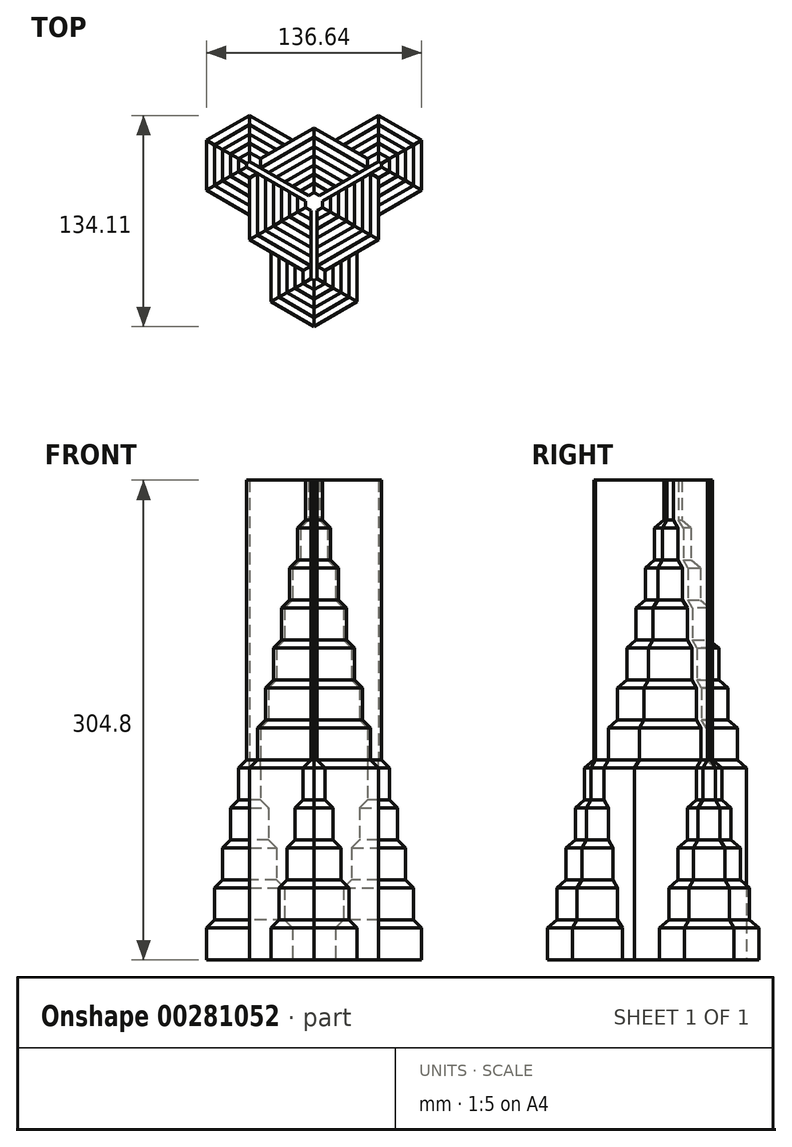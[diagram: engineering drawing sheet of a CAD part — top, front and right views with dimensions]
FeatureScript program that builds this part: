
annotation { "Feature Type Name" : "Feature", "Feature Type Description" : "" }
export const myFeature = defineFeature(function(context is Context, id is Id, definition is map)
    precondition{}
    {
        {
            var Q0;
            Q0=qCreatedBy(makeId("Top.planeOp"),FACE);
            var sketch = newSketch(context, id + "F0", { "sketchPlane" : qUnion([Q0])});
            skCircle(sketch, "E0.cCircle", {"center": v(0, 0) * mm, "radius": 41 * mm, "construction": true});
            skLineSegment(sketch, "E0.0", {"start": v(41, 23.67) * mm, "end": v(41, -23.67) * mm});
            skLineSegment(sketch, "E0.1", {"start": v(41, -23.67) * mm, "end": v(0, -47.33) * mm});
            skLineSegment(sketch, "E0.2", {"start": v(0, -47.33) * mm, "end": v(-41, -23.67) * mm});
            skLineSegment(sketch, "E0.3", {"start": v(-41, -23.67) * mm, "end": v(-41, 23.67) * mm});
            skLineSegment(sketch, "E0.4", {"start": v(-41, 23.67) * mm, "end": v(0, 47.33) * mm});
            skLineSegment(sketch, "E0.5", {"start": v(0, 47.33) * mm, "end": v(41, 23.67) * mm});
            skPoint(sketch, "E0.0.midPoint", {"position": v(41, 0) * mm});
            skCircle(sketch, "E1.cCircle", {"center": v(-41, 23.67) * mm, "radius": 27.33 * mm, "construction": true});
            skLineSegment(sketch, "E1.0", {"start": v(-13.66, 7.89) * mm, "end": v(-41, -7.89) * mm});
            skLineSegment(sketch, "E1.1", {"start": v(-41, -7.89) * mm, "end": v(-68.32, 7.89) * mm});
            skLineSegment(sketch, "E1.2", {"start": v(-68.32, 7.89) * mm, "end": v(-68.32, 39.44) * mm});
            skLineSegment(sketch, "E1.3", {"start": v(-68.32, 39.44) * mm, "end": v(-41, 55.22) * mm});
            skLineSegment(sketch, "E1.4", {"start": v(-41, 55.22) * mm, "end": v(-13.66, 39.44) * mm});
            skLineSegment(sketch, "E1.5", {"start": v(-13.66, 39.44) * mm, "end": v(-13.66, 7.89) * mm});
            skPoint(sketch, "E1.0.midPoint", {"position": v(-27.33, 0) * mm});
            skCircle(sketch, "E2.cCircle", {"center": v(41, 23.67) * mm, "radius": 27.33 * mm, "construction": true});
            skLineSegment(sketch, "E2.0", {"start": v(41, -7.89) * mm, "end": v(13.66, 7.89) * mm});
            skLineSegment(sketch, "E2.1", {"start": v(13.66, 7.89) * mm, "end": v(13.66, 39.44) * mm});
            skLineSegment(sketch, "E2.2", {"start": v(13.66, 39.44) * mm, "end": v(41, 55.22) * mm});
            skLineSegment(sketch, "E2.3", {"start": v(41, 55.22) * mm, "end": v(68.32, 39.44) * mm});
            skLineSegment(sketch, "E2.4", {"start": v(68.32, 39.44) * mm, "end": v(68.32, 7.89) * mm});
            skLineSegment(sketch, "E2.5", {"start": v(68.32, 7.89) * mm, "end": v(41, -7.89) * mm});
            skPoint(sketch, "E2.0.midPoint", {"position": v(27.33, 0) * mm});
            skCircle(sketch, "E3.cCircle", {"center": v(0, -47.33) * mm, "radius": 27.33 * mm, "construction": true});
            skLineSegment(sketch, "E3.0", {"start": v(0, -15.78) * mm, "end": v(27.33, -31.55) * mm});
            skLineSegment(sketch, "E3.1", {"start": v(27.33, -31.55) * mm, "end": v(27.33, -63.1) * mm});
            skLineSegment(sketch, "E3.2", {"start": v(27.33, -63.1) * mm, "end": v(0, -78.89) * mm});
            skLineSegment(sketch, "E3.3", {"start": v(0, -78.89) * mm, "end": v(-27.33, -63.1) * mm});
            skLineSegment(sketch, "E3.4", {"start": v(-27.33, -63.1) * mm, "end": v(-27.33, -31.55) * mm});
            skLineSegment(sketch, "E3.5", {"start": v(-27.33, -31.55) * mm, "end": v(0, -15.78) * mm});
            skPoint(sketch, "E3.0.midPoint", {"position": v(13.66, -23.67) * mm});
            skSolve(sketch);
        }
        {
            var Q0;
            Q0 = qSketchRegion(id + "F0", true);
            extrude(context, id + "F1", {"entities" : qUnion([Q0]), "depth" : 25.4 * mm});
        }
        {
            var Q0;
            Q0=makeQuery(id+"F1.opExtrude","CAP_EDGE",EDGE,{"disambiguationData":[OSD([sQuery(id+"F0.wireOp",EDGE,"E1.1")])],"isStart":false});
            var Q1;
            Q1=makeQuery(id+"F1.opExtrude","CAP_EDGE",EDGE,{"disambiguationData":[OSD([sQuery(id+"F0.wireOp",EDGE,"E3.4")])],"isStart":false});
            var Q2;
            Q2=makeQuery(id+"F1.opExtrude","CAP_EDGE",EDGE,{"disambiguationData":[OSD([sQuery(id+"F0.wireOp",EDGE,"E3.3")])],"isStart":false});
            var Q3;
            Q3=makeQuery(id+"F1.opExtrude","CAP_EDGE",EDGE,{"disambiguationData":[OSD([sQuery(id+"F0.wireOp",EDGE,"E3.2")])],"isStart":false});
            var Q4;
            Q4=makeQuery(id+"F1.opExtrude","CAP_EDGE",EDGE,{"disambiguationData":[OSD([sQuery(id+"F0.wireOp",EDGE,"E3.1")])],"isStart":false});
            var Q5;
            Q5=makeQuery(id+"F1.opExtrude","CAP_EDGE",EDGE,{"disambiguationData":[OSD([sQuery(id+"F0.wireOp",EDGE,"E2.5")])],"isStart":false});
            var Q6;
            Q6=makeQuery(id+"F1.opExtrude","CAP_EDGE",EDGE,{"disambiguationData":[OSD([sQuery(id+"F0.wireOp",EDGE,"E2.4")])],"isStart":false});
            var Q7;
            Q7=makeQuery(id+"F1.opExtrude","CAP_EDGE",EDGE,{"disambiguationData":[OSD([sQuery(id+"F0.wireOp",EDGE,"E2.3")])],"isStart":false});
            var Q8;
            Q8=makeQuery(id+"F1.opExtrude","CAP_EDGE",EDGE,{"disambiguationData":[OSD([sQuery(id+"F0.wireOp",EDGE,"E2.2")])],"isStart":false});
            var Q9;
            Q9=makeQuery(id+"F1.opExtrude","CAP_EDGE",EDGE,{"disambiguationData":[OSD([sQuery(id+"F0.wireOp",EDGE,"E1.4")])],"isStart":false});
            var Q10;
            Q10=makeQuery(id+"F1.opExtrude","CAP_EDGE",EDGE,{"disambiguationData":[OSD([sQuery(id+"F0.wireOp",EDGE,"E1.3")])],"isStart":false});
            var Q11;
            Q11=makeQuery(id+"F1.opExtrude","CAP_EDGE",EDGE,{"disambiguationData":[OSD([sQuery(id+"F0.wireOp",EDGE,"E1.2")])],"isStart":false});
            chamfer(context, id + "F2", {"entities" : qUnion([Q0, Q1, Q2, Q3, Q4, Q5, Q6, Q7, Q8, Q9, Q10, Q11]), "width" : 5.08 * mm, "tangentPropagation" : true});
        }
        {
            var Q0;
            Q0=makeQuery(id+"F1.opExtrude","CAP_FACE",FACE,{"disambiguationData":[OSD([sQuery(id+"F0.wireOp",EDGE,"E0.0"),sQuery(id+"F0.wireOp",EDGE,"E0.1"),sQuery(id+"F0.wireOp",EDGE,"E0.2"),sQuery(id+"F0.wireOp",EDGE,"E0.3"),sQuery(id+"F0.wireOp",EDGE,"E0.4"),sQuery(id+"F0.wireOp",EDGE,"E0.5"),sQuery(id+"F0.wireOp",EDGE,"E1.1"),sQuery(id+"F0.wireOp",EDGE,"E1.2"),sQuery(id+"F0.wireOp",EDGE,"E1.3"),sQuery(id+"F0.wireOp",EDGE,"E1.4"),sQuery(id+"F0.wireOp",EDGE,"E2.2"),sQuery(id+"F0.wireOp",EDGE,"E2.3"),sQuery(id+"F0.wireOp",EDGE,"E2.4"),sQuery(id+"F0.wireOp",EDGE,"E2.5"),sQuery(id+"F0.wireOp",EDGE,"E3.1"),sQuery(id+"F0.wireOp",EDGE,"E3.2"),sQuery(id+"F0.wireOp",EDGE,"E3.3"),sQuery(id+"F0.wireOp",EDGE,"E3.4")])],"isStart":false});
            extrude(context, id + "F3", {"entities" : qUnion([Q0]), "operationType" : NewBodyOperationType.ADD, "depth" : 25.4 * mm});
        }
        {
            var Q0;
            {var subQ0=sQuery(id+"F0.wireOp",EDGE,"E3.4");var subQ1=sQuery(id+"F0.wireOp",EDGE,"E3.3");var subQ2=sQuery(id+"F0.wireOp",EDGE,"E3.2");var subQ3=sQuery(id+"F0.wireOp",EDGE,"E3.1");var subQ4=sQuery(id+"F0.wireOp",EDGE,"E2.5");var subQ5=sQuery(id+"F0.wireOp",EDGE,"E2.4");var subQ6=sQuery(id+"F0.wireOp",EDGE,"E2.3");var subQ7=sQuery(id+"F0.wireOp",EDGE,"E2.2");var subQ8=sQuery(id+"F0.wireOp",EDGE,"E1.4");var subQ9=sQuery(id+"F0.wireOp",EDGE,"E1.3");var subQ10=sQuery(id+"F0.wireOp",EDGE,"E1.2");var subQ11=sQuery(id+"F0.wireOp",EDGE,"E1.1");var subQ12=sQuery(id+"F0.wireOp",EDGE,"E0.5");var subQ13=sQuery(id+"F0.wireOp",EDGE,"E0.4");var subQ14=sQuery(id+"F0.wireOp",EDGE,"E0.3");var subQ15=sQuery(id+"F0.wireOp",EDGE,"E0.2");var subQ16=sQuery(id+"F0.wireOp",EDGE,"E0.1");var subQ17=sQuery(id+"F0.wireOp",EDGE,"E0.0");Q0=makeQuery(id+"F3.opExtrude","CAP_EDGE",EDGE,{"disambiguationData":[OSD([subQ17,subQ16,subQ15,subQ14,subQ13,subQ12,subQ11,subQ10,subQ9,subQ8,subQ7,subQ6,subQ5,subQ4,subQ3,subQ2,subQ1,subQ0]),TDD([makeQuery(id+"F2.opChamfer","BLEND_EDGE",EDGE,{"blendedFrom":[makeQuery(id+"F1.opExtrude","CAP_EDGE",EDGE,{"disambiguationData":[OSD([subQ3])],"isStart":false}),makeQuery(id+"F1.opExtrude","CAP_FACE",FACE,{"disambiguationData":[OSD([subQ17,subQ16,subQ15,subQ14,subQ13,subQ12,subQ11,subQ10,subQ9,subQ8,subQ7,subQ6,subQ5,subQ4,subQ3,subQ2,subQ1,subQ0])],"isStart":false})],"blendedInto":[makeQuery(id+"F1.opExtrude","CAP_FACE",FACE,{"disambiguationData":[OSD([subQ17,subQ16,subQ15,subQ14,subQ13,subQ12,subQ11,subQ10,subQ9,subQ8,subQ7,subQ6,subQ5,subQ4,subQ3,subQ2,subQ1,subQ0])],"isStart":false})]})])],"isStart":false});}
            var Q1;
            {var subQ0=sQuery(id+"F0.wireOp",EDGE,"E3.4");var subQ1=sQuery(id+"F0.wireOp",EDGE,"E3.3");var subQ2=sQuery(id+"F0.wireOp",EDGE,"E3.2");var subQ3=sQuery(id+"F0.wireOp",EDGE,"E3.1");var subQ4=sQuery(id+"F0.wireOp",EDGE,"E2.5");var subQ5=sQuery(id+"F0.wireOp",EDGE,"E2.4");var subQ6=sQuery(id+"F0.wireOp",EDGE,"E2.3");var subQ7=sQuery(id+"F0.wireOp",EDGE,"E2.2");var subQ8=sQuery(id+"F0.wireOp",EDGE,"E1.4");var subQ9=sQuery(id+"F0.wireOp",EDGE,"E1.3");var subQ10=sQuery(id+"F0.wireOp",EDGE,"E1.2");var subQ11=sQuery(id+"F0.wireOp",EDGE,"E1.1");var subQ12=sQuery(id+"F0.wireOp",EDGE,"E0.5");var subQ13=sQuery(id+"F0.wireOp",EDGE,"E0.4");var subQ14=sQuery(id+"F0.wireOp",EDGE,"E0.3");var subQ15=sQuery(id+"F0.wireOp",EDGE,"E0.2");var subQ16=sQuery(id+"F0.wireOp",EDGE,"E0.1");var subQ17=sQuery(id+"F0.wireOp",EDGE,"E0.0");Q1=makeQuery(id+"F3.opExtrude","CAP_EDGE",EDGE,{"disambiguationData":[OSD([subQ17,subQ16,subQ15,subQ14,subQ13,subQ12,subQ11,subQ10,subQ9,subQ8,subQ7,subQ6,subQ5,subQ4,subQ3,subQ2,subQ1,subQ0]),TDD([makeQuery(id+"F2.opChamfer","BLEND_EDGE",EDGE,{"blendedFrom":[makeQuery(id+"F1.opExtrude","CAP_EDGE",EDGE,{"disambiguationData":[OSD([subQ2])],"isStart":false}),makeQuery(id+"F1.opExtrude","CAP_FACE",FACE,{"disambiguationData":[OSD([subQ17,subQ16,subQ15,subQ14,subQ13,subQ12,subQ11,subQ10,subQ9,subQ8,subQ7,subQ6,subQ5,subQ4,subQ3,subQ2,subQ1,subQ0])],"isStart":false})],"blendedInto":[makeQuery(id+"F1.opExtrude","CAP_FACE",FACE,{"disambiguationData":[OSD([subQ17,subQ16,subQ15,subQ14,subQ13,subQ12,subQ11,subQ10,subQ9,subQ8,subQ7,subQ6,subQ5,subQ4,subQ3,subQ2,subQ1,subQ0])],"isStart":false})]})])],"isStart":false});}
            var Q2;
            {var subQ0=sQuery(id+"F0.wireOp",EDGE,"E3.4");var subQ1=sQuery(id+"F0.wireOp",EDGE,"E3.3");var subQ2=sQuery(id+"F0.wireOp",EDGE,"E3.2");var subQ3=sQuery(id+"F0.wireOp",EDGE,"E3.1");var subQ4=sQuery(id+"F0.wireOp",EDGE,"E2.5");var subQ5=sQuery(id+"F0.wireOp",EDGE,"E2.4");var subQ6=sQuery(id+"F0.wireOp",EDGE,"E2.3");var subQ7=sQuery(id+"F0.wireOp",EDGE,"E2.2");var subQ8=sQuery(id+"F0.wireOp",EDGE,"E1.4");var subQ9=sQuery(id+"F0.wireOp",EDGE,"E1.3");var subQ10=sQuery(id+"F0.wireOp",EDGE,"E1.2");var subQ11=sQuery(id+"F0.wireOp",EDGE,"E1.1");var subQ12=sQuery(id+"F0.wireOp",EDGE,"E0.5");var subQ13=sQuery(id+"F0.wireOp",EDGE,"E0.4");var subQ14=sQuery(id+"F0.wireOp",EDGE,"E0.3");var subQ15=sQuery(id+"F0.wireOp",EDGE,"E0.2");var subQ16=sQuery(id+"F0.wireOp",EDGE,"E0.1");var subQ17=sQuery(id+"F0.wireOp",EDGE,"E0.0");Q2=makeQuery(id+"F3.opExtrude","CAP_EDGE",EDGE,{"disambiguationData":[OSD([subQ17,subQ16,subQ15,subQ14,subQ13,subQ12,subQ11,subQ10,subQ9,subQ8,subQ7,subQ6,subQ5,subQ4,subQ3,subQ2,subQ1,subQ0]),TDD([makeQuery(id+"F2.opChamfer","BLEND_EDGE",EDGE,{"blendedFrom":[makeQuery(id+"F1.opExtrude","CAP_EDGE",EDGE,{"disambiguationData":[OSD([subQ1])],"isStart":false}),makeQuery(id+"F1.opExtrude","CAP_FACE",FACE,{"disambiguationData":[OSD([subQ17,subQ16,subQ15,subQ14,subQ13,subQ12,subQ11,subQ10,subQ9,subQ8,subQ7,subQ6,subQ5,subQ4,subQ3,subQ2,subQ1,subQ0])],"isStart":false})],"blendedInto":[makeQuery(id+"F1.opExtrude","CAP_FACE",FACE,{"disambiguationData":[OSD([subQ17,subQ16,subQ15,subQ14,subQ13,subQ12,subQ11,subQ10,subQ9,subQ8,subQ7,subQ6,subQ5,subQ4,subQ3,subQ2,subQ1,subQ0])],"isStart":false})]})])],"isStart":false});}
            var Q3;
            {var subQ0=sQuery(id+"F0.wireOp",EDGE,"E3.4");var subQ1=sQuery(id+"F0.wireOp",EDGE,"E3.3");var subQ2=sQuery(id+"F0.wireOp",EDGE,"E3.2");var subQ3=sQuery(id+"F0.wireOp",EDGE,"E3.1");var subQ4=sQuery(id+"F0.wireOp",EDGE,"E2.5");var subQ5=sQuery(id+"F0.wireOp",EDGE,"E2.4");var subQ6=sQuery(id+"F0.wireOp",EDGE,"E2.3");var subQ7=sQuery(id+"F0.wireOp",EDGE,"E2.2");var subQ8=sQuery(id+"F0.wireOp",EDGE,"E1.4");var subQ9=sQuery(id+"F0.wireOp",EDGE,"E1.3");var subQ10=sQuery(id+"F0.wireOp",EDGE,"E1.2");var subQ11=sQuery(id+"F0.wireOp",EDGE,"E1.1");var subQ12=sQuery(id+"F0.wireOp",EDGE,"E0.5");var subQ13=sQuery(id+"F0.wireOp",EDGE,"E0.4");var subQ14=sQuery(id+"F0.wireOp",EDGE,"E0.3");var subQ15=sQuery(id+"F0.wireOp",EDGE,"E0.2");var subQ16=sQuery(id+"F0.wireOp",EDGE,"E0.1");var subQ17=sQuery(id+"F0.wireOp",EDGE,"E0.0");Q3=makeQuery(id+"F3.opExtrude","CAP_EDGE",EDGE,{"disambiguationData":[OSD([subQ17,subQ16,subQ15,subQ14,subQ13,subQ12,subQ11,subQ10,subQ9,subQ8,subQ7,subQ6,subQ5,subQ4,subQ3,subQ2,subQ1,subQ0]),TDD([makeQuery(id+"F2.opChamfer","BLEND_EDGE",EDGE,{"blendedFrom":[makeQuery(id+"F1.opExtrude","CAP_EDGE",EDGE,{"disambiguationData":[OSD([subQ0])],"isStart":false}),makeQuery(id+"F1.opExtrude","CAP_FACE",FACE,{"disambiguationData":[OSD([subQ17,subQ16,subQ15,subQ14,subQ13,subQ12,subQ11,subQ10,subQ9,subQ8,subQ7,subQ6,subQ5,subQ4,subQ3,subQ2,subQ1,subQ0])],"isStart":false})],"blendedInto":[makeQuery(id+"F1.opExtrude","CAP_FACE",FACE,{"disambiguationData":[OSD([subQ17,subQ16,subQ15,subQ14,subQ13,subQ12,subQ11,subQ10,subQ9,subQ8,subQ7,subQ6,subQ5,subQ4,subQ3,subQ2,subQ1,subQ0])],"isStart":false})]})])],"isStart":false});}
            var Q4;
            {var subQ0=sQuery(id+"F0.wireOp",EDGE,"E3.4");var subQ1=sQuery(id+"F0.wireOp",EDGE,"E3.3");var subQ2=sQuery(id+"F0.wireOp",EDGE,"E3.2");var subQ3=sQuery(id+"F0.wireOp",EDGE,"E3.1");var subQ4=sQuery(id+"F0.wireOp",EDGE,"E2.5");var subQ5=sQuery(id+"F0.wireOp",EDGE,"E2.4");var subQ6=sQuery(id+"F0.wireOp",EDGE,"E2.3");var subQ7=sQuery(id+"F0.wireOp",EDGE,"E2.2");var subQ8=sQuery(id+"F0.wireOp",EDGE,"E1.4");var subQ9=sQuery(id+"F0.wireOp",EDGE,"E1.3");var subQ10=sQuery(id+"F0.wireOp",EDGE,"E1.2");var subQ11=sQuery(id+"F0.wireOp",EDGE,"E1.1");var subQ12=sQuery(id+"F0.wireOp",EDGE,"E0.5");var subQ13=sQuery(id+"F0.wireOp",EDGE,"E0.4");var subQ14=sQuery(id+"F0.wireOp",EDGE,"E0.3");var subQ15=sQuery(id+"F0.wireOp",EDGE,"E0.2");var subQ16=sQuery(id+"F0.wireOp",EDGE,"E0.1");var subQ17=sQuery(id+"F0.wireOp",EDGE,"E0.0");Q4=makeQuery(id+"F3.opExtrude","CAP_EDGE",EDGE,{"disambiguationData":[OSD([subQ17,subQ16,subQ15,subQ14,subQ13,subQ12,subQ11,subQ10,subQ9,subQ8,subQ7,subQ6,subQ5,subQ4,subQ3,subQ2,subQ1,subQ0]),TDD([makeQuery(id+"F2.opChamfer","BLEND_EDGE",EDGE,{"blendedFrom":[makeQuery(id+"F1.opExtrude","CAP_EDGE",EDGE,{"disambiguationData":[OSD([subQ11])],"isStart":false}),makeQuery(id+"F1.opExtrude","CAP_FACE",FACE,{"disambiguationData":[OSD([subQ17,subQ16,subQ15,subQ14,subQ13,subQ12,subQ11,subQ10,subQ9,subQ8,subQ7,subQ6,subQ5,subQ4,subQ3,subQ2,subQ1,subQ0])],"isStart":false})],"blendedInto":[makeQuery(id+"F1.opExtrude","CAP_FACE",FACE,{"disambiguationData":[OSD([subQ17,subQ16,subQ15,subQ14,subQ13,subQ12,subQ11,subQ10,subQ9,subQ8,subQ7,subQ6,subQ5,subQ4,subQ3,subQ2,subQ1,subQ0])],"isStart":false})]})])],"isStart":false});}
            var Q5;
            {var subQ0=sQuery(id+"F0.wireOp",EDGE,"E3.4");var subQ1=sQuery(id+"F0.wireOp",EDGE,"E3.3");var subQ2=sQuery(id+"F0.wireOp",EDGE,"E3.2");var subQ3=sQuery(id+"F0.wireOp",EDGE,"E3.1");var subQ4=sQuery(id+"F0.wireOp",EDGE,"E2.5");var subQ5=sQuery(id+"F0.wireOp",EDGE,"E2.4");var subQ6=sQuery(id+"F0.wireOp",EDGE,"E2.3");var subQ7=sQuery(id+"F0.wireOp",EDGE,"E2.2");var subQ8=sQuery(id+"F0.wireOp",EDGE,"E1.4");var subQ9=sQuery(id+"F0.wireOp",EDGE,"E1.3");var subQ10=sQuery(id+"F0.wireOp",EDGE,"E1.2");var subQ11=sQuery(id+"F0.wireOp",EDGE,"E1.1");var subQ12=sQuery(id+"F0.wireOp",EDGE,"E0.5");var subQ13=sQuery(id+"F0.wireOp",EDGE,"E0.4");var subQ14=sQuery(id+"F0.wireOp",EDGE,"E0.3");var subQ15=sQuery(id+"F0.wireOp",EDGE,"E0.2");var subQ16=sQuery(id+"F0.wireOp",EDGE,"E0.1");var subQ17=sQuery(id+"F0.wireOp",EDGE,"E0.0");Q5=makeQuery(id+"F3.opExtrude","CAP_EDGE",EDGE,{"disambiguationData":[OSD([subQ17,subQ16,subQ15,subQ14,subQ13,subQ12,subQ11,subQ10,subQ9,subQ8,subQ7,subQ6,subQ5,subQ4,subQ3,subQ2,subQ1,subQ0]),TDD([makeQuery(id+"F2.opChamfer","BLEND_EDGE",EDGE,{"blendedFrom":[makeQuery(id+"F1.opExtrude","CAP_EDGE",EDGE,{"disambiguationData":[OSD([subQ10])],"isStart":false}),makeQuery(id+"F1.opExtrude","CAP_FACE",FACE,{"disambiguationData":[OSD([subQ17,subQ16,subQ15,subQ14,subQ13,subQ12,subQ11,subQ10,subQ9,subQ8,subQ7,subQ6,subQ5,subQ4,subQ3,subQ2,subQ1,subQ0])],"isStart":false})],"blendedInto":[makeQuery(id+"F1.opExtrude","CAP_FACE",FACE,{"disambiguationData":[OSD([subQ17,subQ16,subQ15,subQ14,subQ13,subQ12,subQ11,subQ10,subQ9,subQ8,subQ7,subQ6,subQ5,subQ4,subQ3,subQ2,subQ1,subQ0])],"isStart":false})]})])],"isStart":false});}
            var Q6;
            {var subQ0=sQuery(id+"F0.wireOp",EDGE,"E3.4");var subQ1=sQuery(id+"F0.wireOp",EDGE,"E3.3");var subQ2=sQuery(id+"F0.wireOp",EDGE,"E3.2");var subQ3=sQuery(id+"F0.wireOp",EDGE,"E3.1");var subQ4=sQuery(id+"F0.wireOp",EDGE,"E2.5");var subQ5=sQuery(id+"F0.wireOp",EDGE,"E2.4");var subQ6=sQuery(id+"F0.wireOp",EDGE,"E2.3");var subQ7=sQuery(id+"F0.wireOp",EDGE,"E2.2");var subQ8=sQuery(id+"F0.wireOp",EDGE,"E1.4");var subQ9=sQuery(id+"F0.wireOp",EDGE,"E1.3");var subQ10=sQuery(id+"F0.wireOp",EDGE,"E1.2");var subQ11=sQuery(id+"F0.wireOp",EDGE,"E1.1");var subQ12=sQuery(id+"F0.wireOp",EDGE,"E0.5");var subQ13=sQuery(id+"F0.wireOp",EDGE,"E0.4");var subQ14=sQuery(id+"F0.wireOp",EDGE,"E0.3");var subQ15=sQuery(id+"F0.wireOp",EDGE,"E0.2");var subQ16=sQuery(id+"F0.wireOp",EDGE,"E0.1");var subQ17=sQuery(id+"F0.wireOp",EDGE,"E0.0");Q6=makeQuery(id+"F3.opExtrude","CAP_EDGE",EDGE,{"disambiguationData":[OSD([subQ17,subQ16,subQ15,subQ14,subQ13,subQ12,subQ11,subQ10,subQ9,subQ8,subQ7,subQ6,subQ5,subQ4,subQ3,subQ2,subQ1,subQ0]),TDD([makeQuery(id+"F2.opChamfer","BLEND_EDGE",EDGE,{"blendedFrom":[makeQuery(id+"F1.opExtrude","CAP_EDGE",EDGE,{"disambiguationData":[OSD([subQ9])],"isStart":false}),makeQuery(id+"F1.opExtrude","CAP_FACE",FACE,{"disambiguationData":[OSD([subQ17,subQ16,subQ15,subQ14,subQ13,subQ12,subQ11,subQ10,subQ9,subQ8,subQ7,subQ6,subQ5,subQ4,subQ3,subQ2,subQ1,subQ0])],"isStart":false})],"blendedInto":[makeQuery(id+"F1.opExtrude","CAP_FACE",FACE,{"disambiguationData":[OSD([subQ17,subQ16,subQ15,subQ14,subQ13,subQ12,subQ11,subQ10,subQ9,subQ8,subQ7,subQ6,subQ5,subQ4,subQ3,subQ2,subQ1,subQ0])],"isStart":false})]})])],"isStart":false});}
            var Q7;
            {var subQ0=sQuery(id+"F0.wireOp",EDGE,"E3.4");var subQ1=sQuery(id+"F0.wireOp",EDGE,"E3.3");var subQ2=sQuery(id+"F0.wireOp",EDGE,"E3.2");var subQ3=sQuery(id+"F0.wireOp",EDGE,"E3.1");var subQ4=sQuery(id+"F0.wireOp",EDGE,"E2.5");var subQ5=sQuery(id+"F0.wireOp",EDGE,"E2.4");var subQ6=sQuery(id+"F0.wireOp",EDGE,"E2.3");var subQ7=sQuery(id+"F0.wireOp",EDGE,"E2.2");var subQ8=sQuery(id+"F0.wireOp",EDGE,"E1.4");var subQ9=sQuery(id+"F0.wireOp",EDGE,"E1.3");var subQ10=sQuery(id+"F0.wireOp",EDGE,"E1.2");var subQ11=sQuery(id+"F0.wireOp",EDGE,"E1.1");var subQ12=sQuery(id+"F0.wireOp",EDGE,"E0.5");var subQ13=sQuery(id+"F0.wireOp",EDGE,"E0.4");var subQ14=sQuery(id+"F0.wireOp",EDGE,"E0.3");var subQ15=sQuery(id+"F0.wireOp",EDGE,"E0.2");var subQ16=sQuery(id+"F0.wireOp",EDGE,"E0.1");var subQ17=sQuery(id+"F0.wireOp",EDGE,"E0.0");Q7=makeQuery(id+"F3.opExtrude","CAP_EDGE",EDGE,{"disambiguationData":[OSD([subQ17,subQ16,subQ15,subQ14,subQ13,subQ12,subQ11,subQ10,subQ9,subQ8,subQ7,subQ6,subQ5,subQ4,subQ3,subQ2,subQ1,subQ0]),TDD([makeQuery(id+"F2.opChamfer","BLEND_EDGE",EDGE,{"blendedFrom":[makeQuery(id+"F1.opExtrude","CAP_EDGE",EDGE,{"disambiguationData":[OSD([subQ8])],"isStart":false}),makeQuery(id+"F1.opExtrude","CAP_FACE",FACE,{"disambiguationData":[OSD([subQ17,subQ16,subQ15,subQ14,subQ13,subQ12,subQ11,subQ10,subQ9,subQ8,subQ7,subQ6,subQ5,subQ4,subQ3,subQ2,subQ1,subQ0])],"isStart":false})],"blendedInto":[makeQuery(id+"F1.opExtrude","CAP_FACE",FACE,{"disambiguationData":[OSD([subQ17,subQ16,subQ15,subQ14,subQ13,subQ12,subQ11,subQ10,subQ9,subQ8,subQ7,subQ6,subQ5,subQ4,subQ3,subQ2,subQ1,subQ0])],"isStart":false})]})])],"isStart":false});}
            var Q8;
            {var subQ0=sQuery(id+"F0.wireOp",EDGE,"E3.4");var subQ1=sQuery(id+"F0.wireOp",EDGE,"E3.3");var subQ2=sQuery(id+"F0.wireOp",EDGE,"E3.2");var subQ3=sQuery(id+"F0.wireOp",EDGE,"E3.1");var subQ4=sQuery(id+"F0.wireOp",EDGE,"E2.5");var subQ5=sQuery(id+"F0.wireOp",EDGE,"E2.4");var subQ6=sQuery(id+"F0.wireOp",EDGE,"E2.3");var subQ7=sQuery(id+"F0.wireOp",EDGE,"E2.2");var subQ8=sQuery(id+"F0.wireOp",EDGE,"E1.4");var subQ9=sQuery(id+"F0.wireOp",EDGE,"E1.3");var subQ10=sQuery(id+"F0.wireOp",EDGE,"E1.2");var subQ11=sQuery(id+"F0.wireOp",EDGE,"E1.1");var subQ12=sQuery(id+"F0.wireOp",EDGE,"E0.5");var subQ13=sQuery(id+"F0.wireOp",EDGE,"E0.4");var subQ14=sQuery(id+"F0.wireOp",EDGE,"E0.3");var subQ15=sQuery(id+"F0.wireOp",EDGE,"E0.2");var subQ16=sQuery(id+"F0.wireOp",EDGE,"E0.1");var subQ17=sQuery(id+"F0.wireOp",EDGE,"E0.0");Q8=makeQuery(id+"F3.opExtrude","CAP_EDGE",EDGE,{"disambiguationData":[OSD([subQ17,subQ16,subQ15,subQ14,subQ13,subQ12,subQ11,subQ10,subQ9,subQ8,subQ7,subQ6,subQ5,subQ4,subQ3,subQ2,subQ1,subQ0]),TDD([makeQuery(id+"F2.opChamfer","BLEND_EDGE",EDGE,{"blendedFrom":[makeQuery(id+"F1.opExtrude","CAP_EDGE",EDGE,{"disambiguationData":[OSD([subQ7])],"isStart":false}),makeQuery(id+"F1.opExtrude","CAP_FACE",FACE,{"disambiguationData":[OSD([subQ17,subQ16,subQ15,subQ14,subQ13,subQ12,subQ11,subQ10,subQ9,subQ8,subQ7,subQ6,subQ5,subQ4,subQ3,subQ2,subQ1,subQ0])],"isStart":false})],"blendedInto":[makeQuery(id+"F1.opExtrude","CAP_FACE",FACE,{"disambiguationData":[OSD([subQ17,subQ16,subQ15,subQ14,subQ13,subQ12,subQ11,subQ10,subQ9,subQ8,subQ7,subQ6,subQ5,subQ4,subQ3,subQ2,subQ1,subQ0])],"isStart":false})]})])],"isStart":false});}
            var Q9;
            {var subQ0=sQuery(id+"F0.wireOp",EDGE,"E3.4");var subQ1=sQuery(id+"F0.wireOp",EDGE,"E3.3");var subQ2=sQuery(id+"F0.wireOp",EDGE,"E3.2");var subQ3=sQuery(id+"F0.wireOp",EDGE,"E3.1");var subQ4=sQuery(id+"F0.wireOp",EDGE,"E2.5");var subQ5=sQuery(id+"F0.wireOp",EDGE,"E2.4");var subQ6=sQuery(id+"F0.wireOp",EDGE,"E2.3");var subQ7=sQuery(id+"F0.wireOp",EDGE,"E2.2");var subQ8=sQuery(id+"F0.wireOp",EDGE,"E1.4");var subQ9=sQuery(id+"F0.wireOp",EDGE,"E1.3");var subQ10=sQuery(id+"F0.wireOp",EDGE,"E1.2");var subQ11=sQuery(id+"F0.wireOp",EDGE,"E1.1");var subQ12=sQuery(id+"F0.wireOp",EDGE,"E0.5");var subQ13=sQuery(id+"F0.wireOp",EDGE,"E0.4");var subQ14=sQuery(id+"F0.wireOp",EDGE,"E0.3");var subQ15=sQuery(id+"F0.wireOp",EDGE,"E0.2");var subQ16=sQuery(id+"F0.wireOp",EDGE,"E0.1");var subQ17=sQuery(id+"F0.wireOp",EDGE,"E0.0");Q9=makeQuery(id+"F3.opExtrude","CAP_EDGE",EDGE,{"disambiguationData":[OSD([subQ17,subQ16,subQ15,subQ14,subQ13,subQ12,subQ11,subQ10,subQ9,subQ8,subQ7,subQ6,subQ5,subQ4,subQ3,subQ2,subQ1,subQ0]),TDD([makeQuery(id+"F2.opChamfer","BLEND_EDGE",EDGE,{"blendedFrom":[makeQuery(id+"F1.opExtrude","CAP_EDGE",EDGE,{"disambiguationData":[OSD([subQ6])],"isStart":false}),makeQuery(id+"F1.opExtrude","CAP_FACE",FACE,{"disambiguationData":[OSD([subQ17,subQ16,subQ15,subQ14,subQ13,subQ12,subQ11,subQ10,subQ9,subQ8,subQ7,subQ6,subQ5,subQ4,subQ3,subQ2,subQ1,subQ0])],"isStart":false})],"blendedInto":[makeQuery(id+"F1.opExtrude","CAP_FACE",FACE,{"disambiguationData":[OSD([subQ17,subQ16,subQ15,subQ14,subQ13,subQ12,subQ11,subQ10,subQ9,subQ8,subQ7,subQ6,subQ5,subQ4,subQ3,subQ2,subQ1,subQ0])],"isStart":false})]})])],"isStart":false});}
            var Q10;
            {var subQ0=sQuery(id+"F0.wireOp",EDGE,"E3.4");var subQ1=sQuery(id+"F0.wireOp",EDGE,"E3.3");var subQ2=sQuery(id+"F0.wireOp",EDGE,"E3.2");var subQ3=sQuery(id+"F0.wireOp",EDGE,"E3.1");var subQ4=sQuery(id+"F0.wireOp",EDGE,"E2.5");var subQ5=sQuery(id+"F0.wireOp",EDGE,"E2.4");var subQ6=sQuery(id+"F0.wireOp",EDGE,"E2.3");var subQ7=sQuery(id+"F0.wireOp",EDGE,"E2.2");var subQ8=sQuery(id+"F0.wireOp",EDGE,"E1.4");var subQ9=sQuery(id+"F0.wireOp",EDGE,"E1.3");var subQ10=sQuery(id+"F0.wireOp",EDGE,"E1.2");var subQ11=sQuery(id+"F0.wireOp",EDGE,"E1.1");var subQ12=sQuery(id+"F0.wireOp",EDGE,"E0.5");var subQ13=sQuery(id+"F0.wireOp",EDGE,"E0.4");var subQ14=sQuery(id+"F0.wireOp",EDGE,"E0.3");var subQ15=sQuery(id+"F0.wireOp",EDGE,"E0.2");var subQ16=sQuery(id+"F0.wireOp",EDGE,"E0.1");var subQ17=sQuery(id+"F0.wireOp",EDGE,"E0.0");Q10=makeQuery(id+"F3.opExtrude","CAP_EDGE",EDGE,{"disambiguationData":[OSD([subQ17,subQ16,subQ15,subQ14,subQ13,subQ12,subQ11,subQ10,subQ9,subQ8,subQ7,subQ6,subQ5,subQ4,subQ3,subQ2,subQ1,subQ0]),TDD([makeQuery(id+"F2.opChamfer","BLEND_EDGE",EDGE,{"blendedFrom":[makeQuery(id+"F1.opExtrude","CAP_EDGE",EDGE,{"disambiguationData":[OSD([subQ5])],"isStart":false}),makeQuery(id+"F1.opExtrude","CAP_FACE",FACE,{"disambiguationData":[OSD([subQ17,subQ16,subQ15,subQ14,subQ13,subQ12,subQ11,subQ10,subQ9,subQ8,subQ7,subQ6,subQ5,subQ4,subQ3,subQ2,subQ1,subQ0])],"isStart":false})],"blendedInto":[makeQuery(id+"F1.opExtrude","CAP_FACE",FACE,{"disambiguationData":[OSD([subQ17,subQ16,subQ15,subQ14,subQ13,subQ12,subQ11,subQ10,subQ9,subQ8,subQ7,subQ6,subQ5,subQ4,subQ3,subQ2,subQ1,subQ0])],"isStart":false})]})])],"isStart":false});}
            var Q11;
            {var subQ0=sQuery(id+"F0.wireOp",EDGE,"E3.4");var subQ1=sQuery(id+"F0.wireOp",EDGE,"E3.3");var subQ2=sQuery(id+"F0.wireOp",EDGE,"E3.2");var subQ3=sQuery(id+"F0.wireOp",EDGE,"E3.1");var subQ4=sQuery(id+"F0.wireOp",EDGE,"E2.5");var subQ5=sQuery(id+"F0.wireOp",EDGE,"E2.4");var subQ6=sQuery(id+"F0.wireOp",EDGE,"E2.3");var subQ7=sQuery(id+"F0.wireOp",EDGE,"E2.2");var subQ8=sQuery(id+"F0.wireOp",EDGE,"E1.4");var subQ9=sQuery(id+"F0.wireOp",EDGE,"E1.3");var subQ10=sQuery(id+"F0.wireOp",EDGE,"E1.2");var subQ11=sQuery(id+"F0.wireOp",EDGE,"E1.1");var subQ12=sQuery(id+"F0.wireOp",EDGE,"E0.5");var subQ13=sQuery(id+"F0.wireOp",EDGE,"E0.4");var subQ14=sQuery(id+"F0.wireOp",EDGE,"E0.3");var subQ15=sQuery(id+"F0.wireOp",EDGE,"E0.2");var subQ16=sQuery(id+"F0.wireOp",EDGE,"E0.1");var subQ17=sQuery(id+"F0.wireOp",EDGE,"E0.0");Q11=makeQuery(id+"F3.opExtrude","CAP_EDGE",EDGE,{"disambiguationData":[OSD([subQ17,subQ16,subQ15,subQ14,subQ13,subQ12,subQ11,subQ10,subQ9,subQ8,subQ7,subQ6,subQ5,subQ4,subQ3,subQ2,subQ1,subQ0]),TDD([makeQuery(id+"F2.opChamfer","BLEND_EDGE",EDGE,{"blendedFrom":[makeQuery(id+"F1.opExtrude","CAP_EDGE",EDGE,{"disambiguationData":[OSD([subQ4])],"isStart":false}),makeQuery(id+"F1.opExtrude","CAP_FACE",FACE,{"disambiguationData":[OSD([subQ17,subQ16,subQ15,subQ14,subQ13,subQ12,subQ11,subQ10,subQ9,subQ8,subQ7,subQ6,subQ5,subQ4,subQ3,subQ2,subQ1,subQ0])],"isStart":false})],"blendedInto":[makeQuery(id+"F1.opExtrude","CAP_FACE",FACE,{"disambiguationData":[OSD([subQ17,subQ16,subQ15,subQ14,subQ13,subQ12,subQ11,subQ10,subQ9,subQ8,subQ7,subQ6,subQ5,subQ4,subQ3,subQ2,subQ1,subQ0])],"isStart":false})]})])],"isStart":false});}
            chamfer(context, id + "F4", {"entities" : qUnion([Q0, Q1, Q2, Q3, Q4, Q5, Q6, Q7, Q8, Q9, Q10, Q11]), "width" : 5.08 * mm, "tangentPropagation" : true});
        }
        {
            var Q0;
            Q0=makeQuery(id+"F3.opExtrude","CAP_FACE",FACE,{"disambiguationData":[OSD([sQuery(id+"F0.wireOp",EDGE,"E0.0"),sQuery(id+"F0.wireOp",EDGE,"E0.1"),sQuery(id+"F0.wireOp",EDGE,"E0.2"),sQuery(id+"F0.wireOp",EDGE,"E0.3"),sQuery(id+"F0.wireOp",EDGE,"E0.4"),sQuery(id+"F0.wireOp",EDGE,"E0.5"),sQuery(id+"F0.wireOp",EDGE,"E1.1"),sQuery(id+"F0.wireOp",EDGE,"E1.2"),sQuery(id+"F0.wireOp",EDGE,"E1.3"),sQuery(id+"F0.wireOp",EDGE,"E1.4"),sQuery(id+"F0.wireOp",EDGE,"E2.2"),sQuery(id+"F0.wireOp",EDGE,"E2.3"),sQuery(id+"F0.wireOp",EDGE,"E2.4"),sQuery(id+"F0.wireOp",EDGE,"E2.5"),sQuery(id+"F0.wireOp",EDGE,"E3.1"),sQuery(id+"F0.wireOp",EDGE,"E3.2"),sQuery(id+"F0.wireOp",EDGE,"E3.3"),sQuery(id+"F0.wireOp",EDGE,"E3.4")])],"isStart":false});
            extrude(context, id + "F5", {"entities" : qUnion([Q0]), "operationType" : NewBodyOperationType.ADD, "depth" : 25.4 * mm});
        }
        {
            var Q0;
            {var subQ0=sQuery(id+"F0.wireOp",EDGE,"E3.4");var subQ1=sQuery(id+"F0.wireOp",EDGE,"E3.3");var subQ2=sQuery(id+"F0.wireOp",EDGE,"E3.2");var subQ3=sQuery(id+"F0.wireOp",EDGE,"E3.1");var subQ4=sQuery(id+"F0.wireOp",EDGE,"E2.5");var subQ5=sQuery(id+"F0.wireOp",EDGE,"E2.4");var subQ6=sQuery(id+"F0.wireOp",EDGE,"E2.3");var subQ7=sQuery(id+"F0.wireOp",EDGE,"E2.2");var subQ8=sQuery(id+"F0.wireOp",EDGE,"E1.4");var subQ9=sQuery(id+"F0.wireOp",EDGE,"E1.3");var subQ10=sQuery(id+"F0.wireOp",EDGE,"E1.2");var subQ11=sQuery(id+"F0.wireOp",EDGE,"E1.1");var subQ12=sQuery(id+"F0.wireOp",EDGE,"E0.5");var subQ13=sQuery(id+"F0.wireOp",EDGE,"E0.4");var subQ14=sQuery(id+"F0.wireOp",EDGE,"E0.3");var subQ15=sQuery(id+"F0.wireOp",EDGE,"E0.2");var subQ16=sQuery(id+"F0.wireOp",EDGE,"E0.1");var subQ17=sQuery(id+"F0.wireOp",EDGE,"E0.0");Q0=makeQuery(id+"F5.opExtrude","CAP_EDGE",EDGE,{"disambiguationData":[OSD([subQ17,subQ16,subQ15,subQ14,subQ13,subQ12,subQ11,subQ10,subQ9,subQ8,subQ7,subQ6,subQ5,subQ4,subQ3,subQ2,subQ1,subQ0]),TDD([makeQuery(id+"F4.opChamfer","BLEND_EDGE",EDGE,{"blendedFrom":[makeQuery(id+"F3.opExtrude","CAP_EDGE",EDGE,{"disambiguationData":[OSD([subQ17,subQ16,subQ15,subQ14,subQ13,subQ12,subQ11,subQ10,subQ9,subQ8,subQ7,subQ6,subQ5,subQ4,subQ3,subQ2,subQ1,subQ0]),TDD([makeQuery(id+"F2.opChamfer","BLEND_EDGE",EDGE,{"blendedFrom":[makeQuery(id+"F1.opExtrude","CAP_EDGE",EDGE,{"disambiguationData":[OSD([subQ8])],"isStart":false}),makeQuery(id+"F1.opExtrude","CAP_FACE",FACE,{"disambiguationData":[OSD([subQ17,subQ16,subQ15,subQ14,subQ13,subQ12,subQ11,subQ10,subQ9,subQ8,subQ7,subQ6,subQ5,subQ4,subQ3,subQ2,subQ1,subQ0])],"isStart":false})],"blendedInto":[makeQuery(id+"F1.opExtrude","CAP_FACE",FACE,{"disambiguationData":[OSD([subQ17,subQ16,subQ15,subQ14,subQ13,subQ12,subQ11,subQ10,subQ9,subQ8,subQ7,subQ6,subQ5,subQ4,subQ3,subQ2,subQ1,subQ0])],"isStart":false})]})])],"isStart":false}),makeQuery(id+"F3.opExtrude","CAP_FACE",FACE,{"disambiguationData":[OSD([subQ17,subQ16,subQ15,subQ14,subQ13,subQ12,subQ11,subQ10,subQ9,subQ8,subQ7,subQ6,subQ5,subQ4,subQ3,subQ2,subQ1,subQ0])],"isStart":false})],"blendedInto":[makeQuery(id+"F3.opExtrude","CAP_FACE",FACE,{"disambiguationData":[OSD([subQ17,subQ16,subQ15,subQ14,subQ13,subQ12,subQ11,subQ10,subQ9,subQ8,subQ7,subQ6,subQ5,subQ4,subQ3,subQ2,subQ1,subQ0])],"isStart":false})]})])],"isStart":false});}
            var Q1;
            {var subQ0=sQuery(id+"F0.wireOp",EDGE,"E3.4");var subQ1=sQuery(id+"F0.wireOp",EDGE,"E3.3");var subQ2=sQuery(id+"F0.wireOp",EDGE,"E3.2");var subQ3=sQuery(id+"F0.wireOp",EDGE,"E3.1");var subQ4=sQuery(id+"F0.wireOp",EDGE,"E2.5");var subQ5=sQuery(id+"F0.wireOp",EDGE,"E2.4");var subQ6=sQuery(id+"F0.wireOp",EDGE,"E2.3");var subQ7=sQuery(id+"F0.wireOp",EDGE,"E2.2");var subQ8=sQuery(id+"F0.wireOp",EDGE,"E1.4");var subQ9=sQuery(id+"F0.wireOp",EDGE,"E1.3");var subQ10=sQuery(id+"F0.wireOp",EDGE,"E1.2");var subQ11=sQuery(id+"F0.wireOp",EDGE,"E1.1");var subQ12=sQuery(id+"F0.wireOp",EDGE,"E0.5");var subQ13=sQuery(id+"F0.wireOp",EDGE,"E0.4");var subQ14=sQuery(id+"F0.wireOp",EDGE,"E0.3");var subQ15=sQuery(id+"F0.wireOp",EDGE,"E0.2");var subQ16=sQuery(id+"F0.wireOp",EDGE,"E0.1");var subQ17=sQuery(id+"F0.wireOp",EDGE,"E0.0");Q1=makeQuery(id+"F5.opExtrude","CAP_EDGE",EDGE,{"disambiguationData":[OSD([subQ17,subQ16,subQ15,subQ14,subQ13,subQ12,subQ11,subQ10,subQ9,subQ8,subQ7,subQ6,subQ5,subQ4,subQ3,subQ2,subQ1,subQ0]),TDD([makeQuery(id+"F4.opChamfer","BLEND_EDGE",EDGE,{"blendedFrom":[makeQuery(id+"F3.opExtrude","CAP_EDGE",EDGE,{"disambiguationData":[OSD([subQ17,subQ16,subQ15,subQ14,subQ13,subQ12,subQ11,subQ10,subQ9,subQ8,subQ7,subQ6,subQ5,subQ4,subQ3,subQ2,subQ1,subQ0]),TDD([makeQuery(id+"F2.opChamfer","BLEND_EDGE",EDGE,{"blendedFrom":[makeQuery(id+"F1.opExtrude","CAP_EDGE",EDGE,{"disambiguationData":[OSD([subQ9])],"isStart":false}),makeQuery(id+"F1.opExtrude","CAP_FACE",FACE,{"disambiguationData":[OSD([subQ17,subQ16,subQ15,subQ14,subQ13,subQ12,subQ11,subQ10,subQ9,subQ8,subQ7,subQ6,subQ5,subQ4,subQ3,subQ2,subQ1,subQ0])],"isStart":false})],"blendedInto":[makeQuery(id+"F1.opExtrude","CAP_FACE",FACE,{"disambiguationData":[OSD([subQ17,subQ16,subQ15,subQ14,subQ13,subQ12,subQ11,subQ10,subQ9,subQ8,subQ7,subQ6,subQ5,subQ4,subQ3,subQ2,subQ1,subQ0])],"isStart":false})]})])],"isStart":false}),makeQuery(id+"F3.opExtrude","CAP_FACE",FACE,{"disambiguationData":[OSD([subQ17,subQ16,subQ15,subQ14,subQ13,subQ12,subQ11,subQ10,subQ9,subQ8,subQ7,subQ6,subQ5,subQ4,subQ3,subQ2,subQ1,subQ0])],"isStart":false})],"blendedInto":[makeQuery(id+"F3.opExtrude","CAP_FACE",FACE,{"disambiguationData":[OSD([subQ17,subQ16,subQ15,subQ14,subQ13,subQ12,subQ11,subQ10,subQ9,subQ8,subQ7,subQ6,subQ5,subQ4,subQ3,subQ2,subQ1,subQ0])],"isStart":false})]})])],"isStart":false});}
            var Q2;
            {var subQ0=sQuery(id+"F0.wireOp",EDGE,"E3.4");var subQ1=sQuery(id+"F0.wireOp",EDGE,"E3.3");var subQ2=sQuery(id+"F0.wireOp",EDGE,"E3.2");var subQ3=sQuery(id+"F0.wireOp",EDGE,"E3.1");var subQ4=sQuery(id+"F0.wireOp",EDGE,"E2.5");var subQ5=sQuery(id+"F0.wireOp",EDGE,"E2.4");var subQ6=sQuery(id+"F0.wireOp",EDGE,"E2.3");var subQ7=sQuery(id+"F0.wireOp",EDGE,"E2.2");var subQ8=sQuery(id+"F0.wireOp",EDGE,"E1.4");var subQ9=sQuery(id+"F0.wireOp",EDGE,"E1.3");var subQ10=sQuery(id+"F0.wireOp",EDGE,"E1.2");var subQ11=sQuery(id+"F0.wireOp",EDGE,"E1.1");var subQ12=sQuery(id+"F0.wireOp",EDGE,"E0.5");var subQ13=sQuery(id+"F0.wireOp",EDGE,"E0.4");var subQ14=sQuery(id+"F0.wireOp",EDGE,"E0.3");var subQ15=sQuery(id+"F0.wireOp",EDGE,"E0.2");var subQ16=sQuery(id+"F0.wireOp",EDGE,"E0.1");var subQ17=sQuery(id+"F0.wireOp",EDGE,"E0.0");Q2=makeQuery(id+"F5.opExtrude","CAP_EDGE",EDGE,{"disambiguationData":[OSD([subQ17,subQ16,subQ15,subQ14,subQ13,subQ12,subQ11,subQ10,subQ9,subQ8,subQ7,subQ6,subQ5,subQ4,subQ3,subQ2,subQ1,subQ0]),TDD([makeQuery(id+"F4.opChamfer","BLEND_EDGE",EDGE,{"blendedFrom":[makeQuery(id+"F3.opExtrude","CAP_EDGE",EDGE,{"disambiguationData":[OSD([subQ17,subQ16,subQ15,subQ14,subQ13,subQ12,subQ11,subQ10,subQ9,subQ8,subQ7,subQ6,subQ5,subQ4,subQ3,subQ2,subQ1,subQ0]),TDD([makeQuery(id+"F2.opChamfer","BLEND_EDGE",EDGE,{"blendedFrom":[makeQuery(id+"F1.opExtrude","CAP_EDGE",EDGE,{"disambiguationData":[OSD([subQ10])],"isStart":false}),makeQuery(id+"F1.opExtrude","CAP_FACE",FACE,{"disambiguationData":[OSD([subQ17,subQ16,subQ15,subQ14,subQ13,subQ12,subQ11,subQ10,subQ9,subQ8,subQ7,subQ6,subQ5,subQ4,subQ3,subQ2,subQ1,subQ0])],"isStart":false})],"blendedInto":[makeQuery(id+"F1.opExtrude","CAP_FACE",FACE,{"disambiguationData":[OSD([subQ17,subQ16,subQ15,subQ14,subQ13,subQ12,subQ11,subQ10,subQ9,subQ8,subQ7,subQ6,subQ5,subQ4,subQ3,subQ2,subQ1,subQ0])],"isStart":false})]})])],"isStart":false}),makeQuery(id+"F3.opExtrude","CAP_FACE",FACE,{"disambiguationData":[OSD([subQ17,subQ16,subQ15,subQ14,subQ13,subQ12,subQ11,subQ10,subQ9,subQ8,subQ7,subQ6,subQ5,subQ4,subQ3,subQ2,subQ1,subQ0])],"isStart":false})],"blendedInto":[makeQuery(id+"F3.opExtrude","CAP_FACE",FACE,{"disambiguationData":[OSD([subQ17,subQ16,subQ15,subQ14,subQ13,subQ12,subQ11,subQ10,subQ9,subQ8,subQ7,subQ6,subQ5,subQ4,subQ3,subQ2,subQ1,subQ0])],"isStart":false})]})])],"isStart":false});}
            var Q3;
            {var subQ0=sQuery(id+"F0.wireOp",EDGE,"E3.4");var subQ1=sQuery(id+"F0.wireOp",EDGE,"E3.3");var subQ2=sQuery(id+"F0.wireOp",EDGE,"E3.2");var subQ3=sQuery(id+"F0.wireOp",EDGE,"E3.1");var subQ4=sQuery(id+"F0.wireOp",EDGE,"E2.5");var subQ5=sQuery(id+"F0.wireOp",EDGE,"E2.4");var subQ6=sQuery(id+"F0.wireOp",EDGE,"E2.3");var subQ7=sQuery(id+"F0.wireOp",EDGE,"E2.2");var subQ8=sQuery(id+"F0.wireOp",EDGE,"E1.4");var subQ9=sQuery(id+"F0.wireOp",EDGE,"E1.3");var subQ10=sQuery(id+"F0.wireOp",EDGE,"E1.2");var subQ11=sQuery(id+"F0.wireOp",EDGE,"E1.1");var subQ12=sQuery(id+"F0.wireOp",EDGE,"E0.5");var subQ13=sQuery(id+"F0.wireOp",EDGE,"E0.4");var subQ14=sQuery(id+"F0.wireOp",EDGE,"E0.3");var subQ15=sQuery(id+"F0.wireOp",EDGE,"E0.2");var subQ16=sQuery(id+"F0.wireOp",EDGE,"E0.1");var subQ17=sQuery(id+"F0.wireOp",EDGE,"E0.0");Q3=makeQuery(id+"F5.opExtrude","CAP_EDGE",EDGE,{"disambiguationData":[OSD([subQ17,subQ16,subQ15,subQ14,subQ13,subQ12,subQ11,subQ10,subQ9,subQ8,subQ7,subQ6,subQ5,subQ4,subQ3,subQ2,subQ1,subQ0]),TDD([makeQuery(id+"F4.opChamfer","BLEND_EDGE",EDGE,{"blendedFrom":[makeQuery(id+"F3.opExtrude","CAP_EDGE",EDGE,{"disambiguationData":[OSD([subQ17,subQ16,subQ15,subQ14,subQ13,subQ12,subQ11,subQ10,subQ9,subQ8,subQ7,subQ6,subQ5,subQ4,subQ3,subQ2,subQ1,subQ0]),TDD([makeQuery(id+"F2.opChamfer","BLEND_EDGE",EDGE,{"blendedFrom":[makeQuery(id+"F1.opExtrude","CAP_EDGE",EDGE,{"disambiguationData":[OSD([subQ11])],"isStart":false}),makeQuery(id+"F1.opExtrude","CAP_FACE",FACE,{"disambiguationData":[OSD([subQ17,subQ16,subQ15,subQ14,subQ13,subQ12,subQ11,subQ10,subQ9,subQ8,subQ7,subQ6,subQ5,subQ4,subQ3,subQ2,subQ1,subQ0])],"isStart":false})],"blendedInto":[makeQuery(id+"F1.opExtrude","CAP_FACE",FACE,{"disambiguationData":[OSD([subQ17,subQ16,subQ15,subQ14,subQ13,subQ12,subQ11,subQ10,subQ9,subQ8,subQ7,subQ6,subQ5,subQ4,subQ3,subQ2,subQ1,subQ0])],"isStart":false})]})])],"isStart":false}),makeQuery(id+"F3.opExtrude","CAP_FACE",FACE,{"disambiguationData":[OSD([subQ17,subQ16,subQ15,subQ14,subQ13,subQ12,subQ11,subQ10,subQ9,subQ8,subQ7,subQ6,subQ5,subQ4,subQ3,subQ2,subQ1,subQ0])],"isStart":false})],"blendedInto":[makeQuery(id+"F3.opExtrude","CAP_FACE",FACE,{"disambiguationData":[OSD([subQ17,subQ16,subQ15,subQ14,subQ13,subQ12,subQ11,subQ10,subQ9,subQ8,subQ7,subQ6,subQ5,subQ4,subQ3,subQ2,subQ1,subQ0])],"isStart":false})]})])],"isStart":false});}
            var Q4;
            {var subQ0=sQuery(id+"F0.wireOp",EDGE,"E3.4");var subQ1=sQuery(id+"F0.wireOp",EDGE,"E3.3");var subQ2=sQuery(id+"F0.wireOp",EDGE,"E3.2");var subQ3=sQuery(id+"F0.wireOp",EDGE,"E3.1");var subQ4=sQuery(id+"F0.wireOp",EDGE,"E2.5");var subQ5=sQuery(id+"F0.wireOp",EDGE,"E2.4");var subQ6=sQuery(id+"F0.wireOp",EDGE,"E2.3");var subQ7=sQuery(id+"F0.wireOp",EDGE,"E2.2");var subQ8=sQuery(id+"F0.wireOp",EDGE,"E1.4");var subQ9=sQuery(id+"F0.wireOp",EDGE,"E1.3");var subQ10=sQuery(id+"F0.wireOp",EDGE,"E1.2");var subQ11=sQuery(id+"F0.wireOp",EDGE,"E1.1");var subQ12=sQuery(id+"F0.wireOp",EDGE,"E0.5");var subQ13=sQuery(id+"F0.wireOp",EDGE,"E0.4");var subQ14=sQuery(id+"F0.wireOp",EDGE,"E0.3");var subQ15=sQuery(id+"F0.wireOp",EDGE,"E0.2");var subQ16=sQuery(id+"F0.wireOp",EDGE,"E0.1");var subQ17=sQuery(id+"F0.wireOp",EDGE,"E0.0");Q4=makeQuery(id+"F5.opExtrude","CAP_EDGE",EDGE,{"disambiguationData":[OSD([subQ17,subQ16,subQ15,subQ14,subQ13,subQ12,subQ11,subQ10,subQ9,subQ8,subQ7,subQ6,subQ5,subQ4,subQ3,subQ2,subQ1,subQ0]),TDD([makeQuery(id+"F4.opChamfer","BLEND_EDGE",EDGE,{"blendedFrom":[makeQuery(id+"F3.opExtrude","CAP_EDGE",EDGE,{"disambiguationData":[OSD([subQ17,subQ16,subQ15,subQ14,subQ13,subQ12,subQ11,subQ10,subQ9,subQ8,subQ7,subQ6,subQ5,subQ4,subQ3,subQ2,subQ1,subQ0]),TDD([makeQuery(id+"F2.opChamfer","BLEND_EDGE",EDGE,{"blendedFrom":[makeQuery(id+"F1.opExtrude","CAP_EDGE",EDGE,{"disambiguationData":[OSD([subQ0])],"isStart":false}),makeQuery(id+"F1.opExtrude","CAP_FACE",FACE,{"disambiguationData":[OSD([subQ17,subQ16,subQ15,subQ14,subQ13,subQ12,subQ11,subQ10,subQ9,subQ8,subQ7,subQ6,subQ5,subQ4,subQ3,subQ2,subQ1,subQ0])],"isStart":false})],"blendedInto":[makeQuery(id+"F1.opExtrude","CAP_FACE",FACE,{"disambiguationData":[OSD([subQ17,subQ16,subQ15,subQ14,subQ13,subQ12,subQ11,subQ10,subQ9,subQ8,subQ7,subQ6,subQ5,subQ4,subQ3,subQ2,subQ1,subQ0])],"isStart":false})]})])],"isStart":false}),makeQuery(id+"F3.opExtrude","CAP_FACE",FACE,{"disambiguationData":[OSD([subQ17,subQ16,subQ15,subQ14,subQ13,subQ12,subQ11,subQ10,subQ9,subQ8,subQ7,subQ6,subQ5,subQ4,subQ3,subQ2,subQ1,subQ0])],"isStart":false})],"blendedInto":[makeQuery(id+"F3.opExtrude","CAP_FACE",FACE,{"disambiguationData":[OSD([subQ17,subQ16,subQ15,subQ14,subQ13,subQ12,subQ11,subQ10,subQ9,subQ8,subQ7,subQ6,subQ5,subQ4,subQ3,subQ2,subQ1,subQ0])],"isStart":false})]})])],"isStart":false});}
            var Q5;
            {var subQ0=sQuery(id+"F0.wireOp",EDGE,"E3.4");var subQ1=sQuery(id+"F0.wireOp",EDGE,"E3.3");var subQ2=sQuery(id+"F0.wireOp",EDGE,"E3.2");var subQ3=sQuery(id+"F0.wireOp",EDGE,"E3.1");var subQ4=sQuery(id+"F0.wireOp",EDGE,"E2.5");var subQ5=sQuery(id+"F0.wireOp",EDGE,"E2.4");var subQ6=sQuery(id+"F0.wireOp",EDGE,"E2.3");var subQ7=sQuery(id+"F0.wireOp",EDGE,"E2.2");var subQ8=sQuery(id+"F0.wireOp",EDGE,"E1.4");var subQ9=sQuery(id+"F0.wireOp",EDGE,"E1.3");var subQ10=sQuery(id+"F0.wireOp",EDGE,"E1.2");var subQ11=sQuery(id+"F0.wireOp",EDGE,"E1.1");var subQ12=sQuery(id+"F0.wireOp",EDGE,"E0.5");var subQ13=sQuery(id+"F0.wireOp",EDGE,"E0.4");var subQ14=sQuery(id+"F0.wireOp",EDGE,"E0.3");var subQ15=sQuery(id+"F0.wireOp",EDGE,"E0.2");var subQ16=sQuery(id+"F0.wireOp",EDGE,"E0.1");var subQ17=sQuery(id+"F0.wireOp",EDGE,"E0.0");Q5=makeQuery(id+"F5.opExtrude","CAP_EDGE",EDGE,{"disambiguationData":[OSD([subQ17,subQ16,subQ15,subQ14,subQ13,subQ12,subQ11,subQ10,subQ9,subQ8,subQ7,subQ6,subQ5,subQ4,subQ3,subQ2,subQ1,subQ0]),TDD([makeQuery(id+"F4.opChamfer","BLEND_EDGE",EDGE,{"blendedFrom":[makeQuery(id+"F3.opExtrude","CAP_EDGE",EDGE,{"disambiguationData":[OSD([subQ17,subQ16,subQ15,subQ14,subQ13,subQ12,subQ11,subQ10,subQ9,subQ8,subQ7,subQ6,subQ5,subQ4,subQ3,subQ2,subQ1,subQ0]),TDD([makeQuery(id+"F2.opChamfer","BLEND_EDGE",EDGE,{"blendedFrom":[makeQuery(id+"F1.opExtrude","CAP_EDGE",EDGE,{"disambiguationData":[OSD([subQ1])],"isStart":false}),makeQuery(id+"F1.opExtrude","CAP_FACE",FACE,{"disambiguationData":[OSD([subQ17,subQ16,subQ15,subQ14,subQ13,subQ12,subQ11,subQ10,subQ9,subQ8,subQ7,subQ6,subQ5,subQ4,subQ3,subQ2,subQ1,subQ0])],"isStart":false})],"blendedInto":[makeQuery(id+"F1.opExtrude","CAP_FACE",FACE,{"disambiguationData":[OSD([subQ17,subQ16,subQ15,subQ14,subQ13,subQ12,subQ11,subQ10,subQ9,subQ8,subQ7,subQ6,subQ5,subQ4,subQ3,subQ2,subQ1,subQ0])],"isStart":false})]})])],"isStart":false}),makeQuery(id+"F3.opExtrude","CAP_FACE",FACE,{"disambiguationData":[OSD([subQ17,subQ16,subQ15,subQ14,subQ13,subQ12,subQ11,subQ10,subQ9,subQ8,subQ7,subQ6,subQ5,subQ4,subQ3,subQ2,subQ1,subQ0])],"isStart":false})],"blendedInto":[makeQuery(id+"F3.opExtrude","CAP_FACE",FACE,{"disambiguationData":[OSD([subQ17,subQ16,subQ15,subQ14,subQ13,subQ12,subQ11,subQ10,subQ9,subQ8,subQ7,subQ6,subQ5,subQ4,subQ3,subQ2,subQ1,subQ0])],"isStart":false})]})])],"isStart":false});}
            var Q6;
            {var subQ0=sQuery(id+"F0.wireOp",EDGE,"E3.4");var subQ1=sQuery(id+"F0.wireOp",EDGE,"E3.3");var subQ2=sQuery(id+"F0.wireOp",EDGE,"E3.2");var subQ3=sQuery(id+"F0.wireOp",EDGE,"E3.1");var subQ4=sQuery(id+"F0.wireOp",EDGE,"E2.5");var subQ5=sQuery(id+"F0.wireOp",EDGE,"E2.4");var subQ6=sQuery(id+"F0.wireOp",EDGE,"E2.3");var subQ7=sQuery(id+"F0.wireOp",EDGE,"E2.2");var subQ8=sQuery(id+"F0.wireOp",EDGE,"E1.4");var subQ9=sQuery(id+"F0.wireOp",EDGE,"E1.3");var subQ10=sQuery(id+"F0.wireOp",EDGE,"E1.2");var subQ11=sQuery(id+"F0.wireOp",EDGE,"E1.1");var subQ12=sQuery(id+"F0.wireOp",EDGE,"E0.5");var subQ13=sQuery(id+"F0.wireOp",EDGE,"E0.4");var subQ14=sQuery(id+"F0.wireOp",EDGE,"E0.3");var subQ15=sQuery(id+"F0.wireOp",EDGE,"E0.2");var subQ16=sQuery(id+"F0.wireOp",EDGE,"E0.1");var subQ17=sQuery(id+"F0.wireOp",EDGE,"E0.0");Q6=makeQuery(id+"F5.opExtrude","CAP_EDGE",EDGE,{"disambiguationData":[OSD([subQ17,subQ16,subQ15,subQ14,subQ13,subQ12,subQ11,subQ10,subQ9,subQ8,subQ7,subQ6,subQ5,subQ4,subQ3,subQ2,subQ1,subQ0]),TDD([makeQuery(id+"F4.opChamfer","BLEND_EDGE",EDGE,{"blendedFrom":[makeQuery(id+"F3.opExtrude","CAP_EDGE",EDGE,{"disambiguationData":[OSD([subQ17,subQ16,subQ15,subQ14,subQ13,subQ12,subQ11,subQ10,subQ9,subQ8,subQ7,subQ6,subQ5,subQ4,subQ3,subQ2,subQ1,subQ0]),TDD([makeQuery(id+"F2.opChamfer","BLEND_EDGE",EDGE,{"blendedFrom":[makeQuery(id+"F1.opExtrude","CAP_EDGE",EDGE,{"disambiguationData":[OSD([subQ2])],"isStart":false}),makeQuery(id+"F1.opExtrude","CAP_FACE",FACE,{"disambiguationData":[OSD([subQ17,subQ16,subQ15,subQ14,subQ13,subQ12,subQ11,subQ10,subQ9,subQ8,subQ7,subQ6,subQ5,subQ4,subQ3,subQ2,subQ1,subQ0])],"isStart":false})],"blendedInto":[makeQuery(id+"F1.opExtrude","CAP_FACE",FACE,{"disambiguationData":[OSD([subQ17,subQ16,subQ15,subQ14,subQ13,subQ12,subQ11,subQ10,subQ9,subQ8,subQ7,subQ6,subQ5,subQ4,subQ3,subQ2,subQ1,subQ0])],"isStart":false})]})])],"isStart":false}),makeQuery(id+"F3.opExtrude","CAP_FACE",FACE,{"disambiguationData":[OSD([subQ17,subQ16,subQ15,subQ14,subQ13,subQ12,subQ11,subQ10,subQ9,subQ8,subQ7,subQ6,subQ5,subQ4,subQ3,subQ2,subQ1,subQ0])],"isStart":false})],"blendedInto":[makeQuery(id+"F3.opExtrude","CAP_FACE",FACE,{"disambiguationData":[OSD([subQ17,subQ16,subQ15,subQ14,subQ13,subQ12,subQ11,subQ10,subQ9,subQ8,subQ7,subQ6,subQ5,subQ4,subQ3,subQ2,subQ1,subQ0])],"isStart":false})]})])],"isStart":false});}
            var Q7;
            {var subQ0=sQuery(id+"F0.wireOp",EDGE,"E3.4");var subQ1=sQuery(id+"F0.wireOp",EDGE,"E3.3");var subQ2=sQuery(id+"F0.wireOp",EDGE,"E3.2");var subQ3=sQuery(id+"F0.wireOp",EDGE,"E3.1");var subQ4=sQuery(id+"F0.wireOp",EDGE,"E2.5");var subQ5=sQuery(id+"F0.wireOp",EDGE,"E2.4");var subQ6=sQuery(id+"F0.wireOp",EDGE,"E2.3");var subQ7=sQuery(id+"F0.wireOp",EDGE,"E2.2");var subQ8=sQuery(id+"F0.wireOp",EDGE,"E1.4");var subQ9=sQuery(id+"F0.wireOp",EDGE,"E1.3");var subQ10=sQuery(id+"F0.wireOp",EDGE,"E1.2");var subQ11=sQuery(id+"F0.wireOp",EDGE,"E1.1");var subQ12=sQuery(id+"F0.wireOp",EDGE,"E0.5");var subQ13=sQuery(id+"F0.wireOp",EDGE,"E0.4");var subQ14=sQuery(id+"F0.wireOp",EDGE,"E0.3");var subQ15=sQuery(id+"F0.wireOp",EDGE,"E0.2");var subQ16=sQuery(id+"F0.wireOp",EDGE,"E0.1");var subQ17=sQuery(id+"F0.wireOp",EDGE,"E0.0");Q7=makeQuery(id+"F5.opExtrude","CAP_EDGE",EDGE,{"disambiguationData":[OSD([subQ17,subQ16,subQ15,subQ14,subQ13,subQ12,subQ11,subQ10,subQ9,subQ8,subQ7,subQ6,subQ5,subQ4,subQ3,subQ2,subQ1,subQ0]),TDD([makeQuery(id+"F4.opChamfer","BLEND_EDGE",EDGE,{"blendedFrom":[makeQuery(id+"F3.opExtrude","CAP_EDGE",EDGE,{"disambiguationData":[OSD([subQ17,subQ16,subQ15,subQ14,subQ13,subQ12,subQ11,subQ10,subQ9,subQ8,subQ7,subQ6,subQ5,subQ4,subQ3,subQ2,subQ1,subQ0]),TDD([makeQuery(id+"F2.opChamfer","BLEND_EDGE",EDGE,{"blendedFrom":[makeQuery(id+"F1.opExtrude","CAP_EDGE",EDGE,{"disambiguationData":[OSD([subQ3])],"isStart":false}),makeQuery(id+"F1.opExtrude","CAP_FACE",FACE,{"disambiguationData":[OSD([subQ17,subQ16,subQ15,subQ14,subQ13,subQ12,subQ11,subQ10,subQ9,subQ8,subQ7,subQ6,subQ5,subQ4,subQ3,subQ2,subQ1,subQ0])],"isStart":false})],"blendedInto":[makeQuery(id+"F1.opExtrude","CAP_FACE",FACE,{"disambiguationData":[OSD([subQ17,subQ16,subQ15,subQ14,subQ13,subQ12,subQ11,subQ10,subQ9,subQ8,subQ7,subQ6,subQ5,subQ4,subQ3,subQ2,subQ1,subQ0])],"isStart":false})]})])],"isStart":false}),makeQuery(id+"F3.opExtrude","CAP_FACE",FACE,{"disambiguationData":[OSD([subQ17,subQ16,subQ15,subQ14,subQ13,subQ12,subQ11,subQ10,subQ9,subQ8,subQ7,subQ6,subQ5,subQ4,subQ3,subQ2,subQ1,subQ0])],"isStart":false})],"blendedInto":[makeQuery(id+"F3.opExtrude","CAP_FACE",FACE,{"disambiguationData":[OSD([subQ17,subQ16,subQ15,subQ14,subQ13,subQ12,subQ11,subQ10,subQ9,subQ8,subQ7,subQ6,subQ5,subQ4,subQ3,subQ2,subQ1,subQ0])],"isStart":false})]})])],"isStart":false});}
            var Q8;
            {var subQ0=sQuery(id+"F0.wireOp",EDGE,"E3.4");var subQ1=sQuery(id+"F0.wireOp",EDGE,"E3.3");var subQ2=sQuery(id+"F0.wireOp",EDGE,"E3.2");var subQ3=sQuery(id+"F0.wireOp",EDGE,"E3.1");var subQ4=sQuery(id+"F0.wireOp",EDGE,"E2.5");var subQ5=sQuery(id+"F0.wireOp",EDGE,"E2.4");var subQ6=sQuery(id+"F0.wireOp",EDGE,"E2.3");var subQ7=sQuery(id+"F0.wireOp",EDGE,"E2.2");var subQ8=sQuery(id+"F0.wireOp",EDGE,"E1.4");var subQ9=sQuery(id+"F0.wireOp",EDGE,"E1.3");var subQ10=sQuery(id+"F0.wireOp",EDGE,"E1.2");var subQ11=sQuery(id+"F0.wireOp",EDGE,"E1.1");var subQ12=sQuery(id+"F0.wireOp",EDGE,"E0.5");var subQ13=sQuery(id+"F0.wireOp",EDGE,"E0.4");var subQ14=sQuery(id+"F0.wireOp",EDGE,"E0.3");var subQ15=sQuery(id+"F0.wireOp",EDGE,"E0.2");var subQ16=sQuery(id+"F0.wireOp",EDGE,"E0.1");var subQ17=sQuery(id+"F0.wireOp",EDGE,"E0.0");Q8=makeQuery(id+"F5.opExtrude","CAP_EDGE",EDGE,{"disambiguationData":[OSD([subQ17,subQ16,subQ15,subQ14,subQ13,subQ12,subQ11,subQ10,subQ9,subQ8,subQ7,subQ6,subQ5,subQ4,subQ3,subQ2,subQ1,subQ0]),TDD([makeQuery(id+"F4.opChamfer","BLEND_EDGE",EDGE,{"blendedFrom":[makeQuery(id+"F3.opExtrude","CAP_EDGE",EDGE,{"disambiguationData":[OSD([subQ17,subQ16,subQ15,subQ14,subQ13,subQ12,subQ11,subQ10,subQ9,subQ8,subQ7,subQ6,subQ5,subQ4,subQ3,subQ2,subQ1,subQ0]),TDD([makeQuery(id+"F2.opChamfer","BLEND_EDGE",EDGE,{"blendedFrom":[makeQuery(id+"F1.opExtrude","CAP_EDGE",EDGE,{"disambiguationData":[OSD([subQ4])],"isStart":false}),makeQuery(id+"F1.opExtrude","CAP_FACE",FACE,{"disambiguationData":[OSD([subQ17,subQ16,subQ15,subQ14,subQ13,subQ12,subQ11,subQ10,subQ9,subQ8,subQ7,subQ6,subQ5,subQ4,subQ3,subQ2,subQ1,subQ0])],"isStart":false})],"blendedInto":[makeQuery(id+"F1.opExtrude","CAP_FACE",FACE,{"disambiguationData":[OSD([subQ17,subQ16,subQ15,subQ14,subQ13,subQ12,subQ11,subQ10,subQ9,subQ8,subQ7,subQ6,subQ5,subQ4,subQ3,subQ2,subQ1,subQ0])],"isStart":false})]})])],"isStart":false}),makeQuery(id+"F3.opExtrude","CAP_FACE",FACE,{"disambiguationData":[OSD([subQ17,subQ16,subQ15,subQ14,subQ13,subQ12,subQ11,subQ10,subQ9,subQ8,subQ7,subQ6,subQ5,subQ4,subQ3,subQ2,subQ1,subQ0])],"isStart":false})],"blendedInto":[makeQuery(id+"F3.opExtrude","CAP_FACE",FACE,{"disambiguationData":[OSD([subQ17,subQ16,subQ15,subQ14,subQ13,subQ12,subQ11,subQ10,subQ9,subQ8,subQ7,subQ6,subQ5,subQ4,subQ3,subQ2,subQ1,subQ0])],"isStart":false})]})])],"isStart":false});}
            var Q9;
            {var subQ0=sQuery(id+"F0.wireOp",EDGE,"E3.4");var subQ1=sQuery(id+"F0.wireOp",EDGE,"E3.3");var subQ2=sQuery(id+"F0.wireOp",EDGE,"E3.2");var subQ3=sQuery(id+"F0.wireOp",EDGE,"E3.1");var subQ4=sQuery(id+"F0.wireOp",EDGE,"E2.5");var subQ5=sQuery(id+"F0.wireOp",EDGE,"E2.4");var subQ6=sQuery(id+"F0.wireOp",EDGE,"E2.3");var subQ7=sQuery(id+"F0.wireOp",EDGE,"E2.2");var subQ8=sQuery(id+"F0.wireOp",EDGE,"E1.4");var subQ9=sQuery(id+"F0.wireOp",EDGE,"E1.3");var subQ10=sQuery(id+"F0.wireOp",EDGE,"E1.2");var subQ11=sQuery(id+"F0.wireOp",EDGE,"E1.1");var subQ12=sQuery(id+"F0.wireOp",EDGE,"E0.5");var subQ13=sQuery(id+"F0.wireOp",EDGE,"E0.4");var subQ14=sQuery(id+"F0.wireOp",EDGE,"E0.3");var subQ15=sQuery(id+"F0.wireOp",EDGE,"E0.2");var subQ16=sQuery(id+"F0.wireOp",EDGE,"E0.1");var subQ17=sQuery(id+"F0.wireOp",EDGE,"E0.0");Q9=makeQuery(id+"F5.opExtrude","CAP_EDGE",EDGE,{"disambiguationData":[OSD([subQ17,subQ16,subQ15,subQ14,subQ13,subQ12,subQ11,subQ10,subQ9,subQ8,subQ7,subQ6,subQ5,subQ4,subQ3,subQ2,subQ1,subQ0]),TDD([makeQuery(id+"F4.opChamfer","BLEND_EDGE",EDGE,{"blendedFrom":[makeQuery(id+"F3.opExtrude","CAP_EDGE",EDGE,{"disambiguationData":[OSD([subQ17,subQ16,subQ15,subQ14,subQ13,subQ12,subQ11,subQ10,subQ9,subQ8,subQ7,subQ6,subQ5,subQ4,subQ3,subQ2,subQ1,subQ0]),TDD([makeQuery(id+"F2.opChamfer","BLEND_EDGE",EDGE,{"blendedFrom":[makeQuery(id+"F1.opExtrude","CAP_EDGE",EDGE,{"disambiguationData":[OSD([subQ5])],"isStart":false}),makeQuery(id+"F1.opExtrude","CAP_FACE",FACE,{"disambiguationData":[OSD([subQ17,subQ16,subQ15,subQ14,subQ13,subQ12,subQ11,subQ10,subQ9,subQ8,subQ7,subQ6,subQ5,subQ4,subQ3,subQ2,subQ1,subQ0])],"isStart":false})],"blendedInto":[makeQuery(id+"F1.opExtrude","CAP_FACE",FACE,{"disambiguationData":[OSD([subQ17,subQ16,subQ15,subQ14,subQ13,subQ12,subQ11,subQ10,subQ9,subQ8,subQ7,subQ6,subQ5,subQ4,subQ3,subQ2,subQ1,subQ0])],"isStart":false})]})])],"isStart":false}),makeQuery(id+"F3.opExtrude","CAP_FACE",FACE,{"disambiguationData":[OSD([subQ17,subQ16,subQ15,subQ14,subQ13,subQ12,subQ11,subQ10,subQ9,subQ8,subQ7,subQ6,subQ5,subQ4,subQ3,subQ2,subQ1,subQ0])],"isStart":false})],"blendedInto":[makeQuery(id+"F3.opExtrude","CAP_FACE",FACE,{"disambiguationData":[OSD([subQ17,subQ16,subQ15,subQ14,subQ13,subQ12,subQ11,subQ10,subQ9,subQ8,subQ7,subQ6,subQ5,subQ4,subQ3,subQ2,subQ1,subQ0])],"isStart":false})]})])],"isStart":false});}
            var Q10;
            {var subQ0=sQuery(id+"F0.wireOp",EDGE,"E3.4");var subQ1=sQuery(id+"F0.wireOp",EDGE,"E3.3");var subQ2=sQuery(id+"F0.wireOp",EDGE,"E3.2");var subQ3=sQuery(id+"F0.wireOp",EDGE,"E3.1");var subQ4=sQuery(id+"F0.wireOp",EDGE,"E2.5");var subQ5=sQuery(id+"F0.wireOp",EDGE,"E2.4");var subQ6=sQuery(id+"F0.wireOp",EDGE,"E2.3");var subQ7=sQuery(id+"F0.wireOp",EDGE,"E2.2");var subQ8=sQuery(id+"F0.wireOp",EDGE,"E1.4");var subQ9=sQuery(id+"F0.wireOp",EDGE,"E1.3");var subQ10=sQuery(id+"F0.wireOp",EDGE,"E1.2");var subQ11=sQuery(id+"F0.wireOp",EDGE,"E1.1");var subQ12=sQuery(id+"F0.wireOp",EDGE,"E0.5");var subQ13=sQuery(id+"F0.wireOp",EDGE,"E0.4");var subQ14=sQuery(id+"F0.wireOp",EDGE,"E0.3");var subQ15=sQuery(id+"F0.wireOp",EDGE,"E0.2");var subQ16=sQuery(id+"F0.wireOp",EDGE,"E0.1");var subQ17=sQuery(id+"F0.wireOp",EDGE,"E0.0");Q10=makeQuery(id+"F5.opExtrude","CAP_EDGE",EDGE,{"disambiguationData":[OSD([subQ17,subQ16,subQ15,subQ14,subQ13,subQ12,subQ11,subQ10,subQ9,subQ8,subQ7,subQ6,subQ5,subQ4,subQ3,subQ2,subQ1,subQ0]),TDD([makeQuery(id+"F4.opChamfer","BLEND_EDGE",EDGE,{"blendedFrom":[makeQuery(id+"F3.opExtrude","CAP_EDGE",EDGE,{"disambiguationData":[OSD([subQ17,subQ16,subQ15,subQ14,subQ13,subQ12,subQ11,subQ10,subQ9,subQ8,subQ7,subQ6,subQ5,subQ4,subQ3,subQ2,subQ1,subQ0]),TDD([makeQuery(id+"F2.opChamfer","BLEND_EDGE",EDGE,{"blendedFrom":[makeQuery(id+"F1.opExtrude","CAP_EDGE",EDGE,{"disambiguationData":[OSD([subQ6])],"isStart":false}),makeQuery(id+"F1.opExtrude","CAP_FACE",FACE,{"disambiguationData":[OSD([subQ17,subQ16,subQ15,subQ14,subQ13,subQ12,subQ11,subQ10,subQ9,subQ8,subQ7,subQ6,subQ5,subQ4,subQ3,subQ2,subQ1,subQ0])],"isStart":false})],"blendedInto":[makeQuery(id+"F1.opExtrude","CAP_FACE",FACE,{"disambiguationData":[OSD([subQ17,subQ16,subQ15,subQ14,subQ13,subQ12,subQ11,subQ10,subQ9,subQ8,subQ7,subQ6,subQ5,subQ4,subQ3,subQ2,subQ1,subQ0])],"isStart":false})]})])],"isStart":false}),makeQuery(id+"F3.opExtrude","CAP_FACE",FACE,{"disambiguationData":[OSD([subQ17,subQ16,subQ15,subQ14,subQ13,subQ12,subQ11,subQ10,subQ9,subQ8,subQ7,subQ6,subQ5,subQ4,subQ3,subQ2,subQ1,subQ0])],"isStart":false})],"blendedInto":[makeQuery(id+"F3.opExtrude","CAP_FACE",FACE,{"disambiguationData":[OSD([subQ17,subQ16,subQ15,subQ14,subQ13,subQ12,subQ11,subQ10,subQ9,subQ8,subQ7,subQ6,subQ5,subQ4,subQ3,subQ2,subQ1,subQ0])],"isStart":false})]})])],"isStart":false});}
            var Q11;
            {var subQ0=sQuery(id+"F0.wireOp",EDGE,"E3.4");var subQ1=sQuery(id+"F0.wireOp",EDGE,"E3.3");var subQ2=sQuery(id+"F0.wireOp",EDGE,"E3.2");var subQ3=sQuery(id+"F0.wireOp",EDGE,"E3.1");var subQ4=sQuery(id+"F0.wireOp",EDGE,"E2.5");var subQ5=sQuery(id+"F0.wireOp",EDGE,"E2.4");var subQ6=sQuery(id+"F0.wireOp",EDGE,"E2.3");var subQ7=sQuery(id+"F0.wireOp",EDGE,"E2.2");var subQ8=sQuery(id+"F0.wireOp",EDGE,"E1.4");var subQ9=sQuery(id+"F0.wireOp",EDGE,"E1.3");var subQ10=sQuery(id+"F0.wireOp",EDGE,"E1.2");var subQ11=sQuery(id+"F0.wireOp",EDGE,"E1.1");var subQ12=sQuery(id+"F0.wireOp",EDGE,"E0.5");var subQ13=sQuery(id+"F0.wireOp",EDGE,"E0.4");var subQ14=sQuery(id+"F0.wireOp",EDGE,"E0.3");var subQ15=sQuery(id+"F0.wireOp",EDGE,"E0.2");var subQ16=sQuery(id+"F0.wireOp",EDGE,"E0.1");var subQ17=sQuery(id+"F0.wireOp",EDGE,"E0.0");Q11=makeQuery(id+"F5.opExtrude","CAP_EDGE",EDGE,{"disambiguationData":[OSD([subQ17,subQ16,subQ15,subQ14,subQ13,subQ12,subQ11,subQ10,subQ9,subQ8,subQ7,subQ6,subQ5,subQ4,subQ3,subQ2,subQ1,subQ0]),TDD([makeQuery(id+"F4.opChamfer","BLEND_EDGE",EDGE,{"blendedFrom":[makeQuery(id+"F3.opExtrude","CAP_EDGE",EDGE,{"disambiguationData":[OSD([subQ17,subQ16,subQ15,subQ14,subQ13,subQ12,subQ11,subQ10,subQ9,subQ8,subQ7,subQ6,subQ5,subQ4,subQ3,subQ2,subQ1,subQ0]),TDD([makeQuery(id+"F2.opChamfer","BLEND_EDGE",EDGE,{"blendedFrom":[makeQuery(id+"F1.opExtrude","CAP_EDGE",EDGE,{"disambiguationData":[OSD([subQ7])],"isStart":false}),makeQuery(id+"F1.opExtrude","CAP_FACE",FACE,{"disambiguationData":[OSD([subQ17,subQ16,subQ15,subQ14,subQ13,subQ12,subQ11,subQ10,subQ9,subQ8,subQ7,subQ6,subQ5,subQ4,subQ3,subQ2,subQ1,subQ0])],"isStart":false})],"blendedInto":[makeQuery(id+"F1.opExtrude","CAP_FACE",FACE,{"disambiguationData":[OSD([subQ17,subQ16,subQ15,subQ14,subQ13,subQ12,subQ11,subQ10,subQ9,subQ8,subQ7,subQ6,subQ5,subQ4,subQ3,subQ2,subQ1,subQ0])],"isStart":false})]})])],"isStart":false}),makeQuery(id+"F3.opExtrude","CAP_FACE",FACE,{"disambiguationData":[OSD([subQ17,subQ16,subQ15,subQ14,subQ13,subQ12,subQ11,subQ10,subQ9,subQ8,subQ7,subQ6,subQ5,subQ4,subQ3,subQ2,subQ1,subQ0])],"isStart":false})],"blendedInto":[makeQuery(id+"F3.opExtrude","CAP_FACE",FACE,{"disambiguationData":[OSD([subQ17,subQ16,subQ15,subQ14,subQ13,subQ12,subQ11,subQ10,subQ9,subQ8,subQ7,subQ6,subQ5,subQ4,subQ3,subQ2,subQ1,subQ0])],"isStart":false})]})])],"isStart":false});}
            chamfer(context, id + "F6", {"entities" : qUnion([Q0, Q1, Q2, Q3, Q4, Q5, Q6, Q7, Q8, Q9, Q10, Q11]), "width" : 5.08 * mm, "tangentPropagation" : true});
        }
        {
            var Q0;
            Q0=makeQuery(id+"F5.opExtrude","CAP_FACE",FACE,{"disambiguationData":[OSD([sQuery(id+"F0.wireOp",EDGE,"E0.0"),sQuery(id+"F0.wireOp",EDGE,"E0.1"),sQuery(id+"F0.wireOp",EDGE,"E0.2"),sQuery(id+"F0.wireOp",EDGE,"E0.3"),sQuery(id+"F0.wireOp",EDGE,"E0.4"),sQuery(id+"F0.wireOp",EDGE,"E0.5"),sQuery(id+"F0.wireOp",EDGE,"E1.1"),sQuery(id+"F0.wireOp",EDGE,"E1.2"),sQuery(id+"F0.wireOp",EDGE,"E1.3"),sQuery(id+"F0.wireOp",EDGE,"E1.4"),sQuery(id+"F0.wireOp",EDGE,"E2.2"),sQuery(id+"F0.wireOp",EDGE,"E2.3"),sQuery(id+"F0.wireOp",EDGE,"E2.4"),sQuery(id+"F0.wireOp",EDGE,"E2.5"),sQuery(id+"F0.wireOp",EDGE,"E3.1"),sQuery(id+"F0.wireOp",EDGE,"E3.2"),sQuery(id+"F0.wireOp",EDGE,"E3.3"),sQuery(id+"F0.wireOp",EDGE,"E3.4")])],"isStart":false});
            extrude(context, id + "F7", {"entities" : qUnion([Q0]), "operationType" : NewBodyOperationType.ADD, "depth" : 25.4 * mm});
        }
        {
            var Q0;
            {var subQ0=sQuery(id+"F0.wireOp",EDGE,"E3.4");var subQ1=sQuery(id+"F0.wireOp",EDGE,"E3.3");var subQ2=sQuery(id+"F0.wireOp",EDGE,"E3.2");var subQ3=sQuery(id+"F0.wireOp",EDGE,"E3.1");var subQ4=sQuery(id+"F0.wireOp",EDGE,"E2.5");var subQ5=sQuery(id+"F0.wireOp",EDGE,"E2.4");var subQ6=sQuery(id+"F0.wireOp",EDGE,"E2.3");var subQ7=sQuery(id+"F0.wireOp",EDGE,"E2.2");var subQ8=sQuery(id+"F0.wireOp",EDGE,"E1.4");var subQ9=sQuery(id+"F0.wireOp",EDGE,"E1.3");var subQ10=sQuery(id+"F0.wireOp",EDGE,"E1.2");var subQ11=sQuery(id+"F0.wireOp",EDGE,"E1.1");var subQ12=sQuery(id+"F0.wireOp",EDGE,"E0.5");var subQ13=sQuery(id+"F0.wireOp",EDGE,"E0.4");var subQ14=sQuery(id+"F0.wireOp",EDGE,"E0.3");var subQ15=sQuery(id+"F0.wireOp",EDGE,"E0.2");var subQ16=sQuery(id+"F0.wireOp",EDGE,"E0.1");var subQ17=sQuery(id+"F0.wireOp",EDGE,"E0.0");Q0=makeQuery(id+"F7.opExtrude","CAP_EDGE",EDGE,{"disambiguationData":[OSD([subQ17,subQ16,subQ15,subQ14,subQ13,subQ12,subQ11,subQ10,subQ9,subQ8,subQ7,subQ6,subQ5,subQ4,subQ3,subQ2,subQ1,subQ0]),TDD([makeQuery(id+"F6.opChamfer","BLEND_EDGE",EDGE,{"blendedFrom":[makeQuery(id+"F5.opExtrude","CAP_EDGE",EDGE,{"disambiguationData":[OSD([subQ17,subQ16,subQ15,subQ14,subQ13,subQ12,subQ11,subQ10,subQ9,subQ8,subQ7,subQ6,subQ5,subQ4,subQ3,subQ2,subQ1,subQ0]),TDD([makeQuery(id+"F4.opChamfer","BLEND_EDGE",EDGE,{"blendedFrom":[makeQuery(id+"F3.opExtrude","CAP_EDGE",EDGE,{"disambiguationData":[OSD([subQ17,subQ16,subQ15,subQ14,subQ13,subQ12,subQ11,subQ10,subQ9,subQ8,subQ7,subQ6,subQ5,subQ4,subQ3,subQ2,subQ1,subQ0]),TDD([makeQuery(id+"F2.opChamfer","BLEND_EDGE",EDGE,{"blendedFrom":[makeQuery(id+"F1.opExtrude","CAP_EDGE",EDGE,{"disambiguationData":[OSD([subQ8])],"isStart":false}),makeQuery(id+"F1.opExtrude","CAP_FACE",FACE,{"disambiguationData":[OSD([subQ17,subQ16,subQ15,subQ14,subQ13,subQ12,subQ11,subQ10,subQ9,subQ8,subQ7,subQ6,subQ5,subQ4,subQ3,subQ2,subQ1,subQ0])],"isStart":false})],"blendedInto":[makeQuery(id+"F1.opExtrude","CAP_FACE",FACE,{"disambiguationData":[OSD([subQ17,subQ16,subQ15,subQ14,subQ13,subQ12,subQ11,subQ10,subQ9,subQ8,subQ7,subQ6,subQ5,subQ4,subQ3,subQ2,subQ1,subQ0])],"isStart":false})]})])],"isStart":false}),makeQuery(id+"F3.opExtrude","CAP_FACE",FACE,{"disambiguationData":[OSD([subQ17,subQ16,subQ15,subQ14,subQ13,subQ12,subQ11,subQ10,subQ9,subQ8,subQ7,subQ6,subQ5,subQ4,subQ3,subQ2,subQ1,subQ0])],"isStart":false})],"blendedInto":[makeQuery(id+"F3.opExtrude","CAP_FACE",FACE,{"disambiguationData":[OSD([subQ17,subQ16,subQ15,subQ14,subQ13,subQ12,subQ11,subQ10,subQ9,subQ8,subQ7,subQ6,subQ5,subQ4,subQ3,subQ2,subQ1,subQ0])],"isStart":false})]})])],"isStart":false}),makeQuery(id+"F5.opExtrude","CAP_FACE",FACE,{"disambiguationData":[OSD([subQ17,subQ16,subQ15,subQ14,subQ13,subQ12,subQ11,subQ10,subQ9,subQ8,subQ7,subQ6,subQ5,subQ4,subQ3,subQ2,subQ1,subQ0])],"isStart":false})],"blendedInto":[makeQuery(id+"F5.opExtrude","CAP_FACE",FACE,{"disambiguationData":[OSD([subQ17,subQ16,subQ15,subQ14,subQ13,subQ12,subQ11,subQ10,subQ9,subQ8,subQ7,subQ6,subQ5,subQ4,subQ3,subQ2,subQ1,subQ0])],"isStart":false})]})])],"isStart":false});}
            var Q1;
            {var subQ0=sQuery(id+"F0.wireOp",EDGE,"E3.4");var subQ1=sQuery(id+"F0.wireOp",EDGE,"E3.3");var subQ2=sQuery(id+"F0.wireOp",EDGE,"E3.2");var subQ3=sQuery(id+"F0.wireOp",EDGE,"E3.1");var subQ4=sQuery(id+"F0.wireOp",EDGE,"E2.5");var subQ5=sQuery(id+"F0.wireOp",EDGE,"E2.4");var subQ6=sQuery(id+"F0.wireOp",EDGE,"E2.3");var subQ7=sQuery(id+"F0.wireOp",EDGE,"E2.2");var subQ8=sQuery(id+"F0.wireOp",EDGE,"E1.4");var subQ9=sQuery(id+"F0.wireOp",EDGE,"E1.3");var subQ10=sQuery(id+"F0.wireOp",EDGE,"E1.2");var subQ11=sQuery(id+"F0.wireOp",EDGE,"E1.1");var subQ12=sQuery(id+"F0.wireOp",EDGE,"E0.5");var subQ13=sQuery(id+"F0.wireOp",EDGE,"E0.4");var subQ14=sQuery(id+"F0.wireOp",EDGE,"E0.3");var subQ15=sQuery(id+"F0.wireOp",EDGE,"E0.2");var subQ16=sQuery(id+"F0.wireOp",EDGE,"E0.1");var subQ17=sQuery(id+"F0.wireOp",EDGE,"E0.0");Q1=makeQuery(id+"F7.opExtrude","CAP_EDGE",EDGE,{"disambiguationData":[OSD([subQ17,subQ16,subQ15,subQ14,subQ13,subQ12,subQ11,subQ10,subQ9,subQ8,subQ7,subQ6,subQ5,subQ4,subQ3,subQ2,subQ1,subQ0]),TDD([makeQuery(id+"F6.opChamfer","BLEND_EDGE",EDGE,{"blendedFrom":[makeQuery(id+"F5.opExtrude","CAP_EDGE",EDGE,{"disambiguationData":[OSD([subQ17,subQ16,subQ15,subQ14,subQ13,subQ12,subQ11,subQ10,subQ9,subQ8,subQ7,subQ6,subQ5,subQ4,subQ3,subQ2,subQ1,subQ0]),TDD([makeQuery(id+"F4.opChamfer","BLEND_EDGE",EDGE,{"blendedFrom":[makeQuery(id+"F3.opExtrude","CAP_EDGE",EDGE,{"disambiguationData":[OSD([subQ17,subQ16,subQ15,subQ14,subQ13,subQ12,subQ11,subQ10,subQ9,subQ8,subQ7,subQ6,subQ5,subQ4,subQ3,subQ2,subQ1,subQ0]),TDD([makeQuery(id+"F2.opChamfer","BLEND_EDGE",EDGE,{"blendedFrom":[makeQuery(id+"F1.opExtrude","CAP_EDGE",EDGE,{"disambiguationData":[OSD([subQ9])],"isStart":false}),makeQuery(id+"F1.opExtrude","CAP_FACE",FACE,{"disambiguationData":[OSD([subQ17,subQ16,subQ15,subQ14,subQ13,subQ12,subQ11,subQ10,subQ9,subQ8,subQ7,subQ6,subQ5,subQ4,subQ3,subQ2,subQ1,subQ0])],"isStart":false})],"blendedInto":[makeQuery(id+"F1.opExtrude","CAP_FACE",FACE,{"disambiguationData":[OSD([subQ17,subQ16,subQ15,subQ14,subQ13,subQ12,subQ11,subQ10,subQ9,subQ8,subQ7,subQ6,subQ5,subQ4,subQ3,subQ2,subQ1,subQ0])],"isStart":false})]})])],"isStart":false}),makeQuery(id+"F3.opExtrude","CAP_FACE",FACE,{"disambiguationData":[OSD([subQ17,subQ16,subQ15,subQ14,subQ13,subQ12,subQ11,subQ10,subQ9,subQ8,subQ7,subQ6,subQ5,subQ4,subQ3,subQ2,subQ1,subQ0])],"isStart":false})],"blendedInto":[makeQuery(id+"F3.opExtrude","CAP_FACE",FACE,{"disambiguationData":[OSD([subQ17,subQ16,subQ15,subQ14,subQ13,subQ12,subQ11,subQ10,subQ9,subQ8,subQ7,subQ6,subQ5,subQ4,subQ3,subQ2,subQ1,subQ0])],"isStart":false})]})])],"isStart":false}),makeQuery(id+"F5.opExtrude","CAP_FACE",FACE,{"disambiguationData":[OSD([subQ17,subQ16,subQ15,subQ14,subQ13,subQ12,subQ11,subQ10,subQ9,subQ8,subQ7,subQ6,subQ5,subQ4,subQ3,subQ2,subQ1,subQ0])],"isStart":false})],"blendedInto":[makeQuery(id+"F5.opExtrude","CAP_FACE",FACE,{"disambiguationData":[OSD([subQ17,subQ16,subQ15,subQ14,subQ13,subQ12,subQ11,subQ10,subQ9,subQ8,subQ7,subQ6,subQ5,subQ4,subQ3,subQ2,subQ1,subQ0])],"isStart":false})]})])],"isStart":false});}
            var Q2;
            {var subQ0=sQuery(id+"F0.wireOp",EDGE,"E3.4");var subQ1=sQuery(id+"F0.wireOp",EDGE,"E3.3");var subQ2=sQuery(id+"F0.wireOp",EDGE,"E3.2");var subQ3=sQuery(id+"F0.wireOp",EDGE,"E3.1");var subQ4=sQuery(id+"F0.wireOp",EDGE,"E2.5");var subQ5=sQuery(id+"F0.wireOp",EDGE,"E2.4");var subQ6=sQuery(id+"F0.wireOp",EDGE,"E2.3");var subQ7=sQuery(id+"F0.wireOp",EDGE,"E2.2");var subQ8=sQuery(id+"F0.wireOp",EDGE,"E1.4");var subQ9=sQuery(id+"F0.wireOp",EDGE,"E1.3");var subQ10=sQuery(id+"F0.wireOp",EDGE,"E1.2");var subQ11=sQuery(id+"F0.wireOp",EDGE,"E1.1");var subQ12=sQuery(id+"F0.wireOp",EDGE,"E0.5");var subQ13=sQuery(id+"F0.wireOp",EDGE,"E0.4");var subQ14=sQuery(id+"F0.wireOp",EDGE,"E0.3");var subQ15=sQuery(id+"F0.wireOp",EDGE,"E0.2");var subQ16=sQuery(id+"F0.wireOp",EDGE,"E0.1");var subQ17=sQuery(id+"F0.wireOp",EDGE,"E0.0");Q2=makeQuery(id+"F7.opExtrude","CAP_EDGE",EDGE,{"disambiguationData":[OSD([subQ17,subQ16,subQ15,subQ14,subQ13,subQ12,subQ11,subQ10,subQ9,subQ8,subQ7,subQ6,subQ5,subQ4,subQ3,subQ2,subQ1,subQ0]),TDD([makeQuery(id+"F6.opChamfer","BLEND_EDGE",EDGE,{"blendedFrom":[makeQuery(id+"F5.opExtrude","CAP_EDGE",EDGE,{"disambiguationData":[OSD([subQ17,subQ16,subQ15,subQ14,subQ13,subQ12,subQ11,subQ10,subQ9,subQ8,subQ7,subQ6,subQ5,subQ4,subQ3,subQ2,subQ1,subQ0]),TDD([makeQuery(id+"F4.opChamfer","BLEND_EDGE",EDGE,{"blendedFrom":[makeQuery(id+"F3.opExtrude","CAP_EDGE",EDGE,{"disambiguationData":[OSD([subQ17,subQ16,subQ15,subQ14,subQ13,subQ12,subQ11,subQ10,subQ9,subQ8,subQ7,subQ6,subQ5,subQ4,subQ3,subQ2,subQ1,subQ0]),TDD([makeQuery(id+"F2.opChamfer","BLEND_EDGE",EDGE,{"blendedFrom":[makeQuery(id+"F1.opExtrude","CAP_EDGE",EDGE,{"disambiguationData":[OSD([subQ10])],"isStart":false}),makeQuery(id+"F1.opExtrude","CAP_FACE",FACE,{"disambiguationData":[OSD([subQ17,subQ16,subQ15,subQ14,subQ13,subQ12,subQ11,subQ10,subQ9,subQ8,subQ7,subQ6,subQ5,subQ4,subQ3,subQ2,subQ1,subQ0])],"isStart":false})],"blendedInto":[makeQuery(id+"F1.opExtrude","CAP_FACE",FACE,{"disambiguationData":[OSD([subQ17,subQ16,subQ15,subQ14,subQ13,subQ12,subQ11,subQ10,subQ9,subQ8,subQ7,subQ6,subQ5,subQ4,subQ3,subQ2,subQ1,subQ0])],"isStart":false})]})])],"isStart":false}),makeQuery(id+"F3.opExtrude","CAP_FACE",FACE,{"disambiguationData":[OSD([subQ17,subQ16,subQ15,subQ14,subQ13,subQ12,subQ11,subQ10,subQ9,subQ8,subQ7,subQ6,subQ5,subQ4,subQ3,subQ2,subQ1,subQ0])],"isStart":false})],"blendedInto":[makeQuery(id+"F3.opExtrude","CAP_FACE",FACE,{"disambiguationData":[OSD([subQ17,subQ16,subQ15,subQ14,subQ13,subQ12,subQ11,subQ10,subQ9,subQ8,subQ7,subQ6,subQ5,subQ4,subQ3,subQ2,subQ1,subQ0])],"isStart":false})]})])],"isStart":false}),makeQuery(id+"F5.opExtrude","CAP_FACE",FACE,{"disambiguationData":[OSD([subQ17,subQ16,subQ15,subQ14,subQ13,subQ12,subQ11,subQ10,subQ9,subQ8,subQ7,subQ6,subQ5,subQ4,subQ3,subQ2,subQ1,subQ0])],"isStart":false})],"blendedInto":[makeQuery(id+"F5.opExtrude","CAP_FACE",FACE,{"disambiguationData":[OSD([subQ17,subQ16,subQ15,subQ14,subQ13,subQ12,subQ11,subQ10,subQ9,subQ8,subQ7,subQ6,subQ5,subQ4,subQ3,subQ2,subQ1,subQ0])],"isStart":false})]})])],"isStart":false});}
            var Q3;
            {var subQ0=sQuery(id+"F0.wireOp",EDGE,"E3.4");var subQ1=sQuery(id+"F0.wireOp",EDGE,"E3.3");var subQ2=sQuery(id+"F0.wireOp",EDGE,"E3.2");var subQ3=sQuery(id+"F0.wireOp",EDGE,"E3.1");var subQ4=sQuery(id+"F0.wireOp",EDGE,"E2.5");var subQ5=sQuery(id+"F0.wireOp",EDGE,"E2.4");var subQ6=sQuery(id+"F0.wireOp",EDGE,"E2.3");var subQ7=sQuery(id+"F0.wireOp",EDGE,"E2.2");var subQ8=sQuery(id+"F0.wireOp",EDGE,"E1.4");var subQ9=sQuery(id+"F0.wireOp",EDGE,"E1.3");var subQ10=sQuery(id+"F0.wireOp",EDGE,"E1.2");var subQ11=sQuery(id+"F0.wireOp",EDGE,"E1.1");var subQ12=sQuery(id+"F0.wireOp",EDGE,"E0.5");var subQ13=sQuery(id+"F0.wireOp",EDGE,"E0.4");var subQ14=sQuery(id+"F0.wireOp",EDGE,"E0.3");var subQ15=sQuery(id+"F0.wireOp",EDGE,"E0.2");var subQ16=sQuery(id+"F0.wireOp",EDGE,"E0.1");var subQ17=sQuery(id+"F0.wireOp",EDGE,"E0.0");Q3=makeQuery(id+"F7.opExtrude","CAP_EDGE",EDGE,{"disambiguationData":[OSD([subQ17,subQ16,subQ15,subQ14,subQ13,subQ12,subQ11,subQ10,subQ9,subQ8,subQ7,subQ6,subQ5,subQ4,subQ3,subQ2,subQ1,subQ0]),TDD([makeQuery(id+"F6.opChamfer","BLEND_EDGE",EDGE,{"blendedFrom":[makeQuery(id+"F5.opExtrude","CAP_EDGE",EDGE,{"disambiguationData":[OSD([subQ17,subQ16,subQ15,subQ14,subQ13,subQ12,subQ11,subQ10,subQ9,subQ8,subQ7,subQ6,subQ5,subQ4,subQ3,subQ2,subQ1,subQ0]),TDD([makeQuery(id+"F4.opChamfer","BLEND_EDGE",EDGE,{"blendedFrom":[makeQuery(id+"F3.opExtrude","CAP_EDGE",EDGE,{"disambiguationData":[OSD([subQ17,subQ16,subQ15,subQ14,subQ13,subQ12,subQ11,subQ10,subQ9,subQ8,subQ7,subQ6,subQ5,subQ4,subQ3,subQ2,subQ1,subQ0]),TDD([makeQuery(id+"F2.opChamfer","BLEND_EDGE",EDGE,{"blendedFrom":[makeQuery(id+"F1.opExtrude","CAP_EDGE",EDGE,{"disambiguationData":[OSD([subQ11])],"isStart":false}),makeQuery(id+"F1.opExtrude","CAP_FACE",FACE,{"disambiguationData":[OSD([subQ17,subQ16,subQ15,subQ14,subQ13,subQ12,subQ11,subQ10,subQ9,subQ8,subQ7,subQ6,subQ5,subQ4,subQ3,subQ2,subQ1,subQ0])],"isStart":false})],"blendedInto":[makeQuery(id+"F1.opExtrude","CAP_FACE",FACE,{"disambiguationData":[OSD([subQ17,subQ16,subQ15,subQ14,subQ13,subQ12,subQ11,subQ10,subQ9,subQ8,subQ7,subQ6,subQ5,subQ4,subQ3,subQ2,subQ1,subQ0])],"isStart":false})]})])],"isStart":false}),makeQuery(id+"F3.opExtrude","CAP_FACE",FACE,{"disambiguationData":[OSD([subQ17,subQ16,subQ15,subQ14,subQ13,subQ12,subQ11,subQ10,subQ9,subQ8,subQ7,subQ6,subQ5,subQ4,subQ3,subQ2,subQ1,subQ0])],"isStart":false})],"blendedInto":[makeQuery(id+"F3.opExtrude","CAP_FACE",FACE,{"disambiguationData":[OSD([subQ17,subQ16,subQ15,subQ14,subQ13,subQ12,subQ11,subQ10,subQ9,subQ8,subQ7,subQ6,subQ5,subQ4,subQ3,subQ2,subQ1,subQ0])],"isStart":false})]})])],"isStart":false}),makeQuery(id+"F5.opExtrude","CAP_FACE",FACE,{"disambiguationData":[OSD([subQ17,subQ16,subQ15,subQ14,subQ13,subQ12,subQ11,subQ10,subQ9,subQ8,subQ7,subQ6,subQ5,subQ4,subQ3,subQ2,subQ1,subQ0])],"isStart":false})],"blendedInto":[makeQuery(id+"F5.opExtrude","CAP_FACE",FACE,{"disambiguationData":[OSD([subQ17,subQ16,subQ15,subQ14,subQ13,subQ12,subQ11,subQ10,subQ9,subQ8,subQ7,subQ6,subQ5,subQ4,subQ3,subQ2,subQ1,subQ0])],"isStart":false})]})])],"isStart":false});}
            var Q4;
            {var subQ0=sQuery(id+"F0.wireOp",EDGE,"E3.4");var subQ1=sQuery(id+"F0.wireOp",EDGE,"E3.3");var subQ2=sQuery(id+"F0.wireOp",EDGE,"E3.2");var subQ3=sQuery(id+"F0.wireOp",EDGE,"E3.1");var subQ4=sQuery(id+"F0.wireOp",EDGE,"E2.5");var subQ5=sQuery(id+"F0.wireOp",EDGE,"E2.4");var subQ6=sQuery(id+"F0.wireOp",EDGE,"E2.3");var subQ7=sQuery(id+"F0.wireOp",EDGE,"E2.2");var subQ8=sQuery(id+"F0.wireOp",EDGE,"E1.4");var subQ9=sQuery(id+"F0.wireOp",EDGE,"E1.3");var subQ10=sQuery(id+"F0.wireOp",EDGE,"E1.2");var subQ11=sQuery(id+"F0.wireOp",EDGE,"E1.1");var subQ12=sQuery(id+"F0.wireOp",EDGE,"E0.5");var subQ13=sQuery(id+"F0.wireOp",EDGE,"E0.4");var subQ14=sQuery(id+"F0.wireOp",EDGE,"E0.3");var subQ15=sQuery(id+"F0.wireOp",EDGE,"E0.2");var subQ16=sQuery(id+"F0.wireOp",EDGE,"E0.1");var subQ17=sQuery(id+"F0.wireOp",EDGE,"E0.0");Q4=makeQuery(id+"F7.opExtrude","CAP_EDGE",EDGE,{"disambiguationData":[OSD([subQ17,subQ16,subQ15,subQ14,subQ13,subQ12,subQ11,subQ10,subQ9,subQ8,subQ7,subQ6,subQ5,subQ4,subQ3,subQ2,subQ1,subQ0]),TDD([makeQuery(id+"F6.opChamfer","BLEND_EDGE",EDGE,{"blendedFrom":[makeQuery(id+"F5.opExtrude","CAP_EDGE",EDGE,{"disambiguationData":[OSD([subQ17,subQ16,subQ15,subQ14,subQ13,subQ12,subQ11,subQ10,subQ9,subQ8,subQ7,subQ6,subQ5,subQ4,subQ3,subQ2,subQ1,subQ0]),TDD([makeQuery(id+"F4.opChamfer","BLEND_EDGE",EDGE,{"blendedFrom":[makeQuery(id+"F3.opExtrude","CAP_EDGE",EDGE,{"disambiguationData":[OSD([subQ17,subQ16,subQ15,subQ14,subQ13,subQ12,subQ11,subQ10,subQ9,subQ8,subQ7,subQ6,subQ5,subQ4,subQ3,subQ2,subQ1,subQ0]),TDD([makeQuery(id+"F2.opChamfer","BLEND_EDGE",EDGE,{"blendedFrom":[makeQuery(id+"F1.opExtrude","CAP_EDGE",EDGE,{"disambiguationData":[OSD([subQ0])],"isStart":false}),makeQuery(id+"F1.opExtrude","CAP_FACE",FACE,{"disambiguationData":[OSD([subQ17,subQ16,subQ15,subQ14,subQ13,subQ12,subQ11,subQ10,subQ9,subQ8,subQ7,subQ6,subQ5,subQ4,subQ3,subQ2,subQ1,subQ0])],"isStart":false})],"blendedInto":[makeQuery(id+"F1.opExtrude","CAP_FACE",FACE,{"disambiguationData":[OSD([subQ17,subQ16,subQ15,subQ14,subQ13,subQ12,subQ11,subQ10,subQ9,subQ8,subQ7,subQ6,subQ5,subQ4,subQ3,subQ2,subQ1,subQ0])],"isStart":false})]})])],"isStart":false}),makeQuery(id+"F3.opExtrude","CAP_FACE",FACE,{"disambiguationData":[OSD([subQ17,subQ16,subQ15,subQ14,subQ13,subQ12,subQ11,subQ10,subQ9,subQ8,subQ7,subQ6,subQ5,subQ4,subQ3,subQ2,subQ1,subQ0])],"isStart":false})],"blendedInto":[makeQuery(id+"F3.opExtrude","CAP_FACE",FACE,{"disambiguationData":[OSD([subQ17,subQ16,subQ15,subQ14,subQ13,subQ12,subQ11,subQ10,subQ9,subQ8,subQ7,subQ6,subQ5,subQ4,subQ3,subQ2,subQ1,subQ0])],"isStart":false})]})])],"isStart":false}),makeQuery(id+"F5.opExtrude","CAP_FACE",FACE,{"disambiguationData":[OSD([subQ17,subQ16,subQ15,subQ14,subQ13,subQ12,subQ11,subQ10,subQ9,subQ8,subQ7,subQ6,subQ5,subQ4,subQ3,subQ2,subQ1,subQ0])],"isStart":false})],"blendedInto":[makeQuery(id+"F5.opExtrude","CAP_FACE",FACE,{"disambiguationData":[OSD([subQ17,subQ16,subQ15,subQ14,subQ13,subQ12,subQ11,subQ10,subQ9,subQ8,subQ7,subQ6,subQ5,subQ4,subQ3,subQ2,subQ1,subQ0])],"isStart":false})]})])],"isStart":false});}
            var Q5;
            {var subQ0=sQuery(id+"F0.wireOp",EDGE,"E3.4");var subQ1=sQuery(id+"F0.wireOp",EDGE,"E3.3");var subQ2=sQuery(id+"F0.wireOp",EDGE,"E3.2");var subQ3=sQuery(id+"F0.wireOp",EDGE,"E3.1");var subQ4=sQuery(id+"F0.wireOp",EDGE,"E2.5");var subQ5=sQuery(id+"F0.wireOp",EDGE,"E2.4");var subQ6=sQuery(id+"F0.wireOp",EDGE,"E2.3");var subQ7=sQuery(id+"F0.wireOp",EDGE,"E2.2");var subQ8=sQuery(id+"F0.wireOp",EDGE,"E1.4");var subQ9=sQuery(id+"F0.wireOp",EDGE,"E1.3");var subQ10=sQuery(id+"F0.wireOp",EDGE,"E1.2");var subQ11=sQuery(id+"F0.wireOp",EDGE,"E1.1");var subQ12=sQuery(id+"F0.wireOp",EDGE,"E0.5");var subQ13=sQuery(id+"F0.wireOp",EDGE,"E0.4");var subQ14=sQuery(id+"F0.wireOp",EDGE,"E0.3");var subQ15=sQuery(id+"F0.wireOp",EDGE,"E0.2");var subQ16=sQuery(id+"F0.wireOp",EDGE,"E0.1");var subQ17=sQuery(id+"F0.wireOp",EDGE,"E0.0");Q5=makeQuery(id+"F7.opExtrude","CAP_EDGE",EDGE,{"disambiguationData":[OSD([subQ17,subQ16,subQ15,subQ14,subQ13,subQ12,subQ11,subQ10,subQ9,subQ8,subQ7,subQ6,subQ5,subQ4,subQ3,subQ2,subQ1,subQ0]),TDD([makeQuery(id+"F6.opChamfer","BLEND_EDGE",EDGE,{"blendedFrom":[makeQuery(id+"F5.opExtrude","CAP_EDGE",EDGE,{"disambiguationData":[OSD([subQ17,subQ16,subQ15,subQ14,subQ13,subQ12,subQ11,subQ10,subQ9,subQ8,subQ7,subQ6,subQ5,subQ4,subQ3,subQ2,subQ1,subQ0]),TDD([makeQuery(id+"F4.opChamfer","BLEND_EDGE",EDGE,{"blendedFrom":[makeQuery(id+"F3.opExtrude","CAP_EDGE",EDGE,{"disambiguationData":[OSD([subQ17,subQ16,subQ15,subQ14,subQ13,subQ12,subQ11,subQ10,subQ9,subQ8,subQ7,subQ6,subQ5,subQ4,subQ3,subQ2,subQ1,subQ0]),TDD([makeQuery(id+"F2.opChamfer","BLEND_EDGE",EDGE,{"blendedFrom":[makeQuery(id+"F1.opExtrude","CAP_EDGE",EDGE,{"disambiguationData":[OSD([subQ1])],"isStart":false}),makeQuery(id+"F1.opExtrude","CAP_FACE",FACE,{"disambiguationData":[OSD([subQ17,subQ16,subQ15,subQ14,subQ13,subQ12,subQ11,subQ10,subQ9,subQ8,subQ7,subQ6,subQ5,subQ4,subQ3,subQ2,subQ1,subQ0])],"isStart":false})],"blendedInto":[makeQuery(id+"F1.opExtrude","CAP_FACE",FACE,{"disambiguationData":[OSD([subQ17,subQ16,subQ15,subQ14,subQ13,subQ12,subQ11,subQ10,subQ9,subQ8,subQ7,subQ6,subQ5,subQ4,subQ3,subQ2,subQ1,subQ0])],"isStart":false})]})])],"isStart":false}),makeQuery(id+"F3.opExtrude","CAP_FACE",FACE,{"disambiguationData":[OSD([subQ17,subQ16,subQ15,subQ14,subQ13,subQ12,subQ11,subQ10,subQ9,subQ8,subQ7,subQ6,subQ5,subQ4,subQ3,subQ2,subQ1,subQ0])],"isStart":false})],"blendedInto":[makeQuery(id+"F3.opExtrude","CAP_FACE",FACE,{"disambiguationData":[OSD([subQ17,subQ16,subQ15,subQ14,subQ13,subQ12,subQ11,subQ10,subQ9,subQ8,subQ7,subQ6,subQ5,subQ4,subQ3,subQ2,subQ1,subQ0])],"isStart":false})]})])],"isStart":false}),makeQuery(id+"F5.opExtrude","CAP_FACE",FACE,{"disambiguationData":[OSD([subQ17,subQ16,subQ15,subQ14,subQ13,subQ12,subQ11,subQ10,subQ9,subQ8,subQ7,subQ6,subQ5,subQ4,subQ3,subQ2,subQ1,subQ0])],"isStart":false})],"blendedInto":[makeQuery(id+"F5.opExtrude","CAP_FACE",FACE,{"disambiguationData":[OSD([subQ17,subQ16,subQ15,subQ14,subQ13,subQ12,subQ11,subQ10,subQ9,subQ8,subQ7,subQ6,subQ5,subQ4,subQ3,subQ2,subQ1,subQ0])],"isStart":false})]})])],"isStart":false});}
            var Q6;
            {var subQ0=sQuery(id+"F0.wireOp",EDGE,"E3.4");var subQ1=sQuery(id+"F0.wireOp",EDGE,"E3.3");var subQ2=sQuery(id+"F0.wireOp",EDGE,"E3.2");var subQ3=sQuery(id+"F0.wireOp",EDGE,"E3.1");var subQ4=sQuery(id+"F0.wireOp",EDGE,"E2.5");var subQ5=sQuery(id+"F0.wireOp",EDGE,"E2.4");var subQ6=sQuery(id+"F0.wireOp",EDGE,"E2.3");var subQ7=sQuery(id+"F0.wireOp",EDGE,"E2.2");var subQ8=sQuery(id+"F0.wireOp",EDGE,"E1.4");var subQ9=sQuery(id+"F0.wireOp",EDGE,"E1.3");var subQ10=sQuery(id+"F0.wireOp",EDGE,"E1.2");var subQ11=sQuery(id+"F0.wireOp",EDGE,"E1.1");var subQ12=sQuery(id+"F0.wireOp",EDGE,"E0.5");var subQ13=sQuery(id+"F0.wireOp",EDGE,"E0.4");var subQ14=sQuery(id+"F0.wireOp",EDGE,"E0.3");var subQ15=sQuery(id+"F0.wireOp",EDGE,"E0.2");var subQ16=sQuery(id+"F0.wireOp",EDGE,"E0.1");var subQ17=sQuery(id+"F0.wireOp",EDGE,"E0.0");Q6=makeQuery(id+"F7.opExtrude","CAP_EDGE",EDGE,{"disambiguationData":[OSD([subQ17,subQ16,subQ15,subQ14,subQ13,subQ12,subQ11,subQ10,subQ9,subQ8,subQ7,subQ6,subQ5,subQ4,subQ3,subQ2,subQ1,subQ0]),TDD([makeQuery(id+"F6.opChamfer","BLEND_EDGE",EDGE,{"blendedFrom":[makeQuery(id+"F5.opExtrude","CAP_EDGE",EDGE,{"disambiguationData":[OSD([subQ17,subQ16,subQ15,subQ14,subQ13,subQ12,subQ11,subQ10,subQ9,subQ8,subQ7,subQ6,subQ5,subQ4,subQ3,subQ2,subQ1,subQ0]),TDD([makeQuery(id+"F4.opChamfer","BLEND_EDGE",EDGE,{"blendedFrom":[makeQuery(id+"F3.opExtrude","CAP_EDGE",EDGE,{"disambiguationData":[OSD([subQ17,subQ16,subQ15,subQ14,subQ13,subQ12,subQ11,subQ10,subQ9,subQ8,subQ7,subQ6,subQ5,subQ4,subQ3,subQ2,subQ1,subQ0]),TDD([makeQuery(id+"F2.opChamfer","BLEND_EDGE",EDGE,{"blendedFrom":[makeQuery(id+"F1.opExtrude","CAP_EDGE",EDGE,{"disambiguationData":[OSD([subQ2])],"isStart":false}),makeQuery(id+"F1.opExtrude","CAP_FACE",FACE,{"disambiguationData":[OSD([subQ17,subQ16,subQ15,subQ14,subQ13,subQ12,subQ11,subQ10,subQ9,subQ8,subQ7,subQ6,subQ5,subQ4,subQ3,subQ2,subQ1,subQ0])],"isStart":false})],"blendedInto":[makeQuery(id+"F1.opExtrude","CAP_FACE",FACE,{"disambiguationData":[OSD([subQ17,subQ16,subQ15,subQ14,subQ13,subQ12,subQ11,subQ10,subQ9,subQ8,subQ7,subQ6,subQ5,subQ4,subQ3,subQ2,subQ1,subQ0])],"isStart":false})]})])],"isStart":false}),makeQuery(id+"F3.opExtrude","CAP_FACE",FACE,{"disambiguationData":[OSD([subQ17,subQ16,subQ15,subQ14,subQ13,subQ12,subQ11,subQ10,subQ9,subQ8,subQ7,subQ6,subQ5,subQ4,subQ3,subQ2,subQ1,subQ0])],"isStart":false})],"blendedInto":[makeQuery(id+"F3.opExtrude","CAP_FACE",FACE,{"disambiguationData":[OSD([subQ17,subQ16,subQ15,subQ14,subQ13,subQ12,subQ11,subQ10,subQ9,subQ8,subQ7,subQ6,subQ5,subQ4,subQ3,subQ2,subQ1,subQ0])],"isStart":false})]})])],"isStart":false}),makeQuery(id+"F5.opExtrude","CAP_FACE",FACE,{"disambiguationData":[OSD([subQ17,subQ16,subQ15,subQ14,subQ13,subQ12,subQ11,subQ10,subQ9,subQ8,subQ7,subQ6,subQ5,subQ4,subQ3,subQ2,subQ1,subQ0])],"isStart":false})],"blendedInto":[makeQuery(id+"F5.opExtrude","CAP_FACE",FACE,{"disambiguationData":[OSD([subQ17,subQ16,subQ15,subQ14,subQ13,subQ12,subQ11,subQ10,subQ9,subQ8,subQ7,subQ6,subQ5,subQ4,subQ3,subQ2,subQ1,subQ0])],"isStart":false})]})])],"isStart":false});}
            var Q7;
            {var subQ0=sQuery(id+"F0.wireOp",EDGE,"E3.4");var subQ1=sQuery(id+"F0.wireOp",EDGE,"E3.3");var subQ2=sQuery(id+"F0.wireOp",EDGE,"E3.2");var subQ3=sQuery(id+"F0.wireOp",EDGE,"E3.1");var subQ4=sQuery(id+"F0.wireOp",EDGE,"E2.5");var subQ5=sQuery(id+"F0.wireOp",EDGE,"E2.4");var subQ6=sQuery(id+"F0.wireOp",EDGE,"E2.3");var subQ7=sQuery(id+"F0.wireOp",EDGE,"E2.2");var subQ8=sQuery(id+"F0.wireOp",EDGE,"E1.4");var subQ9=sQuery(id+"F0.wireOp",EDGE,"E1.3");var subQ10=sQuery(id+"F0.wireOp",EDGE,"E1.2");var subQ11=sQuery(id+"F0.wireOp",EDGE,"E1.1");var subQ12=sQuery(id+"F0.wireOp",EDGE,"E0.5");var subQ13=sQuery(id+"F0.wireOp",EDGE,"E0.4");var subQ14=sQuery(id+"F0.wireOp",EDGE,"E0.3");var subQ15=sQuery(id+"F0.wireOp",EDGE,"E0.2");var subQ16=sQuery(id+"F0.wireOp",EDGE,"E0.1");var subQ17=sQuery(id+"F0.wireOp",EDGE,"E0.0");Q7=makeQuery(id+"F7.opExtrude","CAP_EDGE",EDGE,{"disambiguationData":[OSD([subQ17,subQ16,subQ15,subQ14,subQ13,subQ12,subQ11,subQ10,subQ9,subQ8,subQ7,subQ6,subQ5,subQ4,subQ3,subQ2,subQ1,subQ0]),TDD([makeQuery(id+"F6.opChamfer","BLEND_EDGE",EDGE,{"blendedFrom":[makeQuery(id+"F5.opExtrude","CAP_EDGE",EDGE,{"disambiguationData":[OSD([subQ17,subQ16,subQ15,subQ14,subQ13,subQ12,subQ11,subQ10,subQ9,subQ8,subQ7,subQ6,subQ5,subQ4,subQ3,subQ2,subQ1,subQ0]),TDD([makeQuery(id+"F4.opChamfer","BLEND_EDGE",EDGE,{"blendedFrom":[makeQuery(id+"F3.opExtrude","CAP_EDGE",EDGE,{"disambiguationData":[OSD([subQ17,subQ16,subQ15,subQ14,subQ13,subQ12,subQ11,subQ10,subQ9,subQ8,subQ7,subQ6,subQ5,subQ4,subQ3,subQ2,subQ1,subQ0]),TDD([makeQuery(id+"F2.opChamfer","BLEND_EDGE",EDGE,{"blendedFrom":[makeQuery(id+"F1.opExtrude","CAP_EDGE",EDGE,{"disambiguationData":[OSD([subQ3])],"isStart":false}),makeQuery(id+"F1.opExtrude","CAP_FACE",FACE,{"disambiguationData":[OSD([subQ17,subQ16,subQ15,subQ14,subQ13,subQ12,subQ11,subQ10,subQ9,subQ8,subQ7,subQ6,subQ5,subQ4,subQ3,subQ2,subQ1,subQ0])],"isStart":false})],"blendedInto":[makeQuery(id+"F1.opExtrude","CAP_FACE",FACE,{"disambiguationData":[OSD([subQ17,subQ16,subQ15,subQ14,subQ13,subQ12,subQ11,subQ10,subQ9,subQ8,subQ7,subQ6,subQ5,subQ4,subQ3,subQ2,subQ1,subQ0])],"isStart":false})]})])],"isStart":false}),makeQuery(id+"F3.opExtrude","CAP_FACE",FACE,{"disambiguationData":[OSD([subQ17,subQ16,subQ15,subQ14,subQ13,subQ12,subQ11,subQ10,subQ9,subQ8,subQ7,subQ6,subQ5,subQ4,subQ3,subQ2,subQ1,subQ0])],"isStart":false})],"blendedInto":[makeQuery(id+"F3.opExtrude","CAP_FACE",FACE,{"disambiguationData":[OSD([subQ17,subQ16,subQ15,subQ14,subQ13,subQ12,subQ11,subQ10,subQ9,subQ8,subQ7,subQ6,subQ5,subQ4,subQ3,subQ2,subQ1,subQ0])],"isStart":false})]})])],"isStart":false}),makeQuery(id+"F5.opExtrude","CAP_FACE",FACE,{"disambiguationData":[OSD([subQ17,subQ16,subQ15,subQ14,subQ13,subQ12,subQ11,subQ10,subQ9,subQ8,subQ7,subQ6,subQ5,subQ4,subQ3,subQ2,subQ1,subQ0])],"isStart":false})],"blendedInto":[makeQuery(id+"F5.opExtrude","CAP_FACE",FACE,{"disambiguationData":[OSD([subQ17,subQ16,subQ15,subQ14,subQ13,subQ12,subQ11,subQ10,subQ9,subQ8,subQ7,subQ6,subQ5,subQ4,subQ3,subQ2,subQ1,subQ0])],"isStart":false})]})])],"isStart":false});}
            var Q8;
            {var subQ0=sQuery(id+"F0.wireOp",EDGE,"E3.4");var subQ1=sQuery(id+"F0.wireOp",EDGE,"E3.3");var subQ2=sQuery(id+"F0.wireOp",EDGE,"E3.2");var subQ3=sQuery(id+"F0.wireOp",EDGE,"E3.1");var subQ4=sQuery(id+"F0.wireOp",EDGE,"E2.5");var subQ5=sQuery(id+"F0.wireOp",EDGE,"E2.4");var subQ6=sQuery(id+"F0.wireOp",EDGE,"E2.3");var subQ7=sQuery(id+"F0.wireOp",EDGE,"E2.2");var subQ8=sQuery(id+"F0.wireOp",EDGE,"E1.4");var subQ9=sQuery(id+"F0.wireOp",EDGE,"E1.3");var subQ10=sQuery(id+"F0.wireOp",EDGE,"E1.2");var subQ11=sQuery(id+"F0.wireOp",EDGE,"E1.1");var subQ12=sQuery(id+"F0.wireOp",EDGE,"E0.5");var subQ13=sQuery(id+"F0.wireOp",EDGE,"E0.4");var subQ14=sQuery(id+"F0.wireOp",EDGE,"E0.3");var subQ15=sQuery(id+"F0.wireOp",EDGE,"E0.2");var subQ16=sQuery(id+"F0.wireOp",EDGE,"E0.1");var subQ17=sQuery(id+"F0.wireOp",EDGE,"E0.0");Q8=makeQuery(id+"F7.opExtrude","CAP_EDGE",EDGE,{"disambiguationData":[OSD([subQ17,subQ16,subQ15,subQ14,subQ13,subQ12,subQ11,subQ10,subQ9,subQ8,subQ7,subQ6,subQ5,subQ4,subQ3,subQ2,subQ1,subQ0]),TDD([makeQuery(id+"F6.opChamfer","BLEND_EDGE",EDGE,{"blendedFrom":[makeQuery(id+"F5.opExtrude","CAP_EDGE",EDGE,{"disambiguationData":[OSD([subQ17,subQ16,subQ15,subQ14,subQ13,subQ12,subQ11,subQ10,subQ9,subQ8,subQ7,subQ6,subQ5,subQ4,subQ3,subQ2,subQ1,subQ0]),TDD([makeQuery(id+"F4.opChamfer","BLEND_EDGE",EDGE,{"blendedFrom":[makeQuery(id+"F3.opExtrude","CAP_EDGE",EDGE,{"disambiguationData":[OSD([subQ17,subQ16,subQ15,subQ14,subQ13,subQ12,subQ11,subQ10,subQ9,subQ8,subQ7,subQ6,subQ5,subQ4,subQ3,subQ2,subQ1,subQ0]),TDD([makeQuery(id+"F2.opChamfer","BLEND_EDGE",EDGE,{"blendedFrom":[makeQuery(id+"F1.opExtrude","CAP_EDGE",EDGE,{"disambiguationData":[OSD([subQ4])],"isStart":false}),makeQuery(id+"F1.opExtrude","CAP_FACE",FACE,{"disambiguationData":[OSD([subQ17,subQ16,subQ15,subQ14,subQ13,subQ12,subQ11,subQ10,subQ9,subQ8,subQ7,subQ6,subQ5,subQ4,subQ3,subQ2,subQ1,subQ0])],"isStart":false})],"blendedInto":[makeQuery(id+"F1.opExtrude","CAP_FACE",FACE,{"disambiguationData":[OSD([subQ17,subQ16,subQ15,subQ14,subQ13,subQ12,subQ11,subQ10,subQ9,subQ8,subQ7,subQ6,subQ5,subQ4,subQ3,subQ2,subQ1,subQ0])],"isStart":false})]})])],"isStart":false}),makeQuery(id+"F3.opExtrude","CAP_FACE",FACE,{"disambiguationData":[OSD([subQ17,subQ16,subQ15,subQ14,subQ13,subQ12,subQ11,subQ10,subQ9,subQ8,subQ7,subQ6,subQ5,subQ4,subQ3,subQ2,subQ1,subQ0])],"isStart":false})],"blendedInto":[makeQuery(id+"F3.opExtrude","CAP_FACE",FACE,{"disambiguationData":[OSD([subQ17,subQ16,subQ15,subQ14,subQ13,subQ12,subQ11,subQ10,subQ9,subQ8,subQ7,subQ6,subQ5,subQ4,subQ3,subQ2,subQ1,subQ0])],"isStart":false})]})])],"isStart":false}),makeQuery(id+"F5.opExtrude","CAP_FACE",FACE,{"disambiguationData":[OSD([subQ17,subQ16,subQ15,subQ14,subQ13,subQ12,subQ11,subQ10,subQ9,subQ8,subQ7,subQ6,subQ5,subQ4,subQ3,subQ2,subQ1,subQ0])],"isStart":false})],"blendedInto":[makeQuery(id+"F5.opExtrude","CAP_FACE",FACE,{"disambiguationData":[OSD([subQ17,subQ16,subQ15,subQ14,subQ13,subQ12,subQ11,subQ10,subQ9,subQ8,subQ7,subQ6,subQ5,subQ4,subQ3,subQ2,subQ1,subQ0])],"isStart":false})]})])],"isStart":false});}
            var Q9;
            {var subQ0=sQuery(id+"F0.wireOp",EDGE,"E3.4");var subQ1=sQuery(id+"F0.wireOp",EDGE,"E3.3");var subQ2=sQuery(id+"F0.wireOp",EDGE,"E3.2");var subQ3=sQuery(id+"F0.wireOp",EDGE,"E3.1");var subQ4=sQuery(id+"F0.wireOp",EDGE,"E2.5");var subQ5=sQuery(id+"F0.wireOp",EDGE,"E2.4");var subQ6=sQuery(id+"F0.wireOp",EDGE,"E2.3");var subQ7=sQuery(id+"F0.wireOp",EDGE,"E2.2");var subQ8=sQuery(id+"F0.wireOp",EDGE,"E1.4");var subQ9=sQuery(id+"F0.wireOp",EDGE,"E1.3");var subQ10=sQuery(id+"F0.wireOp",EDGE,"E1.2");var subQ11=sQuery(id+"F0.wireOp",EDGE,"E1.1");var subQ12=sQuery(id+"F0.wireOp",EDGE,"E0.5");var subQ13=sQuery(id+"F0.wireOp",EDGE,"E0.4");var subQ14=sQuery(id+"F0.wireOp",EDGE,"E0.3");var subQ15=sQuery(id+"F0.wireOp",EDGE,"E0.2");var subQ16=sQuery(id+"F0.wireOp",EDGE,"E0.1");var subQ17=sQuery(id+"F0.wireOp",EDGE,"E0.0");Q9=makeQuery(id+"F7.opExtrude","CAP_EDGE",EDGE,{"disambiguationData":[OSD([subQ17,subQ16,subQ15,subQ14,subQ13,subQ12,subQ11,subQ10,subQ9,subQ8,subQ7,subQ6,subQ5,subQ4,subQ3,subQ2,subQ1,subQ0]),TDD([makeQuery(id+"F6.opChamfer","BLEND_EDGE",EDGE,{"blendedFrom":[makeQuery(id+"F5.opExtrude","CAP_EDGE",EDGE,{"disambiguationData":[OSD([subQ17,subQ16,subQ15,subQ14,subQ13,subQ12,subQ11,subQ10,subQ9,subQ8,subQ7,subQ6,subQ5,subQ4,subQ3,subQ2,subQ1,subQ0]),TDD([makeQuery(id+"F4.opChamfer","BLEND_EDGE",EDGE,{"blendedFrom":[makeQuery(id+"F3.opExtrude","CAP_EDGE",EDGE,{"disambiguationData":[OSD([subQ17,subQ16,subQ15,subQ14,subQ13,subQ12,subQ11,subQ10,subQ9,subQ8,subQ7,subQ6,subQ5,subQ4,subQ3,subQ2,subQ1,subQ0]),TDD([makeQuery(id+"F2.opChamfer","BLEND_EDGE",EDGE,{"blendedFrom":[makeQuery(id+"F1.opExtrude","CAP_EDGE",EDGE,{"disambiguationData":[OSD([subQ7])],"isStart":false}),makeQuery(id+"F1.opExtrude","CAP_FACE",FACE,{"disambiguationData":[OSD([subQ17,subQ16,subQ15,subQ14,subQ13,subQ12,subQ11,subQ10,subQ9,subQ8,subQ7,subQ6,subQ5,subQ4,subQ3,subQ2,subQ1,subQ0])],"isStart":false})],"blendedInto":[makeQuery(id+"F1.opExtrude","CAP_FACE",FACE,{"disambiguationData":[OSD([subQ17,subQ16,subQ15,subQ14,subQ13,subQ12,subQ11,subQ10,subQ9,subQ8,subQ7,subQ6,subQ5,subQ4,subQ3,subQ2,subQ1,subQ0])],"isStart":false})]})])],"isStart":false}),makeQuery(id+"F3.opExtrude","CAP_FACE",FACE,{"disambiguationData":[OSD([subQ17,subQ16,subQ15,subQ14,subQ13,subQ12,subQ11,subQ10,subQ9,subQ8,subQ7,subQ6,subQ5,subQ4,subQ3,subQ2,subQ1,subQ0])],"isStart":false})],"blendedInto":[makeQuery(id+"F3.opExtrude","CAP_FACE",FACE,{"disambiguationData":[OSD([subQ17,subQ16,subQ15,subQ14,subQ13,subQ12,subQ11,subQ10,subQ9,subQ8,subQ7,subQ6,subQ5,subQ4,subQ3,subQ2,subQ1,subQ0])],"isStart":false})]})])],"isStart":false}),makeQuery(id+"F5.opExtrude","CAP_FACE",FACE,{"disambiguationData":[OSD([subQ17,subQ16,subQ15,subQ14,subQ13,subQ12,subQ11,subQ10,subQ9,subQ8,subQ7,subQ6,subQ5,subQ4,subQ3,subQ2,subQ1,subQ0])],"isStart":false})],"blendedInto":[makeQuery(id+"F5.opExtrude","CAP_FACE",FACE,{"disambiguationData":[OSD([subQ17,subQ16,subQ15,subQ14,subQ13,subQ12,subQ11,subQ10,subQ9,subQ8,subQ7,subQ6,subQ5,subQ4,subQ3,subQ2,subQ1,subQ0])],"isStart":false})]})])],"isStart":false});}
            var Q10;
            {var subQ0=sQuery(id+"F0.wireOp",EDGE,"E3.4");var subQ1=sQuery(id+"F0.wireOp",EDGE,"E3.3");var subQ2=sQuery(id+"F0.wireOp",EDGE,"E3.2");var subQ3=sQuery(id+"F0.wireOp",EDGE,"E3.1");var subQ4=sQuery(id+"F0.wireOp",EDGE,"E2.5");var subQ5=sQuery(id+"F0.wireOp",EDGE,"E2.4");var subQ6=sQuery(id+"F0.wireOp",EDGE,"E2.3");var subQ7=sQuery(id+"F0.wireOp",EDGE,"E2.2");var subQ8=sQuery(id+"F0.wireOp",EDGE,"E1.4");var subQ9=sQuery(id+"F0.wireOp",EDGE,"E1.3");var subQ10=sQuery(id+"F0.wireOp",EDGE,"E1.2");var subQ11=sQuery(id+"F0.wireOp",EDGE,"E1.1");var subQ12=sQuery(id+"F0.wireOp",EDGE,"E0.5");var subQ13=sQuery(id+"F0.wireOp",EDGE,"E0.4");var subQ14=sQuery(id+"F0.wireOp",EDGE,"E0.3");var subQ15=sQuery(id+"F0.wireOp",EDGE,"E0.2");var subQ16=sQuery(id+"F0.wireOp",EDGE,"E0.1");var subQ17=sQuery(id+"F0.wireOp",EDGE,"E0.0");Q10=makeQuery(id+"F7.opExtrude","CAP_EDGE",EDGE,{"disambiguationData":[OSD([subQ17,subQ16,subQ15,subQ14,subQ13,subQ12,subQ11,subQ10,subQ9,subQ8,subQ7,subQ6,subQ5,subQ4,subQ3,subQ2,subQ1,subQ0]),TDD([makeQuery(id+"F6.opChamfer","BLEND_EDGE",EDGE,{"blendedFrom":[makeQuery(id+"F5.opExtrude","CAP_EDGE",EDGE,{"disambiguationData":[OSD([subQ17,subQ16,subQ15,subQ14,subQ13,subQ12,subQ11,subQ10,subQ9,subQ8,subQ7,subQ6,subQ5,subQ4,subQ3,subQ2,subQ1,subQ0]),TDD([makeQuery(id+"F4.opChamfer","BLEND_EDGE",EDGE,{"blendedFrom":[makeQuery(id+"F3.opExtrude","CAP_EDGE",EDGE,{"disambiguationData":[OSD([subQ17,subQ16,subQ15,subQ14,subQ13,subQ12,subQ11,subQ10,subQ9,subQ8,subQ7,subQ6,subQ5,subQ4,subQ3,subQ2,subQ1,subQ0]),TDD([makeQuery(id+"F2.opChamfer","BLEND_EDGE",EDGE,{"blendedFrom":[makeQuery(id+"F1.opExtrude","CAP_EDGE",EDGE,{"disambiguationData":[OSD([subQ6])],"isStart":false}),makeQuery(id+"F1.opExtrude","CAP_FACE",FACE,{"disambiguationData":[OSD([subQ17,subQ16,subQ15,subQ14,subQ13,subQ12,subQ11,subQ10,subQ9,subQ8,subQ7,subQ6,subQ5,subQ4,subQ3,subQ2,subQ1,subQ0])],"isStart":false})],"blendedInto":[makeQuery(id+"F1.opExtrude","CAP_FACE",FACE,{"disambiguationData":[OSD([subQ17,subQ16,subQ15,subQ14,subQ13,subQ12,subQ11,subQ10,subQ9,subQ8,subQ7,subQ6,subQ5,subQ4,subQ3,subQ2,subQ1,subQ0])],"isStart":false})]})])],"isStart":false}),makeQuery(id+"F3.opExtrude","CAP_FACE",FACE,{"disambiguationData":[OSD([subQ17,subQ16,subQ15,subQ14,subQ13,subQ12,subQ11,subQ10,subQ9,subQ8,subQ7,subQ6,subQ5,subQ4,subQ3,subQ2,subQ1,subQ0])],"isStart":false})],"blendedInto":[makeQuery(id+"F3.opExtrude","CAP_FACE",FACE,{"disambiguationData":[OSD([subQ17,subQ16,subQ15,subQ14,subQ13,subQ12,subQ11,subQ10,subQ9,subQ8,subQ7,subQ6,subQ5,subQ4,subQ3,subQ2,subQ1,subQ0])],"isStart":false})]})])],"isStart":false}),makeQuery(id+"F5.opExtrude","CAP_FACE",FACE,{"disambiguationData":[OSD([subQ17,subQ16,subQ15,subQ14,subQ13,subQ12,subQ11,subQ10,subQ9,subQ8,subQ7,subQ6,subQ5,subQ4,subQ3,subQ2,subQ1,subQ0])],"isStart":false})],"blendedInto":[makeQuery(id+"F5.opExtrude","CAP_FACE",FACE,{"disambiguationData":[OSD([subQ17,subQ16,subQ15,subQ14,subQ13,subQ12,subQ11,subQ10,subQ9,subQ8,subQ7,subQ6,subQ5,subQ4,subQ3,subQ2,subQ1,subQ0])],"isStart":false})]})])],"isStart":false});}
            var Q11;
            {var subQ0=sQuery(id+"F0.wireOp",EDGE,"E3.4");var subQ1=sQuery(id+"F0.wireOp",EDGE,"E3.3");var subQ2=sQuery(id+"F0.wireOp",EDGE,"E3.2");var subQ3=sQuery(id+"F0.wireOp",EDGE,"E3.1");var subQ4=sQuery(id+"F0.wireOp",EDGE,"E2.5");var subQ5=sQuery(id+"F0.wireOp",EDGE,"E2.4");var subQ6=sQuery(id+"F0.wireOp",EDGE,"E2.3");var subQ7=sQuery(id+"F0.wireOp",EDGE,"E2.2");var subQ8=sQuery(id+"F0.wireOp",EDGE,"E1.4");var subQ9=sQuery(id+"F0.wireOp",EDGE,"E1.3");var subQ10=sQuery(id+"F0.wireOp",EDGE,"E1.2");var subQ11=sQuery(id+"F0.wireOp",EDGE,"E1.1");var subQ12=sQuery(id+"F0.wireOp",EDGE,"E0.5");var subQ13=sQuery(id+"F0.wireOp",EDGE,"E0.4");var subQ14=sQuery(id+"F0.wireOp",EDGE,"E0.3");var subQ15=sQuery(id+"F0.wireOp",EDGE,"E0.2");var subQ16=sQuery(id+"F0.wireOp",EDGE,"E0.1");var subQ17=sQuery(id+"F0.wireOp",EDGE,"E0.0");Q11=makeQuery(id+"F7.opExtrude","CAP_EDGE",EDGE,{"disambiguationData":[OSD([subQ17,subQ16,subQ15,subQ14,subQ13,subQ12,subQ11,subQ10,subQ9,subQ8,subQ7,subQ6,subQ5,subQ4,subQ3,subQ2,subQ1,subQ0]),TDD([makeQuery(id+"F6.opChamfer","BLEND_EDGE",EDGE,{"blendedFrom":[makeQuery(id+"F5.opExtrude","CAP_EDGE",EDGE,{"disambiguationData":[OSD([subQ17,subQ16,subQ15,subQ14,subQ13,subQ12,subQ11,subQ10,subQ9,subQ8,subQ7,subQ6,subQ5,subQ4,subQ3,subQ2,subQ1,subQ0]),TDD([makeQuery(id+"F4.opChamfer","BLEND_EDGE",EDGE,{"blendedFrom":[makeQuery(id+"F3.opExtrude","CAP_EDGE",EDGE,{"disambiguationData":[OSD([subQ17,subQ16,subQ15,subQ14,subQ13,subQ12,subQ11,subQ10,subQ9,subQ8,subQ7,subQ6,subQ5,subQ4,subQ3,subQ2,subQ1,subQ0]),TDD([makeQuery(id+"F2.opChamfer","BLEND_EDGE",EDGE,{"blendedFrom":[makeQuery(id+"F1.opExtrude","CAP_EDGE",EDGE,{"disambiguationData":[OSD([subQ5])],"isStart":false}),makeQuery(id+"F1.opExtrude","CAP_FACE",FACE,{"disambiguationData":[OSD([subQ17,subQ16,subQ15,subQ14,subQ13,subQ12,subQ11,subQ10,subQ9,subQ8,subQ7,subQ6,subQ5,subQ4,subQ3,subQ2,subQ1,subQ0])],"isStart":false})],"blendedInto":[makeQuery(id+"F1.opExtrude","CAP_FACE",FACE,{"disambiguationData":[OSD([subQ17,subQ16,subQ15,subQ14,subQ13,subQ12,subQ11,subQ10,subQ9,subQ8,subQ7,subQ6,subQ5,subQ4,subQ3,subQ2,subQ1,subQ0])],"isStart":false})]})])],"isStart":false}),makeQuery(id+"F3.opExtrude","CAP_FACE",FACE,{"disambiguationData":[OSD([subQ17,subQ16,subQ15,subQ14,subQ13,subQ12,subQ11,subQ10,subQ9,subQ8,subQ7,subQ6,subQ5,subQ4,subQ3,subQ2,subQ1,subQ0])],"isStart":false})],"blendedInto":[makeQuery(id+"F3.opExtrude","CAP_FACE",FACE,{"disambiguationData":[OSD([subQ17,subQ16,subQ15,subQ14,subQ13,subQ12,subQ11,subQ10,subQ9,subQ8,subQ7,subQ6,subQ5,subQ4,subQ3,subQ2,subQ1,subQ0])],"isStart":false})]})])],"isStart":false}),makeQuery(id+"F5.opExtrude","CAP_FACE",FACE,{"disambiguationData":[OSD([subQ17,subQ16,subQ15,subQ14,subQ13,subQ12,subQ11,subQ10,subQ9,subQ8,subQ7,subQ6,subQ5,subQ4,subQ3,subQ2,subQ1,subQ0])],"isStart":false})],"blendedInto":[makeQuery(id+"F5.opExtrude","CAP_FACE",FACE,{"disambiguationData":[OSD([subQ17,subQ16,subQ15,subQ14,subQ13,subQ12,subQ11,subQ10,subQ9,subQ8,subQ7,subQ6,subQ5,subQ4,subQ3,subQ2,subQ1,subQ0])],"isStart":false})]})])],"isStart":false});}
            chamfer(context, id + "F8", {"entities" : qUnion([Q0, Q1, Q2, Q3, Q4, Q5, Q6, Q7, Q8, Q9, Q10, Q11]), "width" : 5.08 * mm, "tangentPropagation" : true});
        }
        {
            var Q0;
            Q0=makeQuery(id+"F7.opExtrude","CAP_FACE",FACE,{"disambiguationData":[OSD([sQuery(id+"F0.wireOp",EDGE,"E0.0"),sQuery(id+"F0.wireOp",EDGE,"E0.1"),sQuery(id+"F0.wireOp",EDGE,"E0.2"),sQuery(id+"F0.wireOp",EDGE,"E0.3"),sQuery(id+"F0.wireOp",EDGE,"E0.4"),sQuery(id+"F0.wireOp",EDGE,"E0.5"),sQuery(id+"F0.wireOp",EDGE,"E1.1"),sQuery(id+"F0.wireOp",EDGE,"E1.2"),sQuery(id+"F0.wireOp",EDGE,"E1.3"),sQuery(id+"F0.wireOp",EDGE,"E1.4"),sQuery(id+"F0.wireOp",EDGE,"E2.2"),sQuery(id+"F0.wireOp",EDGE,"E2.3"),sQuery(id+"F0.wireOp",EDGE,"E2.4"),sQuery(id+"F0.wireOp",EDGE,"E2.5"),sQuery(id+"F0.wireOp",EDGE,"E3.1"),sQuery(id+"F0.wireOp",EDGE,"E3.2"),sQuery(id+"F0.wireOp",EDGE,"E3.3"),sQuery(id+"F0.wireOp",EDGE,"E3.4")])],"isStart":false});
            extrude(context, id + "F9", {"entities" : qUnion([Q0]), "operationType" : NewBodyOperationType.ADD, "depth" : 25.4 * mm});
        }
        {
            var Q0;
            {var subQ0=sQuery(id+"F0.wireOp",EDGE,"E3.4");var subQ1=sQuery(id+"F0.wireOp",EDGE,"E3.3");var subQ2=sQuery(id+"F0.wireOp",EDGE,"E3.2");var subQ3=sQuery(id+"F0.wireOp",EDGE,"E3.1");var subQ4=sQuery(id+"F0.wireOp",EDGE,"E2.5");var subQ5=sQuery(id+"F0.wireOp",EDGE,"E2.4");var subQ6=sQuery(id+"F0.wireOp",EDGE,"E2.3");var subQ7=sQuery(id+"F0.wireOp",EDGE,"E2.2");var subQ8=sQuery(id+"F0.wireOp",EDGE,"E1.4");var subQ9=sQuery(id+"F0.wireOp",EDGE,"E1.3");var subQ10=sQuery(id+"F0.wireOp",EDGE,"E1.2");var subQ11=sQuery(id+"F0.wireOp",EDGE,"E1.1");var subQ12=sQuery(id+"F0.wireOp",EDGE,"E0.5");var subQ13=sQuery(id+"F0.wireOp",EDGE,"E0.4");var subQ14=sQuery(id+"F0.wireOp",EDGE,"E0.3");var subQ15=sQuery(id+"F0.wireOp",EDGE,"E0.2");var subQ16=sQuery(id+"F0.wireOp",EDGE,"E0.1");var subQ17=sQuery(id+"F0.wireOp",EDGE,"E0.0");Q0=makeQuery(id+"F9.opExtrude","CAP_EDGE",EDGE,{"disambiguationData":[OSD([subQ17,subQ16,subQ15,subQ14,subQ13,subQ12,subQ11,subQ10,subQ9,subQ8,subQ7,subQ6,subQ5,subQ4,subQ3,subQ2,subQ1,subQ0]),TDD([makeQuery(id+"F8.opChamfer","BLEND_EDGE",EDGE,{"blendedFrom":[makeQuery(id+"F7.opExtrude","CAP_EDGE",EDGE,{"disambiguationData":[OSD([subQ17,subQ16,subQ15,subQ14,subQ13,subQ12,subQ11,subQ10,subQ9,subQ8,subQ7,subQ6,subQ5,subQ4,subQ3,subQ2,subQ1,subQ0]),TDD([makeQuery(id+"F6.opChamfer","BLEND_EDGE",EDGE,{"blendedFrom":[makeQuery(id+"F5.opExtrude","CAP_EDGE",EDGE,{"disambiguationData":[OSD([subQ17,subQ16,subQ15,subQ14,subQ13,subQ12,subQ11,subQ10,subQ9,subQ8,subQ7,subQ6,subQ5,subQ4,subQ3,subQ2,subQ1,subQ0]),TDD([makeQuery(id+"F4.opChamfer","BLEND_EDGE",EDGE,{"blendedFrom":[makeQuery(id+"F3.opExtrude","CAP_EDGE",EDGE,{"disambiguationData":[OSD([subQ17,subQ16,subQ15,subQ14,subQ13,subQ12,subQ11,subQ10,subQ9,subQ8,subQ7,subQ6,subQ5,subQ4,subQ3,subQ2,subQ1,subQ0]),TDD([makeQuery(id+"F2.opChamfer","BLEND_EDGE",EDGE,{"blendedFrom":[makeQuery(id+"F1.opExtrude","CAP_EDGE",EDGE,{"disambiguationData":[OSD([subQ8])],"isStart":false}),makeQuery(id+"F1.opExtrude","CAP_FACE",FACE,{"disambiguationData":[OSD([subQ17,subQ16,subQ15,subQ14,subQ13,subQ12,subQ11,subQ10,subQ9,subQ8,subQ7,subQ6,subQ5,subQ4,subQ3,subQ2,subQ1,subQ0])],"isStart":false})],"blendedInto":[makeQuery(id+"F1.opExtrude","CAP_FACE",FACE,{"disambiguationData":[OSD([subQ17,subQ16,subQ15,subQ14,subQ13,subQ12,subQ11,subQ10,subQ9,subQ8,subQ7,subQ6,subQ5,subQ4,subQ3,subQ2,subQ1,subQ0])],"isStart":false})]})])],"isStart":false}),makeQuery(id+"F3.opExtrude","CAP_FACE",FACE,{"disambiguationData":[OSD([subQ17,subQ16,subQ15,subQ14,subQ13,subQ12,subQ11,subQ10,subQ9,subQ8,subQ7,subQ6,subQ5,subQ4,subQ3,subQ2,subQ1,subQ0])],"isStart":false})],"blendedInto":[makeQuery(id+"F3.opExtrude","CAP_FACE",FACE,{"disambiguationData":[OSD([subQ17,subQ16,subQ15,subQ14,subQ13,subQ12,subQ11,subQ10,subQ9,subQ8,subQ7,subQ6,subQ5,subQ4,subQ3,subQ2,subQ1,subQ0])],"isStart":false})]})])],"isStart":false}),makeQuery(id+"F5.opExtrude","CAP_FACE",FACE,{"disambiguationData":[OSD([subQ17,subQ16,subQ15,subQ14,subQ13,subQ12,subQ11,subQ10,subQ9,subQ8,subQ7,subQ6,subQ5,subQ4,subQ3,subQ2,subQ1,subQ0])],"isStart":false})],"blendedInto":[makeQuery(id+"F5.opExtrude","CAP_FACE",FACE,{"disambiguationData":[OSD([subQ17,subQ16,subQ15,subQ14,subQ13,subQ12,subQ11,subQ10,subQ9,subQ8,subQ7,subQ6,subQ5,subQ4,subQ3,subQ2,subQ1,subQ0])],"isStart":false})]})])],"isStart":false}),makeQuery(id+"F7.opExtrude","CAP_FACE",FACE,{"disambiguationData":[OSD([subQ17,subQ16,subQ15,subQ14,subQ13,subQ12,subQ11,subQ10,subQ9,subQ8,subQ7,subQ6,subQ5,subQ4,subQ3,subQ2,subQ1,subQ0])],"isStart":false})],"blendedInto":[makeQuery(id+"F7.opExtrude","CAP_FACE",FACE,{"disambiguationData":[OSD([subQ17,subQ16,subQ15,subQ14,subQ13,subQ12,subQ11,subQ10,subQ9,subQ8,subQ7,subQ6,subQ5,subQ4,subQ3,subQ2,subQ1,subQ0])],"isStart":false})]})])],"isStart":false});}
            var Q1;
            {var subQ0=sQuery(id+"F0.wireOp",EDGE,"E3.4");var subQ1=sQuery(id+"F0.wireOp",EDGE,"E3.3");var subQ2=sQuery(id+"F0.wireOp",EDGE,"E3.2");var subQ3=sQuery(id+"F0.wireOp",EDGE,"E3.1");var subQ4=sQuery(id+"F0.wireOp",EDGE,"E2.5");var subQ5=sQuery(id+"F0.wireOp",EDGE,"E2.4");var subQ6=sQuery(id+"F0.wireOp",EDGE,"E2.3");var subQ7=sQuery(id+"F0.wireOp",EDGE,"E2.2");var subQ8=sQuery(id+"F0.wireOp",EDGE,"E1.4");var subQ9=sQuery(id+"F0.wireOp",EDGE,"E1.3");var subQ10=sQuery(id+"F0.wireOp",EDGE,"E1.2");var subQ11=sQuery(id+"F0.wireOp",EDGE,"E1.1");var subQ12=sQuery(id+"F0.wireOp",EDGE,"E0.5");var subQ13=sQuery(id+"F0.wireOp",EDGE,"E0.4");var subQ14=sQuery(id+"F0.wireOp",EDGE,"E0.3");var subQ15=sQuery(id+"F0.wireOp",EDGE,"E0.2");var subQ16=sQuery(id+"F0.wireOp",EDGE,"E0.1");var subQ17=sQuery(id+"F0.wireOp",EDGE,"E0.0");Q1=makeQuery(id+"F9.opExtrude","CAP_EDGE",EDGE,{"disambiguationData":[OSD([subQ17,subQ16,subQ15,subQ14,subQ13,subQ12,subQ11,subQ10,subQ9,subQ8,subQ7,subQ6,subQ5,subQ4,subQ3,subQ2,subQ1,subQ0]),TDD([makeQuery(id+"F8.opChamfer","BLEND_EDGE",EDGE,{"blendedFrom":[makeQuery(id+"F7.opExtrude","CAP_EDGE",EDGE,{"disambiguationData":[OSD([subQ17,subQ16,subQ15,subQ14,subQ13,subQ12,subQ11,subQ10,subQ9,subQ8,subQ7,subQ6,subQ5,subQ4,subQ3,subQ2,subQ1,subQ0]),TDD([makeQuery(id+"F6.opChamfer","BLEND_EDGE",EDGE,{"blendedFrom":[makeQuery(id+"F5.opExtrude","CAP_EDGE",EDGE,{"disambiguationData":[OSD([subQ17,subQ16,subQ15,subQ14,subQ13,subQ12,subQ11,subQ10,subQ9,subQ8,subQ7,subQ6,subQ5,subQ4,subQ3,subQ2,subQ1,subQ0]),TDD([makeQuery(id+"F4.opChamfer","BLEND_EDGE",EDGE,{"blendedFrom":[makeQuery(id+"F3.opExtrude","CAP_EDGE",EDGE,{"disambiguationData":[OSD([subQ17,subQ16,subQ15,subQ14,subQ13,subQ12,subQ11,subQ10,subQ9,subQ8,subQ7,subQ6,subQ5,subQ4,subQ3,subQ2,subQ1,subQ0]),TDD([makeQuery(id+"F2.opChamfer","BLEND_EDGE",EDGE,{"blendedFrom":[makeQuery(id+"F1.opExtrude","CAP_EDGE",EDGE,{"disambiguationData":[OSD([subQ9])],"isStart":false}),makeQuery(id+"F1.opExtrude","CAP_FACE",FACE,{"disambiguationData":[OSD([subQ17,subQ16,subQ15,subQ14,subQ13,subQ12,subQ11,subQ10,subQ9,subQ8,subQ7,subQ6,subQ5,subQ4,subQ3,subQ2,subQ1,subQ0])],"isStart":false})],"blendedInto":[makeQuery(id+"F1.opExtrude","CAP_FACE",FACE,{"disambiguationData":[OSD([subQ17,subQ16,subQ15,subQ14,subQ13,subQ12,subQ11,subQ10,subQ9,subQ8,subQ7,subQ6,subQ5,subQ4,subQ3,subQ2,subQ1,subQ0])],"isStart":false})]})])],"isStart":false}),makeQuery(id+"F3.opExtrude","CAP_FACE",FACE,{"disambiguationData":[OSD([subQ17,subQ16,subQ15,subQ14,subQ13,subQ12,subQ11,subQ10,subQ9,subQ8,subQ7,subQ6,subQ5,subQ4,subQ3,subQ2,subQ1,subQ0])],"isStart":false})],"blendedInto":[makeQuery(id+"F3.opExtrude","CAP_FACE",FACE,{"disambiguationData":[OSD([subQ17,subQ16,subQ15,subQ14,subQ13,subQ12,subQ11,subQ10,subQ9,subQ8,subQ7,subQ6,subQ5,subQ4,subQ3,subQ2,subQ1,subQ0])],"isStart":false})]})])],"isStart":false}),makeQuery(id+"F5.opExtrude","CAP_FACE",FACE,{"disambiguationData":[OSD([subQ17,subQ16,subQ15,subQ14,subQ13,subQ12,subQ11,subQ10,subQ9,subQ8,subQ7,subQ6,subQ5,subQ4,subQ3,subQ2,subQ1,subQ0])],"isStart":false})],"blendedInto":[makeQuery(id+"F5.opExtrude","CAP_FACE",FACE,{"disambiguationData":[OSD([subQ17,subQ16,subQ15,subQ14,subQ13,subQ12,subQ11,subQ10,subQ9,subQ8,subQ7,subQ6,subQ5,subQ4,subQ3,subQ2,subQ1,subQ0])],"isStart":false})]})])],"isStart":false}),makeQuery(id+"F7.opExtrude","CAP_FACE",FACE,{"disambiguationData":[OSD([subQ17,subQ16,subQ15,subQ14,subQ13,subQ12,subQ11,subQ10,subQ9,subQ8,subQ7,subQ6,subQ5,subQ4,subQ3,subQ2,subQ1,subQ0])],"isStart":false})],"blendedInto":[makeQuery(id+"F7.opExtrude","CAP_FACE",FACE,{"disambiguationData":[OSD([subQ17,subQ16,subQ15,subQ14,subQ13,subQ12,subQ11,subQ10,subQ9,subQ8,subQ7,subQ6,subQ5,subQ4,subQ3,subQ2,subQ1,subQ0])],"isStart":false})]})])],"isStart":false});}
            var Q2;
            {var subQ0=sQuery(id+"F0.wireOp",EDGE,"E3.4");var subQ1=sQuery(id+"F0.wireOp",EDGE,"E3.3");var subQ2=sQuery(id+"F0.wireOp",EDGE,"E3.2");var subQ3=sQuery(id+"F0.wireOp",EDGE,"E3.1");var subQ4=sQuery(id+"F0.wireOp",EDGE,"E2.5");var subQ5=sQuery(id+"F0.wireOp",EDGE,"E2.4");var subQ6=sQuery(id+"F0.wireOp",EDGE,"E2.3");var subQ7=sQuery(id+"F0.wireOp",EDGE,"E2.2");var subQ8=sQuery(id+"F0.wireOp",EDGE,"E1.4");var subQ9=sQuery(id+"F0.wireOp",EDGE,"E1.3");var subQ10=sQuery(id+"F0.wireOp",EDGE,"E1.2");var subQ11=sQuery(id+"F0.wireOp",EDGE,"E1.1");var subQ12=sQuery(id+"F0.wireOp",EDGE,"E0.5");var subQ13=sQuery(id+"F0.wireOp",EDGE,"E0.4");var subQ14=sQuery(id+"F0.wireOp",EDGE,"E0.3");var subQ15=sQuery(id+"F0.wireOp",EDGE,"E0.2");var subQ16=sQuery(id+"F0.wireOp",EDGE,"E0.1");var subQ17=sQuery(id+"F0.wireOp",EDGE,"E0.0");Q2=makeQuery(id+"F9.opExtrude","CAP_EDGE",EDGE,{"disambiguationData":[OSD([subQ17,subQ16,subQ15,subQ14,subQ13,subQ12,subQ11,subQ10,subQ9,subQ8,subQ7,subQ6,subQ5,subQ4,subQ3,subQ2,subQ1,subQ0]),TDD([makeQuery(id+"F8.opChamfer","BLEND_EDGE",EDGE,{"blendedFrom":[makeQuery(id+"F7.opExtrude","CAP_EDGE",EDGE,{"disambiguationData":[OSD([subQ17,subQ16,subQ15,subQ14,subQ13,subQ12,subQ11,subQ10,subQ9,subQ8,subQ7,subQ6,subQ5,subQ4,subQ3,subQ2,subQ1,subQ0]),TDD([makeQuery(id+"F6.opChamfer","BLEND_EDGE",EDGE,{"blendedFrom":[makeQuery(id+"F5.opExtrude","CAP_EDGE",EDGE,{"disambiguationData":[OSD([subQ17,subQ16,subQ15,subQ14,subQ13,subQ12,subQ11,subQ10,subQ9,subQ8,subQ7,subQ6,subQ5,subQ4,subQ3,subQ2,subQ1,subQ0]),TDD([makeQuery(id+"F4.opChamfer","BLEND_EDGE",EDGE,{"blendedFrom":[makeQuery(id+"F3.opExtrude","CAP_EDGE",EDGE,{"disambiguationData":[OSD([subQ17,subQ16,subQ15,subQ14,subQ13,subQ12,subQ11,subQ10,subQ9,subQ8,subQ7,subQ6,subQ5,subQ4,subQ3,subQ2,subQ1,subQ0]),TDD([makeQuery(id+"F2.opChamfer","BLEND_EDGE",EDGE,{"blendedFrom":[makeQuery(id+"F1.opExtrude","CAP_EDGE",EDGE,{"disambiguationData":[OSD([subQ10])],"isStart":false}),makeQuery(id+"F1.opExtrude","CAP_FACE",FACE,{"disambiguationData":[OSD([subQ17,subQ16,subQ15,subQ14,subQ13,subQ12,subQ11,subQ10,subQ9,subQ8,subQ7,subQ6,subQ5,subQ4,subQ3,subQ2,subQ1,subQ0])],"isStart":false})],"blendedInto":[makeQuery(id+"F1.opExtrude","CAP_FACE",FACE,{"disambiguationData":[OSD([subQ17,subQ16,subQ15,subQ14,subQ13,subQ12,subQ11,subQ10,subQ9,subQ8,subQ7,subQ6,subQ5,subQ4,subQ3,subQ2,subQ1,subQ0])],"isStart":false})]})])],"isStart":false}),makeQuery(id+"F3.opExtrude","CAP_FACE",FACE,{"disambiguationData":[OSD([subQ17,subQ16,subQ15,subQ14,subQ13,subQ12,subQ11,subQ10,subQ9,subQ8,subQ7,subQ6,subQ5,subQ4,subQ3,subQ2,subQ1,subQ0])],"isStart":false})],"blendedInto":[makeQuery(id+"F3.opExtrude","CAP_FACE",FACE,{"disambiguationData":[OSD([subQ17,subQ16,subQ15,subQ14,subQ13,subQ12,subQ11,subQ10,subQ9,subQ8,subQ7,subQ6,subQ5,subQ4,subQ3,subQ2,subQ1,subQ0])],"isStart":false})]})])],"isStart":false}),makeQuery(id+"F5.opExtrude","CAP_FACE",FACE,{"disambiguationData":[OSD([subQ17,subQ16,subQ15,subQ14,subQ13,subQ12,subQ11,subQ10,subQ9,subQ8,subQ7,subQ6,subQ5,subQ4,subQ3,subQ2,subQ1,subQ0])],"isStart":false})],"blendedInto":[makeQuery(id+"F5.opExtrude","CAP_FACE",FACE,{"disambiguationData":[OSD([subQ17,subQ16,subQ15,subQ14,subQ13,subQ12,subQ11,subQ10,subQ9,subQ8,subQ7,subQ6,subQ5,subQ4,subQ3,subQ2,subQ1,subQ0])],"isStart":false})]})])],"isStart":false}),makeQuery(id+"F7.opExtrude","CAP_FACE",FACE,{"disambiguationData":[OSD([subQ17,subQ16,subQ15,subQ14,subQ13,subQ12,subQ11,subQ10,subQ9,subQ8,subQ7,subQ6,subQ5,subQ4,subQ3,subQ2,subQ1,subQ0])],"isStart":false})],"blendedInto":[makeQuery(id+"F7.opExtrude","CAP_FACE",FACE,{"disambiguationData":[OSD([subQ17,subQ16,subQ15,subQ14,subQ13,subQ12,subQ11,subQ10,subQ9,subQ8,subQ7,subQ6,subQ5,subQ4,subQ3,subQ2,subQ1,subQ0])],"isStart":false})]})])],"isStart":false});}
            var Q3;
            {var subQ0=sQuery(id+"F0.wireOp",EDGE,"E3.4");var subQ1=sQuery(id+"F0.wireOp",EDGE,"E3.3");var subQ2=sQuery(id+"F0.wireOp",EDGE,"E3.2");var subQ3=sQuery(id+"F0.wireOp",EDGE,"E3.1");var subQ4=sQuery(id+"F0.wireOp",EDGE,"E2.5");var subQ5=sQuery(id+"F0.wireOp",EDGE,"E2.4");var subQ6=sQuery(id+"F0.wireOp",EDGE,"E2.3");var subQ7=sQuery(id+"F0.wireOp",EDGE,"E2.2");var subQ8=sQuery(id+"F0.wireOp",EDGE,"E1.4");var subQ9=sQuery(id+"F0.wireOp",EDGE,"E1.3");var subQ10=sQuery(id+"F0.wireOp",EDGE,"E1.2");var subQ11=sQuery(id+"F0.wireOp",EDGE,"E1.1");var subQ12=sQuery(id+"F0.wireOp",EDGE,"E0.5");var subQ13=sQuery(id+"F0.wireOp",EDGE,"E0.4");var subQ14=sQuery(id+"F0.wireOp",EDGE,"E0.3");var subQ15=sQuery(id+"F0.wireOp",EDGE,"E0.2");var subQ16=sQuery(id+"F0.wireOp",EDGE,"E0.1");var subQ17=sQuery(id+"F0.wireOp",EDGE,"E0.0");Q3=makeQuery(id+"F9.opExtrude","CAP_EDGE",EDGE,{"disambiguationData":[OSD([subQ17,subQ16,subQ15,subQ14,subQ13,subQ12,subQ11,subQ10,subQ9,subQ8,subQ7,subQ6,subQ5,subQ4,subQ3,subQ2,subQ1,subQ0]),TDD([makeQuery(id+"F8.opChamfer","BLEND_EDGE",EDGE,{"blendedFrom":[makeQuery(id+"F7.opExtrude","CAP_EDGE",EDGE,{"disambiguationData":[OSD([subQ17,subQ16,subQ15,subQ14,subQ13,subQ12,subQ11,subQ10,subQ9,subQ8,subQ7,subQ6,subQ5,subQ4,subQ3,subQ2,subQ1,subQ0]),TDD([makeQuery(id+"F6.opChamfer","BLEND_EDGE",EDGE,{"blendedFrom":[makeQuery(id+"F5.opExtrude","CAP_EDGE",EDGE,{"disambiguationData":[OSD([subQ17,subQ16,subQ15,subQ14,subQ13,subQ12,subQ11,subQ10,subQ9,subQ8,subQ7,subQ6,subQ5,subQ4,subQ3,subQ2,subQ1,subQ0]),TDD([makeQuery(id+"F4.opChamfer","BLEND_EDGE",EDGE,{"blendedFrom":[makeQuery(id+"F3.opExtrude","CAP_EDGE",EDGE,{"disambiguationData":[OSD([subQ17,subQ16,subQ15,subQ14,subQ13,subQ12,subQ11,subQ10,subQ9,subQ8,subQ7,subQ6,subQ5,subQ4,subQ3,subQ2,subQ1,subQ0]),TDD([makeQuery(id+"F2.opChamfer","BLEND_EDGE",EDGE,{"blendedFrom":[makeQuery(id+"F1.opExtrude","CAP_EDGE",EDGE,{"disambiguationData":[OSD([subQ11])],"isStart":false}),makeQuery(id+"F1.opExtrude","CAP_FACE",FACE,{"disambiguationData":[OSD([subQ17,subQ16,subQ15,subQ14,subQ13,subQ12,subQ11,subQ10,subQ9,subQ8,subQ7,subQ6,subQ5,subQ4,subQ3,subQ2,subQ1,subQ0])],"isStart":false})],"blendedInto":[makeQuery(id+"F1.opExtrude","CAP_FACE",FACE,{"disambiguationData":[OSD([subQ17,subQ16,subQ15,subQ14,subQ13,subQ12,subQ11,subQ10,subQ9,subQ8,subQ7,subQ6,subQ5,subQ4,subQ3,subQ2,subQ1,subQ0])],"isStart":false})]})])],"isStart":false}),makeQuery(id+"F3.opExtrude","CAP_FACE",FACE,{"disambiguationData":[OSD([subQ17,subQ16,subQ15,subQ14,subQ13,subQ12,subQ11,subQ10,subQ9,subQ8,subQ7,subQ6,subQ5,subQ4,subQ3,subQ2,subQ1,subQ0])],"isStart":false})],"blendedInto":[makeQuery(id+"F3.opExtrude","CAP_FACE",FACE,{"disambiguationData":[OSD([subQ17,subQ16,subQ15,subQ14,subQ13,subQ12,subQ11,subQ10,subQ9,subQ8,subQ7,subQ6,subQ5,subQ4,subQ3,subQ2,subQ1,subQ0])],"isStart":false})]})])],"isStart":false}),makeQuery(id+"F5.opExtrude","CAP_FACE",FACE,{"disambiguationData":[OSD([subQ17,subQ16,subQ15,subQ14,subQ13,subQ12,subQ11,subQ10,subQ9,subQ8,subQ7,subQ6,subQ5,subQ4,subQ3,subQ2,subQ1,subQ0])],"isStart":false})],"blendedInto":[makeQuery(id+"F5.opExtrude","CAP_FACE",FACE,{"disambiguationData":[OSD([subQ17,subQ16,subQ15,subQ14,subQ13,subQ12,subQ11,subQ10,subQ9,subQ8,subQ7,subQ6,subQ5,subQ4,subQ3,subQ2,subQ1,subQ0])],"isStart":false})]})])],"isStart":false}),makeQuery(id+"F7.opExtrude","CAP_FACE",FACE,{"disambiguationData":[OSD([subQ17,subQ16,subQ15,subQ14,subQ13,subQ12,subQ11,subQ10,subQ9,subQ8,subQ7,subQ6,subQ5,subQ4,subQ3,subQ2,subQ1,subQ0])],"isStart":false})],"blendedInto":[makeQuery(id+"F7.opExtrude","CAP_FACE",FACE,{"disambiguationData":[OSD([subQ17,subQ16,subQ15,subQ14,subQ13,subQ12,subQ11,subQ10,subQ9,subQ8,subQ7,subQ6,subQ5,subQ4,subQ3,subQ2,subQ1,subQ0])],"isStart":false})]})])],"isStart":false});}
            var Q4;
            {var subQ0=sQuery(id+"F0.wireOp",EDGE,"E3.4");var subQ1=sQuery(id+"F0.wireOp",EDGE,"E3.3");var subQ2=sQuery(id+"F0.wireOp",EDGE,"E3.2");var subQ3=sQuery(id+"F0.wireOp",EDGE,"E3.1");var subQ4=sQuery(id+"F0.wireOp",EDGE,"E2.5");var subQ5=sQuery(id+"F0.wireOp",EDGE,"E2.4");var subQ6=sQuery(id+"F0.wireOp",EDGE,"E2.3");var subQ7=sQuery(id+"F0.wireOp",EDGE,"E2.2");var subQ8=sQuery(id+"F0.wireOp",EDGE,"E1.4");var subQ9=sQuery(id+"F0.wireOp",EDGE,"E1.3");var subQ10=sQuery(id+"F0.wireOp",EDGE,"E1.2");var subQ11=sQuery(id+"F0.wireOp",EDGE,"E1.1");var subQ12=sQuery(id+"F0.wireOp",EDGE,"E0.5");var subQ13=sQuery(id+"F0.wireOp",EDGE,"E0.4");var subQ14=sQuery(id+"F0.wireOp",EDGE,"E0.3");var subQ15=sQuery(id+"F0.wireOp",EDGE,"E0.2");var subQ16=sQuery(id+"F0.wireOp",EDGE,"E0.1");var subQ17=sQuery(id+"F0.wireOp",EDGE,"E0.0");Q4=makeQuery(id+"F9.opExtrude","CAP_EDGE",EDGE,{"disambiguationData":[OSD([subQ17,subQ16,subQ15,subQ14,subQ13,subQ12,subQ11,subQ10,subQ9,subQ8,subQ7,subQ6,subQ5,subQ4,subQ3,subQ2,subQ1,subQ0]),TDD([makeQuery(id+"F8.opChamfer","BLEND_EDGE",EDGE,{"blendedFrom":[makeQuery(id+"F7.opExtrude","CAP_EDGE",EDGE,{"disambiguationData":[OSD([subQ17,subQ16,subQ15,subQ14,subQ13,subQ12,subQ11,subQ10,subQ9,subQ8,subQ7,subQ6,subQ5,subQ4,subQ3,subQ2,subQ1,subQ0]),TDD([makeQuery(id+"F6.opChamfer","BLEND_EDGE",EDGE,{"blendedFrom":[makeQuery(id+"F5.opExtrude","CAP_EDGE",EDGE,{"disambiguationData":[OSD([subQ17,subQ16,subQ15,subQ14,subQ13,subQ12,subQ11,subQ10,subQ9,subQ8,subQ7,subQ6,subQ5,subQ4,subQ3,subQ2,subQ1,subQ0]),TDD([makeQuery(id+"F4.opChamfer","BLEND_EDGE",EDGE,{"blendedFrom":[makeQuery(id+"F3.opExtrude","CAP_EDGE",EDGE,{"disambiguationData":[OSD([subQ17,subQ16,subQ15,subQ14,subQ13,subQ12,subQ11,subQ10,subQ9,subQ8,subQ7,subQ6,subQ5,subQ4,subQ3,subQ2,subQ1,subQ0]),TDD([makeQuery(id+"F2.opChamfer","BLEND_EDGE",EDGE,{"blendedFrom":[makeQuery(id+"F1.opExtrude","CAP_EDGE",EDGE,{"disambiguationData":[OSD([subQ0])],"isStart":false}),makeQuery(id+"F1.opExtrude","CAP_FACE",FACE,{"disambiguationData":[OSD([subQ17,subQ16,subQ15,subQ14,subQ13,subQ12,subQ11,subQ10,subQ9,subQ8,subQ7,subQ6,subQ5,subQ4,subQ3,subQ2,subQ1,subQ0])],"isStart":false})],"blendedInto":[makeQuery(id+"F1.opExtrude","CAP_FACE",FACE,{"disambiguationData":[OSD([subQ17,subQ16,subQ15,subQ14,subQ13,subQ12,subQ11,subQ10,subQ9,subQ8,subQ7,subQ6,subQ5,subQ4,subQ3,subQ2,subQ1,subQ0])],"isStart":false})]})])],"isStart":false}),makeQuery(id+"F3.opExtrude","CAP_FACE",FACE,{"disambiguationData":[OSD([subQ17,subQ16,subQ15,subQ14,subQ13,subQ12,subQ11,subQ10,subQ9,subQ8,subQ7,subQ6,subQ5,subQ4,subQ3,subQ2,subQ1,subQ0])],"isStart":false})],"blendedInto":[makeQuery(id+"F3.opExtrude","CAP_FACE",FACE,{"disambiguationData":[OSD([subQ17,subQ16,subQ15,subQ14,subQ13,subQ12,subQ11,subQ10,subQ9,subQ8,subQ7,subQ6,subQ5,subQ4,subQ3,subQ2,subQ1,subQ0])],"isStart":false})]})])],"isStart":false}),makeQuery(id+"F5.opExtrude","CAP_FACE",FACE,{"disambiguationData":[OSD([subQ17,subQ16,subQ15,subQ14,subQ13,subQ12,subQ11,subQ10,subQ9,subQ8,subQ7,subQ6,subQ5,subQ4,subQ3,subQ2,subQ1,subQ0])],"isStart":false})],"blendedInto":[makeQuery(id+"F5.opExtrude","CAP_FACE",FACE,{"disambiguationData":[OSD([subQ17,subQ16,subQ15,subQ14,subQ13,subQ12,subQ11,subQ10,subQ9,subQ8,subQ7,subQ6,subQ5,subQ4,subQ3,subQ2,subQ1,subQ0])],"isStart":false})]})])],"isStart":false}),makeQuery(id+"F7.opExtrude","CAP_FACE",FACE,{"disambiguationData":[OSD([subQ17,subQ16,subQ15,subQ14,subQ13,subQ12,subQ11,subQ10,subQ9,subQ8,subQ7,subQ6,subQ5,subQ4,subQ3,subQ2,subQ1,subQ0])],"isStart":false})],"blendedInto":[makeQuery(id+"F7.opExtrude","CAP_FACE",FACE,{"disambiguationData":[OSD([subQ17,subQ16,subQ15,subQ14,subQ13,subQ12,subQ11,subQ10,subQ9,subQ8,subQ7,subQ6,subQ5,subQ4,subQ3,subQ2,subQ1,subQ0])],"isStart":false})]})])],"isStart":false});}
            var Q5;
            {var subQ0=sQuery(id+"F0.wireOp",EDGE,"E3.4");var subQ1=sQuery(id+"F0.wireOp",EDGE,"E3.3");var subQ2=sQuery(id+"F0.wireOp",EDGE,"E3.2");var subQ3=sQuery(id+"F0.wireOp",EDGE,"E3.1");var subQ4=sQuery(id+"F0.wireOp",EDGE,"E2.5");var subQ5=sQuery(id+"F0.wireOp",EDGE,"E2.4");var subQ6=sQuery(id+"F0.wireOp",EDGE,"E2.3");var subQ7=sQuery(id+"F0.wireOp",EDGE,"E2.2");var subQ8=sQuery(id+"F0.wireOp",EDGE,"E1.4");var subQ9=sQuery(id+"F0.wireOp",EDGE,"E1.3");var subQ10=sQuery(id+"F0.wireOp",EDGE,"E1.2");var subQ11=sQuery(id+"F0.wireOp",EDGE,"E1.1");var subQ12=sQuery(id+"F0.wireOp",EDGE,"E0.5");var subQ13=sQuery(id+"F0.wireOp",EDGE,"E0.4");var subQ14=sQuery(id+"F0.wireOp",EDGE,"E0.3");var subQ15=sQuery(id+"F0.wireOp",EDGE,"E0.2");var subQ16=sQuery(id+"F0.wireOp",EDGE,"E0.1");var subQ17=sQuery(id+"F0.wireOp",EDGE,"E0.0");Q5=makeQuery(id+"F9.opExtrude","CAP_EDGE",EDGE,{"disambiguationData":[OSD([subQ17,subQ16,subQ15,subQ14,subQ13,subQ12,subQ11,subQ10,subQ9,subQ8,subQ7,subQ6,subQ5,subQ4,subQ3,subQ2,subQ1,subQ0]),TDD([makeQuery(id+"F8.opChamfer","BLEND_EDGE",EDGE,{"blendedFrom":[makeQuery(id+"F7.opExtrude","CAP_EDGE",EDGE,{"disambiguationData":[OSD([subQ17,subQ16,subQ15,subQ14,subQ13,subQ12,subQ11,subQ10,subQ9,subQ8,subQ7,subQ6,subQ5,subQ4,subQ3,subQ2,subQ1,subQ0]),TDD([makeQuery(id+"F6.opChamfer","BLEND_EDGE",EDGE,{"blendedFrom":[makeQuery(id+"F5.opExtrude","CAP_EDGE",EDGE,{"disambiguationData":[OSD([subQ17,subQ16,subQ15,subQ14,subQ13,subQ12,subQ11,subQ10,subQ9,subQ8,subQ7,subQ6,subQ5,subQ4,subQ3,subQ2,subQ1,subQ0]),TDD([makeQuery(id+"F4.opChamfer","BLEND_EDGE",EDGE,{"blendedFrom":[makeQuery(id+"F3.opExtrude","CAP_EDGE",EDGE,{"disambiguationData":[OSD([subQ17,subQ16,subQ15,subQ14,subQ13,subQ12,subQ11,subQ10,subQ9,subQ8,subQ7,subQ6,subQ5,subQ4,subQ3,subQ2,subQ1,subQ0]),TDD([makeQuery(id+"F2.opChamfer","BLEND_EDGE",EDGE,{"blendedFrom":[makeQuery(id+"F1.opExtrude","CAP_EDGE",EDGE,{"disambiguationData":[OSD([subQ1])],"isStart":false}),makeQuery(id+"F1.opExtrude","CAP_FACE",FACE,{"disambiguationData":[OSD([subQ17,subQ16,subQ15,subQ14,subQ13,subQ12,subQ11,subQ10,subQ9,subQ8,subQ7,subQ6,subQ5,subQ4,subQ3,subQ2,subQ1,subQ0])],"isStart":false})],"blendedInto":[makeQuery(id+"F1.opExtrude","CAP_FACE",FACE,{"disambiguationData":[OSD([subQ17,subQ16,subQ15,subQ14,subQ13,subQ12,subQ11,subQ10,subQ9,subQ8,subQ7,subQ6,subQ5,subQ4,subQ3,subQ2,subQ1,subQ0])],"isStart":false})]})])],"isStart":false}),makeQuery(id+"F3.opExtrude","CAP_FACE",FACE,{"disambiguationData":[OSD([subQ17,subQ16,subQ15,subQ14,subQ13,subQ12,subQ11,subQ10,subQ9,subQ8,subQ7,subQ6,subQ5,subQ4,subQ3,subQ2,subQ1,subQ0])],"isStart":false})],"blendedInto":[makeQuery(id+"F3.opExtrude","CAP_FACE",FACE,{"disambiguationData":[OSD([subQ17,subQ16,subQ15,subQ14,subQ13,subQ12,subQ11,subQ10,subQ9,subQ8,subQ7,subQ6,subQ5,subQ4,subQ3,subQ2,subQ1,subQ0])],"isStart":false})]})])],"isStart":false}),makeQuery(id+"F5.opExtrude","CAP_FACE",FACE,{"disambiguationData":[OSD([subQ17,subQ16,subQ15,subQ14,subQ13,subQ12,subQ11,subQ10,subQ9,subQ8,subQ7,subQ6,subQ5,subQ4,subQ3,subQ2,subQ1,subQ0])],"isStart":false})],"blendedInto":[makeQuery(id+"F5.opExtrude","CAP_FACE",FACE,{"disambiguationData":[OSD([subQ17,subQ16,subQ15,subQ14,subQ13,subQ12,subQ11,subQ10,subQ9,subQ8,subQ7,subQ6,subQ5,subQ4,subQ3,subQ2,subQ1,subQ0])],"isStart":false})]})])],"isStart":false}),makeQuery(id+"F7.opExtrude","CAP_FACE",FACE,{"disambiguationData":[OSD([subQ17,subQ16,subQ15,subQ14,subQ13,subQ12,subQ11,subQ10,subQ9,subQ8,subQ7,subQ6,subQ5,subQ4,subQ3,subQ2,subQ1,subQ0])],"isStart":false})],"blendedInto":[makeQuery(id+"F7.opExtrude","CAP_FACE",FACE,{"disambiguationData":[OSD([subQ17,subQ16,subQ15,subQ14,subQ13,subQ12,subQ11,subQ10,subQ9,subQ8,subQ7,subQ6,subQ5,subQ4,subQ3,subQ2,subQ1,subQ0])],"isStart":false})]})])],"isStart":false});}
            var Q6;
            {var subQ0=sQuery(id+"F0.wireOp",EDGE,"E3.4");var subQ1=sQuery(id+"F0.wireOp",EDGE,"E3.3");var subQ2=sQuery(id+"F0.wireOp",EDGE,"E3.2");var subQ3=sQuery(id+"F0.wireOp",EDGE,"E3.1");var subQ4=sQuery(id+"F0.wireOp",EDGE,"E2.5");var subQ5=sQuery(id+"F0.wireOp",EDGE,"E2.4");var subQ6=sQuery(id+"F0.wireOp",EDGE,"E2.3");var subQ7=sQuery(id+"F0.wireOp",EDGE,"E2.2");var subQ8=sQuery(id+"F0.wireOp",EDGE,"E1.4");var subQ9=sQuery(id+"F0.wireOp",EDGE,"E1.3");var subQ10=sQuery(id+"F0.wireOp",EDGE,"E1.2");var subQ11=sQuery(id+"F0.wireOp",EDGE,"E1.1");var subQ12=sQuery(id+"F0.wireOp",EDGE,"E0.5");var subQ13=sQuery(id+"F0.wireOp",EDGE,"E0.4");var subQ14=sQuery(id+"F0.wireOp",EDGE,"E0.3");var subQ15=sQuery(id+"F0.wireOp",EDGE,"E0.2");var subQ16=sQuery(id+"F0.wireOp",EDGE,"E0.1");var subQ17=sQuery(id+"F0.wireOp",EDGE,"E0.0");Q6=makeQuery(id+"F9.opExtrude","CAP_EDGE",EDGE,{"disambiguationData":[OSD([subQ17,subQ16,subQ15,subQ14,subQ13,subQ12,subQ11,subQ10,subQ9,subQ8,subQ7,subQ6,subQ5,subQ4,subQ3,subQ2,subQ1,subQ0]),TDD([makeQuery(id+"F8.opChamfer","BLEND_EDGE",EDGE,{"blendedFrom":[makeQuery(id+"F7.opExtrude","CAP_EDGE",EDGE,{"disambiguationData":[OSD([subQ17,subQ16,subQ15,subQ14,subQ13,subQ12,subQ11,subQ10,subQ9,subQ8,subQ7,subQ6,subQ5,subQ4,subQ3,subQ2,subQ1,subQ0]),TDD([makeQuery(id+"F6.opChamfer","BLEND_EDGE",EDGE,{"blendedFrom":[makeQuery(id+"F5.opExtrude","CAP_EDGE",EDGE,{"disambiguationData":[OSD([subQ17,subQ16,subQ15,subQ14,subQ13,subQ12,subQ11,subQ10,subQ9,subQ8,subQ7,subQ6,subQ5,subQ4,subQ3,subQ2,subQ1,subQ0]),TDD([makeQuery(id+"F4.opChamfer","BLEND_EDGE",EDGE,{"blendedFrom":[makeQuery(id+"F3.opExtrude","CAP_EDGE",EDGE,{"disambiguationData":[OSD([subQ17,subQ16,subQ15,subQ14,subQ13,subQ12,subQ11,subQ10,subQ9,subQ8,subQ7,subQ6,subQ5,subQ4,subQ3,subQ2,subQ1,subQ0]),TDD([makeQuery(id+"F2.opChamfer","BLEND_EDGE",EDGE,{"blendedFrom":[makeQuery(id+"F1.opExtrude","CAP_EDGE",EDGE,{"disambiguationData":[OSD([subQ2])],"isStart":false}),makeQuery(id+"F1.opExtrude","CAP_FACE",FACE,{"disambiguationData":[OSD([subQ17,subQ16,subQ15,subQ14,subQ13,subQ12,subQ11,subQ10,subQ9,subQ8,subQ7,subQ6,subQ5,subQ4,subQ3,subQ2,subQ1,subQ0])],"isStart":false})],"blendedInto":[makeQuery(id+"F1.opExtrude","CAP_FACE",FACE,{"disambiguationData":[OSD([subQ17,subQ16,subQ15,subQ14,subQ13,subQ12,subQ11,subQ10,subQ9,subQ8,subQ7,subQ6,subQ5,subQ4,subQ3,subQ2,subQ1,subQ0])],"isStart":false})]})])],"isStart":false}),makeQuery(id+"F3.opExtrude","CAP_FACE",FACE,{"disambiguationData":[OSD([subQ17,subQ16,subQ15,subQ14,subQ13,subQ12,subQ11,subQ10,subQ9,subQ8,subQ7,subQ6,subQ5,subQ4,subQ3,subQ2,subQ1,subQ0])],"isStart":false})],"blendedInto":[makeQuery(id+"F3.opExtrude","CAP_FACE",FACE,{"disambiguationData":[OSD([subQ17,subQ16,subQ15,subQ14,subQ13,subQ12,subQ11,subQ10,subQ9,subQ8,subQ7,subQ6,subQ5,subQ4,subQ3,subQ2,subQ1,subQ0])],"isStart":false})]})])],"isStart":false}),makeQuery(id+"F5.opExtrude","CAP_FACE",FACE,{"disambiguationData":[OSD([subQ17,subQ16,subQ15,subQ14,subQ13,subQ12,subQ11,subQ10,subQ9,subQ8,subQ7,subQ6,subQ5,subQ4,subQ3,subQ2,subQ1,subQ0])],"isStart":false})],"blendedInto":[makeQuery(id+"F5.opExtrude","CAP_FACE",FACE,{"disambiguationData":[OSD([subQ17,subQ16,subQ15,subQ14,subQ13,subQ12,subQ11,subQ10,subQ9,subQ8,subQ7,subQ6,subQ5,subQ4,subQ3,subQ2,subQ1,subQ0])],"isStart":false})]})])],"isStart":false}),makeQuery(id+"F7.opExtrude","CAP_FACE",FACE,{"disambiguationData":[OSD([subQ17,subQ16,subQ15,subQ14,subQ13,subQ12,subQ11,subQ10,subQ9,subQ8,subQ7,subQ6,subQ5,subQ4,subQ3,subQ2,subQ1,subQ0])],"isStart":false})],"blendedInto":[makeQuery(id+"F7.opExtrude","CAP_FACE",FACE,{"disambiguationData":[OSD([subQ17,subQ16,subQ15,subQ14,subQ13,subQ12,subQ11,subQ10,subQ9,subQ8,subQ7,subQ6,subQ5,subQ4,subQ3,subQ2,subQ1,subQ0])],"isStart":false})]})])],"isStart":false});}
            var Q7;
            {var subQ0=sQuery(id+"F0.wireOp",EDGE,"E3.4");var subQ1=sQuery(id+"F0.wireOp",EDGE,"E3.3");var subQ2=sQuery(id+"F0.wireOp",EDGE,"E3.2");var subQ3=sQuery(id+"F0.wireOp",EDGE,"E3.1");var subQ4=sQuery(id+"F0.wireOp",EDGE,"E2.5");var subQ5=sQuery(id+"F0.wireOp",EDGE,"E2.4");var subQ6=sQuery(id+"F0.wireOp",EDGE,"E2.3");var subQ7=sQuery(id+"F0.wireOp",EDGE,"E2.2");var subQ8=sQuery(id+"F0.wireOp",EDGE,"E1.4");var subQ9=sQuery(id+"F0.wireOp",EDGE,"E1.3");var subQ10=sQuery(id+"F0.wireOp",EDGE,"E1.2");var subQ11=sQuery(id+"F0.wireOp",EDGE,"E1.1");var subQ12=sQuery(id+"F0.wireOp",EDGE,"E0.5");var subQ13=sQuery(id+"F0.wireOp",EDGE,"E0.4");var subQ14=sQuery(id+"F0.wireOp",EDGE,"E0.3");var subQ15=sQuery(id+"F0.wireOp",EDGE,"E0.2");var subQ16=sQuery(id+"F0.wireOp",EDGE,"E0.1");var subQ17=sQuery(id+"F0.wireOp",EDGE,"E0.0");Q7=makeQuery(id+"F9.opExtrude","CAP_EDGE",EDGE,{"disambiguationData":[OSD([subQ17,subQ16,subQ15,subQ14,subQ13,subQ12,subQ11,subQ10,subQ9,subQ8,subQ7,subQ6,subQ5,subQ4,subQ3,subQ2,subQ1,subQ0]),TDD([makeQuery(id+"F8.opChamfer","BLEND_EDGE",EDGE,{"blendedFrom":[makeQuery(id+"F7.opExtrude","CAP_EDGE",EDGE,{"disambiguationData":[OSD([subQ17,subQ16,subQ15,subQ14,subQ13,subQ12,subQ11,subQ10,subQ9,subQ8,subQ7,subQ6,subQ5,subQ4,subQ3,subQ2,subQ1,subQ0]),TDD([makeQuery(id+"F6.opChamfer","BLEND_EDGE",EDGE,{"blendedFrom":[makeQuery(id+"F5.opExtrude","CAP_EDGE",EDGE,{"disambiguationData":[OSD([subQ17,subQ16,subQ15,subQ14,subQ13,subQ12,subQ11,subQ10,subQ9,subQ8,subQ7,subQ6,subQ5,subQ4,subQ3,subQ2,subQ1,subQ0]),TDD([makeQuery(id+"F4.opChamfer","BLEND_EDGE",EDGE,{"blendedFrom":[makeQuery(id+"F3.opExtrude","CAP_EDGE",EDGE,{"disambiguationData":[OSD([subQ17,subQ16,subQ15,subQ14,subQ13,subQ12,subQ11,subQ10,subQ9,subQ8,subQ7,subQ6,subQ5,subQ4,subQ3,subQ2,subQ1,subQ0]),TDD([makeQuery(id+"F2.opChamfer","BLEND_EDGE",EDGE,{"blendedFrom":[makeQuery(id+"F1.opExtrude","CAP_EDGE",EDGE,{"disambiguationData":[OSD([subQ3])],"isStart":false}),makeQuery(id+"F1.opExtrude","CAP_FACE",FACE,{"disambiguationData":[OSD([subQ17,subQ16,subQ15,subQ14,subQ13,subQ12,subQ11,subQ10,subQ9,subQ8,subQ7,subQ6,subQ5,subQ4,subQ3,subQ2,subQ1,subQ0])],"isStart":false})],"blendedInto":[makeQuery(id+"F1.opExtrude","CAP_FACE",FACE,{"disambiguationData":[OSD([subQ17,subQ16,subQ15,subQ14,subQ13,subQ12,subQ11,subQ10,subQ9,subQ8,subQ7,subQ6,subQ5,subQ4,subQ3,subQ2,subQ1,subQ0])],"isStart":false})]})])],"isStart":false}),makeQuery(id+"F3.opExtrude","CAP_FACE",FACE,{"disambiguationData":[OSD([subQ17,subQ16,subQ15,subQ14,subQ13,subQ12,subQ11,subQ10,subQ9,subQ8,subQ7,subQ6,subQ5,subQ4,subQ3,subQ2,subQ1,subQ0])],"isStart":false})],"blendedInto":[makeQuery(id+"F3.opExtrude","CAP_FACE",FACE,{"disambiguationData":[OSD([subQ17,subQ16,subQ15,subQ14,subQ13,subQ12,subQ11,subQ10,subQ9,subQ8,subQ7,subQ6,subQ5,subQ4,subQ3,subQ2,subQ1,subQ0])],"isStart":false})]})])],"isStart":false}),makeQuery(id+"F5.opExtrude","CAP_FACE",FACE,{"disambiguationData":[OSD([subQ17,subQ16,subQ15,subQ14,subQ13,subQ12,subQ11,subQ10,subQ9,subQ8,subQ7,subQ6,subQ5,subQ4,subQ3,subQ2,subQ1,subQ0])],"isStart":false})],"blendedInto":[makeQuery(id+"F5.opExtrude","CAP_FACE",FACE,{"disambiguationData":[OSD([subQ17,subQ16,subQ15,subQ14,subQ13,subQ12,subQ11,subQ10,subQ9,subQ8,subQ7,subQ6,subQ5,subQ4,subQ3,subQ2,subQ1,subQ0])],"isStart":false})]})])],"isStart":false}),makeQuery(id+"F7.opExtrude","CAP_FACE",FACE,{"disambiguationData":[OSD([subQ17,subQ16,subQ15,subQ14,subQ13,subQ12,subQ11,subQ10,subQ9,subQ8,subQ7,subQ6,subQ5,subQ4,subQ3,subQ2,subQ1,subQ0])],"isStart":false})],"blendedInto":[makeQuery(id+"F7.opExtrude","CAP_FACE",FACE,{"disambiguationData":[OSD([subQ17,subQ16,subQ15,subQ14,subQ13,subQ12,subQ11,subQ10,subQ9,subQ8,subQ7,subQ6,subQ5,subQ4,subQ3,subQ2,subQ1,subQ0])],"isStart":false})]})])],"isStart":false});}
            var Q8;
            {var subQ0=sQuery(id+"F0.wireOp",EDGE,"E3.4");var subQ1=sQuery(id+"F0.wireOp",EDGE,"E3.3");var subQ2=sQuery(id+"F0.wireOp",EDGE,"E3.2");var subQ3=sQuery(id+"F0.wireOp",EDGE,"E3.1");var subQ4=sQuery(id+"F0.wireOp",EDGE,"E2.5");var subQ5=sQuery(id+"F0.wireOp",EDGE,"E2.4");var subQ6=sQuery(id+"F0.wireOp",EDGE,"E2.3");var subQ7=sQuery(id+"F0.wireOp",EDGE,"E2.2");var subQ8=sQuery(id+"F0.wireOp",EDGE,"E1.4");var subQ9=sQuery(id+"F0.wireOp",EDGE,"E1.3");var subQ10=sQuery(id+"F0.wireOp",EDGE,"E1.2");var subQ11=sQuery(id+"F0.wireOp",EDGE,"E1.1");var subQ12=sQuery(id+"F0.wireOp",EDGE,"E0.5");var subQ13=sQuery(id+"F0.wireOp",EDGE,"E0.4");var subQ14=sQuery(id+"F0.wireOp",EDGE,"E0.3");var subQ15=sQuery(id+"F0.wireOp",EDGE,"E0.2");var subQ16=sQuery(id+"F0.wireOp",EDGE,"E0.1");var subQ17=sQuery(id+"F0.wireOp",EDGE,"E0.0");Q8=makeQuery(id+"F9.opExtrude","CAP_EDGE",EDGE,{"disambiguationData":[OSD([subQ17,subQ16,subQ15,subQ14,subQ13,subQ12,subQ11,subQ10,subQ9,subQ8,subQ7,subQ6,subQ5,subQ4,subQ3,subQ2,subQ1,subQ0]),TDD([makeQuery(id+"F8.opChamfer","BLEND_EDGE",EDGE,{"blendedFrom":[makeQuery(id+"F7.opExtrude","CAP_EDGE",EDGE,{"disambiguationData":[OSD([subQ17,subQ16,subQ15,subQ14,subQ13,subQ12,subQ11,subQ10,subQ9,subQ8,subQ7,subQ6,subQ5,subQ4,subQ3,subQ2,subQ1,subQ0]),TDD([makeQuery(id+"F6.opChamfer","BLEND_EDGE",EDGE,{"blendedFrom":[makeQuery(id+"F5.opExtrude","CAP_EDGE",EDGE,{"disambiguationData":[OSD([subQ17,subQ16,subQ15,subQ14,subQ13,subQ12,subQ11,subQ10,subQ9,subQ8,subQ7,subQ6,subQ5,subQ4,subQ3,subQ2,subQ1,subQ0]),TDD([makeQuery(id+"F4.opChamfer","BLEND_EDGE",EDGE,{"blendedFrom":[makeQuery(id+"F3.opExtrude","CAP_EDGE",EDGE,{"disambiguationData":[OSD([subQ17,subQ16,subQ15,subQ14,subQ13,subQ12,subQ11,subQ10,subQ9,subQ8,subQ7,subQ6,subQ5,subQ4,subQ3,subQ2,subQ1,subQ0]),TDD([makeQuery(id+"F2.opChamfer","BLEND_EDGE",EDGE,{"blendedFrom":[makeQuery(id+"F1.opExtrude","CAP_EDGE",EDGE,{"disambiguationData":[OSD([subQ4])],"isStart":false}),makeQuery(id+"F1.opExtrude","CAP_FACE",FACE,{"disambiguationData":[OSD([subQ17,subQ16,subQ15,subQ14,subQ13,subQ12,subQ11,subQ10,subQ9,subQ8,subQ7,subQ6,subQ5,subQ4,subQ3,subQ2,subQ1,subQ0])],"isStart":false})],"blendedInto":[makeQuery(id+"F1.opExtrude","CAP_FACE",FACE,{"disambiguationData":[OSD([subQ17,subQ16,subQ15,subQ14,subQ13,subQ12,subQ11,subQ10,subQ9,subQ8,subQ7,subQ6,subQ5,subQ4,subQ3,subQ2,subQ1,subQ0])],"isStart":false})]})])],"isStart":false}),makeQuery(id+"F3.opExtrude","CAP_FACE",FACE,{"disambiguationData":[OSD([subQ17,subQ16,subQ15,subQ14,subQ13,subQ12,subQ11,subQ10,subQ9,subQ8,subQ7,subQ6,subQ5,subQ4,subQ3,subQ2,subQ1,subQ0])],"isStart":false})],"blendedInto":[makeQuery(id+"F3.opExtrude","CAP_FACE",FACE,{"disambiguationData":[OSD([subQ17,subQ16,subQ15,subQ14,subQ13,subQ12,subQ11,subQ10,subQ9,subQ8,subQ7,subQ6,subQ5,subQ4,subQ3,subQ2,subQ1,subQ0])],"isStart":false})]})])],"isStart":false}),makeQuery(id+"F5.opExtrude","CAP_FACE",FACE,{"disambiguationData":[OSD([subQ17,subQ16,subQ15,subQ14,subQ13,subQ12,subQ11,subQ10,subQ9,subQ8,subQ7,subQ6,subQ5,subQ4,subQ3,subQ2,subQ1,subQ0])],"isStart":false})],"blendedInto":[makeQuery(id+"F5.opExtrude","CAP_FACE",FACE,{"disambiguationData":[OSD([subQ17,subQ16,subQ15,subQ14,subQ13,subQ12,subQ11,subQ10,subQ9,subQ8,subQ7,subQ6,subQ5,subQ4,subQ3,subQ2,subQ1,subQ0])],"isStart":false})]})])],"isStart":false}),makeQuery(id+"F7.opExtrude","CAP_FACE",FACE,{"disambiguationData":[OSD([subQ17,subQ16,subQ15,subQ14,subQ13,subQ12,subQ11,subQ10,subQ9,subQ8,subQ7,subQ6,subQ5,subQ4,subQ3,subQ2,subQ1,subQ0])],"isStart":false})],"blendedInto":[makeQuery(id+"F7.opExtrude","CAP_FACE",FACE,{"disambiguationData":[OSD([subQ17,subQ16,subQ15,subQ14,subQ13,subQ12,subQ11,subQ10,subQ9,subQ8,subQ7,subQ6,subQ5,subQ4,subQ3,subQ2,subQ1,subQ0])],"isStart":false})]})])],"isStart":false});}
            var Q9;
            {var subQ0=sQuery(id+"F0.wireOp",EDGE,"E3.4");var subQ1=sQuery(id+"F0.wireOp",EDGE,"E3.3");var subQ2=sQuery(id+"F0.wireOp",EDGE,"E3.2");var subQ3=sQuery(id+"F0.wireOp",EDGE,"E3.1");var subQ4=sQuery(id+"F0.wireOp",EDGE,"E2.5");var subQ5=sQuery(id+"F0.wireOp",EDGE,"E2.4");var subQ6=sQuery(id+"F0.wireOp",EDGE,"E2.3");var subQ7=sQuery(id+"F0.wireOp",EDGE,"E2.2");var subQ8=sQuery(id+"F0.wireOp",EDGE,"E1.4");var subQ9=sQuery(id+"F0.wireOp",EDGE,"E1.3");var subQ10=sQuery(id+"F0.wireOp",EDGE,"E1.2");var subQ11=sQuery(id+"F0.wireOp",EDGE,"E1.1");var subQ12=sQuery(id+"F0.wireOp",EDGE,"E0.5");var subQ13=sQuery(id+"F0.wireOp",EDGE,"E0.4");var subQ14=sQuery(id+"F0.wireOp",EDGE,"E0.3");var subQ15=sQuery(id+"F0.wireOp",EDGE,"E0.2");var subQ16=sQuery(id+"F0.wireOp",EDGE,"E0.1");var subQ17=sQuery(id+"F0.wireOp",EDGE,"E0.0");Q9=makeQuery(id+"F9.opExtrude","CAP_EDGE",EDGE,{"disambiguationData":[OSD([subQ17,subQ16,subQ15,subQ14,subQ13,subQ12,subQ11,subQ10,subQ9,subQ8,subQ7,subQ6,subQ5,subQ4,subQ3,subQ2,subQ1,subQ0]),TDD([makeQuery(id+"F8.opChamfer","BLEND_EDGE",EDGE,{"blendedFrom":[makeQuery(id+"F7.opExtrude","CAP_EDGE",EDGE,{"disambiguationData":[OSD([subQ17,subQ16,subQ15,subQ14,subQ13,subQ12,subQ11,subQ10,subQ9,subQ8,subQ7,subQ6,subQ5,subQ4,subQ3,subQ2,subQ1,subQ0]),TDD([makeQuery(id+"F6.opChamfer","BLEND_EDGE",EDGE,{"blendedFrom":[makeQuery(id+"F5.opExtrude","CAP_EDGE",EDGE,{"disambiguationData":[OSD([subQ17,subQ16,subQ15,subQ14,subQ13,subQ12,subQ11,subQ10,subQ9,subQ8,subQ7,subQ6,subQ5,subQ4,subQ3,subQ2,subQ1,subQ0]),TDD([makeQuery(id+"F4.opChamfer","BLEND_EDGE",EDGE,{"blendedFrom":[makeQuery(id+"F3.opExtrude","CAP_EDGE",EDGE,{"disambiguationData":[OSD([subQ17,subQ16,subQ15,subQ14,subQ13,subQ12,subQ11,subQ10,subQ9,subQ8,subQ7,subQ6,subQ5,subQ4,subQ3,subQ2,subQ1,subQ0]),TDD([makeQuery(id+"F2.opChamfer","BLEND_EDGE",EDGE,{"blendedFrom":[makeQuery(id+"F1.opExtrude","CAP_EDGE",EDGE,{"disambiguationData":[OSD([subQ5])],"isStart":false}),makeQuery(id+"F1.opExtrude","CAP_FACE",FACE,{"disambiguationData":[OSD([subQ17,subQ16,subQ15,subQ14,subQ13,subQ12,subQ11,subQ10,subQ9,subQ8,subQ7,subQ6,subQ5,subQ4,subQ3,subQ2,subQ1,subQ0])],"isStart":false})],"blendedInto":[makeQuery(id+"F1.opExtrude","CAP_FACE",FACE,{"disambiguationData":[OSD([subQ17,subQ16,subQ15,subQ14,subQ13,subQ12,subQ11,subQ10,subQ9,subQ8,subQ7,subQ6,subQ5,subQ4,subQ3,subQ2,subQ1,subQ0])],"isStart":false})]})])],"isStart":false}),makeQuery(id+"F3.opExtrude","CAP_FACE",FACE,{"disambiguationData":[OSD([subQ17,subQ16,subQ15,subQ14,subQ13,subQ12,subQ11,subQ10,subQ9,subQ8,subQ7,subQ6,subQ5,subQ4,subQ3,subQ2,subQ1,subQ0])],"isStart":false})],"blendedInto":[makeQuery(id+"F3.opExtrude","CAP_FACE",FACE,{"disambiguationData":[OSD([subQ17,subQ16,subQ15,subQ14,subQ13,subQ12,subQ11,subQ10,subQ9,subQ8,subQ7,subQ6,subQ5,subQ4,subQ3,subQ2,subQ1,subQ0])],"isStart":false})]})])],"isStart":false}),makeQuery(id+"F5.opExtrude","CAP_FACE",FACE,{"disambiguationData":[OSD([subQ17,subQ16,subQ15,subQ14,subQ13,subQ12,subQ11,subQ10,subQ9,subQ8,subQ7,subQ6,subQ5,subQ4,subQ3,subQ2,subQ1,subQ0])],"isStart":false})],"blendedInto":[makeQuery(id+"F5.opExtrude","CAP_FACE",FACE,{"disambiguationData":[OSD([subQ17,subQ16,subQ15,subQ14,subQ13,subQ12,subQ11,subQ10,subQ9,subQ8,subQ7,subQ6,subQ5,subQ4,subQ3,subQ2,subQ1,subQ0])],"isStart":false})]})])],"isStart":false}),makeQuery(id+"F7.opExtrude","CAP_FACE",FACE,{"disambiguationData":[OSD([subQ17,subQ16,subQ15,subQ14,subQ13,subQ12,subQ11,subQ10,subQ9,subQ8,subQ7,subQ6,subQ5,subQ4,subQ3,subQ2,subQ1,subQ0])],"isStart":false})],"blendedInto":[makeQuery(id+"F7.opExtrude","CAP_FACE",FACE,{"disambiguationData":[OSD([subQ17,subQ16,subQ15,subQ14,subQ13,subQ12,subQ11,subQ10,subQ9,subQ8,subQ7,subQ6,subQ5,subQ4,subQ3,subQ2,subQ1,subQ0])],"isStart":false})]})])],"isStart":false});}
            var Q10;
            {var subQ0=sQuery(id+"F0.wireOp",EDGE,"E3.4");var subQ1=sQuery(id+"F0.wireOp",EDGE,"E3.3");var subQ2=sQuery(id+"F0.wireOp",EDGE,"E3.2");var subQ3=sQuery(id+"F0.wireOp",EDGE,"E3.1");var subQ4=sQuery(id+"F0.wireOp",EDGE,"E2.5");var subQ5=sQuery(id+"F0.wireOp",EDGE,"E2.4");var subQ6=sQuery(id+"F0.wireOp",EDGE,"E2.3");var subQ7=sQuery(id+"F0.wireOp",EDGE,"E2.2");var subQ8=sQuery(id+"F0.wireOp",EDGE,"E1.4");var subQ9=sQuery(id+"F0.wireOp",EDGE,"E1.3");var subQ10=sQuery(id+"F0.wireOp",EDGE,"E1.2");var subQ11=sQuery(id+"F0.wireOp",EDGE,"E1.1");var subQ12=sQuery(id+"F0.wireOp",EDGE,"E0.5");var subQ13=sQuery(id+"F0.wireOp",EDGE,"E0.4");var subQ14=sQuery(id+"F0.wireOp",EDGE,"E0.3");var subQ15=sQuery(id+"F0.wireOp",EDGE,"E0.2");var subQ16=sQuery(id+"F0.wireOp",EDGE,"E0.1");var subQ17=sQuery(id+"F0.wireOp",EDGE,"E0.0");Q10=makeQuery(id+"F9.opExtrude","CAP_EDGE",EDGE,{"disambiguationData":[OSD([subQ17,subQ16,subQ15,subQ14,subQ13,subQ12,subQ11,subQ10,subQ9,subQ8,subQ7,subQ6,subQ5,subQ4,subQ3,subQ2,subQ1,subQ0]),TDD([makeQuery(id+"F8.opChamfer","BLEND_EDGE",EDGE,{"blendedFrom":[makeQuery(id+"F7.opExtrude","CAP_EDGE",EDGE,{"disambiguationData":[OSD([subQ17,subQ16,subQ15,subQ14,subQ13,subQ12,subQ11,subQ10,subQ9,subQ8,subQ7,subQ6,subQ5,subQ4,subQ3,subQ2,subQ1,subQ0]),TDD([makeQuery(id+"F6.opChamfer","BLEND_EDGE",EDGE,{"blendedFrom":[makeQuery(id+"F5.opExtrude","CAP_EDGE",EDGE,{"disambiguationData":[OSD([subQ17,subQ16,subQ15,subQ14,subQ13,subQ12,subQ11,subQ10,subQ9,subQ8,subQ7,subQ6,subQ5,subQ4,subQ3,subQ2,subQ1,subQ0]),TDD([makeQuery(id+"F4.opChamfer","BLEND_EDGE",EDGE,{"blendedFrom":[makeQuery(id+"F3.opExtrude","CAP_EDGE",EDGE,{"disambiguationData":[OSD([subQ17,subQ16,subQ15,subQ14,subQ13,subQ12,subQ11,subQ10,subQ9,subQ8,subQ7,subQ6,subQ5,subQ4,subQ3,subQ2,subQ1,subQ0]),TDD([makeQuery(id+"F2.opChamfer","BLEND_EDGE",EDGE,{"blendedFrom":[makeQuery(id+"F1.opExtrude","CAP_EDGE",EDGE,{"disambiguationData":[OSD([subQ6])],"isStart":false}),makeQuery(id+"F1.opExtrude","CAP_FACE",FACE,{"disambiguationData":[OSD([subQ17,subQ16,subQ15,subQ14,subQ13,subQ12,subQ11,subQ10,subQ9,subQ8,subQ7,subQ6,subQ5,subQ4,subQ3,subQ2,subQ1,subQ0])],"isStart":false})],"blendedInto":[makeQuery(id+"F1.opExtrude","CAP_FACE",FACE,{"disambiguationData":[OSD([subQ17,subQ16,subQ15,subQ14,subQ13,subQ12,subQ11,subQ10,subQ9,subQ8,subQ7,subQ6,subQ5,subQ4,subQ3,subQ2,subQ1,subQ0])],"isStart":false})]})])],"isStart":false}),makeQuery(id+"F3.opExtrude","CAP_FACE",FACE,{"disambiguationData":[OSD([subQ17,subQ16,subQ15,subQ14,subQ13,subQ12,subQ11,subQ10,subQ9,subQ8,subQ7,subQ6,subQ5,subQ4,subQ3,subQ2,subQ1,subQ0])],"isStart":false})],"blendedInto":[makeQuery(id+"F3.opExtrude","CAP_FACE",FACE,{"disambiguationData":[OSD([subQ17,subQ16,subQ15,subQ14,subQ13,subQ12,subQ11,subQ10,subQ9,subQ8,subQ7,subQ6,subQ5,subQ4,subQ3,subQ2,subQ1,subQ0])],"isStart":false})]})])],"isStart":false}),makeQuery(id+"F5.opExtrude","CAP_FACE",FACE,{"disambiguationData":[OSD([subQ17,subQ16,subQ15,subQ14,subQ13,subQ12,subQ11,subQ10,subQ9,subQ8,subQ7,subQ6,subQ5,subQ4,subQ3,subQ2,subQ1,subQ0])],"isStart":false})],"blendedInto":[makeQuery(id+"F5.opExtrude","CAP_FACE",FACE,{"disambiguationData":[OSD([subQ17,subQ16,subQ15,subQ14,subQ13,subQ12,subQ11,subQ10,subQ9,subQ8,subQ7,subQ6,subQ5,subQ4,subQ3,subQ2,subQ1,subQ0])],"isStart":false})]})])],"isStart":false}),makeQuery(id+"F7.opExtrude","CAP_FACE",FACE,{"disambiguationData":[OSD([subQ17,subQ16,subQ15,subQ14,subQ13,subQ12,subQ11,subQ10,subQ9,subQ8,subQ7,subQ6,subQ5,subQ4,subQ3,subQ2,subQ1,subQ0])],"isStart":false})],"blendedInto":[makeQuery(id+"F7.opExtrude","CAP_FACE",FACE,{"disambiguationData":[OSD([subQ17,subQ16,subQ15,subQ14,subQ13,subQ12,subQ11,subQ10,subQ9,subQ8,subQ7,subQ6,subQ5,subQ4,subQ3,subQ2,subQ1,subQ0])],"isStart":false})]})])],"isStart":false});}
            var Q11;
            {var subQ0=sQuery(id+"F0.wireOp",EDGE,"E3.4");var subQ1=sQuery(id+"F0.wireOp",EDGE,"E3.3");var subQ2=sQuery(id+"F0.wireOp",EDGE,"E3.2");var subQ3=sQuery(id+"F0.wireOp",EDGE,"E3.1");var subQ4=sQuery(id+"F0.wireOp",EDGE,"E2.5");var subQ5=sQuery(id+"F0.wireOp",EDGE,"E2.4");var subQ6=sQuery(id+"F0.wireOp",EDGE,"E2.3");var subQ7=sQuery(id+"F0.wireOp",EDGE,"E2.2");var subQ8=sQuery(id+"F0.wireOp",EDGE,"E1.4");var subQ9=sQuery(id+"F0.wireOp",EDGE,"E1.3");var subQ10=sQuery(id+"F0.wireOp",EDGE,"E1.2");var subQ11=sQuery(id+"F0.wireOp",EDGE,"E1.1");var subQ12=sQuery(id+"F0.wireOp",EDGE,"E0.5");var subQ13=sQuery(id+"F0.wireOp",EDGE,"E0.4");var subQ14=sQuery(id+"F0.wireOp",EDGE,"E0.3");var subQ15=sQuery(id+"F0.wireOp",EDGE,"E0.2");var subQ16=sQuery(id+"F0.wireOp",EDGE,"E0.1");var subQ17=sQuery(id+"F0.wireOp",EDGE,"E0.0");Q11=makeQuery(id+"F9.opExtrude","CAP_EDGE",EDGE,{"disambiguationData":[OSD([subQ17,subQ16,subQ15,subQ14,subQ13,subQ12,subQ11,subQ10,subQ9,subQ8,subQ7,subQ6,subQ5,subQ4,subQ3,subQ2,subQ1,subQ0]),TDD([makeQuery(id+"F8.opChamfer","BLEND_EDGE",EDGE,{"blendedFrom":[makeQuery(id+"F7.opExtrude","CAP_EDGE",EDGE,{"disambiguationData":[OSD([subQ17,subQ16,subQ15,subQ14,subQ13,subQ12,subQ11,subQ10,subQ9,subQ8,subQ7,subQ6,subQ5,subQ4,subQ3,subQ2,subQ1,subQ0]),TDD([makeQuery(id+"F6.opChamfer","BLEND_EDGE",EDGE,{"blendedFrom":[makeQuery(id+"F5.opExtrude","CAP_EDGE",EDGE,{"disambiguationData":[OSD([subQ17,subQ16,subQ15,subQ14,subQ13,subQ12,subQ11,subQ10,subQ9,subQ8,subQ7,subQ6,subQ5,subQ4,subQ3,subQ2,subQ1,subQ0]),TDD([makeQuery(id+"F4.opChamfer","BLEND_EDGE",EDGE,{"blendedFrom":[makeQuery(id+"F3.opExtrude","CAP_EDGE",EDGE,{"disambiguationData":[OSD([subQ17,subQ16,subQ15,subQ14,subQ13,subQ12,subQ11,subQ10,subQ9,subQ8,subQ7,subQ6,subQ5,subQ4,subQ3,subQ2,subQ1,subQ0]),TDD([makeQuery(id+"F2.opChamfer","BLEND_EDGE",EDGE,{"blendedFrom":[makeQuery(id+"F1.opExtrude","CAP_EDGE",EDGE,{"disambiguationData":[OSD([subQ7])],"isStart":false}),makeQuery(id+"F1.opExtrude","CAP_FACE",FACE,{"disambiguationData":[OSD([subQ17,subQ16,subQ15,subQ14,subQ13,subQ12,subQ11,subQ10,subQ9,subQ8,subQ7,subQ6,subQ5,subQ4,subQ3,subQ2,subQ1,subQ0])],"isStart":false})],"blendedInto":[makeQuery(id+"F1.opExtrude","CAP_FACE",FACE,{"disambiguationData":[OSD([subQ17,subQ16,subQ15,subQ14,subQ13,subQ12,subQ11,subQ10,subQ9,subQ8,subQ7,subQ6,subQ5,subQ4,subQ3,subQ2,subQ1,subQ0])],"isStart":false})]})])],"isStart":false}),makeQuery(id+"F3.opExtrude","CAP_FACE",FACE,{"disambiguationData":[OSD([subQ17,subQ16,subQ15,subQ14,subQ13,subQ12,subQ11,subQ10,subQ9,subQ8,subQ7,subQ6,subQ5,subQ4,subQ3,subQ2,subQ1,subQ0])],"isStart":false})],"blendedInto":[makeQuery(id+"F3.opExtrude","CAP_FACE",FACE,{"disambiguationData":[OSD([subQ17,subQ16,subQ15,subQ14,subQ13,subQ12,subQ11,subQ10,subQ9,subQ8,subQ7,subQ6,subQ5,subQ4,subQ3,subQ2,subQ1,subQ0])],"isStart":false})]})])],"isStart":false}),makeQuery(id+"F5.opExtrude","CAP_FACE",FACE,{"disambiguationData":[OSD([subQ17,subQ16,subQ15,subQ14,subQ13,subQ12,subQ11,subQ10,subQ9,subQ8,subQ7,subQ6,subQ5,subQ4,subQ3,subQ2,subQ1,subQ0])],"isStart":false})],"blendedInto":[makeQuery(id+"F5.opExtrude","CAP_FACE",FACE,{"disambiguationData":[OSD([subQ17,subQ16,subQ15,subQ14,subQ13,subQ12,subQ11,subQ10,subQ9,subQ8,subQ7,subQ6,subQ5,subQ4,subQ3,subQ2,subQ1,subQ0])],"isStart":false})]})])],"isStart":false}),makeQuery(id+"F7.opExtrude","CAP_FACE",FACE,{"disambiguationData":[OSD([subQ17,subQ16,subQ15,subQ14,subQ13,subQ12,subQ11,subQ10,subQ9,subQ8,subQ7,subQ6,subQ5,subQ4,subQ3,subQ2,subQ1,subQ0])],"isStart":false})],"blendedInto":[makeQuery(id+"F7.opExtrude","CAP_FACE",FACE,{"disambiguationData":[OSD([subQ17,subQ16,subQ15,subQ14,subQ13,subQ12,subQ11,subQ10,subQ9,subQ8,subQ7,subQ6,subQ5,subQ4,subQ3,subQ2,subQ1,subQ0])],"isStart":false})]})])],"isStart":false});}
            chamfer(context, id + "F10", {"entities" : qUnion([Q0, Q1, Q2, Q3, Q4, Q5, Q6, Q7, Q8, Q9, Q10, Q11]), "width" : 5.08 * mm, "tangentPropagation" : true});
        }
        {
            var Q0;
            Q0=makeQuery(id+"F9.opExtrude","CAP_EDGE",EDGE,{"disambiguationData":[OSD([sQuery(id+"F0.wireOp",EDGE,"E0.0")])],"isStart":false});
            var Q1;
            Q1=makeQuery(id+"F9.opExtrude","CAP_EDGE",EDGE,{"disambiguationData":[OSD([sQuery(id+"F0.wireOp",EDGE,"E0.1")])],"isStart":false});
            var Q2;
            Q2=makeQuery(id+"F9.opExtrude","CAP_EDGE",EDGE,{"disambiguationData":[OSD([sQuery(id+"F0.wireOp",EDGE,"E0.2")])],"isStart":false});
            var Q3;
            Q3=makeQuery(id+"F9.opExtrude","CAP_EDGE",EDGE,{"disambiguationData":[OSD([sQuery(id+"F0.wireOp",EDGE,"E0.3")])],"isStart":false});
            var Q4;
            Q4=makeQuery(id+"F9.opExtrude","CAP_EDGE",EDGE,{"disambiguationData":[OSD([sQuery(id+"F0.wireOp",EDGE,"E0.4")])],"isStart":false});
            var Q5;
            Q5=makeQuery(id+"F9.opExtrude","CAP_EDGE",EDGE,{"disambiguationData":[OSD([sQuery(id+"F0.wireOp",EDGE,"E0.5")])],"isStart":false});
            chamfer(context, id + "F11", {"entities" : qUnion([Q0, Q1, Q2, Q3, Q4, Q5]), "width" : 5.08 * mm, "tangentPropagation" : true});
        }
        {
            var Q0;
            Q0=makeQuery(id+"F9.opExtrude","CAP_FACE",FACE,{"disambiguationData":[OSD([sQuery(id+"F0.wireOp",EDGE,"E0.0"),sQuery(id+"F0.wireOp",EDGE,"E0.1"),sQuery(id+"F0.wireOp",EDGE,"E0.2"),sQuery(id+"F0.wireOp",EDGE,"E0.3"),sQuery(id+"F0.wireOp",EDGE,"E0.4"),sQuery(id+"F0.wireOp",EDGE,"E0.5"),sQuery(id+"F0.wireOp",EDGE,"E1.1"),sQuery(id+"F0.wireOp",EDGE,"E1.2"),sQuery(id+"F0.wireOp",EDGE,"E1.3"),sQuery(id+"F0.wireOp",EDGE,"E1.4"),sQuery(id+"F0.wireOp",EDGE,"E2.2"),sQuery(id+"F0.wireOp",EDGE,"E2.3"),sQuery(id+"F0.wireOp",EDGE,"E2.4"),sQuery(id+"F0.wireOp",EDGE,"E2.5"),sQuery(id+"F0.wireOp",EDGE,"E3.1"),sQuery(id+"F0.wireOp",EDGE,"E3.2"),sQuery(id+"F0.wireOp",EDGE,"E3.3"),sQuery(id+"F0.wireOp",EDGE,"E3.4")])],"isStart":false});
            extrude(context, id + "F12", {"entities" : qUnion([Q0]), "operationType" : NewBodyOperationType.ADD, "depth" : 25.4 * mm});
        }
        {
            var Q0;
            {var subQ0=sQuery(id+"F0.wireOp",EDGE,"E3.4");var subQ1=sQuery(id+"F0.wireOp",EDGE,"E3.3");var subQ2=sQuery(id+"F0.wireOp",EDGE,"E3.2");var subQ3=sQuery(id+"F0.wireOp",EDGE,"E3.1");var subQ4=sQuery(id+"F0.wireOp",EDGE,"E2.5");var subQ5=sQuery(id+"F0.wireOp",EDGE,"E2.4");var subQ6=sQuery(id+"F0.wireOp",EDGE,"E2.3");var subQ7=sQuery(id+"F0.wireOp",EDGE,"E2.2");var subQ8=sQuery(id+"F0.wireOp",EDGE,"E1.4");var subQ9=sQuery(id+"F0.wireOp",EDGE,"E1.3");var subQ10=sQuery(id+"F0.wireOp",EDGE,"E1.2");var subQ11=sQuery(id+"F0.wireOp",EDGE,"E1.1");var subQ12=sQuery(id+"F0.wireOp",EDGE,"E0.5");var subQ13=sQuery(id+"F0.wireOp",EDGE,"E0.4");var subQ14=sQuery(id+"F0.wireOp",EDGE,"E0.3");var subQ15=sQuery(id+"F0.wireOp",EDGE,"E0.2");var subQ16=sQuery(id+"F0.wireOp",EDGE,"E0.1");var subQ17=sQuery(id+"F0.wireOp",EDGE,"E0.0");Q0=makeQuery(id+"F12.opExtrude","CAP_EDGE",EDGE,{"disambiguationData":[OSD([subQ17,subQ16,subQ15,subQ14,subQ13,subQ12,subQ11,subQ10,subQ9,subQ8,subQ7,subQ6,subQ5,subQ4,subQ3,subQ2,subQ1,subQ0]),TDD([makeQuery(id+"F11.opChamfer","BLEND_EDGE",EDGE,{"blendedFrom":[makeQuery(id+"F9.opExtrude","CAP_EDGE",EDGE,{"disambiguationData":[OSD([subQ16])],"isStart":false}),makeQuery(id+"F9.opExtrude","CAP_FACE",FACE,{"disambiguationData":[OSD([subQ17,subQ16,subQ15,subQ14,subQ13,subQ12,subQ11,subQ10,subQ9,subQ8,subQ7,subQ6,subQ5,subQ4,subQ3,subQ2,subQ1,subQ0])],"isStart":false})],"blendedInto":[makeQuery(id+"F9.opExtrude","CAP_FACE",FACE,{"disambiguationData":[OSD([subQ17,subQ16,subQ15,subQ14,subQ13,subQ12,subQ11,subQ10,subQ9,subQ8,subQ7,subQ6,subQ5,subQ4,subQ3,subQ2,subQ1,subQ0])],"isStart":false})]})])],"isStart":false});}
            var Q1;
            {var subQ0=sQuery(id+"F0.wireOp",EDGE,"E3.4");var subQ1=sQuery(id+"F0.wireOp",EDGE,"E3.3");var subQ2=sQuery(id+"F0.wireOp",EDGE,"E3.2");var subQ3=sQuery(id+"F0.wireOp",EDGE,"E3.1");var subQ4=sQuery(id+"F0.wireOp",EDGE,"E2.5");var subQ5=sQuery(id+"F0.wireOp",EDGE,"E2.4");var subQ6=sQuery(id+"F0.wireOp",EDGE,"E2.3");var subQ7=sQuery(id+"F0.wireOp",EDGE,"E2.2");var subQ8=sQuery(id+"F0.wireOp",EDGE,"E1.4");var subQ9=sQuery(id+"F0.wireOp",EDGE,"E1.3");var subQ10=sQuery(id+"F0.wireOp",EDGE,"E1.2");var subQ11=sQuery(id+"F0.wireOp",EDGE,"E1.1");var subQ12=sQuery(id+"F0.wireOp",EDGE,"E0.5");var subQ13=sQuery(id+"F0.wireOp",EDGE,"E0.4");var subQ14=sQuery(id+"F0.wireOp",EDGE,"E0.3");var subQ15=sQuery(id+"F0.wireOp",EDGE,"E0.2");var subQ16=sQuery(id+"F0.wireOp",EDGE,"E0.1");var subQ17=sQuery(id+"F0.wireOp",EDGE,"E0.0");Q1=makeQuery(id+"F12.opExtrude","CAP_EDGE",EDGE,{"disambiguationData":[OSD([subQ17,subQ16,subQ15,subQ14,subQ13,subQ12,subQ11,subQ10,subQ9,subQ8,subQ7,subQ6,subQ5,subQ4,subQ3,subQ2,subQ1,subQ0]),TDD([makeQuery(id+"F11.opChamfer","BLEND_EDGE",EDGE,{"blendedFrom":[makeQuery(id+"F9.opExtrude","CAP_EDGE",EDGE,{"disambiguationData":[OSD([subQ17])],"isStart":false}),makeQuery(id+"F9.opExtrude","CAP_FACE",FACE,{"disambiguationData":[OSD([subQ17,subQ16,subQ15,subQ14,subQ13,subQ12,subQ11,subQ10,subQ9,subQ8,subQ7,subQ6,subQ5,subQ4,subQ3,subQ2,subQ1,subQ0])],"isStart":false})],"blendedInto":[makeQuery(id+"F9.opExtrude","CAP_FACE",FACE,{"disambiguationData":[OSD([subQ17,subQ16,subQ15,subQ14,subQ13,subQ12,subQ11,subQ10,subQ9,subQ8,subQ7,subQ6,subQ5,subQ4,subQ3,subQ2,subQ1,subQ0])],"isStart":false})]})])],"isStart":false});}
            var Q2;
            {var subQ0=sQuery(id+"F0.wireOp",EDGE,"E3.4");var subQ1=sQuery(id+"F0.wireOp",EDGE,"E3.3");var subQ2=sQuery(id+"F0.wireOp",EDGE,"E3.2");var subQ3=sQuery(id+"F0.wireOp",EDGE,"E3.1");var subQ4=sQuery(id+"F0.wireOp",EDGE,"E2.5");var subQ5=sQuery(id+"F0.wireOp",EDGE,"E2.4");var subQ6=sQuery(id+"F0.wireOp",EDGE,"E2.3");var subQ7=sQuery(id+"F0.wireOp",EDGE,"E2.2");var subQ8=sQuery(id+"F0.wireOp",EDGE,"E1.4");var subQ9=sQuery(id+"F0.wireOp",EDGE,"E1.3");var subQ10=sQuery(id+"F0.wireOp",EDGE,"E1.2");var subQ11=sQuery(id+"F0.wireOp",EDGE,"E1.1");var subQ12=sQuery(id+"F0.wireOp",EDGE,"E0.5");var subQ13=sQuery(id+"F0.wireOp",EDGE,"E0.4");var subQ14=sQuery(id+"F0.wireOp",EDGE,"E0.3");var subQ15=sQuery(id+"F0.wireOp",EDGE,"E0.2");var subQ16=sQuery(id+"F0.wireOp",EDGE,"E0.1");var subQ17=sQuery(id+"F0.wireOp",EDGE,"E0.0");Q2=makeQuery(id+"F12.opExtrude","CAP_EDGE",EDGE,{"disambiguationData":[OSD([subQ17,subQ16,subQ15,subQ14,subQ13,subQ12,subQ11,subQ10,subQ9,subQ8,subQ7,subQ6,subQ5,subQ4,subQ3,subQ2,subQ1,subQ0]),TDD([makeQuery(id+"F11.opChamfer","BLEND_EDGE",EDGE,{"blendedFrom":[makeQuery(id+"F9.opExtrude","CAP_EDGE",EDGE,{"disambiguationData":[OSD([subQ12])],"isStart":false}),makeQuery(id+"F9.opExtrude","CAP_FACE",FACE,{"disambiguationData":[OSD([subQ17,subQ16,subQ15,subQ14,subQ13,subQ12,subQ11,subQ10,subQ9,subQ8,subQ7,subQ6,subQ5,subQ4,subQ3,subQ2,subQ1,subQ0])],"isStart":false})],"blendedInto":[makeQuery(id+"F9.opExtrude","CAP_FACE",FACE,{"disambiguationData":[OSD([subQ17,subQ16,subQ15,subQ14,subQ13,subQ12,subQ11,subQ10,subQ9,subQ8,subQ7,subQ6,subQ5,subQ4,subQ3,subQ2,subQ1,subQ0])],"isStart":false})]})])],"isStart":false});}
            var Q3;
            {var subQ0=sQuery(id+"F0.wireOp",EDGE,"E3.4");var subQ1=sQuery(id+"F0.wireOp",EDGE,"E3.3");var subQ2=sQuery(id+"F0.wireOp",EDGE,"E3.2");var subQ3=sQuery(id+"F0.wireOp",EDGE,"E3.1");var subQ4=sQuery(id+"F0.wireOp",EDGE,"E2.5");var subQ5=sQuery(id+"F0.wireOp",EDGE,"E2.4");var subQ6=sQuery(id+"F0.wireOp",EDGE,"E2.3");var subQ7=sQuery(id+"F0.wireOp",EDGE,"E2.2");var subQ8=sQuery(id+"F0.wireOp",EDGE,"E1.4");var subQ9=sQuery(id+"F0.wireOp",EDGE,"E1.3");var subQ10=sQuery(id+"F0.wireOp",EDGE,"E1.2");var subQ11=sQuery(id+"F0.wireOp",EDGE,"E1.1");var subQ12=sQuery(id+"F0.wireOp",EDGE,"E0.5");var subQ13=sQuery(id+"F0.wireOp",EDGE,"E0.4");var subQ14=sQuery(id+"F0.wireOp",EDGE,"E0.3");var subQ15=sQuery(id+"F0.wireOp",EDGE,"E0.2");var subQ16=sQuery(id+"F0.wireOp",EDGE,"E0.1");var subQ17=sQuery(id+"F0.wireOp",EDGE,"E0.0");Q3=makeQuery(id+"F12.opExtrude","CAP_EDGE",EDGE,{"disambiguationData":[OSD([subQ17,subQ16,subQ15,subQ14,subQ13,subQ12,subQ11,subQ10,subQ9,subQ8,subQ7,subQ6,subQ5,subQ4,subQ3,subQ2,subQ1,subQ0]),TDD([makeQuery(id+"F11.opChamfer","BLEND_EDGE",EDGE,{"blendedFrom":[makeQuery(id+"F9.opExtrude","CAP_EDGE",EDGE,{"disambiguationData":[OSD([subQ13])],"isStart":false}),makeQuery(id+"F9.opExtrude","CAP_FACE",FACE,{"disambiguationData":[OSD([subQ17,subQ16,subQ15,subQ14,subQ13,subQ12,subQ11,subQ10,subQ9,subQ8,subQ7,subQ6,subQ5,subQ4,subQ3,subQ2,subQ1,subQ0])],"isStart":false})],"blendedInto":[makeQuery(id+"F9.opExtrude","CAP_FACE",FACE,{"disambiguationData":[OSD([subQ17,subQ16,subQ15,subQ14,subQ13,subQ12,subQ11,subQ10,subQ9,subQ8,subQ7,subQ6,subQ5,subQ4,subQ3,subQ2,subQ1,subQ0])],"isStart":false})]})])],"isStart":false});}
            var Q4;
            {var subQ0=sQuery(id+"F0.wireOp",EDGE,"E3.4");var subQ1=sQuery(id+"F0.wireOp",EDGE,"E3.3");var subQ2=sQuery(id+"F0.wireOp",EDGE,"E3.2");var subQ3=sQuery(id+"F0.wireOp",EDGE,"E3.1");var subQ4=sQuery(id+"F0.wireOp",EDGE,"E2.5");var subQ5=sQuery(id+"F0.wireOp",EDGE,"E2.4");var subQ6=sQuery(id+"F0.wireOp",EDGE,"E2.3");var subQ7=sQuery(id+"F0.wireOp",EDGE,"E2.2");var subQ8=sQuery(id+"F0.wireOp",EDGE,"E1.4");var subQ9=sQuery(id+"F0.wireOp",EDGE,"E1.3");var subQ10=sQuery(id+"F0.wireOp",EDGE,"E1.2");var subQ11=sQuery(id+"F0.wireOp",EDGE,"E1.1");var subQ12=sQuery(id+"F0.wireOp",EDGE,"E0.5");var subQ13=sQuery(id+"F0.wireOp",EDGE,"E0.4");var subQ14=sQuery(id+"F0.wireOp",EDGE,"E0.3");var subQ15=sQuery(id+"F0.wireOp",EDGE,"E0.2");var subQ16=sQuery(id+"F0.wireOp",EDGE,"E0.1");var subQ17=sQuery(id+"F0.wireOp",EDGE,"E0.0");Q4=makeQuery(id+"F12.opExtrude","CAP_EDGE",EDGE,{"disambiguationData":[OSD([subQ17,subQ16,subQ15,subQ14,subQ13,subQ12,subQ11,subQ10,subQ9,subQ8,subQ7,subQ6,subQ5,subQ4,subQ3,subQ2,subQ1,subQ0]),TDD([makeQuery(id+"F11.opChamfer","BLEND_EDGE",EDGE,{"blendedFrom":[makeQuery(id+"F9.opExtrude","CAP_EDGE",EDGE,{"disambiguationData":[OSD([subQ14])],"isStart":false}),makeQuery(id+"F9.opExtrude","CAP_FACE",FACE,{"disambiguationData":[OSD([subQ17,subQ16,subQ15,subQ14,subQ13,subQ12,subQ11,subQ10,subQ9,subQ8,subQ7,subQ6,subQ5,subQ4,subQ3,subQ2,subQ1,subQ0])],"isStart":false})],"blendedInto":[makeQuery(id+"F9.opExtrude","CAP_FACE",FACE,{"disambiguationData":[OSD([subQ17,subQ16,subQ15,subQ14,subQ13,subQ12,subQ11,subQ10,subQ9,subQ8,subQ7,subQ6,subQ5,subQ4,subQ3,subQ2,subQ1,subQ0])],"isStart":false})]})])],"isStart":false});}
            var Q5;
            {var subQ0=sQuery(id+"F0.wireOp",EDGE,"E3.4");var subQ1=sQuery(id+"F0.wireOp",EDGE,"E3.3");var subQ2=sQuery(id+"F0.wireOp",EDGE,"E3.2");var subQ3=sQuery(id+"F0.wireOp",EDGE,"E3.1");var subQ4=sQuery(id+"F0.wireOp",EDGE,"E2.5");var subQ5=sQuery(id+"F0.wireOp",EDGE,"E2.4");var subQ6=sQuery(id+"F0.wireOp",EDGE,"E2.3");var subQ7=sQuery(id+"F0.wireOp",EDGE,"E2.2");var subQ8=sQuery(id+"F0.wireOp",EDGE,"E1.4");var subQ9=sQuery(id+"F0.wireOp",EDGE,"E1.3");var subQ10=sQuery(id+"F0.wireOp",EDGE,"E1.2");var subQ11=sQuery(id+"F0.wireOp",EDGE,"E1.1");var subQ12=sQuery(id+"F0.wireOp",EDGE,"E0.5");var subQ13=sQuery(id+"F0.wireOp",EDGE,"E0.4");var subQ14=sQuery(id+"F0.wireOp",EDGE,"E0.3");var subQ15=sQuery(id+"F0.wireOp",EDGE,"E0.2");var subQ16=sQuery(id+"F0.wireOp",EDGE,"E0.1");var subQ17=sQuery(id+"F0.wireOp",EDGE,"E0.0");Q5=makeQuery(id+"F12.opExtrude","CAP_EDGE",EDGE,{"disambiguationData":[OSD([subQ17,subQ16,subQ15,subQ14,subQ13,subQ12,subQ11,subQ10,subQ9,subQ8,subQ7,subQ6,subQ5,subQ4,subQ3,subQ2,subQ1,subQ0]),TDD([makeQuery(id+"F11.opChamfer","BLEND_EDGE",EDGE,{"blendedFrom":[makeQuery(id+"F9.opExtrude","CAP_EDGE",EDGE,{"disambiguationData":[OSD([subQ15])],"isStart":false}),makeQuery(id+"F9.opExtrude","CAP_FACE",FACE,{"disambiguationData":[OSD([subQ17,subQ16,subQ15,subQ14,subQ13,subQ12,subQ11,subQ10,subQ9,subQ8,subQ7,subQ6,subQ5,subQ4,subQ3,subQ2,subQ1,subQ0])],"isStart":false})],"blendedInto":[makeQuery(id+"F9.opExtrude","CAP_FACE",FACE,{"disambiguationData":[OSD([subQ17,subQ16,subQ15,subQ14,subQ13,subQ12,subQ11,subQ10,subQ9,subQ8,subQ7,subQ6,subQ5,subQ4,subQ3,subQ2,subQ1,subQ0])],"isStart":false})]})])],"isStart":false});}
            chamfer(context, id + "F13", {"entities" : qUnion([Q0, Q1, Q2, Q3, Q4, Q5]), "width" : 5.08 * mm, "tangentPropagation" : true});
        }
        {
            var Q0;
            Q0=makeQuery(id+"F12.opExtrude","CAP_FACE",FACE,{"disambiguationData":[OSD([sQuery(id+"F0.wireOp",EDGE,"E0.0"),sQuery(id+"F0.wireOp",EDGE,"E0.1"),sQuery(id+"F0.wireOp",EDGE,"E0.2"),sQuery(id+"F0.wireOp",EDGE,"E0.3"),sQuery(id+"F0.wireOp",EDGE,"E0.4"),sQuery(id+"F0.wireOp",EDGE,"E0.5"),sQuery(id+"F0.wireOp",EDGE,"E1.1"),sQuery(id+"F0.wireOp",EDGE,"E1.2"),sQuery(id+"F0.wireOp",EDGE,"E1.3"),sQuery(id+"F0.wireOp",EDGE,"E1.4"),sQuery(id+"F0.wireOp",EDGE,"E2.2"),sQuery(id+"F0.wireOp",EDGE,"E2.3"),sQuery(id+"F0.wireOp",EDGE,"E2.4"),sQuery(id+"F0.wireOp",EDGE,"E2.5"),sQuery(id+"F0.wireOp",EDGE,"E3.1"),sQuery(id+"F0.wireOp",EDGE,"E3.2"),sQuery(id+"F0.wireOp",EDGE,"E3.3"),sQuery(id+"F0.wireOp",EDGE,"E3.4")])],"isStart":false});
            extrude(context, id + "F14", {"entities" : qUnion([Q0]), "operationType" : NewBodyOperationType.ADD, "depth" : 25.4 * mm});
        }
        {
            var Q0;
            {var subQ0=sQuery(id+"F0.wireOp",EDGE,"E3.4");var subQ1=sQuery(id+"F0.wireOp",EDGE,"E3.3");var subQ2=sQuery(id+"F0.wireOp",EDGE,"E3.2");var subQ3=sQuery(id+"F0.wireOp",EDGE,"E3.1");var subQ4=sQuery(id+"F0.wireOp",EDGE,"E2.5");var subQ5=sQuery(id+"F0.wireOp",EDGE,"E2.4");var subQ6=sQuery(id+"F0.wireOp",EDGE,"E2.3");var subQ7=sQuery(id+"F0.wireOp",EDGE,"E2.2");var subQ8=sQuery(id+"F0.wireOp",EDGE,"E1.4");var subQ9=sQuery(id+"F0.wireOp",EDGE,"E1.3");var subQ10=sQuery(id+"F0.wireOp",EDGE,"E1.2");var subQ11=sQuery(id+"F0.wireOp",EDGE,"E1.1");var subQ12=sQuery(id+"F0.wireOp",EDGE,"E0.5");var subQ13=sQuery(id+"F0.wireOp",EDGE,"E0.4");var subQ14=sQuery(id+"F0.wireOp",EDGE,"E0.3");var subQ15=sQuery(id+"F0.wireOp",EDGE,"E0.2");var subQ16=sQuery(id+"F0.wireOp",EDGE,"E0.1");var subQ17=sQuery(id+"F0.wireOp",EDGE,"E0.0");Q0=makeQuery(id+"F14.opExtrude","CAP_EDGE",EDGE,{"disambiguationData":[OSD([subQ17,subQ16,subQ15,subQ14,subQ13,subQ12,subQ11,subQ10,subQ9,subQ8,subQ7,subQ6,subQ5,subQ4,subQ3,subQ2,subQ1,subQ0]),TDD([makeQuery(id+"F13.opChamfer","BLEND_EDGE",EDGE,{"blendedFrom":[makeQuery(id+"F12.opExtrude","CAP_EDGE",EDGE,{"disambiguationData":[OSD([subQ17,subQ16,subQ15,subQ14,subQ13,subQ12,subQ11,subQ10,subQ9,subQ8,subQ7,subQ6,subQ5,subQ4,subQ3,subQ2,subQ1,subQ0]),TDD([makeQuery(id+"F11.opChamfer","BLEND_EDGE",EDGE,{"blendedFrom":[makeQuery(id+"F9.opExtrude","CAP_EDGE",EDGE,{"disambiguationData":[OSD([subQ13])],"isStart":false}),makeQuery(id+"F9.opExtrude","CAP_FACE",FACE,{"disambiguationData":[OSD([subQ17,subQ16,subQ15,subQ14,subQ13,subQ12,subQ11,subQ10,subQ9,subQ8,subQ7,subQ6,subQ5,subQ4,subQ3,subQ2,subQ1,subQ0])],"isStart":false})],"blendedInto":[makeQuery(id+"F9.opExtrude","CAP_FACE",FACE,{"disambiguationData":[OSD([subQ17,subQ16,subQ15,subQ14,subQ13,subQ12,subQ11,subQ10,subQ9,subQ8,subQ7,subQ6,subQ5,subQ4,subQ3,subQ2,subQ1,subQ0])],"isStart":false})]})])],"isStart":false}),makeQuery(id+"F12.opExtrude","CAP_FACE",FACE,{"disambiguationData":[OSD([subQ17,subQ16,subQ15,subQ14,subQ13,subQ12,subQ11,subQ10,subQ9,subQ8,subQ7,subQ6,subQ5,subQ4,subQ3,subQ2,subQ1,subQ0])],"isStart":false})],"blendedInto":[makeQuery(id+"F12.opExtrude","CAP_FACE",FACE,{"disambiguationData":[OSD([subQ17,subQ16,subQ15,subQ14,subQ13,subQ12,subQ11,subQ10,subQ9,subQ8,subQ7,subQ6,subQ5,subQ4,subQ3,subQ2,subQ1,subQ0])],"isStart":false})]})])],"isStart":false});}
            var Q1;
            {var subQ0=sQuery(id+"F0.wireOp",EDGE,"E3.4");var subQ1=sQuery(id+"F0.wireOp",EDGE,"E3.3");var subQ2=sQuery(id+"F0.wireOp",EDGE,"E3.2");var subQ3=sQuery(id+"F0.wireOp",EDGE,"E3.1");var subQ4=sQuery(id+"F0.wireOp",EDGE,"E2.5");var subQ5=sQuery(id+"F0.wireOp",EDGE,"E2.4");var subQ6=sQuery(id+"F0.wireOp",EDGE,"E2.3");var subQ7=sQuery(id+"F0.wireOp",EDGE,"E2.2");var subQ8=sQuery(id+"F0.wireOp",EDGE,"E1.4");var subQ9=sQuery(id+"F0.wireOp",EDGE,"E1.3");var subQ10=sQuery(id+"F0.wireOp",EDGE,"E1.2");var subQ11=sQuery(id+"F0.wireOp",EDGE,"E1.1");var subQ12=sQuery(id+"F0.wireOp",EDGE,"E0.5");var subQ13=sQuery(id+"F0.wireOp",EDGE,"E0.4");var subQ14=sQuery(id+"F0.wireOp",EDGE,"E0.3");var subQ15=sQuery(id+"F0.wireOp",EDGE,"E0.2");var subQ16=sQuery(id+"F0.wireOp",EDGE,"E0.1");var subQ17=sQuery(id+"F0.wireOp",EDGE,"E0.0");Q1=makeQuery(id+"F14.opExtrude","CAP_EDGE",EDGE,{"disambiguationData":[OSD([subQ17,subQ16,subQ15,subQ14,subQ13,subQ12,subQ11,subQ10,subQ9,subQ8,subQ7,subQ6,subQ5,subQ4,subQ3,subQ2,subQ1,subQ0]),TDD([makeQuery(id+"F13.opChamfer","BLEND_EDGE",EDGE,{"blendedFrom":[makeQuery(id+"F12.opExtrude","CAP_EDGE",EDGE,{"disambiguationData":[OSD([subQ17,subQ16,subQ15,subQ14,subQ13,subQ12,subQ11,subQ10,subQ9,subQ8,subQ7,subQ6,subQ5,subQ4,subQ3,subQ2,subQ1,subQ0]),TDD([makeQuery(id+"F11.opChamfer","BLEND_EDGE",EDGE,{"blendedFrom":[makeQuery(id+"F9.opExtrude","CAP_EDGE",EDGE,{"disambiguationData":[OSD([subQ12])],"isStart":false}),makeQuery(id+"F9.opExtrude","CAP_FACE",FACE,{"disambiguationData":[OSD([subQ17,subQ16,subQ15,subQ14,subQ13,subQ12,subQ11,subQ10,subQ9,subQ8,subQ7,subQ6,subQ5,subQ4,subQ3,subQ2,subQ1,subQ0])],"isStart":false})],"blendedInto":[makeQuery(id+"F9.opExtrude","CAP_FACE",FACE,{"disambiguationData":[OSD([subQ17,subQ16,subQ15,subQ14,subQ13,subQ12,subQ11,subQ10,subQ9,subQ8,subQ7,subQ6,subQ5,subQ4,subQ3,subQ2,subQ1,subQ0])],"isStart":false})]})])],"isStart":false}),makeQuery(id+"F12.opExtrude","CAP_FACE",FACE,{"disambiguationData":[OSD([subQ17,subQ16,subQ15,subQ14,subQ13,subQ12,subQ11,subQ10,subQ9,subQ8,subQ7,subQ6,subQ5,subQ4,subQ3,subQ2,subQ1,subQ0])],"isStart":false})],"blendedInto":[makeQuery(id+"F12.opExtrude","CAP_FACE",FACE,{"disambiguationData":[OSD([subQ17,subQ16,subQ15,subQ14,subQ13,subQ12,subQ11,subQ10,subQ9,subQ8,subQ7,subQ6,subQ5,subQ4,subQ3,subQ2,subQ1,subQ0])],"isStart":false})]})])],"isStart":false});}
            var Q2;
            {var subQ0=sQuery(id+"F0.wireOp",EDGE,"E3.4");var subQ1=sQuery(id+"F0.wireOp",EDGE,"E3.3");var subQ2=sQuery(id+"F0.wireOp",EDGE,"E3.2");var subQ3=sQuery(id+"F0.wireOp",EDGE,"E3.1");var subQ4=sQuery(id+"F0.wireOp",EDGE,"E2.5");var subQ5=sQuery(id+"F0.wireOp",EDGE,"E2.4");var subQ6=sQuery(id+"F0.wireOp",EDGE,"E2.3");var subQ7=sQuery(id+"F0.wireOp",EDGE,"E2.2");var subQ8=sQuery(id+"F0.wireOp",EDGE,"E1.4");var subQ9=sQuery(id+"F0.wireOp",EDGE,"E1.3");var subQ10=sQuery(id+"F0.wireOp",EDGE,"E1.2");var subQ11=sQuery(id+"F0.wireOp",EDGE,"E1.1");var subQ12=sQuery(id+"F0.wireOp",EDGE,"E0.5");var subQ13=sQuery(id+"F0.wireOp",EDGE,"E0.4");var subQ14=sQuery(id+"F0.wireOp",EDGE,"E0.3");var subQ15=sQuery(id+"F0.wireOp",EDGE,"E0.2");var subQ16=sQuery(id+"F0.wireOp",EDGE,"E0.1");var subQ17=sQuery(id+"F0.wireOp",EDGE,"E0.0");Q2=makeQuery(id+"F14.opExtrude","CAP_EDGE",EDGE,{"disambiguationData":[OSD([subQ17,subQ16,subQ15,subQ14,subQ13,subQ12,subQ11,subQ10,subQ9,subQ8,subQ7,subQ6,subQ5,subQ4,subQ3,subQ2,subQ1,subQ0]),TDD([makeQuery(id+"F13.opChamfer","BLEND_EDGE",EDGE,{"blendedFrom":[makeQuery(id+"F12.opExtrude","CAP_EDGE",EDGE,{"disambiguationData":[OSD([subQ17,subQ16,subQ15,subQ14,subQ13,subQ12,subQ11,subQ10,subQ9,subQ8,subQ7,subQ6,subQ5,subQ4,subQ3,subQ2,subQ1,subQ0]),TDD([makeQuery(id+"F11.opChamfer","BLEND_EDGE",EDGE,{"blendedFrom":[makeQuery(id+"F9.opExtrude","CAP_EDGE",EDGE,{"disambiguationData":[OSD([subQ16])],"isStart":false}),makeQuery(id+"F9.opExtrude","CAP_FACE",FACE,{"disambiguationData":[OSD([subQ17,subQ16,subQ15,subQ14,subQ13,subQ12,subQ11,subQ10,subQ9,subQ8,subQ7,subQ6,subQ5,subQ4,subQ3,subQ2,subQ1,subQ0])],"isStart":false})],"blendedInto":[makeQuery(id+"F9.opExtrude","CAP_FACE",FACE,{"disambiguationData":[OSD([subQ17,subQ16,subQ15,subQ14,subQ13,subQ12,subQ11,subQ10,subQ9,subQ8,subQ7,subQ6,subQ5,subQ4,subQ3,subQ2,subQ1,subQ0])],"isStart":false})]})])],"isStart":false}),makeQuery(id+"F12.opExtrude","CAP_FACE",FACE,{"disambiguationData":[OSD([subQ17,subQ16,subQ15,subQ14,subQ13,subQ12,subQ11,subQ10,subQ9,subQ8,subQ7,subQ6,subQ5,subQ4,subQ3,subQ2,subQ1,subQ0])],"isStart":false})],"blendedInto":[makeQuery(id+"F12.opExtrude","CAP_FACE",FACE,{"disambiguationData":[OSD([subQ17,subQ16,subQ15,subQ14,subQ13,subQ12,subQ11,subQ10,subQ9,subQ8,subQ7,subQ6,subQ5,subQ4,subQ3,subQ2,subQ1,subQ0])],"isStart":false})]})])],"isStart":false});}
            var Q3;
            {var subQ0=sQuery(id+"F0.wireOp",EDGE,"E3.4");var subQ1=sQuery(id+"F0.wireOp",EDGE,"E3.3");var subQ2=sQuery(id+"F0.wireOp",EDGE,"E3.2");var subQ3=sQuery(id+"F0.wireOp",EDGE,"E3.1");var subQ4=sQuery(id+"F0.wireOp",EDGE,"E2.5");var subQ5=sQuery(id+"F0.wireOp",EDGE,"E2.4");var subQ6=sQuery(id+"F0.wireOp",EDGE,"E2.3");var subQ7=sQuery(id+"F0.wireOp",EDGE,"E2.2");var subQ8=sQuery(id+"F0.wireOp",EDGE,"E1.4");var subQ9=sQuery(id+"F0.wireOp",EDGE,"E1.3");var subQ10=sQuery(id+"F0.wireOp",EDGE,"E1.2");var subQ11=sQuery(id+"F0.wireOp",EDGE,"E1.1");var subQ12=sQuery(id+"F0.wireOp",EDGE,"E0.5");var subQ13=sQuery(id+"F0.wireOp",EDGE,"E0.4");var subQ14=sQuery(id+"F0.wireOp",EDGE,"E0.3");var subQ15=sQuery(id+"F0.wireOp",EDGE,"E0.2");var subQ16=sQuery(id+"F0.wireOp",EDGE,"E0.1");var subQ17=sQuery(id+"F0.wireOp",EDGE,"E0.0");Q3=makeQuery(id+"F14.opExtrude","CAP_EDGE",EDGE,{"disambiguationData":[OSD([subQ17,subQ16,subQ15,subQ14,subQ13,subQ12,subQ11,subQ10,subQ9,subQ8,subQ7,subQ6,subQ5,subQ4,subQ3,subQ2,subQ1,subQ0]),TDD([makeQuery(id+"F13.opChamfer","BLEND_EDGE",EDGE,{"blendedFrom":[makeQuery(id+"F12.opExtrude","CAP_EDGE",EDGE,{"disambiguationData":[OSD([subQ17,subQ16,subQ15,subQ14,subQ13,subQ12,subQ11,subQ10,subQ9,subQ8,subQ7,subQ6,subQ5,subQ4,subQ3,subQ2,subQ1,subQ0]),TDD([makeQuery(id+"F11.opChamfer","BLEND_EDGE",EDGE,{"blendedFrom":[makeQuery(id+"F9.opExtrude","CAP_EDGE",EDGE,{"disambiguationData":[OSD([subQ17])],"isStart":false}),makeQuery(id+"F9.opExtrude","CAP_FACE",FACE,{"disambiguationData":[OSD([subQ17,subQ16,subQ15,subQ14,subQ13,subQ12,subQ11,subQ10,subQ9,subQ8,subQ7,subQ6,subQ5,subQ4,subQ3,subQ2,subQ1,subQ0])],"isStart":false})],"blendedInto":[makeQuery(id+"F9.opExtrude","CAP_FACE",FACE,{"disambiguationData":[OSD([subQ17,subQ16,subQ15,subQ14,subQ13,subQ12,subQ11,subQ10,subQ9,subQ8,subQ7,subQ6,subQ5,subQ4,subQ3,subQ2,subQ1,subQ0])],"isStart":false})]})])],"isStart":false}),makeQuery(id+"F12.opExtrude","CAP_FACE",FACE,{"disambiguationData":[OSD([subQ17,subQ16,subQ15,subQ14,subQ13,subQ12,subQ11,subQ10,subQ9,subQ8,subQ7,subQ6,subQ5,subQ4,subQ3,subQ2,subQ1,subQ0])],"isStart":false})],"blendedInto":[makeQuery(id+"F12.opExtrude","CAP_FACE",FACE,{"disambiguationData":[OSD([subQ17,subQ16,subQ15,subQ14,subQ13,subQ12,subQ11,subQ10,subQ9,subQ8,subQ7,subQ6,subQ5,subQ4,subQ3,subQ2,subQ1,subQ0])],"isStart":false})]})])],"isStart":false});}
            var Q4;
            {var subQ0=sQuery(id+"F0.wireOp",EDGE,"E3.4");var subQ1=sQuery(id+"F0.wireOp",EDGE,"E3.3");var subQ2=sQuery(id+"F0.wireOp",EDGE,"E3.2");var subQ3=sQuery(id+"F0.wireOp",EDGE,"E3.1");var subQ4=sQuery(id+"F0.wireOp",EDGE,"E2.5");var subQ5=sQuery(id+"F0.wireOp",EDGE,"E2.4");var subQ6=sQuery(id+"F0.wireOp",EDGE,"E2.3");var subQ7=sQuery(id+"F0.wireOp",EDGE,"E2.2");var subQ8=sQuery(id+"F0.wireOp",EDGE,"E1.4");var subQ9=sQuery(id+"F0.wireOp",EDGE,"E1.3");var subQ10=sQuery(id+"F0.wireOp",EDGE,"E1.2");var subQ11=sQuery(id+"F0.wireOp",EDGE,"E1.1");var subQ12=sQuery(id+"F0.wireOp",EDGE,"E0.5");var subQ13=sQuery(id+"F0.wireOp",EDGE,"E0.4");var subQ14=sQuery(id+"F0.wireOp",EDGE,"E0.3");var subQ15=sQuery(id+"F0.wireOp",EDGE,"E0.2");var subQ16=sQuery(id+"F0.wireOp",EDGE,"E0.1");var subQ17=sQuery(id+"F0.wireOp",EDGE,"E0.0");Q4=makeQuery(id+"F14.opExtrude","CAP_EDGE",EDGE,{"disambiguationData":[OSD([subQ17,subQ16,subQ15,subQ14,subQ13,subQ12,subQ11,subQ10,subQ9,subQ8,subQ7,subQ6,subQ5,subQ4,subQ3,subQ2,subQ1,subQ0]),TDD([makeQuery(id+"F13.opChamfer","BLEND_EDGE",EDGE,{"blendedFrom":[makeQuery(id+"F12.opExtrude","CAP_EDGE",EDGE,{"disambiguationData":[OSD([subQ17,subQ16,subQ15,subQ14,subQ13,subQ12,subQ11,subQ10,subQ9,subQ8,subQ7,subQ6,subQ5,subQ4,subQ3,subQ2,subQ1,subQ0]),TDD([makeQuery(id+"F11.opChamfer","BLEND_EDGE",EDGE,{"blendedFrom":[makeQuery(id+"F9.opExtrude","CAP_EDGE",EDGE,{"disambiguationData":[OSD([subQ15])],"isStart":false}),makeQuery(id+"F9.opExtrude","CAP_FACE",FACE,{"disambiguationData":[OSD([subQ17,subQ16,subQ15,subQ14,subQ13,subQ12,subQ11,subQ10,subQ9,subQ8,subQ7,subQ6,subQ5,subQ4,subQ3,subQ2,subQ1,subQ0])],"isStart":false})],"blendedInto":[makeQuery(id+"F9.opExtrude","CAP_FACE",FACE,{"disambiguationData":[OSD([subQ17,subQ16,subQ15,subQ14,subQ13,subQ12,subQ11,subQ10,subQ9,subQ8,subQ7,subQ6,subQ5,subQ4,subQ3,subQ2,subQ1,subQ0])],"isStart":false})]})])],"isStart":false}),makeQuery(id+"F12.opExtrude","CAP_FACE",FACE,{"disambiguationData":[OSD([subQ17,subQ16,subQ15,subQ14,subQ13,subQ12,subQ11,subQ10,subQ9,subQ8,subQ7,subQ6,subQ5,subQ4,subQ3,subQ2,subQ1,subQ0])],"isStart":false})],"blendedInto":[makeQuery(id+"F12.opExtrude","CAP_FACE",FACE,{"disambiguationData":[OSD([subQ17,subQ16,subQ15,subQ14,subQ13,subQ12,subQ11,subQ10,subQ9,subQ8,subQ7,subQ6,subQ5,subQ4,subQ3,subQ2,subQ1,subQ0])],"isStart":false})]})])],"isStart":false});}
            var Q5;
            {var subQ0=sQuery(id+"F0.wireOp",EDGE,"E3.4");var subQ1=sQuery(id+"F0.wireOp",EDGE,"E3.3");var subQ2=sQuery(id+"F0.wireOp",EDGE,"E3.2");var subQ3=sQuery(id+"F0.wireOp",EDGE,"E3.1");var subQ4=sQuery(id+"F0.wireOp",EDGE,"E2.5");var subQ5=sQuery(id+"F0.wireOp",EDGE,"E2.4");var subQ6=sQuery(id+"F0.wireOp",EDGE,"E2.3");var subQ7=sQuery(id+"F0.wireOp",EDGE,"E2.2");var subQ8=sQuery(id+"F0.wireOp",EDGE,"E1.4");var subQ9=sQuery(id+"F0.wireOp",EDGE,"E1.3");var subQ10=sQuery(id+"F0.wireOp",EDGE,"E1.2");var subQ11=sQuery(id+"F0.wireOp",EDGE,"E1.1");var subQ12=sQuery(id+"F0.wireOp",EDGE,"E0.5");var subQ13=sQuery(id+"F0.wireOp",EDGE,"E0.4");var subQ14=sQuery(id+"F0.wireOp",EDGE,"E0.3");var subQ15=sQuery(id+"F0.wireOp",EDGE,"E0.2");var subQ16=sQuery(id+"F0.wireOp",EDGE,"E0.1");var subQ17=sQuery(id+"F0.wireOp",EDGE,"E0.0");Q5=makeQuery(id+"F14.opExtrude","CAP_EDGE",EDGE,{"disambiguationData":[OSD([subQ17,subQ16,subQ15,subQ14,subQ13,subQ12,subQ11,subQ10,subQ9,subQ8,subQ7,subQ6,subQ5,subQ4,subQ3,subQ2,subQ1,subQ0]),TDD([makeQuery(id+"F13.opChamfer","BLEND_EDGE",EDGE,{"blendedFrom":[makeQuery(id+"F12.opExtrude","CAP_EDGE",EDGE,{"disambiguationData":[OSD([subQ17,subQ16,subQ15,subQ14,subQ13,subQ12,subQ11,subQ10,subQ9,subQ8,subQ7,subQ6,subQ5,subQ4,subQ3,subQ2,subQ1,subQ0]),TDD([makeQuery(id+"F11.opChamfer","BLEND_EDGE",EDGE,{"blendedFrom":[makeQuery(id+"F9.opExtrude","CAP_EDGE",EDGE,{"disambiguationData":[OSD([subQ14])],"isStart":false}),makeQuery(id+"F9.opExtrude","CAP_FACE",FACE,{"disambiguationData":[OSD([subQ17,subQ16,subQ15,subQ14,subQ13,subQ12,subQ11,subQ10,subQ9,subQ8,subQ7,subQ6,subQ5,subQ4,subQ3,subQ2,subQ1,subQ0])],"isStart":false})],"blendedInto":[makeQuery(id+"F9.opExtrude","CAP_FACE",FACE,{"disambiguationData":[OSD([subQ17,subQ16,subQ15,subQ14,subQ13,subQ12,subQ11,subQ10,subQ9,subQ8,subQ7,subQ6,subQ5,subQ4,subQ3,subQ2,subQ1,subQ0])],"isStart":false})]})])],"isStart":false}),makeQuery(id+"F12.opExtrude","CAP_FACE",FACE,{"disambiguationData":[OSD([subQ17,subQ16,subQ15,subQ14,subQ13,subQ12,subQ11,subQ10,subQ9,subQ8,subQ7,subQ6,subQ5,subQ4,subQ3,subQ2,subQ1,subQ0])],"isStart":false})],"blendedInto":[makeQuery(id+"F12.opExtrude","CAP_FACE",FACE,{"disambiguationData":[OSD([subQ17,subQ16,subQ15,subQ14,subQ13,subQ12,subQ11,subQ10,subQ9,subQ8,subQ7,subQ6,subQ5,subQ4,subQ3,subQ2,subQ1,subQ0])],"isStart":false})]})])],"isStart":false});}
            chamfer(context, id + "F15", {"entities" : qUnion([Q0, Q1, Q2, Q3, Q4, Q5]), "width" : 5.08 * mm, "tangentPropagation" : true});
        }
        {
            var Q0;
            Q0=makeQuery(id+"F14.opExtrude","CAP_FACE",FACE,{"disambiguationData":[OSD([sQuery(id+"F0.wireOp",EDGE,"E0.0"),sQuery(id+"F0.wireOp",EDGE,"E0.1"),sQuery(id+"F0.wireOp",EDGE,"E0.2"),sQuery(id+"F0.wireOp",EDGE,"E0.3"),sQuery(id+"F0.wireOp",EDGE,"E0.4"),sQuery(id+"F0.wireOp",EDGE,"E0.5"),sQuery(id+"F0.wireOp",EDGE,"E1.1"),sQuery(id+"F0.wireOp",EDGE,"E1.2"),sQuery(id+"F0.wireOp",EDGE,"E1.3"),sQuery(id+"F0.wireOp",EDGE,"E1.4"),sQuery(id+"F0.wireOp",EDGE,"E2.2"),sQuery(id+"F0.wireOp",EDGE,"E2.3"),sQuery(id+"F0.wireOp",EDGE,"E2.4"),sQuery(id+"F0.wireOp",EDGE,"E2.5"),sQuery(id+"F0.wireOp",EDGE,"E3.1"),sQuery(id+"F0.wireOp",EDGE,"E3.2"),sQuery(id+"F0.wireOp",EDGE,"E3.3"),sQuery(id+"F0.wireOp",EDGE,"E3.4")])],"isStart":false});
            extrude(context, id + "F16", {"entities" : qUnion([Q0]), "operationType" : NewBodyOperationType.ADD, "depth" : 25.4 * mm});
        }
        {
            var Q0;
            {var subQ0=sQuery(id+"F0.wireOp",EDGE,"E3.4");var subQ1=sQuery(id+"F0.wireOp",EDGE,"E3.3");var subQ2=sQuery(id+"F0.wireOp",EDGE,"E3.2");var subQ3=sQuery(id+"F0.wireOp",EDGE,"E3.1");var subQ4=sQuery(id+"F0.wireOp",EDGE,"E2.5");var subQ5=sQuery(id+"F0.wireOp",EDGE,"E2.4");var subQ6=sQuery(id+"F0.wireOp",EDGE,"E2.3");var subQ7=sQuery(id+"F0.wireOp",EDGE,"E2.2");var subQ8=sQuery(id+"F0.wireOp",EDGE,"E1.4");var subQ9=sQuery(id+"F0.wireOp",EDGE,"E1.3");var subQ10=sQuery(id+"F0.wireOp",EDGE,"E1.2");var subQ11=sQuery(id+"F0.wireOp",EDGE,"E1.1");var subQ12=sQuery(id+"F0.wireOp",EDGE,"E0.5");var subQ13=sQuery(id+"F0.wireOp",EDGE,"E0.4");var subQ14=sQuery(id+"F0.wireOp",EDGE,"E0.3");var subQ15=sQuery(id+"F0.wireOp",EDGE,"E0.2");var subQ16=sQuery(id+"F0.wireOp",EDGE,"E0.1");var subQ17=sQuery(id+"F0.wireOp",EDGE,"E0.0");Q0=makeQuery(id+"F16.opExtrude","CAP_EDGE",EDGE,{"disambiguationData":[OSD([subQ17,subQ16,subQ15,subQ14,subQ13,subQ12,subQ11,subQ10,subQ9,subQ8,subQ7,subQ6,subQ5,subQ4,subQ3,subQ2,subQ1,subQ0]),TDD([makeQuery(id+"F15.opChamfer","BLEND_EDGE",EDGE,{"blendedFrom":[makeQuery(id+"F14.opExtrude","CAP_EDGE",EDGE,{"disambiguationData":[OSD([subQ17,subQ16,subQ15,subQ14,subQ13,subQ12,subQ11,subQ10,subQ9,subQ8,subQ7,subQ6,subQ5,subQ4,subQ3,subQ2,subQ1,subQ0]),TDD([makeQuery(id+"F13.opChamfer","BLEND_EDGE",EDGE,{"blendedFrom":[makeQuery(id+"F12.opExtrude","CAP_EDGE",EDGE,{"disambiguationData":[OSD([subQ17,subQ16,subQ15,subQ14,subQ13,subQ12,subQ11,subQ10,subQ9,subQ8,subQ7,subQ6,subQ5,subQ4,subQ3,subQ2,subQ1,subQ0]),TDD([makeQuery(id+"F11.opChamfer","BLEND_EDGE",EDGE,{"blendedFrom":[makeQuery(id+"F9.opExtrude","CAP_EDGE",EDGE,{"disambiguationData":[OSD([subQ13])],"isStart":false}),makeQuery(id+"F9.opExtrude","CAP_FACE",FACE,{"disambiguationData":[OSD([subQ17,subQ16,subQ15,subQ14,subQ13,subQ12,subQ11,subQ10,subQ9,subQ8,subQ7,subQ6,subQ5,subQ4,subQ3,subQ2,subQ1,subQ0])],"isStart":false})],"blendedInto":[makeQuery(id+"F9.opExtrude","CAP_FACE",FACE,{"disambiguationData":[OSD([subQ17,subQ16,subQ15,subQ14,subQ13,subQ12,subQ11,subQ10,subQ9,subQ8,subQ7,subQ6,subQ5,subQ4,subQ3,subQ2,subQ1,subQ0])],"isStart":false})]})])],"isStart":false}),makeQuery(id+"F12.opExtrude","CAP_FACE",FACE,{"disambiguationData":[OSD([subQ17,subQ16,subQ15,subQ14,subQ13,subQ12,subQ11,subQ10,subQ9,subQ8,subQ7,subQ6,subQ5,subQ4,subQ3,subQ2,subQ1,subQ0])],"isStart":false})],"blendedInto":[makeQuery(id+"F12.opExtrude","CAP_FACE",FACE,{"disambiguationData":[OSD([subQ17,subQ16,subQ15,subQ14,subQ13,subQ12,subQ11,subQ10,subQ9,subQ8,subQ7,subQ6,subQ5,subQ4,subQ3,subQ2,subQ1,subQ0])],"isStart":false})]})])],"isStart":false}),makeQuery(id+"F14.opExtrude","CAP_FACE",FACE,{"disambiguationData":[OSD([subQ17,subQ16,subQ15,subQ14,subQ13,subQ12,subQ11,subQ10,subQ9,subQ8,subQ7,subQ6,subQ5,subQ4,subQ3,subQ2,subQ1,subQ0])],"isStart":false})],"blendedInto":[makeQuery(id+"F14.opExtrude","CAP_FACE",FACE,{"disambiguationData":[OSD([subQ17,subQ16,subQ15,subQ14,subQ13,subQ12,subQ11,subQ10,subQ9,subQ8,subQ7,subQ6,subQ5,subQ4,subQ3,subQ2,subQ1,subQ0])],"isStart":false})]})])],"isStart":false});}
            var Q1;
            {var subQ0=sQuery(id+"F0.wireOp",EDGE,"E3.4");var subQ1=sQuery(id+"F0.wireOp",EDGE,"E3.3");var subQ2=sQuery(id+"F0.wireOp",EDGE,"E3.2");var subQ3=sQuery(id+"F0.wireOp",EDGE,"E3.1");var subQ4=sQuery(id+"F0.wireOp",EDGE,"E2.5");var subQ5=sQuery(id+"F0.wireOp",EDGE,"E2.4");var subQ6=sQuery(id+"F0.wireOp",EDGE,"E2.3");var subQ7=sQuery(id+"F0.wireOp",EDGE,"E2.2");var subQ8=sQuery(id+"F0.wireOp",EDGE,"E1.4");var subQ9=sQuery(id+"F0.wireOp",EDGE,"E1.3");var subQ10=sQuery(id+"F0.wireOp",EDGE,"E1.2");var subQ11=sQuery(id+"F0.wireOp",EDGE,"E1.1");var subQ12=sQuery(id+"F0.wireOp",EDGE,"E0.5");var subQ13=sQuery(id+"F0.wireOp",EDGE,"E0.4");var subQ14=sQuery(id+"F0.wireOp",EDGE,"E0.3");var subQ15=sQuery(id+"F0.wireOp",EDGE,"E0.2");var subQ16=sQuery(id+"F0.wireOp",EDGE,"E0.1");var subQ17=sQuery(id+"F0.wireOp",EDGE,"E0.0");Q1=makeQuery(id+"F16.opExtrude","CAP_EDGE",EDGE,{"disambiguationData":[OSD([subQ17,subQ16,subQ15,subQ14,subQ13,subQ12,subQ11,subQ10,subQ9,subQ8,subQ7,subQ6,subQ5,subQ4,subQ3,subQ2,subQ1,subQ0]),TDD([makeQuery(id+"F15.opChamfer","BLEND_EDGE",EDGE,{"blendedFrom":[makeQuery(id+"F14.opExtrude","CAP_EDGE",EDGE,{"disambiguationData":[OSD([subQ17,subQ16,subQ15,subQ14,subQ13,subQ12,subQ11,subQ10,subQ9,subQ8,subQ7,subQ6,subQ5,subQ4,subQ3,subQ2,subQ1,subQ0]),TDD([makeQuery(id+"F13.opChamfer","BLEND_EDGE",EDGE,{"blendedFrom":[makeQuery(id+"F12.opExtrude","CAP_EDGE",EDGE,{"disambiguationData":[OSD([subQ17,subQ16,subQ15,subQ14,subQ13,subQ12,subQ11,subQ10,subQ9,subQ8,subQ7,subQ6,subQ5,subQ4,subQ3,subQ2,subQ1,subQ0]),TDD([makeQuery(id+"F11.opChamfer","BLEND_EDGE",EDGE,{"blendedFrom":[makeQuery(id+"F9.opExtrude","CAP_EDGE",EDGE,{"disambiguationData":[OSD([subQ12])],"isStart":false}),makeQuery(id+"F9.opExtrude","CAP_FACE",FACE,{"disambiguationData":[OSD([subQ17,subQ16,subQ15,subQ14,subQ13,subQ12,subQ11,subQ10,subQ9,subQ8,subQ7,subQ6,subQ5,subQ4,subQ3,subQ2,subQ1,subQ0])],"isStart":false})],"blendedInto":[makeQuery(id+"F9.opExtrude","CAP_FACE",FACE,{"disambiguationData":[OSD([subQ17,subQ16,subQ15,subQ14,subQ13,subQ12,subQ11,subQ10,subQ9,subQ8,subQ7,subQ6,subQ5,subQ4,subQ3,subQ2,subQ1,subQ0])],"isStart":false})]})])],"isStart":false}),makeQuery(id+"F12.opExtrude","CAP_FACE",FACE,{"disambiguationData":[OSD([subQ17,subQ16,subQ15,subQ14,subQ13,subQ12,subQ11,subQ10,subQ9,subQ8,subQ7,subQ6,subQ5,subQ4,subQ3,subQ2,subQ1,subQ0])],"isStart":false})],"blendedInto":[makeQuery(id+"F12.opExtrude","CAP_FACE",FACE,{"disambiguationData":[OSD([subQ17,subQ16,subQ15,subQ14,subQ13,subQ12,subQ11,subQ10,subQ9,subQ8,subQ7,subQ6,subQ5,subQ4,subQ3,subQ2,subQ1,subQ0])],"isStart":false})]})])],"isStart":false}),makeQuery(id+"F14.opExtrude","CAP_FACE",FACE,{"disambiguationData":[OSD([subQ17,subQ16,subQ15,subQ14,subQ13,subQ12,subQ11,subQ10,subQ9,subQ8,subQ7,subQ6,subQ5,subQ4,subQ3,subQ2,subQ1,subQ0])],"isStart":false})],"blendedInto":[makeQuery(id+"F14.opExtrude","CAP_FACE",FACE,{"disambiguationData":[OSD([subQ17,subQ16,subQ15,subQ14,subQ13,subQ12,subQ11,subQ10,subQ9,subQ8,subQ7,subQ6,subQ5,subQ4,subQ3,subQ2,subQ1,subQ0])],"isStart":false})]})])],"isStart":false});}
            var Q2;
            {var subQ0=sQuery(id+"F0.wireOp",EDGE,"E3.4");var subQ1=sQuery(id+"F0.wireOp",EDGE,"E3.3");var subQ2=sQuery(id+"F0.wireOp",EDGE,"E3.2");var subQ3=sQuery(id+"F0.wireOp",EDGE,"E3.1");var subQ4=sQuery(id+"F0.wireOp",EDGE,"E2.5");var subQ5=sQuery(id+"F0.wireOp",EDGE,"E2.4");var subQ6=sQuery(id+"F0.wireOp",EDGE,"E2.3");var subQ7=sQuery(id+"F0.wireOp",EDGE,"E2.2");var subQ8=sQuery(id+"F0.wireOp",EDGE,"E1.4");var subQ9=sQuery(id+"F0.wireOp",EDGE,"E1.3");var subQ10=sQuery(id+"F0.wireOp",EDGE,"E1.2");var subQ11=sQuery(id+"F0.wireOp",EDGE,"E1.1");var subQ12=sQuery(id+"F0.wireOp",EDGE,"E0.5");var subQ13=sQuery(id+"F0.wireOp",EDGE,"E0.4");var subQ14=sQuery(id+"F0.wireOp",EDGE,"E0.3");var subQ15=sQuery(id+"F0.wireOp",EDGE,"E0.2");var subQ16=sQuery(id+"F0.wireOp",EDGE,"E0.1");var subQ17=sQuery(id+"F0.wireOp",EDGE,"E0.0");Q2=makeQuery(id+"F16.opExtrude","CAP_EDGE",EDGE,{"disambiguationData":[OSD([subQ17,subQ16,subQ15,subQ14,subQ13,subQ12,subQ11,subQ10,subQ9,subQ8,subQ7,subQ6,subQ5,subQ4,subQ3,subQ2,subQ1,subQ0]),TDD([makeQuery(id+"F15.opChamfer","BLEND_EDGE",EDGE,{"blendedFrom":[makeQuery(id+"F14.opExtrude","CAP_EDGE",EDGE,{"disambiguationData":[OSD([subQ17,subQ16,subQ15,subQ14,subQ13,subQ12,subQ11,subQ10,subQ9,subQ8,subQ7,subQ6,subQ5,subQ4,subQ3,subQ2,subQ1,subQ0]),TDD([makeQuery(id+"F13.opChamfer","BLEND_EDGE",EDGE,{"blendedFrom":[makeQuery(id+"F12.opExtrude","CAP_EDGE",EDGE,{"disambiguationData":[OSD([subQ17,subQ16,subQ15,subQ14,subQ13,subQ12,subQ11,subQ10,subQ9,subQ8,subQ7,subQ6,subQ5,subQ4,subQ3,subQ2,subQ1,subQ0]),TDD([makeQuery(id+"F11.opChamfer","BLEND_EDGE",EDGE,{"blendedFrom":[makeQuery(id+"F9.opExtrude","CAP_EDGE",EDGE,{"disambiguationData":[OSD([subQ17])],"isStart":false}),makeQuery(id+"F9.opExtrude","CAP_FACE",FACE,{"disambiguationData":[OSD([subQ17,subQ16,subQ15,subQ14,subQ13,subQ12,subQ11,subQ10,subQ9,subQ8,subQ7,subQ6,subQ5,subQ4,subQ3,subQ2,subQ1,subQ0])],"isStart":false})],"blendedInto":[makeQuery(id+"F9.opExtrude","CAP_FACE",FACE,{"disambiguationData":[OSD([subQ17,subQ16,subQ15,subQ14,subQ13,subQ12,subQ11,subQ10,subQ9,subQ8,subQ7,subQ6,subQ5,subQ4,subQ3,subQ2,subQ1,subQ0])],"isStart":false})]})])],"isStart":false}),makeQuery(id+"F12.opExtrude","CAP_FACE",FACE,{"disambiguationData":[OSD([subQ17,subQ16,subQ15,subQ14,subQ13,subQ12,subQ11,subQ10,subQ9,subQ8,subQ7,subQ6,subQ5,subQ4,subQ3,subQ2,subQ1,subQ0])],"isStart":false})],"blendedInto":[makeQuery(id+"F12.opExtrude","CAP_FACE",FACE,{"disambiguationData":[OSD([subQ17,subQ16,subQ15,subQ14,subQ13,subQ12,subQ11,subQ10,subQ9,subQ8,subQ7,subQ6,subQ5,subQ4,subQ3,subQ2,subQ1,subQ0])],"isStart":false})]})])],"isStart":false}),makeQuery(id+"F14.opExtrude","CAP_FACE",FACE,{"disambiguationData":[OSD([subQ17,subQ16,subQ15,subQ14,subQ13,subQ12,subQ11,subQ10,subQ9,subQ8,subQ7,subQ6,subQ5,subQ4,subQ3,subQ2,subQ1,subQ0])],"isStart":false})],"blendedInto":[makeQuery(id+"F14.opExtrude","CAP_FACE",FACE,{"disambiguationData":[OSD([subQ17,subQ16,subQ15,subQ14,subQ13,subQ12,subQ11,subQ10,subQ9,subQ8,subQ7,subQ6,subQ5,subQ4,subQ3,subQ2,subQ1,subQ0])],"isStart":false})]})])],"isStart":false});}
            var Q3;
            {var subQ0=sQuery(id+"F0.wireOp",EDGE,"E3.4");var subQ1=sQuery(id+"F0.wireOp",EDGE,"E3.3");var subQ2=sQuery(id+"F0.wireOp",EDGE,"E3.2");var subQ3=sQuery(id+"F0.wireOp",EDGE,"E3.1");var subQ4=sQuery(id+"F0.wireOp",EDGE,"E2.5");var subQ5=sQuery(id+"F0.wireOp",EDGE,"E2.4");var subQ6=sQuery(id+"F0.wireOp",EDGE,"E2.3");var subQ7=sQuery(id+"F0.wireOp",EDGE,"E2.2");var subQ8=sQuery(id+"F0.wireOp",EDGE,"E1.4");var subQ9=sQuery(id+"F0.wireOp",EDGE,"E1.3");var subQ10=sQuery(id+"F0.wireOp",EDGE,"E1.2");var subQ11=sQuery(id+"F0.wireOp",EDGE,"E1.1");var subQ12=sQuery(id+"F0.wireOp",EDGE,"E0.5");var subQ13=sQuery(id+"F0.wireOp",EDGE,"E0.4");var subQ14=sQuery(id+"F0.wireOp",EDGE,"E0.3");var subQ15=sQuery(id+"F0.wireOp",EDGE,"E0.2");var subQ16=sQuery(id+"F0.wireOp",EDGE,"E0.1");var subQ17=sQuery(id+"F0.wireOp",EDGE,"E0.0");Q3=makeQuery(id+"F16.opExtrude","CAP_EDGE",EDGE,{"disambiguationData":[OSD([subQ17,subQ16,subQ15,subQ14,subQ13,subQ12,subQ11,subQ10,subQ9,subQ8,subQ7,subQ6,subQ5,subQ4,subQ3,subQ2,subQ1,subQ0]),TDD([makeQuery(id+"F15.opChamfer","BLEND_EDGE",EDGE,{"blendedFrom":[makeQuery(id+"F14.opExtrude","CAP_EDGE",EDGE,{"disambiguationData":[OSD([subQ17,subQ16,subQ15,subQ14,subQ13,subQ12,subQ11,subQ10,subQ9,subQ8,subQ7,subQ6,subQ5,subQ4,subQ3,subQ2,subQ1,subQ0]),TDD([makeQuery(id+"F13.opChamfer","BLEND_EDGE",EDGE,{"blendedFrom":[makeQuery(id+"F12.opExtrude","CAP_EDGE",EDGE,{"disambiguationData":[OSD([subQ17,subQ16,subQ15,subQ14,subQ13,subQ12,subQ11,subQ10,subQ9,subQ8,subQ7,subQ6,subQ5,subQ4,subQ3,subQ2,subQ1,subQ0]),TDD([makeQuery(id+"F11.opChamfer","BLEND_EDGE",EDGE,{"blendedFrom":[makeQuery(id+"F9.opExtrude","CAP_EDGE",EDGE,{"disambiguationData":[OSD([subQ16])],"isStart":false}),makeQuery(id+"F9.opExtrude","CAP_FACE",FACE,{"disambiguationData":[OSD([subQ17,subQ16,subQ15,subQ14,subQ13,subQ12,subQ11,subQ10,subQ9,subQ8,subQ7,subQ6,subQ5,subQ4,subQ3,subQ2,subQ1,subQ0])],"isStart":false})],"blendedInto":[makeQuery(id+"F9.opExtrude","CAP_FACE",FACE,{"disambiguationData":[OSD([subQ17,subQ16,subQ15,subQ14,subQ13,subQ12,subQ11,subQ10,subQ9,subQ8,subQ7,subQ6,subQ5,subQ4,subQ3,subQ2,subQ1,subQ0])],"isStart":false})]})])],"isStart":false}),makeQuery(id+"F12.opExtrude","CAP_FACE",FACE,{"disambiguationData":[OSD([subQ17,subQ16,subQ15,subQ14,subQ13,subQ12,subQ11,subQ10,subQ9,subQ8,subQ7,subQ6,subQ5,subQ4,subQ3,subQ2,subQ1,subQ0])],"isStart":false})],"blendedInto":[makeQuery(id+"F12.opExtrude","CAP_FACE",FACE,{"disambiguationData":[OSD([subQ17,subQ16,subQ15,subQ14,subQ13,subQ12,subQ11,subQ10,subQ9,subQ8,subQ7,subQ6,subQ5,subQ4,subQ3,subQ2,subQ1,subQ0])],"isStart":false})]})])],"isStart":false}),makeQuery(id+"F14.opExtrude","CAP_FACE",FACE,{"disambiguationData":[OSD([subQ17,subQ16,subQ15,subQ14,subQ13,subQ12,subQ11,subQ10,subQ9,subQ8,subQ7,subQ6,subQ5,subQ4,subQ3,subQ2,subQ1,subQ0])],"isStart":false})],"blendedInto":[makeQuery(id+"F14.opExtrude","CAP_FACE",FACE,{"disambiguationData":[OSD([subQ17,subQ16,subQ15,subQ14,subQ13,subQ12,subQ11,subQ10,subQ9,subQ8,subQ7,subQ6,subQ5,subQ4,subQ3,subQ2,subQ1,subQ0])],"isStart":false})]})])],"isStart":false});}
            var Q4;
            {var subQ0=sQuery(id+"F0.wireOp",EDGE,"E3.4");var subQ1=sQuery(id+"F0.wireOp",EDGE,"E3.3");var subQ2=sQuery(id+"F0.wireOp",EDGE,"E3.2");var subQ3=sQuery(id+"F0.wireOp",EDGE,"E3.1");var subQ4=sQuery(id+"F0.wireOp",EDGE,"E2.5");var subQ5=sQuery(id+"F0.wireOp",EDGE,"E2.4");var subQ6=sQuery(id+"F0.wireOp",EDGE,"E2.3");var subQ7=sQuery(id+"F0.wireOp",EDGE,"E2.2");var subQ8=sQuery(id+"F0.wireOp",EDGE,"E1.4");var subQ9=sQuery(id+"F0.wireOp",EDGE,"E1.3");var subQ10=sQuery(id+"F0.wireOp",EDGE,"E1.2");var subQ11=sQuery(id+"F0.wireOp",EDGE,"E1.1");var subQ12=sQuery(id+"F0.wireOp",EDGE,"E0.5");var subQ13=sQuery(id+"F0.wireOp",EDGE,"E0.4");var subQ14=sQuery(id+"F0.wireOp",EDGE,"E0.3");var subQ15=sQuery(id+"F0.wireOp",EDGE,"E0.2");var subQ16=sQuery(id+"F0.wireOp",EDGE,"E0.1");var subQ17=sQuery(id+"F0.wireOp",EDGE,"E0.0");Q4=makeQuery(id+"F16.opExtrude","CAP_EDGE",EDGE,{"disambiguationData":[OSD([subQ17,subQ16,subQ15,subQ14,subQ13,subQ12,subQ11,subQ10,subQ9,subQ8,subQ7,subQ6,subQ5,subQ4,subQ3,subQ2,subQ1,subQ0]),TDD([makeQuery(id+"F15.opChamfer","BLEND_EDGE",EDGE,{"blendedFrom":[makeQuery(id+"F14.opExtrude","CAP_EDGE",EDGE,{"disambiguationData":[OSD([subQ17,subQ16,subQ15,subQ14,subQ13,subQ12,subQ11,subQ10,subQ9,subQ8,subQ7,subQ6,subQ5,subQ4,subQ3,subQ2,subQ1,subQ0]),TDD([makeQuery(id+"F13.opChamfer","BLEND_EDGE",EDGE,{"blendedFrom":[makeQuery(id+"F12.opExtrude","CAP_EDGE",EDGE,{"disambiguationData":[OSD([subQ17,subQ16,subQ15,subQ14,subQ13,subQ12,subQ11,subQ10,subQ9,subQ8,subQ7,subQ6,subQ5,subQ4,subQ3,subQ2,subQ1,subQ0]),TDD([makeQuery(id+"F11.opChamfer","BLEND_EDGE",EDGE,{"blendedFrom":[makeQuery(id+"F9.opExtrude","CAP_EDGE",EDGE,{"disambiguationData":[OSD([subQ15])],"isStart":false}),makeQuery(id+"F9.opExtrude","CAP_FACE",FACE,{"disambiguationData":[OSD([subQ17,subQ16,subQ15,subQ14,subQ13,subQ12,subQ11,subQ10,subQ9,subQ8,subQ7,subQ6,subQ5,subQ4,subQ3,subQ2,subQ1,subQ0])],"isStart":false})],"blendedInto":[makeQuery(id+"F9.opExtrude","CAP_FACE",FACE,{"disambiguationData":[OSD([subQ17,subQ16,subQ15,subQ14,subQ13,subQ12,subQ11,subQ10,subQ9,subQ8,subQ7,subQ6,subQ5,subQ4,subQ3,subQ2,subQ1,subQ0])],"isStart":false})]})])],"isStart":false}),makeQuery(id+"F12.opExtrude","CAP_FACE",FACE,{"disambiguationData":[OSD([subQ17,subQ16,subQ15,subQ14,subQ13,subQ12,subQ11,subQ10,subQ9,subQ8,subQ7,subQ6,subQ5,subQ4,subQ3,subQ2,subQ1,subQ0])],"isStart":false})],"blendedInto":[makeQuery(id+"F12.opExtrude","CAP_FACE",FACE,{"disambiguationData":[OSD([subQ17,subQ16,subQ15,subQ14,subQ13,subQ12,subQ11,subQ10,subQ9,subQ8,subQ7,subQ6,subQ5,subQ4,subQ3,subQ2,subQ1,subQ0])],"isStart":false})]})])],"isStart":false}),makeQuery(id+"F14.opExtrude","CAP_FACE",FACE,{"disambiguationData":[OSD([subQ17,subQ16,subQ15,subQ14,subQ13,subQ12,subQ11,subQ10,subQ9,subQ8,subQ7,subQ6,subQ5,subQ4,subQ3,subQ2,subQ1,subQ0])],"isStart":false})],"blendedInto":[makeQuery(id+"F14.opExtrude","CAP_FACE",FACE,{"disambiguationData":[OSD([subQ17,subQ16,subQ15,subQ14,subQ13,subQ12,subQ11,subQ10,subQ9,subQ8,subQ7,subQ6,subQ5,subQ4,subQ3,subQ2,subQ1,subQ0])],"isStart":false})]})])],"isStart":false});}
            var Q5;
            {var subQ0=sQuery(id+"F0.wireOp",EDGE,"E3.4");var subQ1=sQuery(id+"F0.wireOp",EDGE,"E3.3");var subQ2=sQuery(id+"F0.wireOp",EDGE,"E3.2");var subQ3=sQuery(id+"F0.wireOp",EDGE,"E3.1");var subQ4=sQuery(id+"F0.wireOp",EDGE,"E2.5");var subQ5=sQuery(id+"F0.wireOp",EDGE,"E2.4");var subQ6=sQuery(id+"F0.wireOp",EDGE,"E2.3");var subQ7=sQuery(id+"F0.wireOp",EDGE,"E2.2");var subQ8=sQuery(id+"F0.wireOp",EDGE,"E1.4");var subQ9=sQuery(id+"F0.wireOp",EDGE,"E1.3");var subQ10=sQuery(id+"F0.wireOp",EDGE,"E1.2");var subQ11=sQuery(id+"F0.wireOp",EDGE,"E1.1");var subQ12=sQuery(id+"F0.wireOp",EDGE,"E0.5");var subQ13=sQuery(id+"F0.wireOp",EDGE,"E0.4");var subQ14=sQuery(id+"F0.wireOp",EDGE,"E0.3");var subQ15=sQuery(id+"F0.wireOp",EDGE,"E0.2");var subQ16=sQuery(id+"F0.wireOp",EDGE,"E0.1");var subQ17=sQuery(id+"F0.wireOp",EDGE,"E0.0");Q5=makeQuery(id+"F16.opExtrude","CAP_EDGE",EDGE,{"disambiguationData":[OSD([subQ17,subQ16,subQ15,subQ14,subQ13,subQ12,subQ11,subQ10,subQ9,subQ8,subQ7,subQ6,subQ5,subQ4,subQ3,subQ2,subQ1,subQ0]),TDD([makeQuery(id+"F15.opChamfer","BLEND_EDGE",EDGE,{"blendedFrom":[makeQuery(id+"F14.opExtrude","CAP_EDGE",EDGE,{"disambiguationData":[OSD([subQ17,subQ16,subQ15,subQ14,subQ13,subQ12,subQ11,subQ10,subQ9,subQ8,subQ7,subQ6,subQ5,subQ4,subQ3,subQ2,subQ1,subQ0]),TDD([makeQuery(id+"F13.opChamfer","BLEND_EDGE",EDGE,{"blendedFrom":[makeQuery(id+"F12.opExtrude","CAP_EDGE",EDGE,{"disambiguationData":[OSD([subQ17,subQ16,subQ15,subQ14,subQ13,subQ12,subQ11,subQ10,subQ9,subQ8,subQ7,subQ6,subQ5,subQ4,subQ3,subQ2,subQ1,subQ0]),TDD([makeQuery(id+"F11.opChamfer","BLEND_EDGE",EDGE,{"blendedFrom":[makeQuery(id+"F9.opExtrude","CAP_EDGE",EDGE,{"disambiguationData":[OSD([subQ14])],"isStart":false}),makeQuery(id+"F9.opExtrude","CAP_FACE",FACE,{"disambiguationData":[OSD([subQ17,subQ16,subQ15,subQ14,subQ13,subQ12,subQ11,subQ10,subQ9,subQ8,subQ7,subQ6,subQ5,subQ4,subQ3,subQ2,subQ1,subQ0])],"isStart":false})],"blendedInto":[makeQuery(id+"F9.opExtrude","CAP_FACE",FACE,{"disambiguationData":[OSD([subQ17,subQ16,subQ15,subQ14,subQ13,subQ12,subQ11,subQ10,subQ9,subQ8,subQ7,subQ6,subQ5,subQ4,subQ3,subQ2,subQ1,subQ0])],"isStart":false})]})])],"isStart":false}),makeQuery(id+"F12.opExtrude","CAP_FACE",FACE,{"disambiguationData":[OSD([subQ17,subQ16,subQ15,subQ14,subQ13,subQ12,subQ11,subQ10,subQ9,subQ8,subQ7,subQ6,subQ5,subQ4,subQ3,subQ2,subQ1,subQ0])],"isStart":false})],"blendedInto":[makeQuery(id+"F12.opExtrude","CAP_FACE",FACE,{"disambiguationData":[OSD([subQ17,subQ16,subQ15,subQ14,subQ13,subQ12,subQ11,subQ10,subQ9,subQ8,subQ7,subQ6,subQ5,subQ4,subQ3,subQ2,subQ1,subQ0])],"isStart":false})]})])],"isStart":false}),makeQuery(id+"F14.opExtrude","CAP_FACE",FACE,{"disambiguationData":[OSD([subQ17,subQ16,subQ15,subQ14,subQ13,subQ12,subQ11,subQ10,subQ9,subQ8,subQ7,subQ6,subQ5,subQ4,subQ3,subQ2,subQ1,subQ0])],"isStart":false})],"blendedInto":[makeQuery(id+"F14.opExtrude","CAP_FACE",FACE,{"disambiguationData":[OSD([subQ17,subQ16,subQ15,subQ14,subQ13,subQ12,subQ11,subQ10,subQ9,subQ8,subQ7,subQ6,subQ5,subQ4,subQ3,subQ2,subQ1,subQ0])],"isStart":false})]})])],"isStart":false});}
            chamfer(context, id + "F17", {"entities" : qUnion([Q0, Q1, Q2, Q3, Q4, Q5]), "width" : 5.08 * mm, "tangentPropagation" : true});
        }
        {
            var Q0;
            Q0=makeQuery(id+"F16.opExtrude","CAP_FACE",FACE,{"disambiguationData":[OSD([sQuery(id+"F0.wireOp",EDGE,"E0.0"),sQuery(id+"F0.wireOp",EDGE,"E0.1"),sQuery(id+"F0.wireOp",EDGE,"E0.2"),sQuery(id+"F0.wireOp",EDGE,"E0.3"),sQuery(id+"F0.wireOp",EDGE,"E0.4"),sQuery(id+"F0.wireOp",EDGE,"E0.5"),sQuery(id+"F0.wireOp",EDGE,"E1.1"),sQuery(id+"F0.wireOp",EDGE,"E1.2"),sQuery(id+"F0.wireOp",EDGE,"E1.3"),sQuery(id+"F0.wireOp",EDGE,"E1.4"),sQuery(id+"F0.wireOp",EDGE,"E2.2"),sQuery(id+"F0.wireOp",EDGE,"E2.3"),sQuery(id+"F0.wireOp",EDGE,"E2.4"),sQuery(id+"F0.wireOp",EDGE,"E2.5"),sQuery(id+"F0.wireOp",EDGE,"E3.1"),sQuery(id+"F0.wireOp",EDGE,"E3.2"),sQuery(id+"F0.wireOp",EDGE,"E3.3"),sQuery(id+"F0.wireOp",EDGE,"E3.4")])],"isStart":false});
            extrude(context, id + "F18", {"entities" : qUnion([Q0]), "operationType" : NewBodyOperationType.ADD, "depth" : 25.4 * mm});
        }
        {
            var Q0;
            {var subQ0=sQuery(id+"F0.wireOp",EDGE,"E3.4");var subQ1=sQuery(id+"F0.wireOp",EDGE,"E3.3");var subQ2=sQuery(id+"F0.wireOp",EDGE,"E3.2");var subQ3=sQuery(id+"F0.wireOp",EDGE,"E3.1");var subQ4=sQuery(id+"F0.wireOp",EDGE,"E2.5");var subQ5=sQuery(id+"F0.wireOp",EDGE,"E2.4");var subQ6=sQuery(id+"F0.wireOp",EDGE,"E2.3");var subQ7=sQuery(id+"F0.wireOp",EDGE,"E2.2");var subQ8=sQuery(id+"F0.wireOp",EDGE,"E1.4");var subQ9=sQuery(id+"F0.wireOp",EDGE,"E1.3");var subQ10=sQuery(id+"F0.wireOp",EDGE,"E1.2");var subQ11=sQuery(id+"F0.wireOp",EDGE,"E1.1");var subQ12=sQuery(id+"F0.wireOp",EDGE,"E0.5");var subQ13=sQuery(id+"F0.wireOp",EDGE,"E0.4");var subQ14=sQuery(id+"F0.wireOp",EDGE,"E0.3");var subQ15=sQuery(id+"F0.wireOp",EDGE,"E0.2");var subQ16=sQuery(id+"F0.wireOp",EDGE,"E0.1");var subQ17=sQuery(id+"F0.wireOp",EDGE,"E0.0");Q0=makeQuery(id+"F18.opExtrude","CAP_EDGE",EDGE,{"disambiguationData":[OSD([subQ17,subQ16,subQ15,subQ14,subQ13,subQ12,subQ11,subQ10,subQ9,subQ8,subQ7,subQ6,subQ5,subQ4,subQ3,subQ2,subQ1,subQ0]),TDD([makeQuery(id+"F17.opChamfer","BLEND_EDGE",EDGE,{"blendedFrom":[makeQuery(id+"F16.opExtrude","CAP_EDGE",EDGE,{"disambiguationData":[OSD([subQ17,subQ16,subQ15,subQ14,subQ13,subQ12,subQ11,subQ10,subQ9,subQ8,subQ7,subQ6,subQ5,subQ4,subQ3,subQ2,subQ1,subQ0]),TDD([makeQuery(id+"F15.opChamfer","BLEND_EDGE",EDGE,{"blendedFrom":[makeQuery(id+"F14.opExtrude","CAP_EDGE",EDGE,{"disambiguationData":[OSD([subQ17,subQ16,subQ15,subQ14,subQ13,subQ12,subQ11,subQ10,subQ9,subQ8,subQ7,subQ6,subQ5,subQ4,subQ3,subQ2,subQ1,subQ0]),TDD([makeQuery(id+"F13.opChamfer","BLEND_EDGE",EDGE,{"blendedFrom":[makeQuery(id+"F12.opExtrude","CAP_EDGE",EDGE,{"disambiguationData":[OSD([subQ17,subQ16,subQ15,subQ14,subQ13,subQ12,subQ11,subQ10,subQ9,subQ8,subQ7,subQ6,subQ5,subQ4,subQ3,subQ2,subQ1,subQ0]),TDD([makeQuery(id+"F11.opChamfer","BLEND_EDGE",EDGE,{"blendedFrom":[makeQuery(id+"F9.opExtrude","CAP_EDGE",EDGE,{"disambiguationData":[OSD([subQ14])],"isStart":false}),makeQuery(id+"F9.opExtrude","CAP_FACE",FACE,{"disambiguationData":[OSD([subQ17,subQ16,subQ15,subQ14,subQ13,subQ12,subQ11,subQ10,subQ9,subQ8,subQ7,subQ6,subQ5,subQ4,subQ3,subQ2,subQ1,subQ0])],"isStart":false})],"blendedInto":[makeQuery(id+"F9.opExtrude","CAP_FACE",FACE,{"disambiguationData":[OSD([subQ17,subQ16,subQ15,subQ14,subQ13,subQ12,subQ11,subQ10,subQ9,subQ8,subQ7,subQ6,subQ5,subQ4,subQ3,subQ2,subQ1,subQ0])],"isStart":false})]})])],"isStart":false}),makeQuery(id+"F12.opExtrude","CAP_FACE",FACE,{"disambiguationData":[OSD([subQ17,subQ16,subQ15,subQ14,subQ13,subQ12,subQ11,subQ10,subQ9,subQ8,subQ7,subQ6,subQ5,subQ4,subQ3,subQ2,subQ1,subQ0])],"isStart":false})],"blendedInto":[makeQuery(id+"F12.opExtrude","CAP_FACE",FACE,{"disambiguationData":[OSD([subQ17,subQ16,subQ15,subQ14,subQ13,subQ12,subQ11,subQ10,subQ9,subQ8,subQ7,subQ6,subQ5,subQ4,subQ3,subQ2,subQ1,subQ0])],"isStart":false})]})])],"isStart":false}),makeQuery(id+"F14.opExtrude","CAP_FACE",FACE,{"disambiguationData":[OSD([subQ17,subQ16,subQ15,subQ14,subQ13,subQ12,subQ11,subQ10,subQ9,subQ8,subQ7,subQ6,subQ5,subQ4,subQ3,subQ2,subQ1,subQ0])],"isStart":false})],"blendedInto":[makeQuery(id+"F14.opExtrude","CAP_FACE",FACE,{"disambiguationData":[OSD([subQ17,subQ16,subQ15,subQ14,subQ13,subQ12,subQ11,subQ10,subQ9,subQ8,subQ7,subQ6,subQ5,subQ4,subQ3,subQ2,subQ1,subQ0])],"isStart":false})]})])],"isStart":false}),makeQuery(id+"F16.opExtrude","CAP_FACE",FACE,{"disambiguationData":[OSD([subQ17,subQ16,subQ15,subQ14,subQ13,subQ12,subQ11,subQ10,subQ9,subQ8,subQ7,subQ6,subQ5,subQ4,subQ3,subQ2,subQ1,subQ0])],"isStart":false})],"blendedInto":[makeQuery(id+"F16.opExtrude","CAP_FACE",FACE,{"disambiguationData":[OSD([subQ17,subQ16,subQ15,subQ14,subQ13,subQ12,subQ11,subQ10,subQ9,subQ8,subQ7,subQ6,subQ5,subQ4,subQ3,subQ2,subQ1,subQ0])],"isStart":false})]})])],"isStart":false});}
            var Q1;
            {var subQ0=sQuery(id+"F0.wireOp",EDGE,"E3.4");var subQ1=sQuery(id+"F0.wireOp",EDGE,"E3.3");var subQ2=sQuery(id+"F0.wireOp",EDGE,"E3.2");var subQ3=sQuery(id+"F0.wireOp",EDGE,"E3.1");var subQ4=sQuery(id+"F0.wireOp",EDGE,"E2.5");var subQ5=sQuery(id+"F0.wireOp",EDGE,"E2.4");var subQ6=sQuery(id+"F0.wireOp",EDGE,"E2.3");var subQ7=sQuery(id+"F0.wireOp",EDGE,"E2.2");var subQ8=sQuery(id+"F0.wireOp",EDGE,"E1.4");var subQ9=sQuery(id+"F0.wireOp",EDGE,"E1.3");var subQ10=sQuery(id+"F0.wireOp",EDGE,"E1.2");var subQ11=sQuery(id+"F0.wireOp",EDGE,"E1.1");var subQ12=sQuery(id+"F0.wireOp",EDGE,"E0.5");var subQ13=sQuery(id+"F0.wireOp",EDGE,"E0.4");var subQ14=sQuery(id+"F0.wireOp",EDGE,"E0.3");var subQ15=sQuery(id+"F0.wireOp",EDGE,"E0.2");var subQ16=sQuery(id+"F0.wireOp",EDGE,"E0.1");var subQ17=sQuery(id+"F0.wireOp",EDGE,"E0.0");Q1=makeQuery(id+"F18.opExtrude","CAP_EDGE",EDGE,{"disambiguationData":[OSD([subQ17,subQ16,subQ15,subQ14,subQ13,subQ12,subQ11,subQ10,subQ9,subQ8,subQ7,subQ6,subQ5,subQ4,subQ3,subQ2,subQ1,subQ0]),TDD([makeQuery(id+"F17.opChamfer","BLEND_EDGE",EDGE,{"blendedFrom":[makeQuery(id+"F16.opExtrude","CAP_EDGE",EDGE,{"disambiguationData":[OSD([subQ17,subQ16,subQ15,subQ14,subQ13,subQ12,subQ11,subQ10,subQ9,subQ8,subQ7,subQ6,subQ5,subQ4,subQ3,subQ2,subQ1,subQ0]),TDD([makeQuery(id+"F15.opChamfer","BLEND_EDGE",EDGE,{"blendedFrom":[makeQuery(id+"F14.opExtrude","CAP_EDGE",EDGE,{"disambiguationData":[OSD([subQ17,subQ16,subQ15,subQ14,subQ13,subQ12,subQ11,subQ10,subQ9,subQ8,subQ7,subQ6,subQ5,subQ4,subQ3,subQ2,subQ1,subQ0]),TDD([makeQuery(id+"F13.opChamfer","BLEND_EDGE",EDGE,{"blendedFrom":[makeQuery(id+"F12.opExtrude","CAP_EDGE",EDGE,{"disambiguationData":[OSD([subQ17,subQ16,subQ15,subQ14,subQ13,subQ12,subQ11,subQ10,subQ9,subQ8,subQ7,subQ6,subQ5,subQ4,subQ3,subQ2,subQ1,subQ0]),TDD([makeQuery(id+"F11.opChamfer","BLEND_EDGE",EDGE,{"blendedFrom":[makeQuery(id+"F9.opExtrude","CAP_EDGE",EDGE,{"disambiguationData":[OSD([subQ15])],"isStart":false}),makeQuery(id+"F9.opExtrude","CAP_FACE",FACE,{"disambiguationData":[OSD([subQ17,subQ16,subQ15,subQ14,subQ13,subQ12,subQ11,subQ10,subQ9,subQ8,subQ7,subQ6,subQ5,subQ4,subQ3,subQ2,subQ1,subQ0])],"isStart":false})],"blendedInto":[makeQuery(id+"F9.opExtrude","CAP_FACE",FACE,{"disambiguationData":[OSD([subQ17,subQ16,subQ15,subQ14,subQ13,subQ12,subQ11,subQ10,subQ9,subQ8,subQ7,subQ6,subQ5,subQ4,subQ3,subQ2,subQ1,subQ0])],"isStart":false})]})])],"isStart":false}),makeQuery(id+"F12.opExtrude","CAP_FACE",FACE,{"disambiguationData":[OSD([subQ17,subQ16,subQ15,subQ14,subQ13,subQ12,subQ11,subQ10,subQ9,subQ8,subQ7,subQ6,subQ5,subQ4,subQ3,subQ2,subQ1,subQ0])],"isStart":false})],"blendedInto":[makeQuery(id+"F12.opExtrude","CAP_FACE",FACE,{"disambiguationData":[OSD([subQ17,subQ16,subQ15,subQ14,subQ13,subQ12,subQ11,subQ10,subQ9,subQ8,subQ7,subQ6,subQ5,subQ4,subQ3,subQ2,subQ1,subQ0])],"isStart":false})]})])],"isStart":false}),makeQuery(id+"F14.opExtrude","CAP_FACE",FACE,{"disambiguationData":[OSD([subQ17,subQ16,subQ15,subQ14,subQ13,subQ12,subQ11,subQ10,subQ9,subQ8,subQ7,subQ6,subQ5,subQ4,subQ3,subQ2,subQ1,subQ0])],"isStart":false})],"blendedInto":[makeQuery(id+"F14.opExtrude","CAP_FACE",FACE,{"disambiguationData":[OSD([subQ17,subQ16,subQ15,subQ14,subQ13,subQ12,subQ11,subQ10,subQ9,subQ8,subQ7,subQ6,subQ5,subQ4,subQ3,subQ2,subQ1,subQ0])],"isStart":false})]})])],"isStart":false}),makeQuery(id+"F16.opExtrude","CAP_FACE",FACE,{"disambiguationData":[OSD([subQ17,subQ16,subQ15,subQ14,subQ13,subQ12,subQ11,subQ10,subQ9,subQ8,subQ7,subQ6,subQ5,subQ4,subQ3,subQ2,subQ1,subQ0])],"isStart":false})],"blendedInto":[makeQuery(id+"F16.opExtrude","CAP_FACE",FACE,{"disambiguationData":[OSD([subQ17,subQ16,subQ15,subQ14,subQ13,subQ12,subQ11,subQ10,subQ9,subQ8,subQ7,subQ6,subQ5,subQ4,subQ3,subQ2,subQ1,subQ0])],"isStart":false})]})])],"isStart":false});}
            var Q2;
            {var subQ0=sQuery(id+"F0.wireOp",EDGE,"E3.4");var subQ1=sQuery(id+"F0.wireOp",EDGE,"E3.3");var subQ2=sQuery(id+"F0.wireOp",EDGE,"E3.2");var subQ3=sQuery(id+"F0.wireOp",EDGE,"E3.1");var subQ4=sQuery(id+"F0.wireOp",EDGE,"E2.5");var subQ5=sQuery(id+"F0.wireOp",EDGE,"E2.4");var subQ6=sQuery(id+"F0.wireOp",EDGE,"E2.3");var subQ7=sQuery(id+"F0.wireOp",EDGE,"E2.2");var subQ8=sQuery(id+"F0.wireOp",EDGE,"E1.4");var subQ9=sQuery(id+"F0.wireOp",EDGE,"E1.3");var subQ10=sQuery(id+"F0.wireOp",EDGE,"E1.2");var subQ11=sQuery(id+"F0.wireOp",EDGE,"E1.1");var subQ12=sQuery(id+"F0.wireOp",EDGE,"E0.5");var subQ13=sQuery(id+"F0.wireOp",EDGE,"E0.4");var subQ14=sQuery(id+"F0.wireOp",EDGE,"E0.3");var subQ15=sQuery(id+"F0.wireOp",EDGE,"E0.2");var subQ16=sQuery(id+"F0.wireOp",EDGE,"E0.1");var subQ17=sQuery(id+"F0.wireOp",EDGE,"E0.0");Q2=makeQuery(id+"F18.opExtrude","CAP_EDGE",EDGE,{"disambiguationData":[OSD([subQ17,subQ16,subQ15,subQ14,subQ13,subQ12,subQ11,subQ10,subQ9,subQ8,subQ7,subQ6,subQ5,subQ4,subQ3,subQ2,subQ1,subQ0]),TDD([makeQuery(id+"F17.opChamfer","BLEND_EDGE",EDGE,{"blendedFrom":[makeQuery(id+"F16.opExtrude","CAP_EDGE",EDGE,{"disambiguationData":[OSD([subQ17,subQ16,subQ15,subQ14,subQ13,subQ12,subQ11,subQ10,subQ9,subQ8,subQ7,subQ6,subQ5,subQ4,subQ3,subQ2,subQ1,subQ0]),TDD([makeQuery(id+"F15.opChamfer","BLEND_EDGE",EDGE,{"blendedFrom":[makeQuery(id+"F14.opExtrude","CAP_EDGE",EDGE,{"disambiguationData":[OSD([subQ17,subQ16,subQ15,subQ14,subQ13,subQ12,subQ11,subQ10,subQ9,subQ8,subQ7,subQ6,subQ5,subQ4,subQ3,subQ2,subQ1,subQ0]),TDD([makeQuery(id+"F13.opChamfer","BLEND_EDGE",EDGE,{"blendedFrom":[makeQuery(id+"F12.opExtrude","CAP_EDGE",EDGE,{"disambiguationData":[OSD([subQ17,subQ16,subQ15,subQ14,subQ13,subQ12,subQ11,subQ10,subQ9,subQ8,subQ7,subQ6,subQ5,subQ4,subQ3,subQ2,subQ1,subQ0]),TDD([makeQuery(id+"F11.opChamfer","BLEND_EDGE",EDGE,{"blendedFrom":[makeQuery(id+"F9.opExtrude","CAP_EDGE",EDGE,{"disambiguationData":[OSD([subQ16])],"isStart":false}),makeQuery(id+"F9.opExtrude","CAP_FACE",FACE,{"disambiguationData":[OSD([subQ17,subQ16,subQ15,subQ14,subQ13,subQ12,subQ11,subQ10,subQ9,subQ8,subQ7,subQ6,subQ5,subQ4,subQ3,subQ2,subQ1,subQ0])],"isStart":false})],"blendedInto":[makeQuery(id+"F9.opExtrude","CAP_FACE",FACE,{"disambiguationData":[OSD([subQ17,subQ16,subQ15,subQ14,subQ13,subQ12,subQ11,subQ10,subQ9,subQ8,subQ7,subQ6,subQ5,subQ4,subQ3,subQ2,subQ1,subQ0])],"isStart":false})]})])],"isStart":false}),makeQuery(id+"F12.opExtrude","CAP_FACE",FACE,{"disambiguationData":[OSD([subQ17,subQ16,subQ15,subQ14,subQ13,subQ12,subQ11,subQ10,subQ9,subQ8,subQ7,subQ6,subQ5,subQ4,subQ3,subQ2,subQ1,subQ0])],"isStart":false})],"blendedInto":[makeQuery(id+"F12.opExtrude","CAP_FACE",FACE,{"disambiguationData":[OSD([subQ17,subQ16,subQ15,subQ14,subQ13,subQ12,subQ11,subQ10,subQ9,subQ8,subQ7,subQ6,subQ5,subQ4,subQ3,subQ2,subQ1,subQ0])],"isStart":false})]})])],"isStart":false}),makeQuery(id+"F14.opExtrude","CAP_FACE",FACE,{"disambiguationData":[OSD([subQ17,subQ16,subQ15,subQ14,subQ13,subQ12,subQ11,subQ10,subQ9,subQ8,subQ7,subQ6,subQ5,subQ4,subQ3,subQ2,subQ1,subQ0])],"isStart":false})],"blendedInto":[makeQuery(id+"F14.opExtrude","CAP_FACE",FACE,{"disambiguationData":[OSD([subQ17,subQ16,subQ15,subQ14,subQ13,subQ12,subQ11,subQ10,subQ9,subQ8,subQ7,subQ6,subQ5,subQ4,subQ3,subQ2,subQ1,subQ0])],"isStart":false})]})])],"isStart":false}),makeQuery(id+"F16.opExtrude","CAP_FACE",FACE,{"disambiguationData":[OSD([subQ17,subQ16,subQ15,subQ14,subQ13,subQ12,subQ11,subQ10,subQ9,subQ8,subQ7,subQ6,subQ5,subQ4,subQ3,subQ2,subQ1,subQ0])],"isStart":false})],"blendedInto":[makeQuery(id+"F16.opExtrude","CAP_FACE",FACE,{"disambiguationData":[OSD([subQ17,subQ16,subQ15,subQ14,subQ13,subQ12,subQ11,subQ10,subQ9,subQ8,subQ7,subQ6,subQ5,subQ4,subQ3,subQ2,subQ1,subQ0])],"isStart":false})]})])],"isStart":false});}
            var Q3;
            {var subQ0=sQuery(id+"F0.wireOp",EDGE,"E3.4");var subQ1=sQuery(id+"F0.wireOp",EDGE,"E3.3");var subQ2=sQuery(id+"F0.wireOp",EDGE,"E3.2");var subQ3=sQuery(id+"F0.wireOp",EDGE,"E3.1");var subQ4=sQuery(id+"F0.wireOp",EDGE,"E2.5");var subQ5=sQuery(id+"F0.wireOp",EDGE,"E2.4");var subQ6=sQuery(id+"F0.wireOp",EDGE,"E2.3");var subQ7=sQuery(id+"F0.wireOp",EDGE,"E2.2");var subQ8=sQuery(id+"F0.wireOp",EDGE,"E1.4");var subQ9=sQuery(id+"F0.wireOp",EDGE,"E1.3");var subQ10=sQuery(id+"F0.wireOp",EDGE,"E1.2");var subQ11=sQuery(id+"F0.wireOp",EDGE,"E1.1");var subQ12=sQuery(id+"F0.wireOp",EDGE,"E0.5");var subQ13=sQuery(id+"F0.wireOp",EDGE,"E0.4");var subQ14=sQuery(id+"F0.wireOp",EDGE,"E0.3");var subQ15=sQuery(id+"F0.wireOp",EDGE,"E0.2");var subQ16=sQuery(id+"F0.wireOp",EDGE,"E0.1");var subQ17=sQuery(id+"F0.wireOp",EDGE,"E0.0");Q3=makeQuery(id+"F18.opExtrude","CAP_EDGE",EDGE,{"disambiguationData":[OSD([subQ17,subQ16,subQ15,subQ14,subQ13,subQ12,subQ11,subQ10,subQ9,subQ8,subQ7,subQ6,subQ5,subQ4,subQ3,subQ2,subQ1,subQ0]),TDD([makeQuery(id+"F17.opChamfer","BLEND_EDGE",EDGE,{"blendedFrom":[makeQuery(id+"F16.opExtrude","CAP_EDGE",EDGE,{"disambiguationData":[OSD([subQ17,subQ16,subQ15,subQ14,subQ13,subQ12,subQ11,subQ10,subQ9,subQ8,subQ7,subQ6,subQ5,subQ4,subQ3,subQ2,subQ1,subQ0]),TDD([makeQuery(id+"F15.opChamfer","BLEND_EDGE",EDGE,{"blendedFrom":[makeQuery(id+"F14.opExtrude","CAP_EDGE",EDGE,{"disambiguationData":[OSD([subQ17,subQ16,subQ15,subQ14,subQ13,subQ12,subQ11,subQ10,subQ9,subQ8,subQ7,subQ6,subQ5,subQ4,subQ3,subQ2,subQ1,subQ0]),TDD([makeQuery(id+"F13.opChamfer","BLEND_EDGE",EDGE,{"blendedFrom":[makeQuery(id+"F12.opExtrude","CAP_EDGE",EDGE,{"disambiguationData":[OSD([subQ17,subQ16,subQ15,subQ14,subQ13,subQ12,subQ11,subQ10,subQ9,subQ8,subQ7,subQ6,subQ5,subQ4,subQ3,subQ2,subQ1,subQ0]),TDD([makeQuery(id+"F11.opChamfer","BLEND_EDGE",EDGE,{"blendedFrom":[makeQuery(id+"F9.opExtrude","CAP_EDGE",EDGE,{"disambiguationData":[OSD([subQ17])],"isStart":false}),makeQuery(id+"F9.opExtrude","CAP_FACE",FACE,{"disambiguationData":[OSD([subQ17,subQ16,subQ15,subQ14,subQ13,subQ12,subQ11,subQ10,subQ9,subQ8,subQ7,subQ6,subQ5,subQ4,subQ3,subQ2,subQ1,subQ0])],"isStart":false})],"blendedInto":[makeQuery(id+"F9.opExtrude","CAP_FACE",FACE,{"disambiguationData":[OSD([subQ17,subQ16,subQ15,subQ14,subQ13,subQ12,subQ11,subQ10,subQ9,subQ8,subQ7,subQ6,subQ5,subQ4,subQ3,subQ2,subQ1,subQ0])],"isStart":false})]})])],"isStart":false}),makeQuery(id+"F12.opExtrude","CAP_FACE",FACE,{"disambiguationData":[OSD([subQ17,subQ16,subQ15,subQ14,subQ13,subQ12,subQ11,subQ10,subQ9,subQ8,subQ7,subQ6,subQ5,subQ4,subQ3,subQ2,subQ1,subQ0])],"isStart":false})],"blendedInto":[makeQuery(id+"F12.opExtrude","CAP_FACE",FACE,{"disambiguationData":[OSD([subQ17,subQ16,subQ15,subQ14,subQ13,subQ12,subQ11,subQ10,subQ9,subQ8,subQ7,subQ6,subQ5,subQ4,subQ3,subQ2,subQ1,subQ0])],"isStart":false})]})])],"isStart":false}),makeQuery(id+"F14.opExtrude","CAP_FACE",FACE,{"disambiguationData":[OSD([subQ17,subQ16,subQ15,subQ14,subQ13,subQ12,subQ11,subQ10,subQ9,subQ8,subQ7,subQ6,subQ5,subQ4,subQ3,subQ2,subQ1,subQ0])],"isStart":false})],"blendedInto":[makeQuery(id+"F14.opExtrude","CAP_FACE",FACE,{"disambiguationData":[OSD([subQ17,subQ16,subQ15,subQ14,subQ13,subQ12,subQ11,subQ10,subQ9,subQ8,subQ7,subQ6,subQ5,subQ4,subQ3,subQ2,subQ1,subQ0])],"isStart":false})]})])],"isStart":false}),makeQuery(id+"F16.opExtrude","CAP_FACE",FACE,{"disambiguationData":[OSD([subQ17,subQ16,subQ15,subQ14,subQ13,subQ12,subQ11,subQ10,subQ9,subQ8,subQ7,subQ6,subQ5,subQ4,subQ3,subQ2,subQ1,subQ0])],"isStart":false})],"blendedInto":[makeQuery(id+"F16.opExtrude","CAP_FACE",FACE,{"disambiguationData":[OSD([subQ17,subQ16,subQ15,subQ14,subQ13,subQ12,subQ11,subQ10,subQ9,subQ8,subQ7,subQ6,subQ5,subQ4,subQ3,subQ2,subQ1,subQ0])],"isStart":false})]})])],"isStart":false});}
            var Q4;
            {var subQ0=sQuery(id+"F0.wireOp",EDGE,"E3.4");var subQ1=sQuery(id+"F0.wireOp",EDGE,"E3.3");var subQ2=sQuery(id+"F0.wireOp",EDGE,"E3.2");var subQ3=sQuery(id+"F0.wireOp",EDGE,"E3.1");var subQ4=sQuery(id+"F0.wireOp",EDGE,"E2.5");var subQ5=sQuery(id+"F0.wireOp",EDGE,"E2.4");var subQ6=sQuery(id+"F0.wireOp",EDGE,"E2.3");var subQ7=sQuery(id+"F0.wireOp",EDGE,"E2.2");var subQ8=sQuery(id+"F0.wireOp",EDGE,"E1.4");var subQ9=sQuery(id+"F0.wireOp",EDGE,"E1.3");var subQ10=sQuery(id+"F0.wireOp",EDGE,"E1.2");var subQ11=sQuery(id+"F0.wireOp",EDGE,"E1.1");var subQ12=sQuery(id+"F0.wireOp",EDGE,"E0.5");var subQ13=sQuery(id+"F0.wireOp",EDGE,"E0.4");var subQ14=sQuery(id+"F0.wireOp",EDGE,"E0.3");var subQ15=sQuery(id+"F0.wireOp",EDGE,"E0.2");var subQ16=sQuery(id+"F0.wireOp",EDGE,"E0.1");var subQ17=sQuery(id+"F0.wireOp",EDGE,"E0.0");Q4=makeQuery(id+"F18.opExtrude","CAP_EDGE",EDGE,{"disambiguationData":[OSD([subQ17,subQ16,subQ15,subQ14,subQ13,subQ12,subQ11,subQ10,subQ9,subQ8,subQ7,subQ6,subQ5,subQ4,subQ3,subQ2,subQ1,subQ0]),TDD([makeQuery(id+"F17.opChamfer","BLEND_EDGE",EDGE,{"blendedFrom":[makeQuery(id+"F16.opExtrude","CAP_EDGE",EDGE,{"disambiguationData":[OSD([subQ17,subQ16,subQ15,subQ14,subQ13,subQ12,subQ11,subQ10,subQ9,subQ8,subQ7,subQ6,subQ5,subQ4,subQ3,subQ2,subQ1,subQ0]),TDD([makeQuery(id+"F15.opChamfer","BLEND_EDGE",EDGE,{"blendedFrom":[makeQuery(id+"F14.opExtrude","CAP_EDGE",EDGE,{"disambiguationData":[OSD([subQ17,subQ16,subQ15,subQ14,subQ13,subQ12,subQ11,subQ10,subQ9,subQ8,subQ7,subQ6,subQ5,subQ4,subQ3,subQ2,subQ1,subQ0]),TDD([makeQuery(id+"F13.opChamfer","BLEND_EDGE",EDGE,{"blendedFrom":[makeQuery(id+"F12.opExtrude","CAP_EDGE",EDGE,{"disambiguationData":[OSD([subQ17,subQ16,subQ15,subQ14,subQ13,subQ12,subQ11,subQ10,subQ9,subQ8,subQ7,subQ6,subQ5,subQ4,subQ3,subQ2,subQ1,subQ0]),TDD([makeQuery(id+"F11.opChamfer","BLEND_EDGE",EDGE,{"blendedFrom":[makeQuery(id+"F9.opExtrude","CAP_EDGE",EDGE,{"disambiguationData":[OSD([subQ12])],"isStart":false}),makeQuery(id+"F9.opExtrude","CAP_FACE",FACE,{"disambiguationData":[OSD([subQ17,subQ16,subQ15,subQ14,subQ13,subQ12,subQ11,subQ10,subQ9,subQ8,subQ7,subQ6,subQ5,subQ4,subQ3,subQ2,subQ1,subQ0])],"isStart":false})],"blendedInto":[makeQuery(id+"F9.opExtrude","CAP_FACE",FACE,{"disambiguationData":[OSD([subQ17,subQ16,subQ15,subQ14,subQ13,subQ12,subQ11,subQ10,subQ9,subQ8,subQ7,subQ6,subQ5,subQ4,subQ3,subQ2,subQ1,subQ0])],"isStart":false})]})])],"isStart":false}),makeQuery(id+"F12.opExtrude","CAP_FACE",FACE,{"disambiguationData":[OSD([subQ17,subQ16,subQ15,subQ14,subQ13,subQ12,subQ11,subQ10,subQ9,subQ8,subQ7,subQ6,subQ5,subQ4,subQ3,subQ2,subQ1,subQ0])],"isStart":false})],"blendedInto":[makeQuery(id+"F12.opExtrude","CAP_FACE",FACE,{"disambiguationData":[OSD([subQ17,subQ16,subQ15,subQ14,subQ13,subQ12,subQ11,subQ10,subQ9,subQ8,subQ7,subQ6,subQ5,subQ4,subQ3,subQ2,subQ1,subQ0])],"isStart":false})]})])],"isStart":false}),makeQuery(id+"F14.opExtrude","CAP_FACE",FACE,{"disambiguationData":[OSD([subQ17,subQ16,subQ15,subQ14,subQ13,subQ12,subQ11,subQ10,subQ9,subQ8,subQ7,subQ6,subQ5,subQ4,subQ3,subQ2,subQ1,subQ0])],"isStart":false})],"blendedInto":[makeQuery(id+"F14.opExtrude","CAP_FACE",FACE,{"disambiguationData":[OSD([subQ17,subQ16,subQ15,subQ14,subQ13,subQ12,subQ11,subQ10,subQ9,subQ8,subQ7,subQ6,subQ5,subQ4,subQ3,subQ2,subQ1,subQ0])],"isStart":false})]})])],"isStart":false}),makeQuery(id+"F16.opExtrude","CAP_FACE",FACE,{"disambiguationData":[OSD([subQ17,subQ16,subQ15,subQ14,subQ13,subQ12,subQ11,subQ10,subQ9,subQ8,subQ7,subQ6,subQ5,subQ4,subQ3,subQ2,subQ1,subQ0])],"isStart":false})],"blendedInto":[makeQuery(id+"F16.opExtrude","CAP_FACE",FACE,{"disambiguationData":[OSD([subQ17,subQ16,subQ15,subQ14,subQ13,subQ12,subQ11,subQ10,subQ9,subQ8,subQ7,subQ6,subQ5,subQ4,subQ3,subQ2,subQ1,subQ0])],"isStart":false})]})])],"isStart":false});}
            var Q5;
            {var subQ0=sQuery(id+"F0.wireOp",EDGE,"E3.4");var subQ1=sQuery(id+"F0.wireOp",EDGE,"E3.3");var subQ2=sQuery(id+"F0.wireOp",EDGE,"E3.2");var subQ3=sQuery(id+"F0.wireOp",EDGE,"E3.1");var subQ4=sQuery(id+"F0.wireOp",EDGE,"E2.5");var subQ5=sQuery(id+"F0.wireOp",EDGE,"E2.4");var subQ6=sQuery(id+"F0.wireOp",EDGE,"E2.3");var subQ7=sQuery(id+"F0.wireOp",EDGE,"E2.2");var subQ8=sQuery(id+"F0.wireOp",EDGE,"E1.4");var subQ9=sQuery(id+"F0.wireOp",EDGE,"E1.3");var subQ10=sQuery(id+"F0.wireOp",EDGE,"E1.2");var subQ11=sQuery(id+"F0.wireOp",EDGE,"E1.1");var subQ12=sQuery(id+"F0.wireOp",EDGE,"E0.5");var subQ13=sQuery(id+"F0.wireOp",EDGE,"E0.4");var subQ14=sQuery(id+"F0.wireOp",EDGE,"E0.3");var subQ15=sQuery(id+"F0.wireOp",EDGE,"E0.2");var subQ16=sQuery(id+"F0.wireOp",EDGE,"E0.1");var subQ17=sQuery(id+"F0.wireOp",EDGE,"E0.0");Q5=makeQuery(id+"F18.opExtrude","CAP_EDGE",EDGE,{"disambiguationData":[OSD([subQ17,subQ16,subQ15,subQ14,subQ13,subQ12,subQ11,subQ10,subQ9,subQ8,subQ7,subQ6,subQ5,subQ4,subQ3,subQ2,subQ1,subQ0]),TDD([makeQuery(id+"F17.opChamfer","BLEND_EDGE",EDGE,{"blendedFrom":[makeQuery(id+"F16.opExtrude","CAP_EDGE",EDGE,{"disambiguationData":[OSD([subQ17,subQ16,subQ15,subQ14,subQ13,subQ12,subQ11,subQ10,subQ9,subQ8,subQ7,subQ6,subQ5,subQ4,subQ3,subQ2,subQ1,subQ0]),TDD([makeQuery(id+"F15.opChamfer","BLEND_EDGE",EDGE,{"blendedFrom":[makeQuery(id+"F14.opExtrude","CAP_EDGE",EDGE,{"disambiguationData":[OSD([subQ17,subQ16,subQ15,subQ14,subQ13,subQ12,subQ11,subQ10,subQ9,subQ8,subQ7,subQ6,subQ5,subQ4,subQ3,subQ2,subQ1,subQ0]),TDD([makeQuery(id+"F13.opChamfer","BLEND_EDGE",EDGE,{"blendedFrom":[makeQuery(id+"F12.opExtrude","CAP_EDGE",EDGE,{"disambiguationData":[OSD([subQ17,subQ16,subQ15,subQ14,subQ13,subQ12,subQ11,subQ10,subQ9,subQ8,subQ7,subQ6,subQ5,subQ4,subQ3,subQ2,subQ1,subQ0]),TDD([makeQuery(id+"F11.opChamfer","BLEND_EDGE",EDGE,{"blendedFrom":[makeQuery(id+"F9.opExtrude","CAP_EDGE",EDGE,{"disambiguationData":[OSD([subQ13])],"isStart":false}),makeQuery(id+"F9.opExtrude","CAP_FACE",FACE,{"disambiguationData":[OSD([subQ17,subQ16,subQ15,subQ14,subQ13,subQ12,subQ11,subQ10,subQ9,subQ8,subQ7,subQ6,subQ5,subQ4,subQ3,subQ2,subQ1,subQ0])],"isStart":false})],"blendedInto":[makeQuery(id+"F9.opExtrude","CAP_FACE",FACE,{"disambiguationData":[OSD([subQ17,subQ16,subQ15,subQ14,subQ13,subQ12,subQ11,subQ10,subQ9,subQ8,subQ7,subQ6,subQ5,subQ4,subQ3,subQ2,subQ1,subQ0])],"isStart":false})]})])],"isStart":false}),makeQuery(id+"F12.opExtrude","CAP_FACE",FACE,{"disambiguationData":[OSD([subQ17,subQ16,subQ15,subQ14,subQ13,subQ12,subQ11,subQ10,subQ9,subQ8,subQ7,subQ6,subQ5,subQ4,subQ3,subQ2,subQ1,subQ0])],"isStart":false})],"blendedInto":[makeQuery(id+"F12.opExtrude","CAP_FACE",FACE,{"disambiguationData":[OSD([subQ17,subQ16,subQ15,subQ14,subQ13,subQ12,subQ11,subQ10,subQ9,subQ8,subQ7,subQ6,subQ5,subQ4,subQ3,subQ2,subQ1,subQ0])],"isStart":false})]})])],"isStart":false}),makeQuery(id+"F14.opExtrude","CAP_FACE",FACE,{"disambiguationData":[OSD([subQ17,subQ16,subQ15,subQ14,subQ13,subQ12,subQ11,subQ10,subQ9,subQ8,subQ7,subQ6,subQ5,subQ4,subQ3,subQ2,subQ1,subQ0])],"isStart":false})],"blendedInto":[makeQuery(id+"F14.opExtrude","CAP_FACE",FACE,{"disambiguationData":[OSD([subQ17,subQ16,subQ15,subQ14,subQ13,subQ12,subQ11,subQ10,subQ9,subQ8,subQ7,subQ6,subQ5,subQ4,subQ3,subQ2,subQ1,subQ0])],"isStart":false})]})])],"isStart":false}),makeQuery(id+"F16.opExtrude","CAP_FACE",FACE,{"disambiguationData":[OSD([subQ17,subQ16,subQ15,subQ14,subQ13,subQ12,subQ11,subQ10,subQ9,subQ8,subQ7,subQ6,subQ5,subQ4,subQ3,subQ2,subQ1,subQ0])],"isStart":false})],"blendedInto":[makeQuery(id+"F16.opExtrude","CAP_FACE",FACE,{"disambiguationData":[OSD([subQ17,subQ16,subQ15,subQ14,subQ13,subQ12,subQ11,subQ10,subQ9,subQ8,subQ7,subQ6,subQ5,subQ4,subQ3,subQ2,subQ1,subQ0])],"isStart":false})]})])],"isStart":false});}
            chamfer(context, id + "F19", {"entities" : qUnion([Q0, Q1, Q2, Q3, Q4, Q5]), "width" : 5.08 * mm, "tangentPropagation" : true});
        }
        {
            var Q0;
            Q0=makeQuery(id+"F18.opExtrude","CAP_FACE",FACE,{"disambiguationData":[OSD([sQuery(id+"F0.wireOp",EDGE,"E0.0"),sQuery(id+"F0.wireOp",EDGE,"E0.1"),sQuery(id+"F0.wireOp",EDGE,"E0.2"),sQuery(id+"F0.wireOp",EDGE,"E0.3"),sQuery(id+"F0.wireOp",EDGE,"E0.4"),sQuery(id+"F0.wireOp",EDGE,"E0.5"),sQuery(id+"F0.wireOp",EDGE,"E1.1"),sQuery(id+"F0.wireOp",EDGE,"E1.2"),sQuery(id+"F0.wireOp",EDGE,"E1.3"),sQuery(id+"F0.wireOp",EDGE,"E1.4"),sQuery(id+"F0.wireOp",EDGE,"E2.2"),sQuery(id+"F0.wireOp",EDGE,"E2.3"),sQuery(id+"F0.wireOp",EDGE,"E2.4"),sQuery(id+"F0.wireOp",EDGE,"E2.5"),sQuery(id+"F0.wireOp",EDGE,"E3.1"),sQuery(id+"F0.wireOp",EDGE,"E3.2"),sQuery(id+"F0.wireOp",EDGE,"E3.3"),sQuery(id+"F0.wireOp",EDGE,"E3.4")])],"isStart":false});
            extrude(context, id + "F20", {"entities" : qUnion([Q0]), "operationType" : NewBodyOperationType.ADD, "depth" : 25.4 * mm});
        }
        {
            var Q0;
            {var subQ0=sQuery(id+"F0.wireOp",EDGE,"E3.4");var subQ1=sQuery(id+"F0.wireOp",EDGE,"E3.3");var subQ2=sQuery(id+"F0.wireOp",EDGE,"E3.2");var subQ3=sQuery(id+"F0.wireOp",EDGE,"E3.1");var subQ4=sQuery(id+"F0.wireOp",EDGE,"E2.5");var subQ5=sQuery(id+"F0.wireOp",EDGE,"E2.4");var subQ6=sQuery(id+"F0.wireOp",EDGE,"E2.3");var subQ7=sQuery(id+"F0.wireOp",EDGE,"E2.2");var subQ8=sQuery(id+"F0.wireOp",EDGE,"E1.4");var subQ9=sQuery(id+"F0.wireOp",EDGE,"E1.3");var subQ10=sQuery(id+"F0.wireOp",EDGE,"E1.2");var subQ11=sQuery(id+"F0.wireOp",EDGE,"E1.1");var subQ12=sQuery(id+"F0.wireOp",EDGE,"E0.5");var subQ13=sQuery(id+"F0.wireOp",EDGE,"E0.4");var subQ14=sQuery(id+"F0.wireOp",EDGE,"E0.3");var subQ15=sQuery(id+"F0.wireOp",EDGE,"E0.2");var subQ16=sQuery(id+"F0.wireOp",EDGE,"E0.1");var subQ17=sQuery(id+"F0.wireOp",EDGE,"E0.0");Q0=makeQuery(id+"F20.opExtrude","CAP_EDGE",EDGE,{"disambiguationData":[OSD([subQ17,subQ16,subQ15,subQ14,subQ13,subQ12,subQ11,subQ10,subQ9,subQ8,subQ7,subQ6,subQ5,subQ4,subQ3,subQ2,subQ1,subQ0]),TDD([makeQuery(id+"F19.opChamfer","BLEND_EDGE",EDGE,{"blendedFrom":[makeQuery(id+"F18.opExtrude","CAP_EDGE",EDGE,{"disambiguationData":[OSD([subQ17,subQ16,subQ15,subQ14,subQ13,subQ12,subQ11,subQ10,subQ9,subQ8,subQ7,subQ6,subQ5,subQ4,subQ3,subQ2,subQ1,subQ0]),TDD([makeQuery(id+"F17.opChamfer","BLEND_EDGE",EDGE,{"blendedFrom":[makeQuery(id+"F16.opExtrude","CAP_EDGE",EDGE,{"disambiguationData":[OSD([subQ17,subQ16,subQ15,subQ14,subQ13,subQ12,subQ11,subQ10,subQ9,subQ8,subQ7,subQ6,subQ5,subQ4,subQ3,subQ2,subQ1,subQ0]),TDD([makeQuery(id+"F15.opChamfer","BLEND_EDGE",EDGE,{"blendedFrom":[makeQuery(id+"F14.opExtrude","CAP_EDGE",EDGE,{"disambiguationData":[OSD([subQ17,subQ16,subQ15,subQ14,subQ13,subQ12,subQ11,subQ10,subQ9,subQ8,subQ7,subQ6,subQ5,subQ4,subQ3,subQ2,subQ1,subQ0]),TDD([makeQuery(id+"F13.opChamfer","BLEND_EDGE",EDGE,{"blendedFrom":[makeQuery(id+"F12.opExtrude","CAP_EDGE",EDGE,{"disambiguationData":[OSD([subQ17,subQ16,subQ15,subQ14,subQ13,subQ12,subQ11,subQ10,subQ9,subQ8,subQ7,subQ6,subQ5,subQ4,subQ3,subQ2,subQ1,subQ0]),TDD([makeQuery(id+"F11.opChamfer","BLEND_EDGE",EDGE,{"blendedFrom":[makeQuery(id+"F9.opExtrude","CAP_EDGE",EDGE,{"disambiguationData":[OSD([subQ13])],"isStart":false}),makeQuery(id+"F9.opExtrude","CAP_FACE",FACE,{"disambiguationData":[OSD([subQ17,subQ16,subQ15,subQ14,subQ13,subQ12,subQ11,subQ10,subQ9,subQ8,subQ7,subQ6,subQ5,subQ4,subQ3,subQ2,subQ1,subQ0])],"isStart":false})],"blendedInto":[makeQuery(id+"F9.opExtrude","CAP_FACE",FACE,{"disambiguationData":[OSD([subQ17,subQ16,subQ15,subQ14,subQ13,subQ12,subQ11,subQ10,subQ9,subQ8,subQ7,subQ6,subQ5,subQ4,subQ3,subQ2,subQ1,subQ0])],"isStart":false})]})])],"isStart":false}),makeQuery(id+"F12.opExtrude","CAP_FACE",FACE,{"disambiguationData":[OSD([subQ17,subQ16,subQ15,subQ14,subQ13,subQ12,subQ11,subQ10,subQ9,subQ8,subQ7,subQ6,subQ5,subQ4,subQ3,subQ2,subQ1,subQ0])],"isStart":false})],"blendedInto":[makeQuery(id+"F12.opExtrude","CAP_FACE",FACE,{"disambiguationData":[OSD([subQ17,subQ16,subQ15,subQ14,subQ13,subQ12,subQ11,subQ10,subQ9,subQ8,subQ7,subQ6,subQ5,subQ4,subQ3,subQ2,subQ1,subQ0])],"isStart":false})]})])],"isStart":false}),makeQuery(id+"F14.opExtrude","CAP_FACE",FACE,{"disambiguationData":[OSD([subQ17,subQ16,subQ15,subQ14,subQ13,subQ12,subQ11,subQ10,subQ9,subQ8,subQ7,subQ6,subQ5,subQ4,subQ3,subQ2,subQ1,subQ0])],"isStart":false})],"blendedInto":[makeQuery(id+"F14.opExtrude","CAP_FACE",FACE,{"disambiguationData":[OSD([subQ17,subQ16,subQ15,subQ14,subQ13,subQ12,subQ11,subQ10,subQ9,subQ8,subQ7,subQ6,subQ5,subQ4,subQ3,subQ2,subQ1,subQ0])],"isStart":false})]})])],"isStart":false}),makeQuery(id+"F16.opExtrude","CAP_FACE",FACE,{"disambiguationData":[OSD([subQ17,subQ16,subQ15,subQ14,subQ13,subQ12,subQ11,subQ10,subQ9,subQ8,subQ7,subQ6,subQ5,subQ4,subQ3,subQ2,subQ1,subQ0])],"isStart":false})],"blendedInto":[makeQuery(id+"F16.opExtrude","CAP_FACE",FACE,{"disambiguationData":[OSD([subQ17,subQ16,subQ15,subQ14,subQ13,subQ12,subQ11,subQ10,subQ9,subQ8,subQ7,subQ6,subQ5,subQ4,subQ3,subQ2,subQ1,subQ0])],"isStart":false})]})])],"isStart":false}),makeQuery(id+"F18.opExtrude","CAP_FACE",FACE,{"disambiguationData":[OSD([subQ17,subQ16,subQ15,subQ14,subQ13,subQ12,subQ11,subQ10,subQ9,subQ8,subQ7,subQ6,subQ5,subQ4,subQ3,subQ2,subQ1,subQ0])],"isStart":false})],"blendedInto":[makeQuery(id+"F18.opExtrude","CAP_FACE",FACE,{"disambiguationData":[OSD([subQ17,subQ16,subQ15,subQ14,subQ13,subQ12,subQ11,subQ10,subQ9,subQ8,subQ7,subQ6,subQ5,subQ4,subQ3,subQ2,subQ1,subQ0])],"isStart":false})]})])],"isStart":false});}
            var Q1;
            {var subQ0=sQuery(id+"F0.wireOp",EDGE,"E3.4");var subQ1=sQuery(id+"F0.wireOp",EDGE,"E3.3");var subQ2=sQuery(id+"F0.wireOp",EDGE,"E3.2");var subQ3=sQuery(id+"F0.wireOp",EDGE,"E3.1");var subQ4=sQuery(id+"F0.wireOp",EDGE,"E2.5");var subQ5=sQuery(id+"F0.wireOp",EDGE,"E2.4");var subQ6=sQuery(id+"F0.wireOp",EDGE,"E2.3");var subQ7=sQuery(id+"F0.wireOp",EDGE,"E2.2");var subQ8=sQuery(id+"F0.wireOp",EDGE,"E1.4");var subQ9=sQuery(id+"F0.wireOp",EDGE,"E1.3");var subQ10=sQuery(id+"F0.wireOp",EDGE,"E1.2");var subQ11=sQuery(id+"F0.wireOp",EDGE,"E1.1");var subQ12=sQuery(id+"F0.wireOp",EDGE,"E0.5");var subQ13=sQuery(id+"F0.wireOp",EDGE,"E0.4");var subQ14=sQuery(id+"F0.wireOp",EDGE,"E0.3");var subQ15=sQuery(id+"F0.wireOp",EDGE,"E0.2");var subQ16=sQuery(id+"F0.wireOp",EDGE,"E0.1");var subQ17=sQuery(id+"F0.wireOp",EDGE,"E0.0");Q1=makeQuery(id+"F20.opExtrude","CAP_EDGE",EDGE,{"disambiguationData":[OSD([subQ17,subQ16,subQ15,subQ14,subQ13,subQ12,subQ11,subQ10,subQ9,subQ8,subQ7,subQ6,subQ5,subQ4,subQ3,subQ2,subQ1,subQ0]),TDD([makeQuery(id+"F19.opChamfer","BLEND_EDGE",EDGE,{"blendedFrom":[makeQuery(id+"F18.opExtrude","CAP_EDGE",EDGE,{"disambiguationData":[OSD([subQ17,subQ16,subQ15,subQ14,subQ13,subQ12,subQ11,subQ10,subQ9,subQ8,subQ7,subQ6,subQ5,subQ4,subQ3,subQ2,subQ1,subQ0]),TDD([makeQuery(id+"F17.opChamfer","BLEND_EDGE",EDGE,{"blendedFrom":[makeQuery(id+"F16.opExtrude","CAP_EDGE",EDGE,{"disambiguationData":[OSD([subQ17,subQ16,subQ15,subQ14,subQ13,subQ12,subQ11,subQ10,subQ9,subQ8,subQ7,subQ6,subQ5,subQ4,subQ3,subQ2,subQ1,subQ0]),TDD([makeQuery(id+"F15.opChamfer","BLEND_EDGE",EDGE,{"blendedFrom":[makeQuery(id+"F14.opExtrude","CAP_EDGE",EDGE,{"disambiguationData":[OSD([subQ17,subQ16,subQ15,subQ14,subQ13,subQ12,subQ11,subQ10,subQ9,subQ8,subQ7,subQ6,subQ5,subQ4,subQ3,subQ2,subQ1,subQ0]),TDD([makeQuery(id+"F13.opChamfer","BLEND_EDGE",EDGE,{"blendedFrom":[makeQuery(id+"F12.opExtrude","CAP_EDGE",EDGE,{"disambiguationData":[OSD([subQ17,subQ16,subQ15,subQ14,subQ13,subQ12,subQ11,subQ10,subQ9,subQ8,subQ7,subQ6,subQ5,subQ4,subQ3,subQ2,subQ1,subQ0]),TDD([makeQuery(id+"F11.opChamfer","BLEND_EDGE",EDGE,{"blendedFrom":[makeQuery(id+"F9.opExtrude","CAP_EDGE",EDGE,{"disambiguationData":[OSD([subQ12])],"isStart":false}),makeQuery(id+"F9.opExtrude","CAP_FACE",FACE,{"disambiguationData":[OSD([subQ17,subQ16,subQ15,subQ14,subQ13,subQ12,subQ11,subQ10,subQ9,subQ8,subQ7,subQ6,subQ5,subQ4,subQ3,subQ2,subQ1,subQ0])],"isStart":false})],"blendedInto":[makeQuery(id+"F9.opExtrude","CAP_FACE",FACE,{"disambiguationData":[OSD([subQ17,subQ16,subQ15,subQ14,subQ13,subQ12,subQ11,subQ10,subQ9,subQ8,subQ7,subQ6,subQ5,subQ4,subQ3,subQ2,subQ1,subQ0])],"isStart":false})]})])],"isStart":false}),makeQuery(id+"F12.opExtrude","CAP_FACE",FACE,{"disambiguationData":[OSD([subQ17,subQ16,subQ15,subQ14,subQ13,subQ12,subQ11,subQ10,subQ9,subQ8,subQ7,subQ6,subQ5,subQ4,subQ3,subQ2,subQ1,subQ0])],"isStart":false})],"blendedInto":[makeQuery(id+"F12.opExtrude","CAP_FACE",FACE,{"disambiguationData":[OSD([subQ17,subQ16,subQ15,subQ14,subQ13,subQ12,subQ11,subQ10,subQ9,subQ8,subQ7,subQ6,subQ5,subQ4,subQ3,subQ2,subQ1,subQ0])],"isStart":false})]})])],"isStart":false}),makeQuery(id+"F14.opExtrude","CAP_FACE",FACE,{"disambiguationData":[OSD([subQ17,subQ16,subQ15,subQ14,subQ13,subQ12,subQ11,subQ10,subQ9,subQ8,subQ7,subQ6,subQ5,subQ4,subQ3,subQ2,subQ1,subQ0])],"isStart":false})],"blendedInto":[makeQuery(id+"F14.opExtrude","CAP_FACE",FACE,{"disambiguationData":[OSD([subQ17,subQ16,subQ15,subQ14,subQ13,subQ12,subQ11,subQ10,subQ9,subQ8,subQ7,subQ6,subQ5,subQ4,subQ3,subQ2,subQ1,subQ0])],"isStart":false})]})])],"isStart":false}),makeQuery(id+"F16.opExtrude","CAP_FACE",FACE,{"disambiguationData":[OSD([subQ17,subQ16,subQ15,subQ14,subQ13,subQ12,subQ11,subQ10,subQ9,subQ8,subQ7,subQ6,subQ5,subQ4,subQ3,subQ2,subQ1,subQ0])],"isStart":false})],"blendedInto":[makeQuery(id+"F16.opExtrude","CAP_FACE",FACE,{"disambiguationData":[OSD([subQ17,subQ16,subQ15,subQ14,subQ13,subQ12,subQ11,subQ10,subQ9,subQ8,subQ7,subQ6,subQ5,subQ4,subQ3,subQ2,subQ1,subQ0])],"isStart":false})]})])],"isStart":false}),makeQuery(id+"F18.opExtrude","CAP_FACE",FACE,{"disambiguationData":[OSD([subQ17,subQ16,subQ15,subQ14,subQ13,subQ12,subQ11,subQ10,subQ9,subQ8,subQ7,subQ6,subQ5,subQ4,subQ3,subQ2,subQ1,subQ0])],"isStart":false})],"blendedInto":[makeQuery(id+"F18.opExtrude","CAP_FACE",FACE,{"disambiguationData":[OSD([subQ17,subQ16,subQ15,subQ14,subQ13,subQ12,subQ11,subQ10,subQ9,subQ8,subQ7,subQ6,subQ5,subQ4,subQ3,subQ2,subQ1,subQ0])],"isStart":false})]})])],"isStart":false});}
            var Q2;
            {var subQ0=sQuery(id+"F0.wireOp",EDGE,"E3.4");var subQ1=sQuery(id+"F0.wireOp",EDGE,"E3.3");var subQ2=sQuery(id+"F0.wireOp",EDGE,"E3.2");var subQ3=sQuery(id+"F0.wireOp",EDGE,"E3.1");var subQ4=sQuery(id+"F0.wireOp",EDGE,"E2.5");var subQ5=sQuery(id+"F0.wireOp",EDGE,"E2.4");var subQ6=sQuery(id+"F0.wireOp",EDGE,"E2.3");var subQ7=sQuery(id+"F0.wireOp",EDGE,"E2.2");var subQ8=sQuery(id+"F0.wireOp",EDGE,"E1.4");var subQ9=sQuery(id+"F0.wireOp",EDGE,"E1.3");var subQ10=sQuery(id+"F0.wireOp",EDGE,"E1.2");var subQ11=sQuery(id+"F0.wireOp",EDGE,"E1.1");var subQ12=sQuery(id+"F0.wireOp",EDGE,"E0.5");var subQ13=sQuery(id+"F0.wireOp",EDGE,"E0.4");var subQ14=sQuery(id+"F0.wireOp",EDGE,"E0.3");var subQ15=sQuery(id+"F0.wireOp",EDGE,"E0.2");var subQ16=sQuery(id+"F0.wireOp",EDGE,"E0.1");var subQ17=sQuery(id+"F0.wireOp",EDGE,"E0.0");Q2=makeQuery(id+"F20.opExtrude","CAP_EDGE",EDGE,{"disambiguationData":[OSD([subQ17,subQ16,subQ15,subQ14,subQ13,subQ12,subQ11,subQ10,subQ9,subQ8,subQ7,subQ6,subQ5,subQ4,subQ3,subQ2,subQ1,subQ0]),TDD([makeQuery(id+"F19.opChamfer","BLEND_EDGE",EDGE,{"blendedFrom":[makeQuery(id+"F18.opExtrude","CAP_EDGE",EDGE,{"disambiguationData":[OSD([subQ17,subQ16,subQ15,subQ14,subQ13,subQ12,subQ11,subQ10,subQ9,subQ8,subQ7,subQ6,subQ5,subQ4,subQ3,subQ2,subQ1,subQ0]),TDD([makeQuery(id+"F17.opChamfer","BLEND_EDGE",EDGE,{"blendedFrom":[makeQuery(id+"F16.opExtrude","CAP_EDGE",EDGE,{"disambiguationData":[OSD([subQ17,subQ16,subQ15,subQ14,subQ13,subQ12,subQ11,subQ10,subQ9,subQ8,subQ7,subQ6,subQ5,subQ4,subQ3,subQ2,subQ1,subQ0]),TDD([makeQuery(id+"F15.opChamfer","BLEND_EDGE",EDGE,{"blendedFrom":[makeQuery(id+"F14.opExtrude","CAP_EDGE",EDGE,{"disambiguationData":[OSD([subQ17,subQ16,subQ15,subQ14,subQ13,subQ12,subQ11,subQ10,subQ9,subQ8,subQ7,subQ6,subQ5,subQ4,subQ3,subQ2,subQ1,subQ0]),TDD([makeQuery(id+"F13.opChamfer","BLEND_EDGE",EDGE,{"blendedFrom":[makeQuery(id+"F12.opExtrude","CAP_EDGE",EDGE,{"disambiguationData":[OSD([subQ17,subQ16,subQ15,subQ14,subQ13,subQ12,subQ11,subQ10,subQ9,subQ8,subQ7,subQ6,subQ5,subQ4,subQ3,subQ2,subQ1,subQ0]),TDD([makeQuery(id+"F11.opChamfer","BLEND_EDGE",EDGE,{"blendedFrom":[makeQuery(id+"F9.opExtrude","CAP_EDGE",EDGE,{"disambiguationData":[OSD([subQ17])],"isStart":false}),makeQuery(id+"F9.opExtrude","CAP_FACE",FACE,{"disambiguationData":[OSD([subQ17,subQ16,subQ15,subQ14,subQ13,subQ12,subQ11,subQ10,subQ9,subQ8,subQ7,subQ6,subQ5,subQ4,subQ3,subQ2,subQ1,subQ0])],"isStart":false})],"blendedInto":[makeQuery(id+"F9.opExtrude","CAP_FACE",FACE,{"disambiguationData":[OSD([subQ17,subQ16,subQ15,subQ14,subQ13,subQ12,subQ11,subQ10,subQ9,subQ8,subQ7,subQ6,subQ5,subQ4,subQ3,subQ2,subQ1,subQ0])],"isStart":false})]})])],"isStart":false}),makeQuery(id+"F12.opExtrude","CAP_FACE",FACE,{"disambiguationData":[OSD([subQ17,subQ16,subQ15,subQ14,subQ13,subQ12,subQ11,subQ10,subQ9,subQ8,subQ7,subQ6,subQ5,subQ4,subQ3,subQ2,subQ1,subQ0])],"isStart":false})],"blendedInto":[makeQuery(id+"F12.opExtrude","CAP_FACE",FACE,{"disambiguationData":[OSD([subQ17,subQ16,subQ15,subQ14,subQ13,subQ12,subQ11,subQ10,subQ9,subQ8,subQ7,subQ6,subQ5,subQ4,subQ3,subQ2,subQ1,subQ0])],"isStart":false})]})])],"isStart":false}),makeQuery(id+"F14.opExtrude","CAP_FACE",FACE,{"disambiguationData":[OSD([subQ17,subQ16,subQ15,subQ14,subQ13,subQ12,subQ11,subQ10,subQ9,subQ8,subQ7,subQ6,subQ5,subQ4,subQ3,subQ2,subQ1,subQ0])],"isStart":false})],"blendedInto":[makeQuery(id+"F14.opExtrude","CAP_FACE",FACE,{"disambiguationData":[OSD([subQ17,subQ16,subQ15,subQ14,subQ13,subQ12,subQ11,subQ10,subQ9,subQ8,subQ7,subQ6,subQ5,subQ4,subQ3,subQ2,subQ1,subQ0])],"isStart":false})]})])],"isStart":false}),makeQuery(id+"F16.opExtrude","CAP_FACE",FACE,{"disambiguationData":[OSD([subQ17,subQ16,subQ15,subQ14,subQ13,subQ12,subQ11,subQ10,subQ9,subQ8,subQ7,subQ6,subQ5,subQ4,subQ3,subQ2,subQ1,subQ0])],"isStart":false})],"blendedInto":[makeQuery(id+"F16.opExtrude","CAP_FACE",FACE,{"disambiguationData":[OSD([subQ17,subQ16,subQ15,subQ14,subQ13,subQ12,subQ11,subQ10,subQ9,subQ8,subQ7,subQ6,subQ5,subQ4,subQ3,subQ2,subQ1,subQ0])],"isStart":false})]})])],"isStart":false}),makeQuery(id+"F18.opExtrude","CAP_FACE",FACE,{"disambiguationData":[OSD([subQ17,subQ16,subQ15,subQ14,subQ13,subQ12,subQ11,subQ10,subQ9,subQ8,subQ7,subQ6,subQ5,subQ4,subQ3,subQ2,subQ1,subQ0])],"isStart":false})],"blendedInto":[makeQuery(id+"F18.opExtrude","CAP_FACE",FACE,{"disambiguationData":[OSD([subQ17,subQ16,subQ15,subQ14,subQ13,subQ12,subQ11,subQ10,subQ9,subQ8,subQ7,subQ6,subQ5,subQ4,subQ3,subQ2,subQ1,subQ0])],"isStart":false})]})])],"isStart":false});}
            var Q3;
            {var subQ0=sQuery(id+"F0.wireOp",EDGE,"E3.4");var subQ1=sQuery(id+"F0.wireOp",EDGE,"E3.3");var subQ2=sQuery(id+"F0.wireOp",EDGE,"E3.2");var subQ3=sQuery(id+"F0.wireOp",EDGE,"E3.1");var subQ4=sQuery(id+"F0.wireOp",EDGE,"E2.5");var subQ5=sQuery(id+"F0.wireOp",EDGE,"E2.4");var subQ6=sQuery(id+"F0.wireOp",EDGE,"E2.3");var subQ7=sQuery(id+"F0.wireOp",EDGE,"E2.2");var subQ8=sQuery(id+"F0.wireOp",EDGE,"E1.4");var subQ9=sQuery(id+"F0.wireOp",EDGE,"E1.3");var subQ10=sQuery(id+"F0.wireOp",EDGE,"E1.2");var subQ11=sQuery(id+"F0.wireOp",EDGE,"E1.1");var subQ12=sQuery(id+"F0.wireOp",EDGE,"E0.5");var subQ13=sQuery(id+"F0.wireOp",EDGE,"E0.4");var subQ14=sQuery(id+"F0.wireOp",EDGE,"E0.3");var subQ15=sQuery(id+"F0.wireOp",EDGE,"E0.2");var subQ16=sQuery(id+"F0.wireOp",EDGE,"E0.1");var subQ17=sQuery(id+"F0.wireOp",EDGE,"E0.0");Q3=makeQuery(id+"F20.opExtrude","CAP_EDGE",EDGE,{"disambiguationData":[OSD([subQ17,subQ16,subQ15,subQ14,subQ13,subQ12,subQ11,subQ10,subQ9,subQ8,subQ7,subQ6,subQ5,subQ4,subQ3,subQ2,subQ1,subQ0]),TDD([makeQuery(id+"F19.opChamfer","BLEND_EDGE",EDGE,{"blendedFrom":[makeQuery(id+"F18.opExtrude","CAP_EDGE",EDGE,{"disambiguationData":[OSD([subQ17,subQ16,subQ15,subQ14,subQ13,subQ12,subQ11,subQ10,subQ9,subQ8,subQ7,subQ6,subQ5,subQ4,subQ3,subQ2,subQ1,subQ0]),TDD([makeQuery(id+"F17.opChamfer","BLEND_EDGE",EDGE,{"blendedFrom":[makeQuery(id+"F16.opExtrude","CAP_EDGE",EDGE,{"disambiguationData":[OSD([subQ17,subQ16,subQ15,subQ14,subQ13,subQ12,subQ11,subQ10,subQ9,subQ8,subQ7,subQ6,subQ5,subQ4,subQ3,subQ2,subQ1,subQ0]),TDD([makeQuery(id+"F15.opChamfer","BLEND_EDGE",EDGE,{"blendedFrom":[makeQuery(id+"F14.opExtrude","CAP_EDGE",EDGE,{"disambiguationData":[OSD([subQ17,subQ16,subQ15,subQ14,subQ13,subQ12,subQ11,subQ10,subQ9,subQ8,subQ7,subQ6,subQ5,subQ4,subQ3,subQ2,subQ1,subQ0]),TDD([makeQuery(id+"F13.opChamfer","BLEND_EDGE",EDGE,{"blendedFrom":[makeQuery(id+"F12.opExtrude","CAP_EDGE",EDGE,{"disambiguationData":[OSD([subQ17,subQ16,subQ15,subQ14,subQ13,subQ12,subQ11,subQ10,subQ9,subQ8,subQ7,subQ6,subQ5,subQ4,subQ3,subQ2,subQ1,subQ0]),TDD([makeQuery(id+"F11.opChamfer","BLEND_EDGE",EDGE,{"blendedFrom":[makeQuery(id+"F9.opExtrude","CAP_EDGE",EDGE,{"disambiguationData":[OSD([subQ16])],"isStart":false}),makeQuery(id+"F9.opExtrude","CAP_FACE",FACE,{"disambiguationData":[OSD([subQ17,subQ16,subQ15,subQ14,subQ13,subQ12,subQ11,subQ10,subQ9,subQ8,subQ7,subQ6,subQ5,subQ4,subQ3,subQ2,subQ1,subQ0])],"isStart":false})],"blendedInto":[makeQuery(id+"F9.opExtrude","CAP_FACE",FACE,{"disambiguationData":[OSD([subQ17,subQ16,subQ15,subQ14,subQ13,subQ12,subQ11,subQ10,subQ9,subQ8,subQ7,subQ6,subQ5,subQ4,subQ3,subQ2,subQ1,subQ0])],"isStart":false})]})])],"isStart":false}),makeQuery(id+"F12.opExtrude","CAP_FACE",FACE,{"disambiguationData":[OSD([subQ17,subQ16,subQ15,subQ14,subQ13,subQ12,subQ11,subQ10,subQ9,subQ8,subQ7,subQ6,subQ5,subQ4,subQ3,subQ2,subQ1,subQ0])],"isStart":false})],"blendedInto":[makeQuery(id+"F12.opExtrude","CAP_FACE",FACE,{"disambiguationData":[OSD([subQ17,subQ16,subQ15,subQ14,subQ13,subQ12,subQ11,subQ10,subQ9,subQ8,subQ7,subQ6,subQ5,subQ4,subQ3,subQ2,subQ1,subQ0])],"isStart":false})]})])],"isStart":false}),makeQuery(id+"F14.opExtrude","CAP_FACE",FACE,{"disambiguationData":[OSD([subQ17,subQ16,subQ15,subQ14,subQ13,subQ12,subQ11,subQ10,subQ9,subQ8,subQ7,subQ6,subQ5,subQ4,subQ3,subQ2,subQ1,subQ0])],"isStart":false})],"blendedInto":[makeQuery(id+"F14.opExtrude","CAP_FACE",FACE,{"disambiguationData":[OSD([subQ17,subQ16,subQ15,subQ14,subQ13,subQ12,subQ11,subQ10,subQ9,subQ8,subQ7,subQ6,subQ5,subQ4,subQ3,subQ2,subQ1,subQ0])],"isStart":false})]})])],"isStart":false}),makeQuery(id+"F16.opExtrude","CAP_FACE",FACE,{"disambiguationData":[OSD([subQ17,subQ16,subQ15,subQ14,subQ13,subQ12,subQ11,subQ10,subQ9,subQ8,subQ7,subQ6,subQ5,subQ4,subQ3,subQ2,subQ1,subQ0])],"isStart":false})],"blendedInto":[makeQuery(id+"F16.opExtrude","CAP_FACE",FACE,{"disambiguationData":[OSD([subQ17,subQ16,subQ15,subQ14,subQ13,subQ12,subQ11,subQ10,subQ9,subQ8,subQ7,subQ6,subQ5,subQ4,subQ3,subQ2,subQ1,subQ0])],"isStart":false})]})])],"isStart":false}),makeQuery(id+"F18.opExtrude","CAP_FACE",FACE,{"disambiguationData":[OSD([subQ17,subQ16,subQ15,subQ14,subQ13,subQ12,subQ11,subQ10,subQ9,subQ8,subQ7,subQ6,subQ5,subQ4,subQ3,subQ2,subQ1,subQ0])],"isStart":false})],"blendedInto":[makeQuery(id+"F18.opExtrude","CAP_FACE",FACE,{"disambiguationData":[OSD([subQ17,subQ16,subQ15,subQ14,subQ13,subQ12,subQ11,subQ10,subQ9,subQ8,subQ7,subQ6,subQ5,subQ4,subQ3,subQ2,subQ1,subQ0])],"isStart":false})]})])],"isStart":false});}
            var Q4;
            {var subQ0=sQuery(id+"F0.wireOp",EDGE,"E3.4");var subQ1=sQuery(id+"F0.wireOp",EDGE,"E3.3");var subQ2=sQuery(id+"F0.wireOp",EDGE,"E3.2");var subQ3=sQuery(id+"F0.wireOp",EDGE,"E3.1");var subQ4=sQuery(id+"F0.wireOp",EDGE,"E2.5");var subQ5=sQuery(id+"F0.wireOp",EDGE,"E2.4");var subQ6=sQuery(id+"F0.wireOp",EDGE,"E2.3");var subQ7=sQuery(id+"F0.wireOp",EDGE,"E2.2");var subQ8=sQuery(id+"F0.wireOp",EDGE,"E1.4");var subQ9=sQuery(id+"F0.wireOp",EDGE,"E1.3");var subQ10=sQuery(id+"F0.wireOp",EDGE,"E1.2");var subQ11=sQuery(id+"F0.wireOp",EDGE,"E1.1");var subQ12=sQuery(id+"F0.wireOp",EDGE,"E0.5");var subQ13=sQuery(id+"F0.wireOp",EDGE,"E0.4");var subQ14=sQuery(id+"F0.wireOp",EDGE,"E0.3");var subQ15=sQuery(id+"F0.wireOp",EDGE,"E0.2");var subQ16=sQuery(id+"F0.wireOp",EDGE,"E0.1");var subQ17=sQuery(id+"F0.wireOp",EDGE,"E0.0");Q4=makeQuery(id+"F20.opExtrude","CAP_EDGE",EDGE,{"disambiguationData":[OSD([subQ17,subQ16,subQ15,subQ14,subQ13,subQ12,subQ11,subQ10,subQ9,subQ8,subQ7,subQ6,subQ5,subQ4,subQ3,subQ2,subQ1,subQ0]),TDD([makeQuery(id+"F19.opChamfer","BLEND_EDGE",EDGE,{"blendedFrom":[makeQuery(id+"F18.opExtrude","CAP_EDGE",EDGE,{"disambiguationData":[OSD([subQ17,subQ16,subQ15,subQ14,subQ13,subQ12,subQ11,subQ10,subQ9,subQ8,subQ7,subQ6,subQ5,subQ4,subQ3,subQ2,subQ1,subQ0]),TDD([makeQuery(id+"F17.opChamfer","BLEND_EDGE",EDGE,{"blendedFrom":[makeQuery(id+"F16.opExtrude","CAP_EDGE",EDGE,{"disambiguationData":[OSD([subQ17,subQ16,subQ15,subQ14,subQ13,subQ12,subQ11,subQ10,subQ9,subQ8,subQ7,subQ6,subQ5,subQ4,subQ3,subQ2,subQ1,subQ0]),TDD([makeQuery(id+"F15.opChamfer","BLEND_EDGE",EDGE,{"blendedFrom":[makeQuery(id+"F14.opExtrude","CAP_EDGE",EDGE,{"disambiguationData":[OSD([subQ17,subQ16,subQ15,subQ14,subQ13,subQ12,subQ11,subQ10,subQ9,subQ8,subQ7,subQ6,subQ5,subQ4,subQ3,subQ2,subQ1,subQ0]),TDD([makeQuery(id+"F13.opChamfer","BLEND_EDGE",EDGE,{"blendedFrom":[makeQuery(id+"F12.opExtrude","CAP_EDGE",EDGE,{"disambiguationData":[OSD([subQ17,subQ16,subQ15,subQ14,subQ13,subQ12,subQ11,subQ10,subQ9,subQ8,subQ7,subQ6,subQ5,subQ4,subQ3,subQ2,subQ1,subQ0]),TDD([makeQuery(id+"F11.opChamfer","BLEND_EDGE",EDGE,{"blendedFrom":[makeQuery(id+"F9.opExtrude","CAP_EDGE",EDGE,{"disambiguationData":[OSD([subQ15])],"isStart":false}),makeQuery(id+"F9.opExtrude","CAP_FACE",FACE,{"disambiguationData":[OSD([subQ17,subQ16,subQ15,subQ14,subQ13,subQ12,subQ11,subQ10,subQ9,subQ8,subQ7,subQ6,subQ5,subQ4,subQ3,subQ2,subQ1,subQ0])],"isStart":false})],"blendedInto":[makeQuery(id+"F9.opExtrude","CAP_FACE",FACE,{"disambiguationData":[OSD([subQ17,subQ16,subQ15,subQ14,subQ13,subQ12,subQ11,subQ10,subQ9,subQ8,subQ7,subQ6,subQ5,subQ4,subQ3,subQ2,subQ1,subQ0])],"isStart":false})]})])],"isStart":false}),makeQuery(id+"F12.opExtrude","CAP_FACE",FACE,{"disambiguationData":[OSD([subQ17,subQ16,subQ15,subQ14,subQ13,subQ12,subQ11,subQ10,subQ9,subQ8,subQ7,subQ6,subQ5,subQ4,subQ3,subQ2,subQ1,subQ0])],"isStart":false})],"blendedInto":[makeQuery(id+"F12.opExtrude","CAP_FACE",FACE,{"disambiguationData":[OSD([subQ17,subQ16,subQ15,subQ14,subQ13,subQ12,subQ11,subQ10,subQ9,subQ8,subQ7,subQ6,subQ5,subQ4,subQ3,subQ2,subQ1,subQ0])],"isStart":false})]})])],"isStart":false}),makeQuery(id+"F14.opExtrude","CAP_FACE",FACE,{"disambiguationData":[OSD([subQ17,subQ16,subQ15,subQ14,subQ13,subQ12,subQ11,subQ10,subQ9,subQ8,subQ7,subQ6,subQ5,subQ4,subQ3,subQ2,subQ1,subQ0])],"isStart":false})],"blendedInto":[makeQuery(id+"F14.opExtrude","CAP_FACE",FACE,{"disambiguationData":[OSD([subQ17,subQ16,subQ15,subQ14,subQ13,subQ12,subQ11,subQ10,subQ9,subQ8,subQ7,subQ6,subQ5,subQ4,subQ3,subQ2,subQ1,subQ0])],"isStart":false})]})])],"isStart":false}),makeQuery(id+"F16.opExtrude","CAP_FACE",FACE,{"disambiguationData":[OSD([subQ17,subQ16,subQ15,subQ14,subQ13,subQ12,subQ11,subQ10,subQ9,subQ8,subQ7,subQ6,subQ5,subQ4,subQ3,subQ2,subQ1,subQ0])],"isStart":false})],"blendedInto":[makeQuery(id+"F16.opExtrude","CAP_FACE",FACE,{"disambiguationData":[OSD([subQ17,subQ16,subQ15,subQ14,subQ13,subQ12,subQ11,subQ10,subQ9,subQ8,subQ7,subQ6,subQ5,subQ4,subQ3,subQ2,subQ1,subQ0])],"isStart":false})]})])],"isStart":false}),makeQuery(id+"F18.opExtrude","CAP_FACE",FACE,{"disambiguationData":[OSD([subQ17,subQ16,subQ15,subQ14,subQ13,subQ12,subQ11,subQ10,subQ9,subQ8,subQ7,subQ6,subQ5,subQ4,subQ3,subQ2,subQ1,subQ0])],"isStart":false})],"blendedInto":[makeQuery(id+"F18.opExtrude","CAP_FACE",FACE,{"disambiguationData":[OSD([subQ17,subQ16,subQ15,subQ14,subQ13,subQ12,subQ11,subQ10,subQ9,subQ8,subQ7,subQ6,subQ5,subQ4,subQ3,subQ2,subQ1,subQ0])],"isStart":false})]})])],"isStart":false});}
            var Q5;
            {var subQ0=sQuery(id+"F0.wireOp",EDGE,"E3.4");var subQ1=sQuery(id+"F0.wireOp",EDGE,"E3.3");var subQ2=sQuery(id+"F0.wireOp",EDGE,"E3.2");var subQ3=sQuery(id+"F0.wireOp",EDGE,"E3.1");var subQ4=sQuery(id+"F0.wireOp",EDGE,"E2.5");var subQ5=sQuery(id+"F0.wireOp",EDGE,"E2.4");var subQ6=sQuery(id+"F0.wireOp",EDGE,"E2.3");var subQ7=sQuery(id+"F0.wireOp",EDGE,"E2.2");var subQ8=sQuery(id+"F0.wireOp",EDGE,"E1.4");var subQ9=sQuery(id+"F0.wireOp",EDGE,"E1.3");var subQ10=sQuery(id+"F0.wireOp",EDGE,"E1.2");var subQ11=sQuery(id+"F0.wireOp",EDGE,"E1.1");var subQ12=sQuery(id+"F0.wireOp",EDGE,"E0.5");var subQ13=sQuery(id+"F0.wireOp",EDGE,"E0.4");var subQ14=sQuery(id+"F0.wireOp",EDGE,"E0.3");var subQ15=sQuery(id+"F0.wireOp",EDGE,"E0.2");var subQ16=sQuery(id+"F0.wireOp",EDGE,"E0.1");var subQ17=sQuery(id+"F0.wireOp",EDGE,"E0.0");Q5=makeQuery(id+"F20.opExtrude","CAP_EDGE",EDGE,{"disambiguationData":[OSD([subQ17,subQ16,subQ15,subQ14,subQ13,subQ12,subQ11,subQ10,subQ9,subQ8,subQ7,subQ6,subQ5,subQ4,subQ3,subQ2,subQ1,subQ0]),TDD([makeQuery(id+"F19.opChamfer","BLEND_EDGE",EDGE,{"blendedFrom":[makeQuery(id+"F18.opExtrude","CAP_EDGE",EDGE,{"disambiguationData":[OSD([subQ17,subQ16,subQ15,subQ14,subQ13,subQ12,subQ11,subQ10,subQ9,subQ8,subQ7,subQ6,subQ5,subQ4,subQ3,subQ2,subQ1,subQ0]),TDD([makeQuery(id+"F17.opChamfer","BLEND_EDGE",EDGE,{"blendedFrom":[makeQuery(id+"F16.opExtrude","CAP_EDGE",EDGE,{"disambiguationData":[OSD([subQ17,subQ16,subQ15,subQ14,subQ13,subQ12,subQ11,subQ10,subQ9,subQ8,subQ7,subQ6,subQ5,subQ4,subQ3,subQ2,subQ1,subQ0]),TDD([makeQuery(id+"F15.opChamfer","BLEND_EDGE",EDGE,{"blendedFrom":[makeQuery(id+"F14.opExtrude","CAP_EDGE",EDGE,{"disambiguationData":[OSD([subQ17,subQ16,subQ15,subQ14,subQ13,subQ12,subQ11,subQ10,subQ9,subQ8,subQ7,subQ6,subQ5,subQ4,subQ3,subQ2,subQ1,subQ0]),TDD([makeQuery(id+"F13.opChamfer","BLEND_EDGE",EDGE,{"blendedFrom":[makeQuery(id+"F12.opExtrude","CAP_EDGE",EDGE,{"disambiguationData":[OSD([subQ17,subQ16,subQ15,subQ14,subQ13,subQ12,subQ11,subQ10,subQ9,subQ8,subQ7,subQ6,subQ5,subQ4,subQ3,subQ2,subQ1,subQ0]),TDD([makeQuery(id+"F11.opChamfer","BLEND_EDGE",EDGE,{"blendedFrom":[makeQuery(id+"F9.opExtrude","CAP_EDGE",EDGE,{"disambiguationData":[OSD([subQ14])],"isStart":false}),makeQuery(id+"F9.opExtrude","CAP_FACE",FACE,{"disambiguationData":[OSD([subQ17,subQ16,subQ15,subQ14,subQ13,subQ12,subQ11,subQ10,subQ9,subQ8,subQ7,subQ6,subQ5,subQ4,subQ3,subQ2,subQ1,subQ0])],"isStart":false})],"blendedInto":[makeQuery(id+"F9.opExtrude","CAP_FACE",FACE,{"disambiguationData":[OSD([subQ17,subQ16,subQ15,subQ14,subQ13,subQ12,subQ11,subQ10,subQ9,subQ8,subQ7,subQ6,subQ5,subQ4,subQ3,subQ2,subQ1,subQ0])],"isStart":false})]})])],"isStart":false}),makeQuery(id+"F12.opExtrude","CAP_FACE",FACE,{"disambiguationData":[OSD([subQ17,subQ16,subQ15,subQ14,subQ13,subQ12,subQ11,subQ10,subQ9,subQ8,subQ7,subQ6,subQ5,subQ4,subQ3,subQ2,subQ1,subQ0])],"isStart":false})],"blendedInto":[makeQuery(id+"F12.opExtrude","CAP_FACE",FACE,{"disambiguationData":[OSD([subQ17,subQ16,subQ15,subQ14,subQ13,subQ12,subQ11,subQ10,subQ9,subQ8,subQ7,subQ6,subQ5,subQ4,subQ3,subQ2,subQ1,subQ0])],"isStart":false})]})])],"isStart":false}),makeQuery(id+"F14.opExtrude","CAP_FACE",FACE,{"disambiguationData":[OSD([subQ17,subQ16,subQ15,subQ14,subQ13,subQ12,subQ11,subQ10,subQ9,subQ8,subQ7,subQ6,subQ5,subQ4,subQ3,subQ2,subQ1,subQ0])],"isStart":false})],"blendedInto":[makeQuery(id+"F14.opExtrude","CAP_FACE",FACE,{"disambiguationData":[OSD([subQ17,subQ16,subQ15,subQ14,subQ13,subQ12,subQ11,subQ10,subQ9,subQ8,subQ7,subQ6,subQ5,subQ4,subQ3,subQ2,subQ1,subQ0])],"isStart":false})]})])],"isStart":false}),makeQuery(id+"F16.opExtrude","CAP_FACE",FACE,{"disambiguationData":[OSD([subQ17,subQ16,subQ15,subQ14,subQ13,subQ12,subQ11,subQ10,subQ9,subQ8,subQ7,subQ6,subQ5,subQ4,subQ3,subQ2,subQ1,subQ0])],"isStart":false})],"blendedInto":[makeQuery(id+"F16.opExtrude","CAP_FACE",FACE,{"disambiguationData":[OSD([subQ17,subQ16,subQ15,subQ14,subQ13,subQ12,subQ11,subQ10,subQ9,subQ8,subQ7,subQ6,subQ5,subQ4,subQ3,subQ2,subQ1,subQ0])],"isStart":false})]})])],"isStart":false}),makeQuery(id+"F18.opExtrude","CAP_FACE",FACE,{"disambiguationData":[OSD([subQ17,subQ16,subQ15,subQ14,subQ13,subQ12,subQ11,subQ10,subQ9,subQ8,subQ7,subQ6,subQ5,subQ4,subQ3,subQ2,subQ1,subQ0])],"isStart":false})],"blendedInto":[makeQuery(id+"F18.opExtrude","CAP_FACE",FACE,{"disambiguationData":[OSD([subQ17,subQ16,subQ15,subQ14,subQ13,subQ12,subQ11,subQ10,subQ9,subQ8,subQ7,subQ6,subQ5,subQ4,subQ3,subQ2,subQ1,subQ0])],"isStart":false})]})])],"isStart":false});}
            chamfer(context, id + "F21", {"entities" : qUnion([Q0, Q1, Q2, Q3, Q4, Q5]), "width" : 5.08 * mm, "tangentPropagation" : true});
        }
        {
            var Q0;
            Q0=makeQuery(id+"F20.opExtrude","CAP_FACE",FACE,{"disambiguationData":[OSD([sQuery(id+"F0.wireOp",EDGE,"E0.0"),sQuery(id+"F0.wireOp",EDGE,"E0.1"),sQuery(id+"F0.wireOp",EDGE,"E0.2"),sQuery(id+"F0.wireOp",EDGE,"E0.3"),sQuery(id+"F0.wireOp",EDGE,"E0.4"),sQuery(id+"F0.wireOp",EDGE,"E0.5"),sQuery(id+"F0.wireOp",EDGE,"E1.1"),sQuery(id+"F0.wireOp",EDGE,"E1.2"),sQuery(id+"F0.wireOp",EDGE,"E1.3"),sQuery(id+"F0.wireOp",EDGE,"E1.4"),sQuery(id+"F0.wireOp",EDGE,"E2.2"),sQuery(id+"F0.wireOp",EDGE,"E2.3"),sQuery(id+"F0.wireOp",EDGE,"E2.4"),sQuery(id+"F0.wireOp",EDGE,"E2.5"),sQuery(id+"F0.wireOp",EDGE,"E3.1"),sQuery(id+"F0.wireOp",EDGE,"E3.2"),sQuery(id+"F0.wireOp",EDGE,"E3.3"),sQuery(id+"F0.wireOp",EDGE,"E3.4")])],"isStart":false});
            extrude(context, id + "F22", {"entities" : qUnion([Q0]), "operationType" : NewBodyOperationType.ADD, "depth" : 25.4 * mm});
        }
        {
            var Q0;
            {var subQ0=sQuery(id+"F0.wireOp",EDGE,"E3.4");var subQ1=sQuery(id+"F0.wireOp",EDGE,"E3.3");var subQ2=sQuery(id+"F0.wireOp",EDGE,"E3.2");var subQ3=sQuery(id+"F0.wireOp",EDGE,"E3.1");var subQ4=sQuery(id+"F0.wireOp",EDGE,"E2.5");var subQ5=sQuery(id+"F0.wireOp",EDGE,"E2.4");var subQ6=sQuery(id+"F0.wireOp",EDGE,"E2.3");var subQ7=sQuery(id+"F0.wireOp",EDGE,"E2.2");var subQ8=sQuery(id+"F0.wireOp",EDGE,"E1.4");var subQ9=sQuery(id+"F0.wireOp",EDGE,"E1.3");var subQ10=sQuery(id+"F0.wireOp",EDGE,"E1.2");var subQ11=sQuery(id+"F0.wireOp",EDGE,"E1.1");var subQ12=sQuery(id+"F0.wireOp",EDGE,"E0.5");var subQ13=sQuery(id+"F0.wireOp",EDGE,"E0.4");var subQ14=sQuery(id+"F0.wireOp",EDGE,"E0.3");var subQ15=sQuery(id+"F0.wireOp",EDGE,"E0.2");var subQ16=sQuery(id+"F0.wireOp",EDGE,"E0.1");var subQ17=sQuery(id+"F0.wireOp",EDGE,"E0.0");Q0=makeQuery(id+"F22.opExtrude","CAP_EDGE",EDGE,{"disambiguationData":[OSD([subQ17,subQ16,subQ15,subQ14,subQ13,subQ12,subQ11,subQ10,subQ9,subQ8,subQ7,subQ6,subQ5,subQ4,subQ3,subQ2,subQ1,subQ0]),TDD([makeQuery(id+"F21.opChamfer","BLEND_EDGE",EDGE,{"blendedFrom":[makeQuery(id+"F20.opExtrude","CAP_EDGE",EDGE,{"disambiguationData":[OSD([subQ17,subQ16,subQ15,subQ14,subQ13,subQ12,subQ11,subQ10,subQ9,subQ8,subQ7,subQ6,subQ5,subQ4,subQ3,subQ2,subQ1,subQ0]),TDD([makeQuery(id+"F19.opChamfer","BLEND_EDGE",EDGE,{"blendedFrom":[makeQuery(id+"F18.opExtrude","CAP_EDGE",EDGE,{"disambiguationData":[OSD([subQ17,subQ16,subQ15,subQ14,subQ13,subQ12,subQ11,subQ10,subQ9,subQ8,subQ7,subQ6,subQ5,subQ4,subQ3,subQ2,subQ1,subQ0]),TDD([makeQuery(id+"F17.opChamfer","BLEND_EDGE",EDGE,{"blendedFrom":[makeQuery(id+"F16.opExtrude","CAP_EDGE",EDGE,{"disambiguationData":[OSD([subQ17,subQ16,subQ15,subQ14,subQ13,subQ12,subQ11,subQ10,subQ9,subQ8,subQ7,subQ6,subQ5,subQ4,subQ3,subQ2,subQ1,subQ0]),TDD([makeQuery(id+"F15.opChamfer","BLEND_EDGE",EDGE,{"blendedFrom":[makeQuery(id+"F14.opExtrude","CAP_EDGE",EDGE,{"disambiguationData":[OSD([subQ17,subQ16,subQ15,subQ14,subQ13,subQ12,subQ11,subQ10,subQ9,subQ8,subQ7,subQ6,subQ5,subQ4,subQ3,subQ2,subQ1,subQ0]),TDD([makeQuery(id+"F13.opChamfer","BLEND_EDGE",EDGE,{"blendedFrom":[makeQuery(id+"F12.opExtrude","CAP_EDGE",EDGE,{"disambiguationData":[OSD([subQ17,subQ16,subQ15,subQ14,subQ13,subQ12,subQ11,subQ10,subQ9,subQ8,subQ7,subQ6,subQ5,subQ4,subQ3,subQ2,subQ1,subQ0]),TDD([makeQuery(id+"F11.opChamfer","BLEND_EDGE",EDGE,{"blendedFrom":[makeQuery(id+"F9.opExtrude","CAP_EDGE",EDGE,{"disambiguationData":[OSD([subQ12])],"isStart":false}),makeQuery(id+"F9.opExtrude","CAP_FACE",FACE,{"disambiguationData":[OSD([subQ17,subQ16,subQ15,subQ14,subQ13,subQ12,subQ11,subQ10,subQ9,subQ8,subQ7,subQ6,subQ5,subQ4,subQ3,subQ2,subQ1,subQ0])],"isStart":false})],"blendedInto":[makeQuery(id+"F9.opExtrude","CAP_FACE",FACE,{"disambiguationData":[OSD([subQ17,subQ16,subQ15,subQ14,subQ13,subQ12,subQ11,subQ10,subQ9,subQ8,subQ7,subQ6,subQ5,subQ4,subQ3,subQ2,subQ1,subQ0])],"isStart":false})]})])],"isStart":false}),makeQuery(id+"F12.opExtrude","CAP_FACE",FACE,{"disambiguationData":[OSD([subQ17,subQ16,subQ15,subQ14,subQ13,subQ12,subQ11,subQ10,subQ9,subQ8,subQ7,subQ6,subQ5,subQ4,subQ3,subQ2,subQ1,subQ0])],"isStart":false})],"blendedInto":[makeQuery(id+"F12.opExtrude","CAP_FACE",FACE,{"disambiguationData":[OSD([subQ17,subQ16,subQ15,subQ14,subQ13,subQ12,subQ11,subQ10,subQ9,subQ8,subQ7,subQ6,subQ5,subQ4,subQ3,subQ2,subQ1,subQ0])],"isStart":false})]})])],"isStart":false}),makeQuery(id+"F14.opExtrude","CAP_FACE",FACE,{"disambiguationData":[OSD([subQ17,subQ16,subQ15,subQ14,subQ13,subQ12,subQ11,subQ10,subQ9,subQ8,subQ7,subQ6,subQ5,subQ4,subQ3,subQ2,subQ1,subQ0])],"isStart":false})],"blendedInto":[makeQuery(id+"F14.opExtrude","CAP_FACE",FACE,{"disambiguationData":[OSD([subQ17,subQ16,subQ15,subQ14,subQ13,subQ12,subQ11,subQ10,subQ9,subQ8,subQ7,subQ6,subQ5,subQ4,subQ3,subQ2,subQ1,subQ0])],"isStart":false})]})])],"isStart":false}),makeQuery(id+"F16.opExtrude","CAP_FACE",FACE,{"disambiguationData":[OSD([subQ17,subQ16,subQ15,subQ14,subQ13,subQ12,subQ11,subQ10,subQ9,subQ8,subQ7,subQ6,subQ5,subQ4,subQ3,subQ2,subQ1,subQ0])],"isStart":false})],"blendedInto":[makeQuery(id+"F16.opExtrude","CAP_FACE",FACE,{"disambiguationData":[OSD([subQ17,subQ16,subQ15,subQ14,subQ13,subQ12,subQ11,subQ10,subQ9,subQ8,subQ7,subQ6,subQ5,subQ4,subQ3,subQ2,subQ1,subQ0])],"isStart":false})]})])],"isStart":false}),makeQuery(id+"F18.opExtrude","CAP_FACE",FACE,{"disambiguationData":[OSD([subQ17,subQ16,subQ15,subQ14,subQ13,subQ12,subQ11,subQ10,subQ9,subQ8,subQ7,subQ6,subQ5,subQ4,subQ3,subQ2,subQ1,subQ0])],"isStart":false})],"blendedInto":[makeQuery(id+"F18.opExtrude","CAP_FACE",FACE,{"disambiguationData":[OSD([subQ17,subQ16,subQ15,subQ14,subQ13,subQ12,subQ11,subQ10,subQ9,subQ8,subQ7,subQ6,subQ5,subQ4,subQ3,subQ2,subQ1,subQ0])],"isStart":false})]})])],"isStart":false}),makeQuery(id+"F20.opExtrude","CAP_FACE",FACE,{"disambiguationData":[OSD([subQ17,subQ16,subQ15,subQ14,subQ13,subQ12,subQ11,subQ10,subQ9,subQ8,subQ7,subQ6,subQ5,subQ4,subQ3,subQ2,subQ1,subQ0])],"isStart":false})],"blendedInto":[makeQuery(id+"F20.opExtrude","CAP_FACE",FACE,{"disambiguationData":[OSD([subQ17,subQ16,subQ15,subQ14,subQ13,subQ12,subQ11,subQ10,subQ9,subQ8,subQ7,subQ6,subQ5,subQ4,subQ3,subQ2,subQ1,subQ0])],"isStart":false})]})])],"isStart":false});}
            var Q1;
            {var subQ0=sQuery(id+"F0.wireOp",EDGE,"E3.4");var subQ1=sQuery(id+"F0.wireOp",EDGE,"E3.3");var subQ2=sQuery(id+"F0.wireOp",EDGE,"E3.2");var subQ3=sQuery(id+"F0.wireOp",EDGE,"E3.1");var subQ4=sQuery(id+"F0.wireOp",EDGE,"E2.5");var subQ5=sQuery(id+"F0.wireOp",EDGE,"E2.4");var subQ6=sQuery(id+"F0.wireOp",EDGE,"E2.3");var subQ7=sQuery(id+"F0.wireOp",EDGE,"E2.2");var subQ8=sQuery(id+"F0.wireOp",EDGE,"E1.4");var subQ9=sQuery(id+"F0.wireOp",EDGE,"E1.3");var subQ10=sQuery(id+"F0.wireOp",EDGE,"E1.2");var subQ11=sQuery(id+"F0.wireOp",EDGE,"E1.1");var subQ12=sQuery(id+"F0.wireOp",EDGE,"E0.5");var subQ13=sQuery(id+"F0.wireOp",EDGE,"E0.4");var subQ14=sQuery(id+"F0.wireOp",EDGE,"E0.3");var subQ15=sQuery(id+"F0.wireOp",EDGE,"E0.2");var subQ16=sQuery(id+"F0.wireOp",EDGE,"E0.1");var subQ17=sQuery(id+"F0.wireOp",EDGE,"E0.0");Q1=makeQuery(id+"F22.opExtrude","CAP_EDGE",EDGE,{"disambiguationData":[OSD([subQ17,subQ16,subQ15,subQ14,subQ13,subQ12,subQ11,subQ10,subQ9,subQ8,subQ7,subQ6,subQ5,subQ4,subQ3,subQ2,subQ1,subQ0]),TDD([makeQuery(id+"F21.opChamfer","BLEND_EDGE",EDGE,{"blendedFrom":[makeQuery(id+"F20.opExtrude","CAP_EDGE",EDGE,{"disambiguationData":[OSD([subQ17,subQ16,subQ15,subQ14,subQ13,subQ12,subQ11,subQ10,subQ9,subQ8,subQ7,subQ6,subQ5,subQ4,subQ3,subQ2,subQ1,subQ0]),TDD([makeQuery(id+"F19.opChamfer","BLEND_EDGE",EDGE,{"blendedFrom":[makeQuery(id+"F18.opExtrude","CAP_EDGE",EDGE,{"disambiguationData":[OSD([subQ17,subQ16,subQ15,subQ14,subQ13,subQ12,subQ11,subQ10,subQ9,subQ8,subQ7,subQ6,subQ5,subQ4,subQ3,subQ2,subQ1,subQ0]),TDD([makeQuery(id+"F17.opChamfer","BLEND_EDGE",EDGE,{"blendedFrom":[makeQuery(id+"F16.opExtrude","CAP_EDGE",EDGE,{"disambiguationData":[OSD([subQ17,subQ16,subQ15,subQ14,subQ13,subQ12,subQ11,subQ10,subQ9,subQ8,subQ7,subQ6,subQ5,subQ4,subQ3,subQ2,subQ1,subQ0]),TDD([makeQuery(id+"F15.opChamfer","BLEND_EDGE",EDGE,{"blendedFrom":[makeQuery(id+"F14.opExtrude","CAP_EDGE",EDGE,{"disambiguationData":[OSD([subQ17,subQ16,subQ15,subQ14,subQ13,subQ12,subQ11,subQ10,subQ9,subQ8,subQ7,subQ6,subQ5,subQ4,subQ3,subQ2,subQ1,subQ0]),TDD([makeQuery(id+"F13.opChamfer","BLEND_EDGE",EDGE,{"blendedFrom":[makeQuery(id+"F12.opExtrude","CAP_EDGE",EDGE,{"disambiguationData":[OSD([subQ17,subQ16,subQ15,subQ14,subQ13,subQ12,subQ11,subQ10,subQ9,subQ8,subQ7,subQ6,subQ5,subQ4,subQ3,subQ2,subQ1,subQ0]),TDD([makeQuery(id+"F11.opChamfer","BLEND_EDGE",EDGE,{"blendedFrom":[makeQuery(id+"F9.opExtrude","CAP_EDGE",EDGE,{"disambiguationData":[OSD([subQ13])],"isStart":false}),makeQuery(id+"F9.opExtrude","CAP_FACE",FACE,{"disambiguationData":[OSD([subQ17,subQ16,subQ15,subQ14,subQ13,subQ12,subQ11,subQ10,subQ9,subQ8,subQ7,subQ6,subQ5,subQ4,subQ3,subQ2,subQ1,subQ0])],"isStart":false})],"blendedInto":[makeQuery(id+"F9.opExtrude","CAP_FACE",FACE,{"disambiguationData":[OSD([subQ17,subQ16,subQ15,subQ14,subQ13,subQ12,subQ11,subQ10,subQ9,subQ8,subQ7,subQ6,subQ5,subQ4,subQ3,subQ2,subQ1,subQ0])],"isStart":false})]})])],"isStart":false}),makeQuery(id+"F12.opExtrude","CAP_FACE",FACE,{"disambiguationData":[OSD([subQ17,subQ16,subQ15,subQ14,subQ13,subQ12,subQ11,subQ10,subQ9,subQ8,subQ7,subQ6,subQ5,subQ4,subQ3,subQ2,subQ1,subQ0])],"isStart":false})],"blendedInto":[makeQuery(id+"F12.opExtrude","CAP_FACE",FACE,{"disambiguationData":[OSD([subQ17,subQ16,subQ15,subQ14,subQ13,subQ12,subQ11,subQ10,subQ9,subQ8,subQ7,subQ6,subQ5,subQ4,subQ3,subQ2,subQ1,subQ0])],"isStart":false})]})])],"isStart":false}),makeQuery(id+"F14.opExtrude","CAP_FACE",FACE,{"disambiguationData":[OSD([subQ17,subQ16,subQ15,subQ14,subQ13,subQ12,subQ11,subQ10,subQ9,subQ8,subQ7,subQ6,subQ5,subQ4,subQ3,subQ2,subQ1,subQ0])],"isStart":false})],"blendedInto":[makeQuery(id+"F14.opExtrude","CAP_FACE",FACE,{"disambiguationData":[OSD([subQ17,subQ16,subQ15,subQ14,subQ13,subQ12,subQ11,subQ10,subQ9,subQ8,subQ7,subQ6,subQ5,subQ4,subQ3,subQ2,subQ1,subQ0])],"isStart":false})]})])],"isStart":false}),makeQuery(id+"F16.opExtrude","CAP_FACE",FACE,{"disambiguationData":[OSD([subQ17,subQ16,subQ15,subQ14,subQ13,subQ12,subQ11,subQ10,subQ9,subQ8,subQ7,subQ6,subQ5,subQ4,subQ3,subQ2,subQ1,subQ0])],"isStart":false})],"blendedInto":[makeQuery(id+"F16.opExtrude","CAP_FACE",FACE,{"disambiguationData":[OSD([subQ17,subQ16,subQ15,subQ14,subQ13,subQ12,subQ11,subQ10,subQ9,subQ8,subQ7,subQ6,subQ5,subQ4,subQ3,subQ2,subQ1,subQ0])],"isStart":false})]})])],"isStart":false}),makeQuery(id+"F18.opExtrude","CAP_FACE",FACE,{"disambiguationData":[OSD([subQ17,subQ16,subQ15,subQ14,subQ13,subQ12,subQ11,subQ10,subQ9,subQ8,subQ7,subQ6,subQ5,subQ4,subQ3,subQ2,subQ1,subQ0])],"isStart":false})],"blendedInto":[makeQuery(id+"F18.opExtrude","CAP_FACE",FACE,{"disambiguationData":[OSD([subQ17,subQ16,subQ15,subQ14,subQ13,subQ12,subQ11,subQ10,subQ9,subQ8,subQ7,subQ6,subQ5,subQ4,subQ3,subQ2,subQ1,subQ0])],"isStart":false})]})])],"isStart":false}),makeQuery(id+"F20.opExtrude","CAP_FACE",FACE,{"disambiguationData":[OSD([subQ17,subQ16,subQ15,subQ14,subQ13,subQ12,subQ11,subQ10,subQ9,subQ8,subQ7,subQ6,subQ5,subQ4,subQ3,subQ2,subQ1,subQ0])],"isStart":false})],"blendedInto":[makeQuery(id+"F20.opExtrude","CAP_FACE",FACE,{"disambiguationData":[OSD([subQ17,subQ16,subQ15,subQ14,subQ13,subQ12,subQ11,subQ10,subQ9,subQ8,subQ7,subQ6,subQ5,subQ4,subQ3,subQ2,subQ1,subQ0])],"isStart":false})]})])],"isStart":false});}
            var Q2;
            {var subQ0=sQuery(id+"F0.wireOp",EDGE,"E3.4");var subQ1=sQuery(id+"F0.wireOp",EDGE,"E3.3");var subQ2=sQuery(id+"F0.wireOp",EDGE,"E3.2");var subQ3=sQuery(id+"F0.wireOp",EDGE,"E3.1");var subQ4=sQuery(id+"F0.wireOp",EDGE,"E2.5");var subQ5=sQuery(id+"F0.wireOp",EDGE,"E2.4");var subQ6=sQuery(id+"F0.wireOp",EDGE,"E2.3");var subQ7=sQuery(id+"F0.wireOp",EDGE,"E2.2");var subQ8=sQuery(id+"F0.wireOp",EDGE,"E1.4");var subQ9=sQuery(id+"F0.wireOp",EDGE,"E1.3");var subQ10=sQuery(id+"F0.wireOp",EDGE,"E1.2");var subQ11=sQuery(id+"F0.wireOp",EDGE,"E1.1");var subQ12=sQuery(id+"F0.wireOp",EDGE,"E0.5");var subQ13=sQuery(id+"F0.wireOp",EDGE,"E0.4");var subQ14=sQuery(id+"F0.wireOp",EDGE,"E0.3");var subQ15=sQuery(id+"F0.wireOp",EDGE,"E0.2");var subQ16=sQuery(id+"F0.wireOp",EDGE,"E0.1");var subQ17=sQuery(id+"F0.wireOp",EDGE,"E0.0");Q2=makeQuery(id+"F22.opExtrude","CAP_EDGE",EDGE,{"disambiguationData":[OSD([subQ17,subQ16,subQ15,subQ14,subQ13,subQ12,subQ11,subQ10,subQ9,subQ8,subQ7,subQ6,subQ5,subQ4,subQ3,subQ2,subQ1,subQ0]),TDD([makeQuery(id+"F21.opChamfer","BLEND_EDGE",EDGE,{"blendedFrom":[makeQuery(id+"F20.opExtrude","CAP_EDGE",EDGE,{"disambiguationData":[OSD([subQ17,subQ16,subQ15,subQ14,subQ13,subQ12,subQ11,subQ10,subQ9,subQ8,subQ7,subQ6,subQ5,subQ4,subQ3,subQ2,subQ1,subQ0]),TDD([makeQuery(id+"F19.opChamfer","BLEND_EDGE",EDGE,{"blendedFrom":[makeQuery(id+"F18.opExtrude","CAP_EDGE",EDGE,{"disambiguationData":[OSD([subQ17,subQ16,subQ15,subQ14,subQ13,subQ12,subQ11,subQ10,subQ9,subQ8,subQ7,subQ6,subQ5,subQ4,subQ3,subQ2,subQ1,subQ0]),TDD([makeQuery(id+"F17.opChamfer","BLEND_EDGE",EDGE,{"blendedFrom":[makeQuery(id+"F16.opExtrude","CAP_EDGE",EDGE,{"disambiguationData":[OSD([subQ17,subQ16,subQ15,subQ14,subQ13,subQ12,subQ11,subQ10,subQ9,subQ8,subQ7,subQ6,subQ5,subQ4,subQ3,subQ2,subQ1,subQ0]),TDD([makeQuery(id+"F15.opChamfer","BLEND_EDGE",EDGE,{"blendedFrom":[makeQuery(id+"F14.opExtrude","CAP_EDGE",EDGE,{"disambiguationData":[OSD([subQ17,subQ16,subQ15,subQ14,subQ13,subQ12,subQ11,subQ10,subQ9,subQ8,subQ7,subQ6,subQ5,subQ4,subQ3,subQ2,subQ1,subQ0]),TDD([makeQuery(id+"F13.opChamfer","BLEND_EDGE",EDGE,{"blendedFrom":[makeQuery(id+"F12.opExtrude","CAP_EDGE",EDGE,{"disambiguationData":[OSD([subQ17,subQ16,subQ15,subQ14,subQ13,subQ12,subQ11,subQ10,subQ9,subQ8,subQ7,subQ6,subQ5,subQ4,subQ3,subQ2,subQ1,subQ0]),TDD([makeQuery(id+"F11.opChamfer","BLEND_EDGE",EDGE,{"blendedFrom":[makeQuery(id+"F9.opExtrude","CAP_EDGE",EDGE,{"disambiguationData":[OSD([subQ15])],"isStart":false}),makeQuery(id+"F9.opExtrude","CAP_FACE",FACE,{"disambiguationData":[OSD([subQ17,subQ16,subQ15,subQ14,subQ13,subQ12,subQ11,subQ10,subQ9,subQ8,subQ7,subQ6,subQ5,subQ4,subQ3,subQ2,subQ1,subQ0])],"isStart":false})],"blendedInto":[makeQuery(id+"F9.opExtrude","CAP_FACE",FACE,{"disambiguationData":[OSD([subQ17,subQ16,subQ15,subQ14,subQ13,subQ12,subQ11,subQ10,subQ9,subQ8,subQ7,subQ6,subQ5,subQ4,subQ3,subQ2,subQ1,subQ0])],"isStart":false})]})])],"isStart":false}),makeQuery(id+"F12.opExtrude","CAP_FACE",FACE,{"disambiguationData":[OSD([subQ17,subQ16,subQ15,subQ14,subQ13,subQ12,subQ11,subQ10,subQ9,subQ8,subQ7,subQ6,subQ5,subQ4,subQ3,subQ2,subQ1,subQ0])],"isStart":false})],"blendedInto":[makeQuery(id+"F12.opExtrude","CAP_FACE",FACE,{"disambiguationData":[OSD([subQ17,subQ16,subQ15,subQ14,subQ13,subQ12,subQ11,subQ10,subQ9,subQ8,subQ7,subQ6,subQ5,subQ4,subQ3,subQ2,subQ1,subQ0])],"isStart":false})]})])],"isStart":false}),makeQuery(id+"F14.opExtrude","CAP_FACE",FACE,{"disambiguationData":[OSD([subQ17,subQ16,subQ15,subQ14,subQ13,subQ12,subQ11,subQ10,subQ9,subQ8,subQ7,subQ6,subQ5,subQ4,subQ3,subQ2,subQ1,subQ0])],"isStart":false})],"blendedInto":[makeQuery(id+"F14.opExtrude","CAP_FACE",FACE,{"disambiguationData":[OSD([subQ17,subQ16,subQ15,subQ14,subQ13,subQ12,subQ11,subQ10,subQ9,subQ8,subQ7,subQ6,subQ5,subQ4,subQ3,subQ2,subQ1,subQ0])],"isStart":false})]})])],"isStart":false}),makeQuery(id+"F16.opExtrude","CAP_FACE",FACE,{"disambiguationData":[OSD([subQ17,subQ16,subQ15,subQ14,subQ13,subQ12,subQ11,subQ10,subQ9,subQ8,subQ7,subQ6,subQ5,subQ4,subQ3,subQ2,subQ1,subQ0])],"isStart":false})],"blendedInto":[makeQuery(id+"F16.opExtrude","CAP_FACE",FACE,{"disambiguationData":[OSD([subQ17,subQ16,subQ15,subQ14,subQ13,subQ12,subQ11,subQ10,subQ9,subQ8,subQ7,subQ6,subQ5,subQ4,subQ3,subQ2,subQ1,subQ0])],"isStart":false})]})])],"isStart":false}),makeQuery(id+"F18.opExtrude","CAP_FACE",FACE,{"disambiguationData":[OSD([subQ17,subQ16,subQ15,subQ14,subQ13,subQ12,subQ11,subQ10,subQ9,subQ8,subQ7,subQ6,subQ5,subQ4,subQ3,subQ2,subQ1,subQ0])],"isStart":false})],"blendedInto":[makeQuery(id+"F18.opExtrude","CAP_FACE",FACE,{"disambiguationData":[OSD([subQ17,subQ16,subQ15,subQ14,subQ13,subQ12,subQ11,subQ10,subQ9,subQ8,subQ7,subQ6,subQ5,subQ4,subQ3,subQ2,subQ1,subQ0])],"isStart":false})]})])],"isStart":false}),makeQuery(id+"F20.opExtrude","CAP_FACE",FACE,{"disambiguationData":[OSD([subQ17,subQ16,subQ15,subQ14,subQ13,subQ12,subQ11,subQ10,subQ9,subQ8,subQ7,subQ6,subQ5,subQ4,subQ3,subQ2,subQ1,subQ0])],"isStart":false})],"blendedInto":[makeQuery(id+"F20.opExtrude","CAP_FACE",FACE,{"disambiguationData":[OSD([subQ17,subQ16,subQ15,subQ14,subQ13,subQ12,subQ11,subQ10,subQ9,subQ8,subQ7,subQ6,subQ5,subQ4,subQ3,subQ2,subQ1,subQ0])],"isStart":false})]})])],"isStart":false});}
            var Q3;
            {var subQ0=sQuery(id+"F0.wireOp",EDGE,"E3.4");var subQ1=sQuery(id+"F0.wireOp",EDGE,"E3.3");var subQ2=sQuery(id+"F0.wireOp",EDGE,"E3.2");var subQ3=sQuery(id+"F0.wireOp",EDGE,"E3.1");var subQ4=sQuery(id+"F0.wireOp",EDGE,"E2.5");var subQ5=sQuery(id+"F0.wireOp",EDGE,"E2.4");var subQ6=sQuery(id+"F0.wireOp",EDGE,"E2.3");var subQ7=sQuery(id+"F0.wireOp",EDGE,"E2.2");var subQ8=sQuery(id+"F0.wireOp",EDGE,"E1.4");var subQ9=sQuery(id+"F0.wireOp",EDGE,"E1.3");var subQ10=sQuery(id+"F0.wireOp",EDGE,"E1.2");var subQ11=sQuery(id+"F0.wireOp",EDGE,"E1.1");var subQ12=sQuery(id+"F0.wireOp",EDGE,"E0.5");var subQ13=sQuery(id+"F0.wireOp",EDGE,"E0.4");var subQ14=sQuery(id+"F0.wireOp",EDGE,"E0.3");var subQ15=sQuery(id+"F0.wireOp",EDGE,"E0.2");var subQ16=sQuery(id+"F0.wireOp",EDGE,"E0.1");var subQ17=sQuery(id+"F0.wireOp",EDGE,"E0.0");Q3=makeQuery(id+"F22.opExtrude","CAP_EDGE",EDGE,{"disambiguationData":[OSD([subQ17,subQ16,subQ15,subQ14,subQ13,subQ12,subQ11,subQ10,subQ9,subQ8,subQ7,subQ6,subQ5,subQ4,subQ3,subQ2,subQ1,subQ0]),TDD([makeQuery(id+"F21.opChamfer","BLEND_EDGE",EDGE,{"blendedFrom":[makeQuery(id+"F20.opExtrude","CAP_EDGE",EDGE,{"disambiguationData":[OSD([subQ17,subQ16,subQ15,subQ14,subQ13,subQ12,subQ11,subQ10,subQ9,subQ8,subQ7,subQ6,subQ5,subQ4,subQ3,subQ2,subQ1,subQ0]),TDD([makeQuery(id+"F19.opChamfer","BLEND_EDGE",EDGE,{"blendedFrom":[makeQuery(id+"F18.opExtrude","CAP_EDGE",EDGE,{"disambiguationData":[OSD([subQ17,subQ16,subQ15,subQ14,subQ13,subQ12,subQ11,subQ10,subQ9,subQ8,subQ7,subQ6,subQ5,subQ4,subQ3,subQ2,subQ1,subQ0]),TDD([makeQuery(id+"F17.opChamfer","BLEND_EDGE",EDGE,{"blendedFrom":[makeQuery(id+"F16.opExtrude","CAP_EDGE",EDGE,{"disambiguationData":[OSD([subQ17,subQ16,subQ15,subQ14,subQ13,subQ12,subQ11,subQ10,subQ9,subQ8,subQ7,subQ6,subQ5,subQ4,subQ3,subQ2,subQ1,subQ0]),TDD([makeQuery(id+"F15.opChamfer","BLEND_EDGE",EDGE,{"blendedFrom":[makeQuery(id+"F14.opExtrude","CAP_EDGE",EDGE,{"disambiguationData":[OSD([subQ17,subQ16,subQ15,subQ14,subQ13,subQ12,subQ11,subQ10,subQ9,subQ8,subQ7,subQ6,subQ5,subQ4,subQ3,subQ2,subQ1,subQ0]),TDD([makeQuery(id+"F13.opChamfer","BLEND_EDGE",EDGE,{"blendedFrom":[makeQuery(id+"F12.opExtrude","CAP_EDGE",EDGE,{"disambiguationData":[OSD([subQ17,subQ16,subQ15,subQ14,subQ13,subQ12,subQ11,subQ10,subQ9,subQ8,subQ7,subQ6,subQ5,subQ4,subQ3,subQ2,subQ1,subQ0]),TDD([makeQuery(id+"F11.opChamfer","BLEND_EDGE",EDGE,{"blendedFrom":[makeQuery(id+"F9.opExtrude","CAP_EDGE",EDGE,{"disambiguationData":[OSD([subQ16])],"isStart":false}),makeQuery(id+"F9.opExtrude","CAP_FACE",FACE,{"disambiguationData":[OSD([subQ17,subQ16,subQ15,subQ14,subQ13,subQ12,subQ11,subQ10,subQ9,subQ8,subQ7,subQ6,subQ5,subQ4,subQ3,subQ2,subQ1,subQ0])],"isStart":false})],"blendedInto":[makeQuery(id+"F9.opExtrude","CAP_FACE",FACE,{"disambiguationData":[OSD([subQ17,subQ16,subQ15,subQ14,subQ13,subQ12,subQ11,subQ10,subQ9,subQ8,subQ7,subQ6,subQ5,subQ4,subQ3,subQ2,subQ1,subQ0])],"isStart":false})]})])],"isStart":false}),makeQuery(id+"F12.opExtrude","CAP_FACE",FACE,{"disambiguationData":[OSD([subQ17,subQ16,subQ15,subQ14,subQ13,subQ12,subQ11,subQ10,subQ9,subQ8,subQ7,subQ6,subQ5,subQ4,subQ3,subQ2,subQ1,subQ0])],"isStart":false})],"blendedInto":[makeQuery(id+"F12.opExtrude","CAP_FACE",FACE,{"disambiguationData":[OSD([subQ17,subQ16,subQ15,subQ14,subQ13,subQ12,subQ11,subQ10,subQ9,subQ8,subQ7,subQ6,subQ5,subQ4,subQ3,subQ2,subQ1,subQ0])],"isStart":false})]})])],"isStart":false}),makeQuery(id+"F14.opExtrude","CAP_FACE",FACE,{"disambiguationData":[OSD([subQ17,subQ16,subQ15,subQ14,subQ13,subQ12,subQ11,subQ10,subQ9,subQ8,subQ7,subQ6,subQ5,subQ4,subQ3,subQ2,subQ1,subQ0])],"isStart":false})],"blendedInto":[makeQuery(id+"F14.opExtrude","CAP_FACE",FACE,{"disambiguationData":[OSD([subQ17,subQ16,subQ15,subQ14,subQ13,subQ12,subQ11,subQ10,subQ9,subQ8,subQ7,subQ6,subQ5,subQ4,subQ3,subQ2,subQ1,subQ0])],"isStart":false})]})])],"isStart":false}),makeQuery(id+"F16.opExtrude","CAP_FACE",FACE,{"disambiguationData":[OSD([subQ17,subQ16,subQ15,subQ14,subQ13,subQ12,subQ11,subQ10,subQ9,subQ8,subQ7,subQ6,subQ5,subQ4,subQ3,subQ2,subQ1,subQ0])],"isStart":false})],"blendedInto":[makeQuery(id+"F16.opExtrude","CAP_FACE",FACE,{"disambiguationData":[OSD([subQ17,subQ16,subQ15,subQ14,subQ13,subQ12,subQ11,subQ10,subQ9,subQ8,subQ7,subQ6,subQ5,subQ4,subQ3,subQ2,subQ1,subQ0])],"isStart":false})]})])],"isStart":false}),makeQuery(id+"F18.opExtrude","CAP_FACE",FACE,{"disambiguationData":[OSD([subQ17,subQ16,subQ15,subQ14,subQ13,subQ12,subQ11,subQ10,subQ9,subQ8,subQ7,subQ6,subQ5,subQ4,subQ3,subQ2,subQ1,subQ0])],"isStart":false})],"blendedInto":[makeQuery(id+"F18.opExtrude","CAP_FACE",FACE,{"disambiguationData":[OSD([subQ17,subQ16,subQ15,subQ14,subQ13,subQ12,subQ11,subQ10,subQ9,subQ8,subQ7,subQ6,subQ5,subQ4,subQ3,subQ2,subQ1,subQ0])],"isStart":false})]})])],"isStart":false}),makeQuery(id+"F20.opExtrude","CAP_FACE",FACE,{"disambiguationData":[OSD([subQ17,subQ16,subQ15,subQ14,subQ13,subQ12,subQ11,subQ10,subQ9,subQ8,subQ7,subQ6,subQ5,subQ4,subQ3,subQ2,subQ1,subQ0])],"isStart":false})],"blendedInto":[makeQuery(id+"F20.opExtrude","CAP_FACE",FACE,{"disambiguationData":[OSD([subQ17,subQ16,subQ15,subQ14,subQ13,subQ12,subQ11,subQ10,subQ9,subQ8,subQ7,subQ6,subQ5,subQ4,subQ3,subQ2,subQ1,subQ0])],"isStart":false})]})])],"isStart":false});}
            var Q4;
            {var subQ0=sQuery(id+"F0.wireOp",EDGE,"E3.4");var subQ1=sQuery(id+"F0.wireOp",EDGE,"E3.3");var subQ2=sQuery(id+"F0.wireOp",EDGE,"E3.2");var subQ3=sQuery(id+"F0.wireOp",EDGE,"E3.1");var subQ4=sQuery(id+"F0.wireOp",EDGE,"E2.5");var subQ5=sQuery(id+"F0.wireOp",EDGE,"E2.4");var subQ6=sQuery(id+"F0.wireOp",EDGE,"E2.3");var subQ7=sQuery(id+"F0.wireOp",EDGE,"E2.2");var subQ8=sQuery(id+"F0.wireOp",EDGE,"E1.4");var subQ9=sQuery(id+"F0.wireOp",EDGE,"E1.3");var subQ10=sQuery(id+"F0.wireOp",EDGE,"E1.2");var subQ11=sQuery(id+"F0.wireOp",EDGE,"E1.1");var subQ12=sQuery(id+"F0.wireOp",EDGE,"E0.5");var subQ13=sQuery(id+"F0.wireOp",EDGE,"E0.4");var subQ14=sQuery(id+"F0.wireOp",EDGE,"E0.3");var subQ15=sQuery(id+"F0.wireOp",EDGE,"E0.2");var subQ16=sQuery(id+"F0.wireOp",EDGE,"E0.1");var subQ17=sQuery(id+"F0.wireOp",EDGE,"E0.0");Q4=makeQuery(id+"F22.opExtrude","CAP_EDGE",EDGE,{"disambiguationData":[OSD([subQ17,subQ16,subQ15,subQ14,subQ13,subQ12,subQ11,subQ10,subQ9,subQ8,subQ7,subQ6,subQ5,subQ4,subQ3,subQ2,subQ1,subQ0]),TDD([makeQuery(id+"F21.opChamfer","BLEND_EDGE",EDGE,{"blendedFrom":[makeQuery(id+"F20.opExtrude","CAP_EDGE",EDGE,{"disambiguationData":[OSD([subQ17,subQ16,subQ15,subQ14,subQ13,subQ12,subQ11,subQ10,subQ9,subQ8,subQ7,subQ6,subQ5,subQ4,subQ3,subQ2,subQ1,subQ0]),TDD([makeQuery(id+"F19.opChamfer","BLEND_EDGE",EDGE,{"blendedFrom":[makeQuery(id+"F18.opExtrude","CAP_EDGE",EDGE,{"disambiguationData":[OSD([subQ17,subQ16,subQ15,subQ14,subQ13,subQ12,subQ11,subQ10,subQ9,subQ8,subQ7,subQ6,subQ5,subQ4,subQ3,subQ2,subQ1,subQ0]),TDD([makeQuery(id+"F17.opChamfer","BLEND_EDGE",EDGE,{"blendedFrom":[makeQuery(id+"F16.opExtrude","CAP_EDGE",EDGE,{"disambiguationData":[OSD([subQ17,subQ16,subQ15,subQ14,subQ13,subQ12,subQ11,subQ10,subQ9,subQ8,subQ7,subQ6,subQ5,subQ4,subQ3,subQ2,subQ1,subQ0]),TDD([makeQuery(id+"F15.opChamfer","BLEND_EDGE",EDGE,{"blendedFrom":[makeQuery(id+"F14.opExtrude","CAP_EDGE",EDGE,{"disambiguationData":[OSD([subQ17,subQ16,subQ15,subQ14,subQ13,subQ12,subQ11,subQ10,subQ9,subQ8,subQ7,subQ6,subQ5,subQ4,subQ3,subQ2,subQ1,subQ0]),TDD([makeQuery(id+"F13.opChamfer","BLEND_EDGE",EDGE,{"blendedFrom":[makeQuery(id+"F12.opExtrude","CAP_EDGE",EDGE,{"disambiguationData":[OSD([subQ17,subQ16,subQ15,subQ14,subQ13,subQ12,subQ11,subQ10,subQ9,subQ8,subQ7,subQ6,subQ5,subQ4,subQ3,subQ2,subQ1,subQ0]),TDD([makeQuery(id+"F11.opChamfer","BLEND_EDGE",EDGE,{"blendedFrom":[makeQuery(id+"F9.opExtrude","CAP_EDGE",EDGE,{"disambiguationData":[OSD([subQ14])],"isStart":false}),makeQuery(id+"F9.opExtrude","CAP_FACE",FACE,{"disambiguationData":[OSD([subQ17,subQ16,subQ15,subQ14,subQ13,subQ12,subQ11,subQ10,subQ9,subQ8,subQ7,subQ6,subQ5,subQ4,subQ3,subQ2,subQ1,subQ0])],"isStart":false})],"blendedInto":[makeQuery(id+"F9.opExtrude","CAP_FACE",FACE,{"disambiguationData":[OSD([subQ17,subQ16,subQ15,subQ14,subQ13,subQ12,subQ11,subQ10,subQ9,subQ8,subQ7,subQ6,subQ5,subQ4,subQ3,subQ2,subQ1,subQ0])],"isStart":false})]})])],"isStart":false}),makeQuery(id+"F12.opExtrude","CAP_FACE",FACE,{"disambiguationData":[OSD([subQ17,subQ16,subQ15,subQ14,subQ13,subQ12,subQ11,subQ10,subQ9,subQ8,subQ7,subQ6,subQ5,subQ4,subQ3,subQ2,subQ1,subQ0])],"isStart":false})],"blendedInto":[makeQuery(id+"F12.opExtrude","CAP_FACE",FACE,{"disambiguationData":[OSD([subQ17,subQ16,subQ15,subQ14,subQ13,subQ12,subQ11,subQ10,subQ9,subQ8,subQ7,subQ6,subQ5,subQ4,subQ3,subQ2,subQ1,subQ0])],"isStart":false})]})])],"isStart":false}),makeQuery(id+"F14.opExtrude","CAP_FACE",FACE,{"disambiguationData":[OSD([subQ17,subQ16,subQ15,subQ14,subQ13,subQ12,subQ11,subQ10,subQ9,subQ8,subQ7,subQ6,subQ5,subQ4,subQ3,subQ2,subQ1,subQ0])],"isStart":false})],"blendedInto":[makeQuery(id+"F14.opExtrude","CAP_FACE",FACE,{"disambiguationData":[OSD([subQ17,subQ16,subQ15,subQ14,subQ13,subQ12,subQ11,subQ10,subQ9,subQ8,subQ7,subQ6,subQ5,subQ4,subQ3,subQ2,subQ1,subQ0])],"isStart":false})]})])],"isStart":false}),makeQuery(id+"F16.opExtrude","CAP_FACE",FACE,{"disambiguationData":[OSD([subQ17,subQ16,subQ15,subQ14,subQ13,subQ12,subQ11,subQ10,subQ9,subQ8,subQ7,subQ6,subQ5,subQ4,subQ3,subQ2,subQ1,subQ0])],"isStart":false})],"blendedInto":[makeQuery(id+"F16.opExtrude","CAP_FACE",FACE,{"disambiguationData":[OSD([subQ17,subQ16,subQ15,subQ14,subQ13,subQ12,subQ11,subQ10,subQ9,subQ8,subQ7,subQ6,subQ5,subQ4,subQ3,subQ2,subQ1,subQ0])],"isStart":false})]})])],"isStart":false}),makeQuery(id+"F18.opExtrude","CAP_FACE",FACE,{"disambiguationData":[OSD([subQ17,subQ16,subQ15,subQ14,subQ13,subQ12,subQ11,subQ10,subQ9,subQ8,subQ7,subQ6,subQ5,subQ4,subQ3,subQ2,subQ1,subQ0])],"isStart":false})],"blendedInto":[makeQuery(id+"F18.opExtrude","CAP_FACE",FACE,{"disambiguationData":[OSD([subQ17,subQ16,subQ15,subQ14,subQ13,subQ12,subQ11,subQ10,subQ9,subQ8,subQ7,subQ6,subQ5,subQ4,subQ3,subQ2,subQ1,subQ0])],"isStart":false})]})])],"isStart":false}),makeQuery(id+"F20.opExtrude","CAP_FACE",FACE,{"disambiguationData":[OSD([subQ17,subQ16,subQ15,subQ14,subQ13,subQ12,subQ11,subQ10,subQ9,subQ8,subQ7,subQ6,subQ5,subQ4,subQ3,subQ2,subQ1,subQ0])],"isStart":false})],"blendedInto":[makeQuery(id+"F20.opExtrude","CAP_FACE",FACE,{"disambiguationData":[OSD([subQ17,subQ16,subQ15,subQ14,subQ13,subQ12,subQ11,subQ10,subQ9,subQ8,subQ7,subQ6,subQ5,subQ4,subQ3,subQ2,subQ1,subQ0])],"isStart":false})]})])],"isStart":false});}
            var Q5;
            {var subQ0=sQuery(id+"F0.wireOp",EDGE,"E3.4");var subQ1=sQuery(id+"F0.wireOp",EDGE,"E3.3");var subQ2=sQuery(id+"F0.wireOp",EDGE,"E3.2");var subQ3=sQuery(id+"F0.wireOp",EDGE,"E3.1");var subQ4=sQuery(id+"F0.wireOp",EDGE,"E2.5");var subQ5=sQuery(id+"F0.wireOp",EDGE,"E2.4");var subQ6=sQuery(id+"F0.wireOp",EDGE,"E2.3");var subQ7=sQuery(id+"F0.wireOp",EDGE,"E2.2");var subQ8=sQuery(id+"F0.wireOp",EDGE,"E1.4");var subQ9=sQuery(id+"F0.wireOp",EDGE,"E1.3");var subQ10=sQuery(id+"F0.wireOp",EDGE,"E1.2");var subQ11=sQuery(id+"F0.wireOp",EDGE,"E1.1");var subQ12=sQuery(id+"F0.wireOp",EDGE,"E0.5");var subQ13=sQuery(id+"F0.wireOp",EDGE,"E0.4");var subQ14=sQuery(id+"F0.wireOp",EDGE,"E0.3");var subQ15=sQuery(id+"F0.wireOp",EDGE,"E0.2");var subQ16=sQuery(id+"F0.wireOp",EDGE,"E0.1");var subQ17=sQuery(id+"F0.wireOp",EDGE,"E0.0");Q5=makeQuery(id+"F22.opExtrude","CAP_EDGE",EDGE,{"disambiguationData":[OSD([subQ17,subQ16,subQ15,subQ14,subQ13,subQ12,subQ11,subQ10,subQ9,subQ8,subQ7,subQ6,subQ5,subQ4,subQ3,subQ2,subQ1,subQ0]),TDD([makeQuery(id+"F21.opChamfer","BLEND_EDGE",EDGE,{"blendedFrom":[makeQuery(id+"F20.opExtrude","CAP_EDGE",EDGE,{"disambiguationData":[OSD([subQ17,subQ16,subQ15,subQ14,subQ13,subQ12,subQ11,subQ10,subQ9,subQ8,subQ7,subQ6,subQ5,subQ4,subQ3,subQ2,subQ1,subQ0]),TDD([makeQuery(id+"F19.opChamfer","BLEND_EDGE",EDGE,{"blendedFrom":[makeQuery(id+"F18.opExtrude","CAP_EDGE",EDGE,{"disambiguationData":[OSD([subQ17,subQ16,subQ15,subQ14,subQ13,subQ12,subQ11,subQ10,subQ9,subQ8,subQ7,subQ6,subQ5,subQ4,subQ3,subQ2,subQ1,subQ0]),TDD([makeQuery(id+"F17.opChamfer","BLEND_EDGE",EDGE,{"blendedFrom":[makeQuery(id+"F16.opExtrude","CAP_EDGE",EDGE,{"disambiguationData":[OSD([subQ17,subQ16,subQ15,subQ14,subQ13,subQ12,subQ11,subQ10,subQ9,subQ8,subQ7,subQ6,subQ5,subQ4,subQ3,subQ2,subQ1,subQ0]),TDD([makeQuery(id+"F15.opChamfer","BLEND_EDGE",EDGE,{"blendedFrom":[makeQuery(id+"F14.opExtrude","CAP_EDGE",EDGE,{"disambiguationData":[OSD([subQ17,subQ16,subQ15,subQ14,subQ13,subQ12,subQ11,subQ10,subQ9,subQ8,subQ7,subQ6,subQ5,subQ4,subQ3,subQ2,subQ1,subQ0]),TDD([makeQuery(id+"F13.opChamfer","BLEND_EDGE",EDGE,{"blendedFrom":[makeQuery(id+"F12.opExtrude","CAP_EDGE",EDGE,{"disambiguationData":[OSD([subQ17,subQ16,subQ15,subQ14,subQ13,subQ12,subQ11,subQ10,subQ9,subQ8,subQ7,subQ6,subQ5,subQ4,subQ3,subQ2,subQ1,subQ0]),TDD([makeQuery(id+"F11.opChamfer","BLEND_EDGE",EDGE,{"blendedFrom":[makeQuery(id+"F9.opExtrude","CAP_EDGE",EDGE,{"disambiguationData":[OSD([subQ17])],"isStart":false}),makeQuery(id+"F9.opExtrude","CAP_FACE",FACE,{"disambiguationData":[OSD([subQ17,subQ16,subQ15,subQ14,subQ13,subQ12,subQ11,subQ10,subQ9,subQ8,subQ7,subQ6,subQ5,subQ4,subQ3,subQ2,subQ1,subQ0])],"isStart":false})],"blendedInto":[makeQuery(id+"F9.opExtrude","CAP_FACE",FACE,{"disambiguationData":[OSD([subQ17,subQ16,subQ15,subQ14,subQ13,subQ12,subQ11,subQ10,subQ9,subQ8,subQ7,subQ6,subQ5,subQ4,subQ3,subQ2,subQ1,subQ0])],"isStart":false})]})])],"isStart":false}),makeQuery(id+"F12.opExtrude","CAP_FACE",FACE,{"disambiguationData":[OSD([subQ17,subQ16,subQ15,subQ14,subQ13,subQ12,subQ11,subQ10,subQ9,subQ8,subQ7,subQ6,subQ5,subQ4,subQ3,subQ2,subQ1,subQ0])],"isStart":false})],"blendedInto":[makeQuery(id+"F12.opExtrude","CAP_FACE",FACE,{"disambiguationData":[OSD([subQ17,subQ16,subQ15,subQ14,subQ13,subQ12,subQ11,subQ10,subQ9,subQ8,subQ7,subQ6,subQ5,subQ4,subQ3,subQ2,subQ1,subQ0])],"isStart":false})]})])],"isStart":false}),makeQuery(id+"F14.opExtrude","CAP_FACE",FACE,{"disambiguationData":[OSD([subQ17,subQ16,subQ15,subQ14,subQ13,subQ12,subQ11,subQ10,subQ9,subQ8,subQ7,subQ6,subQ5,subQ4,subQ3,subQ2,subQ1,subQ0])],"isStart":false})],"blendedInto":[makeQuery(id+"F14.opExtrude","CAP_FACE",FACE,{"disambiguationData":[OSD([subQ17,subQ16,subQ15,subQ14,subQ13,subQ12,subQ11,subQ10,subQ9,subQ8,subQ7,subQ6,subQ5,subQ4,subQ3,subQ2,subQ1,subQ0])],"isStart":false})]})])],"isStart":false}),makeQuery(id+"F16.opExtrude","CAP_FACE",FACE,{"disambiguationData":[OSD([subQ17,subQ16,subQ15,subQ14,subQ13,subQ12,subQ11,subQ10,subQ9,subQ8,subQ7,subQ6,subQ5,subQ4,subQ3,subQ2,subQ1,subQ0])],"isStart":false})],"blendedInto":[makeQuery(id+"F16.opExtrude","CAP_FACE",FACE,{"disambiguationData":[OSD([subQ17,subQ16,subQ15,subQ14,subQ13,subQ12,subQ11,subQ10,subQ9,subQ8,subQ7,subQ6,subQ5,subQ4,subQ3,subQ2,subQ1,subQ0])],"isStart":false})]})])],"isStart":false}),makeQuery(id+"F18.opExtrude","CAP_FACE",FACE,{"disambiguationData":[OSD([subQ17,subQ16,subQ15,subQ14,subQ13,subQ12,subQ11,subQ10,subQ9,subQ8,subQ7,subQ6,subQ5,subQ4,subQ3,subQ2,subQ1,subQ0])],"isStart":false})],"blendedInto":[makeQuery(id+"F18.opExtrude","CAP_FACE",FACE,{"disambiguationData":[OSD([subQ17,subQ16,subQ15,subQ14,subQ13,subQ12,subQ11,subQ10,subQ9,subQ8,subQ7,subQ6,subQ5,subQ4,subQ3,subQ2,subQ1,subQ0])],"isStart":false})]})])],"isStart":false}),makeQuery(id+"F20.opExtrude","CAP_FACE",FACE,{"disambiguationData":[OSD([subQ17,subQ16,subQ15,subQ14,subQ13,subQ12,subQ11,subQ10,subQ9,subQ8,subQ7,subQ6,subQ5,subQ4,subQ3,subQ2,subQ1,subQ0])],"isStart":false})],"blendedInto":[makeQuery(id+"F20.opExtrude","CAP_FACE",FACE,{"disambiguationData":[OSD([subQ17,subQ16,subQ15,subQ14,subQ13,subQ12,subQ11,subQ10,subQ9,subQ8,subQ7,subQ6,subQ5,subQ4,subQ3,subQ2,subQ1,subQ0])],"isStart":false})]})])],"isStart":false});}
            chamfer(context, id + "F23", {"entities" : qUnion([Q0, Q1, Q2, Q3, Q4, Q5]), "width" : 5.08 * mm, "tangentPropagation" : true});
        }
        {
            var Q0;
            Q0=makeQuery(id+"F22.opExtrude","CAP_FACE",FACE,{"disambiguationData":[OSD([sQuery(id+"F0.wireOp",EDGE,"E0.0"),sQuery(id+"F0.wireOp",EDGE,"E0.1"),sQuery(id+"F0.wireOp",EDGE,"E0.2"),sQuery(id+"F0.wireOp",EDGE,"E0.3"),sQuery(id+"F0.wireOp",EDGE,"E0.4"),sQuery(id+"F0.wireOp",EDGE,"E0.5"),sQuery(id+"F0.wireOp",EDGE,"E1.1"),sQuery(id+"F0.wireOp",EDGE,"E1.2"),sQuery(id+"F0.wireOp",EDGE,"E1.3"),sQuery(id+"F0.wireOp",EDGE,"E1.4"),sQuery(id+"F0.wireOp",EDGE,"E2.2"),sQuery(id+"F0.wireOp",EDGE,"E2.3"),sQuery(id+"F0.wireOp",EDGE,"E2.4"),sQuery(id+"F0.wireOp",EDGE,"E2.5"),sQuery(id+"F0.wireOp",EDGE,"E3.1"),sQuery(id+"F0.wireOp",EDGE,"E3.2"),sQuery(id+"F0.wireOp",EDGE,"E3.3"),sQuery(id+"F0.wireOp",EDGE,"E3.4")])],"isStart":false});
            extrude(context, id + "F24", {"entities" : qUnion([Q0]), "operationType" : NewBodyOperationType.ADD, "depth" : 25.4 * mm});
        }
    });
